FCSTD DOCUMENT  (FreeCAD 0.18.4R)
Label: SubEnclosure
License: All rights reserved
LicenseURL: http://en.wikipedia.org/wiki/All_rights_reserved
objects: Part::Feature×281, Sketcher::SketchObject×109, PartDesign::Pocket×59, PartDesign::Pad×44, PartDesign::Body×26, PartDesign::Plane×20, PartDesign::Chamfer×16, PartDesign::Mirrored×12, PartDesign::Fillet×7, PartDesign::PolarPattern×5, Part::Part2DObjectPython×4, Part::Extrusion×4, Part::Cut×4, PartDesign::Revolution×3, Part::MultiFuse×3, PartDesign::FeatureBase×2, App::DocumentObjectGroup×2, PartDesign::Line×1, Mesh::Feature×1, Part::Box×1, +1 more types
note: 708 computed .brp shape members not serialized (recipe doc carries the construction recipe); baked Part::Feature solids carry a one-line shape summary decoded from their .brp

FEATURE [Sketcher::SketchObject] Sketch
  MapMode = 5
  Support = -> [XY_Plane]
  sketch-geometry (38):
    g0: LineSegment StartX=-115 StartY=90 StartZ=0 EndX=115 EndY=90 EndZ=0
    g1: LineSegment StartX=-115 StartY=-90 StartZ=0 EndX=115 EndY=-90 EndZ=0
    g2: LineSegment StartX=120 StartY=85 StartZ=0 EndX=120 EndY=-85 EndZ=0
    g3: LineSegment StartX=-120 StartY=85 StartZ=0 EndX=-120 EndY=-85 EndZ=0
    g4: ArcOfCircle CenterX=115 CenterY=85 CenterZ=0 NormalX=0 NormalY=0 NormalZ=1 AngleXU=0 Radius=5 StartAngle=-9e-16 EndAngle=1.5708
    g5: ArcOfCircle CenterX=115 CenterY=-85 CenterZ=0 NormalX=0 NormalY=0 NormalZ=1 AngleXU=0 Radius=5 StartAngle=4.71239 EndAngle=6.28319
    g6: ArcOfCircle CenterX=-115 CenterY=-85 CenterZ=0 NormalX=0 NormalY=0 NormalZ=1 AngleXU=0 Radius=5 StartAngle=3.14159 EndAngle=4.71239
    g7: ArcOfCircle CenterX=-115 CenterY=85 CenterZ=0 NormalX=0 NormalY=0 NormalZ=1 AngleXU=0 Radius=5 StartAngle=1.5708 EndAngle=3.14159
    g8: Circle CenterX=110 CenterY=80 CenterZ=0 NormalX=0 NormalY=0 NormalZ=1 AngleXU=0 Radius=3.25
    g9: Circle CenterX=-110 CenterY=80 CenterZ=0 NormalX=0 NormalY=0 NormalZ=1 AngleXU=0 Radius=3.25
    g10: Circle CenterX=110 CenterY=-80 CenterZ=0 NormalX=0 NormalY=0 NormalZ=1 AngleXU=0 Radius=3.25
    g11: Circle CenterX=-110 CenterY=-80 CenterZ=0 NormalX=0 NormalY=0 NormalZ=1 AngleXU=0 Radius=3.25
    g12: ArcOfCircle CenterX=110 CenterY=80 CenterZ=0 NormalX=0 NormalY=0 NormalZ=1 AngleXU=0 Radius=7 StartAngle=3.43134 EndAngle=4.42264
    g13: ArcOfCircle CenterX=106 CenterY=66.5836 CenterZ=0 NormalX=0 NormalY=0 NormalZ=1 AngleXU=0 Radius=7 StartAngle=-9e-16 EndAngle=1.28104
    g14: ArcOfCircle CenterX=96.5836 CenterY=76 CenterZ=0 NormalX=0 NormalY=0 NormalZ=1 AngleXU=0 Radius=7 StartAngle=0.289752 EndAngle=1.5708
    g15: LineSegment StartX=-96.5836 StartY=83 StartZ=0 EndX=96.5836 EndY=83 EndZ=0
    g16: ArcOfCircle CenterX=110 CenterY=-80 CenterZ=0 NormalX=0 NormalY=0 NormalZ=1 AngleXU=0 Radius=7 StartAngle=1.86055 EndAngle=2.85184
    g17: ArcOfCircle CenterX=-110 CenterY=-80 CenterZ=0 NormalX=0 NormalY=0 NormalZ=1 AngleXU=0 Radius=7 StartAngle=0.289752 EndAngle=1.28104
    g18: ArcOfCircle CenterX=-110 CenterY=80 CenterZ=0 NormalX=0 NormalY=0 NormalZ=1 AngleXU=0 Radius=7 StartAngle=5.00214 EndAngle=5.99343
    g19: ArcOfCircle CenterX=-96.5836 CenterY=76 CenterZ=0 NormalX=0 NormalY=0 NormalZ=1 AngleXU=0 Radius=7 StartAngle=1.5708 EndAngle=2.85184
    g20: ArcOfCircle CenterX=106 CenterY=-66.5836 CenterZ=0 NormalX=0 NormalY=0 NormalZ=1 AngleXU=0 Radius=7 StartAngle=5.00214 EndAngle=6.28319
    g21: ArcOfCircle CenterX=96.5836 CenterY=-76 CenterZ=0 NormalX=0 NormalY=0 NormalZ=1 AngleXU=0 Radius=7 StartAngle=4.71239 EndAngle=5.99343
    g22: ArcOfCircle CenterX=-96.5836 CenterY=-76 CenterZ=0 NormalX=0 NormalY=0 NormalZ=1 AngleXU=0 Radius=7 StartAngle=3.43134 EndAngle=4.71239
    g23: ArcOfCircle CenterX=-106 CenterY=-66.5836 CenterZ=0 NormalX=0 NormalY=0 NormalZ=1 AngleXU=0 Radius=7 StartAngle=3.14159 EndAngle=4.42264
    g24: ArcOfCircle CenterX=-106 CenterY=66.5836 CenterZ=0 NormalX=0 NormalY=0 NormalZ=1 AngleXU=0 Radius=7 StartAngle=1.86055 EndAngle=3.14159
    g25: LineSegment StartX=-96.5836 StartY=-83 StartZ=0 EndX=96.5836 EndY=-83 EndZ=0
    g26: Circle CenterX=110 CenterY=0 CenterZ=0 NormalX=0 NormalY=0 NormalZ=1 AngleXU=0 Radius=3.25
    g27: Circle CenterX=-110 CenterY=0 CenterZ=0 NormalX=0 NormalY=0 NormalZ=1 AngleXU=0 Radius=3.25
    g28: ArcOfCircle CenterX=110 CenterY=0 CenterZ=0 NormalX=0 NormalY=0 NormalZ=1 AngleXU=0 Radius=7 StartAngle=1.86055 EndAngle=4.42264
    g29: ArcOfCircle CenterX=106 CenterY=-13.4164 CenterZ=0 NormalX=0 NormalY=0 NormalZ=1 AngleXU=0 Radius=7 StartAngle=0 EndAngle=1.28104
    g30: ArcOfCircle CenterX=106 CenterY=13.4164 CenterZ=0 NormalX=0 NormalY=0 NormalZ=1 AngleXU=0 Radius=7 StartAngle=5.00214 EndAngle=6.28319
    g31: ArcOfCircle CenterX=-110 CenterY=0 CenterZ=0 NormalX=0 NormalY=0 NormalZ=1 AngleXU=0 Radius=7 StartAngle=5.00214 EndAngle=7.56423
    g32: ArcOfCircle CenterX=-106 CenterY=13.4164 CenterZ=0 NormalX=0 NormalY=0 NormalZ=1 AngleXU=0 Radius=7 StartAngle=3.14159 EndAngle=4.42264
    g33: ArcOfCircle CenterX=-106 CenterY=-13.4164 CenterZ=0 NormalX=0 NormalY=0 NormalZ=1 AngleXU=0 Radius=7 StartAngle=1.86055 EndAngle=3.14159
    g34: LineSegment StartX=113 StartY=66.5836 StartZ=0 EndX=113 EndY=13.4164 EndZ=0
    g35: LineSegment StartX=113 StartY=-13.4164 StartZ=0 EndX=113 EndY=-66.5836 EndZ=0
    g36: LineSegment StartX=-113 StartY=-66.5836 StartZ=0 EndX=-113 EndY=-13.4164 EndZ=0
    g37: LineSegment StartX=-113 StartY=13.4164 StartZ=0 EndX=-113 EndY=66.5836 EndZ=0
  constraints (92):
    c: Symmetric(g0,g0,g-2)
    c: Equal(g1,g0)
    c: Symmetric(g1,g1,g-2)
    c: Symmetric(g2,g2,g-1)
    c: Symmetric(g3,g3,g-1)
    c: Equal(g3,g2)
    c: Symmetric(g0,g1,g-1)
    c: Symmetric(g2,g3,g-2)
    c: Coincident(g4,g2)
    c: Tangent(g7,g0) = 1.5708
    c: Tangent(g7,g3) = -1.5708
    c: Tangent(g0,g4) = 1.5708
    c: Coincident(g5,g1)
    c: Tangent(g5,g2) = 1.5708
    c: Coincident(g3,g6)
    c: Tangent(g6,g1) = -1.5708
    c: Distance(g3,g2) = 240
    c: Radius(g4) = 5
    c: Distance(g0,g1) = 180
    c: Diameter(g8) = 6.5
    c: DistanceY(g8,g0) = 10
    c: DistanceX(g8,g2) = 10
    c: Equal(g9,g8)
    c: Symmetric(g9,g8,g-2)
    c: Equal(g11,g10)
    c: Equal(g10,g8)
    c: Symmetric(g10,g8,g-1)
    c: Symmetric(g11,g10,g-2)
    c: Coincident(g12,g8)
    c: Tangent(g13,g12) = 1.5708
    c: Radius(g12) = 7
    c: DistanceX(g13,g2) = 7
    c: Tangent(g14,g12) = 1.5708
    c: DistanceY(g14,g0) = 7
    c: Equal(g13,g12)
    c: Equal(g12,g14)
    c: Symmetric(g15,g15,g-2)
    c: Tangent(g14,g15) = 1.5708
    c: Coincident(g16,g10)
    c: Coincident(g17,g11)
    c: Coincident(g18,g9)
    c: Equal(g16,g12)
    c: Equal(g17,g16)
    c: Equal(g18,g12)
    c: Tangent(g19,g18) = 1.5708
    c: Tangent(g19,g15) = 1.5708
    c: Tangent(g22,g17) = 1.5708
    c: Tangent(g17,g23) = 1.5708
    c: Symmetric(g13,g24,g-2)
    c: Tangent(g24,g18) = 1.5708
    c: Horizontal(g25)
    c: Tangent(g16,g20) = 1.5708
    c: Symmetric(g21,g14,g-1)
    c: Tangent(g21,g25) = -1.5708
    c: Tangent(g22,g25) = -1.5708
    c: Equal(g22,g23)
    c: Equal(g23,g21)
    c: Equal(g21,g20)
    c: Coincident(g16,g21)
    c: PointOnObject(g26,g-1)
    c: PointOnObject(g27,g-1)
    c: Equal(g27,g26)
    c: Equal(g26,g8)
    c: Vertical(g26,g8)
    c: Vertical(g27,g9)
    c: Coincident(g28,g26)
    c: Coincident(g31,g27)
    c: Vertical(g34)
    c: Vertical(g35)
    c: Equal(g34,g35)
    c: Tangent(g34,g13) = 1.5708
    c: Tangent(g35,g20) = 1.5708
    c: Tangent(g35,g29) = 1.5708
    c: Tangent(g34,g30) = 1.5708
    c: Tangent(g29,g28) = 1.5708
    c: Tangent(g28,g30) = 1.5708
    c: Equal(g28,g12)
    c: Equal(g29,g30)
    c: Equal(g30,g13)
    c: Vertical(g29,g30)
    c: Equal(g33,g29)
    c: Equal(g32,g30)
    c: Equal(g31,g28)
    c: Tangent(g32,g37) = 1.5708
    c: Vertical(g37)
    c: Tangent(g36,g33) = 1.5708
    c: Tangent(g36,g23) = 1.5708
    c: Vertical(g36)
    c: Vertical(g33,g32)
    c: Tangent(g33,g31) = 1.5708
    c: Tangent(g31,g32) = 1.5708
    c: Tangent(g37,g24) = 1.5708
FEATURE [PartDesign::Pad] Pad
  Length = 200
  Length2 = 100
  Profile = -> Sketch
  Type = 0
FEATURE [PartDesign::Line] DatumLine
  AttacherType = Attacher::AttachEngineLine
  AttachmentOffset = pos=(0,100,0) rot=(0,0,1;0rad)
  MapMode = 29
  Placement = pos=(0,2.22e-14,100) rot=(0,0.707107,0.707107;3.14159rad)
  Support = -> [Y_Axis]
FEATURE [PartDesign::Plane] DatumPlane
  Length = 284.9
  MapMode = 5
  Placement = pos=(0,-90,0) rot=(1,0,0;1.5708rad)
  ResizeMode = 0
  Support = -> [Pad]
  Width = 254.9
FEATURE [Sketcher::SketchObject] Sketch001
  ExternalGeometry = -> [Pad]
  MapMode = 5
  Placement = pos=(0,-90,0) rot=(1,0,0;1.5708rad)
  Support = -> [DatumPlane]
  sketch-geometry (7):
    g0: Circle CenterX=0 CenterY=100 CenterZ=0 NormalX=0 NormalY=0 NormalZ=1 AngleXU=0 Radius=60.5
    g1: LineSegment [constr] StartX=-48.7904 StartY=51.2096 StartZ=0 EndX=48.7904 EndY=148.79 EndZ=0
    g2: LineSegment [constr] StartX=-48.7904 StartY=148.79 StartZ=0 EndX=48.7904 EndY=51.2096 EndZ=0
    g3: Circle CenterX=-48.7904 CenterY=148.79 CenterZ=0 NormalX=0 NormalY=0 NormalZ=1 AngleXU=0 Radius=2.6
    g4: Circle CenterX=48.7904 CenterY=148.79 CenterZ=0 NormalX=0 NormalY=0 NormalZ=1 AngleXU=0 Radius=2.6
    g5: Circle CenterX=48.7904 CenterY=51.2096 CenterZ=0 NormalX=0 NormalY=0 NormalZ=1 AngleXU=0 Radius=2.6
    g6: Circle CenterX=-48.7904 CenterY=51.2096 CenterZ=0 NormalX=0 NormalY=0 NormalZ=1 AngleXU=0 Radius=2.6
  constraints (17):
    c: Diameter(g0) = 121
    c: Perpendicular(g2,g1)
    c: Symmetric(g1,g1,g0)
    c: Equal(g2,g1)
    c: Symmetric(g2,g2,g0)
    c: Angle(g-4,g1) = 0.785398
    c: Distance(g1) = 138
    c: Coincident(g3,g2)
    c: Coincident(g4,g1)
    c: Coincident(g5,g2)
    c: Coincident(g6,g1)
    c: Diameter(g6) = 5.2
    c: Equal(g3,g4)
    c: Equal(g4,g5)
    c: Equal(g5,g6)
    c: PointOnObject(g0,g-2)
    c: DistanceY(g-4,g0) = 100
FEATURE [PartDesign::Pocket] Pocket
  BaseFeature = -> Pad
  Length = 5
  Length2 = 100
  Profile = -> Sketch001
  Type = 1
FEATURE [Sketcher::SketchObject] Sketch002
  ExternalGeometry = -> [Pocket]
  MapMode = 5
  Placement = pos=(0,0,0) rot=(0.57735,0.57735,0.57735;2.0944rad)
  Support = -> [YZ_Plane]
  expr: Constraints[4] = (200 - 156) / 2
  sketch-geometry (4):
    g0: LineSegment StartX=-90 StartY=200 StartZ=0 EndX=-93.2142 EndY=188.312 EndZ=0
    g1: LineSegment StartX=-90 StartY=178 StartZ=0 EndX=-90 EndY=200 EndZ=0
    g2: LineSegment [constr] StartX=-90 StartY=178 StartZ=0 EndX=-97.6604 EndY=184.428 EndZ=0
    g3: ArcOfCircle CenterX=-83.5721 CenterY=185.66 CenterZ=0 NormalX=0 NormalY=0 NormalZ=1 AngleXU=0 Radius=10 StartAngle=2.87323 EndAngle=4.01425
  constraints (12):
    c: Coincident(g0,g1)
    c: Vertical(g1)
    c: DistanceX(g0,g-1) = 90
    c: DistanceY(g-1,g0) = 200
    c: DistanceY(g1,g1) = 22
    c: Coincident(g2,g1)
    c: Angle(g2,g-2) = 2.26893
    c: Distance(g2) = 10
    c: Coincident(g3,g1)
    c: Tangent(g3,g2)
    c: Radius(g3) = 10
    c: Tangent(g3,g0) = -1.5708
FEATURE [PartDesign::Revolution] Revolution
  Angle = 360
  Axis = (1e-16,1,-2e-16)
  Base = (0,2.22e-14,100)
  BaseFeature = -> Pocket
  Profile = -> Sketch002
  ReferenceAxis = -> DatumLine
FEATURE [PartDesign::Plane] DatumPlane001
  Length = 284.9
  MapMode = 5
  Placement = pos=(0,-83,0) rot=(0,0.707107,0.707107;3.14159rad)
  ResizeMode = 0
  Support = -> [Revolution]
  Width = 254.9
FEATURE [Sketcher::SketchObject] Sketch003
  ExternalGeometry = -> [Revolution]
  MapMode = 5
  Placement = pos=(0,-83,0) rot=(0,0.707107,0.707107;3.14159rad)
  Support = -> [DatumPlane001]
  sketch-geometry (31):
    g0: LineSegment StartX=51.2441 StartY=144.54 StartZ=0 EndX=53.6978 EndY=148.79 EndZ=0
    g1: LineSegment StartX=53.6978 StartY=148.79 StartZ=0 EndX=51.2441 EndY=153.04 EndZ=0
    g2: LineSegment StartX=51.2441 StartY=153.04 StartZ=0 EndX=46.3366 EndY=153.04 EndZ=0
    g3: LineSegment StartX=46.3366 StartY=153.04 StartZ=0 EndX=43.8829 EndY=148.79 EndZ=0
    g4: LineSegment StartX=43.8829 StartY=148.79 StartZ=0 EndX=46.3366 EndY=144.54 EndZ=0
    g5: LineSegment StartX=46.3366 StartY=144.54 StartZ=0 EndX=51.2441 EndY=144.54 EndZ=0
    g6: Circle [constr] CenterX=48.7904 CenterY=148.79 CenterZ=0 NormalX=0 NormalY=0 NormalZ=1 AngleXU=0 Radius=4.90748
    g7: LineSegment StartX=51.2441 StartY=46.9596 StartZ=0 EndX=53.6978 EndY=51.2096 EndZ=0
    g8: LineSegment StartX=53.6978 StartY=51.2096 StartZ=0 EndX=51.2441 EndY=55.4596 EndZ=0
    g9: LineSegment StartX=51.2441 StartY=55.4596 StartZ=0 EndX=46.3366 EndY=55.4596 EndZ=0
    g10: LineSegment StartX=46.3366 StartY=55.4596 StartZ=0 EndX=43.8829 EndY=51.2096 EndZ=0
    g11: LineSegment StartX=43.8829 StartY=51.2096 StartZ=0 EndX=46.3366 EndY=46.9596 EndZ=0
    g12: LineSegment StartX=46.3366 StartY=46.9596 StartZ=0 EndX=51.2441 EndY=46.9596 EndZ=0
    g13: Circle [constr] CenterX=48.7904 CenterY=51.2096 CenterZ=0 NormalX=0 NormalY=0 NormalZ=1 AngleXU=0 Radius=4.90748
    g14: LineSegment StartX=-46.3366 StartY=46.9596 StartZ=0 EndX=-43.8829 EndY=51.2096 EndZ=0
    g15: LineSegment StartX=-43.8829 StartY=51.2096 StartZ=0 EndX=-46.3366 EndY=55.4596 EndZ=0
    g16: LineSegment StartX=-46.3366 StartY=55.4596 StartZ=0 EndX=-51.2441 EndY=55.4596 EndZ=0
    g17: LineSegment StartX=-51.2441 StartY=55.4596 StartZ=0 EndX=-53.6978 EndY=51.2096 EndZ=0
    g18: LineSegment StartX=-53.6978 StartY=51.2096 StartZ=0 EndX=-51.2441 EndY=46.9596 EndZ=0
    g19: LineSegment StartX=-51.2441 StartY=46.9596 StartZ=0 EndX=-46.3366 EndY=46.9596 EndZ=0
    g20: Circle [constr] CenterX=-48.7904 CenterY=51.2096 CenterZ=0 NormalX=0 NormalY=0 NormalZ=1 AngleXU=0 Radius=4.90748
    g21: LineSegment StartX=-46.3366 StartY=144.54 StartZ=0 EndX=-43.8829 EndY=148.79 EndZ=0
    g22: LineSegment StartX=-43.8829 StartY=148.79 StartZ=0 EndX=-46.3366 EndY=153.04 EndZ=0
    g23: LineSegment StartX=-46.3366 StartY=153.04 StartZ=0 EndX=-51.2441 EndY=153.04 EndZ=0
    g24: LineSegment StartX=-51.2441 StartY=153.04 StartZ=0 EndX=-53.6978 EndY=148.79 EndZ=0
    g25: LineSegment StartX=-53.6978 StartY=148.79 StartZ=0 EndX=-51.2441 EndY=144.54 EndZ=0
    g26: LineSegment StartX=-51.2441 StartY=144.54 StartZ=0 EndX=-46.3366 EndY=144.54 EndZ=0
    g27: Circle [constr] CenterX=-48.7904 CenterY=148.79 CenterZ=0 NormalX=0 NormalY=0 NormalZ=1 AngleXU=0 Radius=4.90748
    g28: Circle CenterX=0 CenterY=100 CenterZ=0 NormalX=0 NormalY=0 NormalZ=1 AngleXU=0 Radius=60.5
    g29: Circle CenterX=0 CenterY=100 CenterZ=0 NormalX=0 NormalY=0 NormalZ=1 AngleXU=0 Radius=79
    g30: LineSegment [constr] StartX=-100 StartY=100 StartZ=0 EndX=100 EndY=100 EndZ=0
  constraints (87):
    c: Coincident(g17,g18)
    c: Coincident(g25,g24)
    c: Coincident(g18,g19)
    c: Coincident(g16,g17)
    c: Coincident(g26,g25)
    c: Coincident(g23,g24)
    c: Coincident(g19,g14)
    c: Coincident(g16,g15)
    c: Coincident(g21,g26)
    c: Coincident(g23,g22)
    c: Coincident(g14,g15)
    c: Coincident(g22,g21)
    c: Coincident(g10,g11)
    c: Coincident(g3,g4)
    c: Coincident(g11,g12)
    c: Coincident(g9,g10)
    c: Coincident(g5,g4)
    c: Coincident(g3,g2)
    c: Coincident(g7,g12)
    c: Coincident(g8,g9)
    c: Coincident(g5,g0)
    c: Coincident(g2,g1)
    c: Coincident(g7,g8)
    c: Coincident(g1,g0)
    c: Coincident(g28,g29)
    c: Coincident(g28,g-7)
    c: Equal(g28,g-7)
    c: Coincident(g6,g-8)
    c: Equal(g0,g5)
    c: Equal(g5,g4)
    c: Equal(g4,g3)
    c: Equal(g3,g2)
    c: Equal(g2,g1)
    c: Horizontal(g5)
    c: PointOnObject(g0,g6)
    c: PointOnObject(g1,g6)
    c: PointOnObject(g2,g6)
    c: PointOnObject(g3,g6)
    c: PointOnObject(g0,g6)
    c: PointOnObject(g4,g6)
    c: DistanceY(g0,g1) = 8.5
    c: Diameter(g29) = 158
    c: Equal(g27,g20)
    c: Equal(g20,g13)
    c: Equal(g13,g6)
    c: Symmetric(g27,g6,g-2)
    c: PointOnObject(g21,g27)
    c: PointOnObject(g22,g27)
    c: PointOnObject(g23,g27)
    c: PointOnObject(g24,g27)
    c: PointOnObject(g25,g27)
    c: PointOnObject(g21,g27)
    c: Horizontal(g26)
    c: Equal(g26,g25)
    c: Equal(g25,g24)
    c: Equal(g24,g23)
    c: Equal(g23,g22)
    c: Equal(g22,g21)
    c: Horizontal(g30)
    c: Symmetric(g30,g30,g28)
    c: DistanceX(g30,g30) = 200
    c: Symmetric(g13,g6,g30)
    c: PointOnObject(g7,g13)
    c: PointOnObject(g7,g13)
    c: PointOnObject(g8,g13)
    c: PointOnObject(g9,g13)
    c: PointOnObject(g10,g13)
    c: PointOnObject(g11,g13)
    c: Equal(g12,g11)
    c: Equal(g11,g10)
    c: Equal(g10,g9)
    c: Equal(g9,g8)
    c: Equal(g8,g7)
    c: Horizontal(g12)
    c: Equal(g18,g17)
    c: Equal(g17,g16)
    c: Equal(g16,g15)
    c: Equal(g15,g14)
    c: Equal(g14,g19)
    c: PointOnObject(g15,g20)
    c: PointOnObject(g14,g20)
    c: PointOnObject(g14,g20)
    c: PointOnObject(g18,g20)
    c: PointOnObject(g17,g20)
    c: PointOnObject(g16,g20)
    c: Symmetric(g20,g27,g30)
    c: Horizontal(g19)
FEATURE [PartDesign::Pad] Pad001
  BaseFeature = -> Revolution
  Length = 5
  Length2 = 100
  Profile = -> Sketch003
  Type = 0
FEATURE [PartDesign::PolarPattern] PolarPattern
  Angle = 360
  Axis = -> Z_Axis
  BaseFeature = -> Pad001
  Occurrences = 2
  Originals = -> [Pad001]
FEATURE [PartDesign::Mirrored] Mirrored
  BaseFeature = -> PolarPattern
  MirrorPlane = -> Sketch002 [V_Axis]
  Originals = -> [Revolution]
FEATURE [Sketcher::SketchObject] CopySketch005
  sketch-geometry (16):
    g0: LineSegment StartX=-115 StartY=90 StartZ=0 EndX=115 EndY=90 EndZ=0
    g1: LineSegment StartX=-115 StartY=-90 StartZ=0 EndX=115 EndY=-90 EndZ=0
    g2: LineSegment StartX=120 StartY=85 StartZ=0 EndX=120 EndY=-85 EndZ=0
    g3: LineSegment StartX=-120 StartY=85 StartZ=0 EndX=-120 EndY=-85 EndZ=0
    g4: ArcOfCircle CenterX=115 CenterY=85 CenterZ=0 NormalX=0 NormalY=0 NormalZ=1 AngleXU=0 Radius=5 StartAngle=-9e-16 EndAngle=1.5708
    g5: ArcOfCircle CenterX=115 CenterY=-85 CenterZ=0 NormalX=0 NormalY=0 NormalZ=1 AngleXU=0 Radius=5 StartAngle=4.71239 EndAngle=6.28319
    g6: ArcOfCircle CenterX=-115 CenterY=-85 CenterZ=0 NormalX=0 NormalY=0 NormalZ=1 AngleXU=0 Radius=5 StartAngle=3.14159 EndAngle=4.71239
    g7: ArcOfCircle CenterX=-115 CenterY=85 CenterZ=0 NormalX=0 NormalY=0 NormalZ=1 AngleXU=0 Radius=5 StartAngle=1.5708 EndAngle=3.14159
    g8: Circle CenterX=110 CenterY=80 CenterZ=0 NormalX=0 NormalY=0 NormalZ=1 AngleXU=0 Radius=3.25
    g9: Circle CenterX=-110 CenterY=80 CenterZ=0 NormalX=0 NormalY=0 NormalZ=1 AngleXU=0 Radius=3.25
    g10: Circle CenterX=110 CenterY=-80 CenterZ=0 NormalX=0 NormalY=0 NormalZ=1 AngleXU=0 Radius=3.25
    g11: Circle CenterX=-110 CenterY=-80 CenterZ=0 NormalX=0 NormalY=0 NormalZ=1 AngleXU=0 Radius=3.25
    g12: Circle CenterX=110 CenterY=0 CenterZ=0 NormalX=0 NormalY=0 NormalZ=1 AngleXU=0 Radius=3.25
    g13: Circle CenterX=-110 CenterY=0 CenterZ=0 NormalX=0 NormalY=0 NormalZ=1 AngleXU=0 Radius=3.25
    g14: Circle CenterX=0 CenterY=70 CenterZ=0 NormalX=0 NormalY=0 NormalZ=1 AngleXU=0 Radius=3.25
    g15: Circle CenterX=0 CenterY=-70 CenterZ=0 NormalX=0 NormalY=0 NormalZ=1 AngleXU=0 Radius=3.25
  constraints (39):
    c: Symmetric(g0,g0,g-2)
    c: Equal(g1,g0)
    c: Symmetric(g1,g1,g-2)
    c: Symmetric(g2,g2,g-1)
    c: Symmetric(g3,g3,g-1)
    c: Equal(g3,g2)
    c: Symmetric(g0,g1,g-1)
    c: Symmetric(g2,g3,g-2)
    c: Coincident(g4,g2)
    c: Tangent(g7,g0) = 1.5708
    c: Tangent(g7,g3) = -1.5708
    c: Tangent(g0,g4) = 1.5708
    c: Coincident(g5,g1)
    c: Tangent(g5,g2) = 1.5708
    c: Coincident(g3,g6)
    c: Tangent(g6,g1) = -1.5708
    c: Distance(g3,g2) = 240
    c: Radius(g4) = 5
    c: Distance(g0,g1) = 180
    c: Diameter(g8) = 6.5
    c: DistanceY(g8,g0) = 10
    c: DistanceX(g8,g2) = 10
    c: Equal(g9,g8)
    c: Symmetric(g9,g8,g-2)
    c: Equal(g11,g10)
    c: Equal(g10,g8)
    c: Symmetric(g10,g8,g-1)
    c: Symmetric(g11,g10,g-2)
    c: PointOnObject(g12,g-1)
    c: PointOnObject(g13,g-1)
    c: Equal(g13,g12)
    c: Equal(g12,g8)
    c: Vertical(g12,g8)
    c: Vertical(g13,g9)
    c: Equal(g15,g14)
    c: Equal(g14,g8)
    c: PointOnObject(g15,g-2)
    c: Symmetric(g15,g14,g-1)
    c: DistanceY(g14,g0) = 20
FEATURE [PartDesign::Pad] Pad002
  Length = 14
  Length2 = 100
  Profile = -> CopySketch005
  Reversed = true
  Type = 0
FEATURE [Sketcher::SketchObject] Sketch010
  MapMode = 5
  Support = -> [XY_Plane003]
  sketch-geometry (4):
    g0: LineSegment StartX=-50 StartY=42.5 StartZ=0 EndX=50 EndY=42.5 EndZ=0
    g1: LineSegment StartX=50 StartY=42.5 StartZ=0 EndX=50 EndY=-42.5 EndZ=0
    g2: LineSegment StartX=50 StartY=-42.5 StartZ=0 EndX=-50 EndY=-42.5 EndZ=0
    g3: LineSegment StartX=-50 StartY=-42.5 StartZ=0 EndX=-50 EndY=42.5 EndZ=0
  constraints (10):
    c: Coincident(g0,g1)
    c: Coincident(g1,g2)
    c: Coincident(g2,g3)
    c: Coincident(g3,g0)
    c: Horizontal(g2)
    c: Vertical(g3)
    c: Symmetric(g1,g0,g-1)
    c: Symmetric(g0,g0,g-2)
    c: DistanceX(g0,g0) = 100
    c: DistanceY(g1,g1) = 85
FEATURE [PartDesign::Pad] Pad006
  Length = 50
  Length2 = 100
  Profile = -> Sketch010
  Type = 0
FEATURE [Sketcher::SketchObject] Sketch011
  ExternalGeometry = -> [Pad006]
  MapMode = 5
  Placement = pos=(0,42.5,0) rot=(0,0.707107,0.707107;3.14159rad)
  Support = -> [Pad006]
  sketch-geometry (26):
    g0: Circle CenterX=-38.5 CenterY=13 CenterZ=0 NormalX=0 NormalY=0 NormalZ=1 AngleXU=0 Radius=9.25
    g1: Circle CenterX=-27.5 CenterY=32.0526 CenterZ=0 NormalX=0 NormalY=0 NormalZ=1 AngleXU=0 Radius=9.25
    g2: Circle CenterX=-16.5 CenterY=13 CenterZ=0 NormalX=0 NormalY=0 NormalZ=1 AngleXU=0 Radius=9.25
    g3: Circle CenterX=5.5 CenterY=13 CenterZ=0 NormalX=0 NormalY=0 NormalZ=1 AngleXU=0 Radius=9.25
    g4: Circle CenterX=27.5 CenterY=13 CenterZ=0 NormalX=0 NormalY=0 NormalZ=1 AngleXU=0 Radius=9.25
    g5: Circle CenterX=-5.5 CenterY=32.0526 CenterZ=0 NormalX=0 NormalY=0 NormalZ=1 AngleXU=0 Radius=9.25
    g6: Circle CenterX=16.5 CenterY=32.0526 CenterZ=0 NormalX=0 NormalY=0 NormalZ=1 AngleXU=0 Radius=9.25
    g7: Circle CenterX=38.5 CenterY=32.0526 CenterZ=0 NormalX=0 NormalY=0 NormalZ=1 AngleXU=0 Radius=9.25
    g8: LineSegment [constr] StartX=-38.5 StartY=13 StartZ=0 EndX=-16.5 EndY=13 EndZ=0
    g9: LineSegment [constr] StartX=5.5 StartY=13 StartZ=0 EndX=-16.5 EndY=13 EndZ=0
    g10: LineSegment [constr] StartX=27.5 StartY=13 StartZ=0 EndX=5.5 EndY=13 EndZ=0
    g11: LineSegment [constr] StartX=-27.5 StartY=32.0526 StartZ=0 EndX=-5.5 EndY=32.0526 EndZ=0
    g12: LineSegment [constr] StartX=-5.5 StartY=32.0526 StartZ=0 EndX=16.5 EndY=32.0526 EndZ=0
    g13: LineSegment [constr] StartX=16.5 StartY=32.0526 StartZ=0 EndX=38.5 EndY=32.0526 EndZ=0
    g14: LineSegment [constr] StartX=-16.5 StartY=13 StartZ=0 EndX=-27.5 EndY=32.0526 EndZ=0
    g15: LineSegment [constr] StartX=-27.5 StartY=32.0526 StartZ=0 EndX=-38.5 EndY=13 EndZ=0
    g16: LineSegment StartX=35 StartY=0 StartZ=0 EndX=50 EndY=25.9808 EndZ=0
    g17: LineSegment StartX=50 StartY=25.9808 StartZ=0 EndX=50 EndY=0 EndZ=0
    g18: LineSegment StartX=50 StartY=0 StartZ=0 EndX=35 EndY=0 EndZ=0
    g19: LineSegment StartX=-50 StartY=50 StartZ=0 EndX=-50 EndY=18.8231 EndZ=0
    g20: LineSegment StartX=-50 StartY=18.8231 StartZ=0 EndX=-35.4641 EndY=44 EndZ=0
    g21: LineSegment StartX=-32 StartY=50 StartZ=0 EndX=-50 EndY=50 EndZ=0
    g22: LineSegment StartX=-32 StartY=50 StartZ=0 EndX=50 EndY=50 EndZ=0
    g23: LineSegment StartX=50 StartY=50 StartZ=0 EndX=50 EndY=44 EndZ=0
    g24: LineSegment StartX=50 StartY=44 StartZ=0 EndX=-35.4641 EndY=44 EndZ=0
    g25: LineSegment [constr] StartX=-35.4641 StartY=44 StartZ=0 EndX=-32 EndY=50 EndZ=0
  constraints (67):
    c: Horizontal(g0,g2)
    c: Horizontal(g2,g3)
    c: Horizontal(g3,g4)
    c: Horizontal(g1,g5)
    c: Horizontal(g5,g6)
    c: Horizontal(g6,g7)
    c: Diameter(g0) = 18.5
    c: Equal(g2,g1)
    c: Equal(g1,g5)
    c: Equal(g5,g6)
    c: Equal(g6,g7)
    c: Equal(g7,g3)
    c: Equal(g3,g4)
    c: Equal(g4,g0)
    c: Coincident(g8,g0)
    c: Coincident(g8,g2)
    c: DistanceX(g8,g8) = 22
    c: Coincident(g9,g3)
    c: Coincident(g9,g2)
    c: Coincident(g10,g4)
    c: Coincident(g10,g3)
    c: Coincident(g11,g1)
    c: Coincident(g11,g5)
    c: Coincident(g12,g5)
    c: Coincident(g12,g6)
    c: Coincident(g13,g6)
    c: Coincident(g13,g7)
    c: Equal(g10,g13)
    c: Equal(g13,g12)
    c: Equal(g12,g11)
    c: Equal(g11,g9)
    c: Equal(g9,g8)
    c: DistanceY(g-1,g2) = 13
    c: Coincident(g14,g2)
    c: Coincident(g14,g1)
    c: Coincident(g15,g1)
    c: Coincident(g15,g0)
    c: Equal(g14,g15)
    c: Equal(g15,g8)
    c: DistanceX(g0,g-1) = 38.5
    c: PointOnObject(g16,g-1)
    c: Coincident(g17,g16)
    c: PointOnObject(g17,g-1)
    c: Vertical(g17)
    c: Coincident(g18,g17)
    c: Coincident(g18,g16)
    c: PointOnObject(g16,g-3)
    c: Parallel(g16,g15)
    c: DistanceX(g18,g18) = 15
    c: Coincident(g19,g-5)
    c: PointOnObject(g19,g-4)
    c: PointOnObject(g21,g-5)
    c: Coincident(g21,g19)
    c: Coincident(g20,g19)
    c: Parallel(g20,g15)
    c: DistanceX(g21,g21) = 18
    c: Coincident(g22,g21)
    c: Coincident(g22,g-5)
    c: Coincident(g23,g22)
    c: PointOnObject(g23,g-3)
    c: Coincident(g24,g23)
    c: Horizontal(g24)
    c: DistanceY(g23,g23) = 6
    c: Coincident(g20,g24)
    c: Coincident(g25,g20)
    c: Coincident(g25,g21)
    c: Parallel(g20,g25)
FEATURE [PartDesign::Pocket] Pocket004
  BaseFeature = -> Pad006
  Length = 5
  Length2 = 100
  Profile = -> Sketch011
  Type = 1
FEATURE [Sketcher::SketchObject] Sketch012
  ExternalGeometry = -> [Pocket004]
  MapMode = 5
  Placement = pos=(50,0,0) rot=(0.57735,0.57735,0.57735;2.0944rad)
  Support = -> [Pocket004]
  sketch-geometry (12):
    g0: LineSegment StartX=-42.5 StartY=3 StartZ=0 EndX=-27.5 EndY=3 EndZ=0
    g1: LineSegment StartX=-27.5 StartY=3 StartZ=0 EndX=-27.5 EndY=44 EndZ=0
    g2: LineSegment StartX=-27.5 StartY=44 StartZ=0 EndX=-42.5 EndY=44 EndZ=0
    g3: LineSegment StartX=-42.5 StartY=44 StartZ=0 EndX=-42.5 EndY=3 EndZ=0
    g4: LineSegment StartX=42.5 StartY=44 StartZ=0 EndX=27.5 EndY=44 EndZ=0
    g5: LineSegment StartX=27.5 StartY=44 StartZ=0 EndX=27.5 EndY=3 EndZ=0
    g6: LineSegment StartX=27.5 StartY=3 StartZ=0 EndX=42.5 EndY=3 EndZ=0
    g7: LineSegment StartX=42.5 StartY=3 StartZ=0 EndX=42.5 EndY=44 EndZ=0
    g8: LineSegment StartX=-10 StartY=44 StartZ=0 EndX=10 EndY=44 EndZ=0
    g9: LineSegment StartX=10 StartY=44 StartZ=0 EndX=10 EndY=3 EndZ=0
    g10: LineSegment StartX=10 StartY=3 StartZ=0 EndX=-10 EndY=3 EndZ=0
    g11: LineSegment StartX=-10 StartY=3 StartZ=0 EndX=-10 EndY=44 EndZ=0
  constraints (31):
    c: PointOnObject(g0,g-3)
    c: Horizontal(g0)
    c: Coincident(g1,g0)
    c: PointOnObject(g1,g-5)
    c: Vertical(g1)
    c: Coincident(g2,g1)
    c: Coincident(g2,g-5)
    c: Coincident(g3,g2)
    c: Coincident(g3,g0)
    c: DistanceX(g2,g2) = 15
    c: DistanceY(g-3,g0) = 3
    c: Coincident(g4,g5)
    c: Coincident(g5,g6)
    c: Coincident(g6,g7)
    c: Coincident(g7,g4)
    c: Horizontal(g6)
    c: Vertical(g7)
    c: Coincident(g4,g-7)
    c: Symmetric(g4,g1,g-2)
    c: Symmetric(g5,g0,g-2)
    c: Coincident(g8,g9)
    c: Coincident(g9,g10)
    c: Coincident(g10,g11)
    c: Coincident(g11,g8)
    c: Horizontal(g8)
    c: Vertical(g9)
    c: Vertical(g11)
    c: PointOnObject(g8,g-5)
    c: Symmetric(g9,g10,g-2)
    c: Horizontal(g9,g6)
    c: DistanceX(g8,g8) = 20
FEATURE [PartDesign::Pocket] Pocket005
  BaseFeature = -> Pocket004
  Length = 5
  Length2 = 100
  Profile = -> Sketch012
  Type = 1
FEATURE [Sketcher::SketchObject] Sketch013
  ExternalGeometry = -> [Pocket005]
  MapMode = 5
  Placement = pos=(0,0,3) rot=(0,0,1;0rad)
  Support = -> [Pocket005]
  sketch-geometry (14):
    g0: Circle CenterX=-31.7321 CenterY=37.5 CenterZ=0 NormalX=0 NormalY=0 NormalZ=1 AngleXU=0 Radius=2.25
    g1: Circle CenterX=31.7321 CenterY=37.5 CenterZ=0 NormalX=0 NormalY=0 NormalZ=1 AngleXU=0 Radius=2.25
    g2: Circle CenterX=31.7321 CenterY=-37.5 CenterZ=0 NormalX=0 NormalY=0 NormalZ=1 AngleXU=0 Radius=2.25
    g3: Circle CenterX=-31.7321 CenterY=-37.5 CenterZ=0 NormalX=0 NormalY=0 NormalZ=1 AngleXU=0 Radius=2.25
    g4: LineSegment StartX=50 StartY=42.5 StartZ=0 EndX=36.7321 EndY=42.5 EndZ=0
    g5: LineSegment StartX=36.7321 StartY=42.5 StartZ=0 EndX=36.7321 EndY=27.5 EndZ=0
    g6: LineSegment StartX=36.7321 StartY=27.5 StartZ=0 EndX=50 EndY=27.5 EndZ=0
    g7: LineSegment StartX=50 StartY=27.5 StartZ=0 EndX=50 EndY=42.5 EndZ=0
    g8: LineSegment StartX=50 StartY=-42.5 StartZ=0 EndX=36.7321 EndY=-42.5 EndZ=0
    g9: LineSegment StartX=36.7321 StartY=-42.5 StartZ=0 EndX=36.7321 EndY=-27.5 EndZ=0
    g10: LineSegment StartX=36.7321 StartY=-27.5 StartZ=0 EndX=50 EndY=-27.5 EndZ=0
    g11: LineSegment StartX=50 StartY=-27.5 StartZ=0 EndX=50 EndY=-42.5 EndZ=0
    g12: Circle CenterX=0 CenterY=55 CenterZ=0 NormalX=0 NormalY=0 NormalZ=1 AngleXU=0 Radius=27.5
    g13: Circle CenterX=0 CenterY=-55 CenterZ=0 NormalX=0 NormalY=0 NormalZ=1 AngleXU=0 Radius=27.5
  constraints (34):
    c: Symmetric(g3,g2,g-2)
    c: Symmetric(g0,g1,g-2)
    c: Symmetric(g2,g1,g-1)
    c: DistanceY(g0,g-3) = 5
    c: Diameter(g1) = 4.5
    c: Equal(g3,g0)
    c: Equal(g0,g2)
    c: Equal(g2,g1)
    c: DistanceX(g-5,g0) = 5
    c: Coincident(g4,g5)
    c: Coincident(g5,g6)
    c: Coincident(g6,g7)
    c: Coincident(g7,g4)
    c: Horizontal(g4)
    c: Horizontal(g6)
    c: Vertical(g5)
    c: Vertical(g7)
    c: Coincident(g4,g-3)
    c: DistanceX(g1,g4) = 5
    c: PointOnObject(g5,g-6)
    c: Coincident(g8,g9)
    c: Coincident(g9,g10)
    c: Coincident(g10,g11)
    c: Coincident(g11,g8)
    c: Horizontal(g10)
    c: Vertical(g9)
    c: Coincident(g8,g-4)
    c: Symmetric(g10,g6,g-1)
    c: Symmetric(g8,g4,g-1)
    c: PointOnObject(g12,g-2)
    c: Diameter(g12) = 55
    c: Tangent(g12,g-6)
    c: Equal(g13,g12)
    c: Symmetric(g13,g12,g-1)
FEATURE [PartDesign::Pocket] Pocket006
  BaseFeature = -> Pocket005
  Length = 5
  Length2 = 100
  Profile = -> Sketch013
  Type = 0
FEATURE [PartDesign::Fillet] Fillet
  Base = -> Pocket006 [Edge126,Edge78,Edge72,Edge68,Edge112,Edge80,Edge52,Edge48]
  BaseFeature = -> Pocket006
  Radius = 5
FEATURE [PartDesign::Fillet] Fillet001
  Base = -> Fillet [Edge28,Edge31,Edge35,Edge4]
  BaseFeature = -> Fillet
  Radius = 1
FEATURE [PartDesign::Fillet] Fillet002
  Base = -> Fillet001 [Edge188,Edge190,Edge191,Edge192,Edge195,Edge194,Edge193,Edge189,Edge215,Edge214,Edge213,Edge209,Edge208,Edge212,Edge211,Edge210,Edge20,Edge19,Edge18,Edge14,Edge13,Edge15,Edge16,Edge17,Edge67,Edge61,Edge59,Edge57,Edge53,Edge55,Edge63,Edge65]
  BaseFeature = -> Fillet001
  Radius = 1
FEATURE [PartDesign::Fillet] Fillet003
  Base = -> Fillet002 [Edge133,Edge98,Edge134,Edge149,Edge189,Edge190,Edge194,Edge157]
  BaseFeature = -> Fillet002
  Radius = 2
FEATURE [PartDesign::Body] Body003  label="LiPoHolder"
  Group = -> [Sketch010,Pad006,Sketch011,Pocket004,Sketch012,Pocket005,Sketch013,Pocket006,Fillet,Fillet001,Fillet002,Fillet003]
  Origin = -> Origin003
  Placement = pos=(55,30,207) rot=(0,0,1;1.5708rad)
  Tip = -> Fillet003
FEATURE [Sketcher::SketchObject] Sketch014
  ExternalGeometry = -> [Sketch]
  MapMode = 5
  Support = -> [XY_Plane]
  sketch-geometry (10):
    g0: LineSegment StartX=-7 StartY=83 StartZ=0 EndX=7 EndY=83 EndZ=0
    g1: LineSegment StartX=7 StartY=83 StartZ=0 EndX=7 EndY=63 EndZ=0
    g2: LineSegment StartX=7 StartY=63 StartZ=0 EndX=-7 EndY=63 EndZ=0
    g3: LineSegment StartX=-7 StartY=63 StartZ=0 EndX=-7 EndY=83 EndZ=0
    g4: Circle CenterX=0 CenterY=70 CenterZ=0 NormalX=0 NormalY=0 NormalZ=1 AngleXU=0 Radius=3.25
    g5: LineSegment StartX=-7 StartY=-83 StartZ=0 EndX=7 EndY=-83 EndZ=0
    g6: LineSegment StartX=7 StartY=-83 StartZ=0 EndX=7 EndY=-63 EndZ=0
    g7: LineSegment StartX=7 StartY=-63 StartZ=0 EndX=-7 EndY=-63 EndZ=0
    g8: LineSegment StartX=-7 StartY=-63 StartZ=0 EndX=-7 EndY=-83 EndZ=0
    g9: Circle CenterX=0 CenterY=-70 CenterZ=0 NormalX=0 NormalY=0 NormalZ=1 AngleXU=0 Radius=3.25
  constraints (25):
    c: Coincident(g0,g1)
    c: Coincident(g1,g2)
    c: Coincident(g2,g3)
    c: Coincident(g3,g0)
    c: Horizontal(g2)
    c: Vertical(g1)
    c: Vertical(g3)
    c: PointOnObject(g0,g-3)
    c: Symmetric(g0,g0,g-2)
    c: PointOnObject(g4,g-2)
    c: Diameter(g4) = 6.5
    c: DistanceX(g2,g2) = 14
    c: DistanceY(g1,g4) = 7
    c: DistanceY(g1,g1) = 20
    c: Coincident(g5,g6)
    c: Coincident(g6,g7)
    c: Coincident(g7,g8)
    c: Coincident(g8,g5)
    c: Horizontal(g5)
    c: Vertical(g8)
    c: Symmetric(g6,g7,g-2)
    c: Symmetric(g9,g4,g-1)
    c: Equal(g9,g4)
    c: Symmetric(g6,g1,g-1)
    c: Symmetric(g5,g0,g-1)
FEATURE [PartDesign::Pad] Pad007
  BaseFeature = -> Mirrored
  Length = 10
  Length2 = 100
  Profile = -> Sketch014
  Type = 0
FEATURE [Sketcher::SketchObject] Sketch015
  ExternalGeometry = -> [Pad002]
  MapMode = 5
  Support = -> [Pad002]
  sketch-geometry (24):
    g0: LineSegment StartX=7 StartY=83 StartZ=0 EndX=96 EndY=83 EndZ=0
    g1: LineSegment StartX=96 StartY=83 StartZ=0 EndX=113 EndY=66 EndZ=0
    g2: LineSegment StartX=113 StartY=66 StartZ=0 EndX=113 EndY=7 EndZ=0
    g3: LineSegment StartX=113 StartY=7 StartZ=0 EndX=104 EndY=7 EndZ=0
    g4: LineSegment StartX=104 StartY=7 StartZ=0 EndX=104 EndY=-7 EndZ=0
    g5: LineSegment StartX=104 StartY=-7 StartZ=0 EndX=113 EndY=-7 EndZ=0
    g6: LineSegment StartX=113 StartY=-7 StartZ=0 EndX=113 EndY=-66 EndZ=0
    g7: LineSegment StartX=113 StartY=-66 StartZ=0 EndX=96 EndY=-83 EndZ=0
    g8: LineSegment StartX=96 StartY=-83 StartZ=0 EndX=7 EndY=-83 EndZ=0
    g9: LineSegment StartX=7 StartY=-83 StartZ=0 EndX=7 EndY=-63 EndZ=0
    g10: LineSegment StartX=7 StartY=-63 StartZ=0 EndX=-7 EndY=-63 EndZ=0
    g11: LineSegment StartX=-7 StartY=-63 StartZ=0 EndX=-7 EndY=-83 EndZ=0
    g12: LineSegment StartX=-7 StartY=-83 StartZ=0 EndX=-96 EndY=-83 EndZ=0
    g13: LineSegment StartX=-96 StartY=-83 StartZ=0 EndX=-113 EndY=-66 EndZ=0
    g14: LineSegment StartX=-113 StartY=-66 StartZ=0 EndX=-113 EndY=-7 EndZ=0
    g15: LineSegment StartX=-113 StartY=-7 StartZ=0 EndX=-104 EndY=-7 EndZ=0
    g16: LineSegment StartX=-104 StartY=-7 StartZ=0 EndX=-104 EndY=7 EndZ=0
    g17: LineSegment StartX=-104 StartY=7 StartZ=0 EndX=-113 EndY=7 EndZ=0
    g18: LineSegment StartX=-113 StartY=7 StartZ=0 EndX=-113 EndY=66 EndZ=0
    g19: LineSegment StartX=-113 StartY=66 StartZ=0 EndX=-96 EndY=83 EndZ=0
    g20: LineSegment StartX=-96 StartY=83 StartZ=0 EndX=-7 EndY=83 EndZ=0
    g21: LineSegment StartX=-7 StartY=83 StartZ=0 EndX=-7 EndY=63 EndZ=0
    g22: LineSegment StartX=-7 StartY=63 StartZ=0 EndX=7 EndY=63 EndZ=0
    g23: LineSegment StartX=7 StartY=63 StartZ=0 EndX=7 EndY=83 EndZ=0
  constraints (62):
    c: Horizontal(g0)
    c: Coincident(g1,g0)
    c: Coincident(g2,g1)
    c: Vertical(g2)
    c: Coincident(g3,g2)
    c: Horizontal(g3)
    c: Coincident(g4,g3)
    c: Coincident(g5,g4)
    c: Coincident(g6,g5)
    c: Vertical(g6)
    c: Coincident(g7,g6)
    c: Coincident(g8,g7)
    c: Horizontal(g8)
    c: Coincident(g9,g8)
    c: Coincident(g10,g9)
    c: Coincident(g11,g10)
    c: Vertical(g11)
    c: Coincident(g12,g11)
    c: Horizontal(g12)
    c: Coincident(g13,g12)
    c: Coincident(g14,g13)
    c: Vertical(g14)
    c: Coincident(g15,g14)
    c: Horizontal(g15)
    c: Coincident(g16,g15)
    c: Vertical(g16)
    c: Coincident(g17,g16)
    c: Coincident(g18,g17)
    c: Coincident(g19,g18)
    c: Coincident(g20,g19)
    c: Coincident(g21,g20)
    c: Vertical(g21)
    c: Coincident(g22,g21)
    c: Horizontal(g22)
    c: Coincident(g23,g22)
    c: Coincident(g23,g0)
    c: Angle(g-3,g1) = 2.35619
    c: DistanceY(g0,g-3) = 7
    c: DistanceX(g1,g-4) = 7
    c: Symmetric(g20,g0,g-2)
    c: Vertical(g23)
    c: DistanceX(g-1,g0) = 7
    c: DistanceY(g23,g23) = 20
    c: Symmetric(g19,g0,g-2)
    c: Symmetric(g18,g1,g-2)
    c: DistanceX(g0,g0) = 89
    c: Equal(g4,g10)
    c: Equal(g10,g16)
    c: Equal(g16,g22)
    c: Horizontal(g5)
    c: Horizontal(g17)
    c: Symmetric(g14,g17,g-1)
    c: Symmetric(g4,g3,g-1)
    c: DistanceX(g3,g-4) = 16
    c: Symmetric(g6,g1,g-1)
    c: Vertical(g9)
    c: Symmetric(g9,g10,g-2)
    c: Equal(g9,g23)
    c: Symmetric(g13,g6,g-2)
    c: Symmetric(g12,g7,g-2)
    c: Symmetric(g7,g0,g-1)
    c: Equal(g17,g3)
FEATURE [PartDesign::Pocket] Pocket007
  BaseFeature = -> Pad002
  Length = 10
  Length2 = 100
  Profile = -> Sketch015
  Type = 0
FEATURE [Sketcher::SketchObject] Sketch016
  ExternalGeometry = -> [Pocket007]
  MapMode = 5
  Placement = pos=(0,0,-10) rot=(0,0,1;0rad)
  Support = -> [Pocket007]
  sketch-geometry (100):
    g0: LineSegment StartX=-113 StartY=56 StartZ=0 EndX=-86 EndY=83 EndZ=0
    g1: LineSegment StartX=-83 StartY=83 StartZ=0 EndX=-113 EndY=53 EndZ=0
    g2: LineSegment StartX=-73 StartY=83 StartZ=0 EndX=-113 EndY=43 EndZ=0
    g3: LineSegment StartX=-113 StartY=40 StartZ=0 EndX=-70 EndY=83 EndZ=0
    g4: LineSegment StartX=-60 StartY=83 StartZ=0 EndX=-113 EndY=30 EndZ=0
    g5: LineSegment [constr] StartX=-96 StartY=83 StartZ=0 EndX=-86 EndY=83 EndZ=0
    g6: LineSegment StartX=-86 StartY=83 StartZ=0 EndX=-83 EndY=83 EndZ=0
    g7: LineSegment [constr] StartX=-83 StartY=83 StartZ=0 EndX=-73 EndY=83 EndZ=0
    g8: LineSegment StartX=-73 StartY=83 StartZ=0 EndX=-70 EndY=83 EndZ=0
    g9: LineSegment StartX=-113 StartY=56 StartZ=0 EndX=-113 EndY=53 EndZ=0
    g10: LineSegment StartX=-113 StartY=40 StartZ=0 EndX=-113 EndY=43 EndZ=0
    g11: LineSegment [constr] StartX=-60 StartY=83 StartZ=0 EndX=-70 EndY=83 EndZ=0
    g12: LineSegment StartX=-113 StartY=27 StartZ=0 EndX=-57 EndY=83 EndZ=0
    g13: LineSegment StartX=-60 StartY=83 StartZ=0 EndX=-57 EndY=83 EndZ=0
    g14: LineSegment StartX=-113 StartY=27 StartZ=0 EndX=-113 EndY=30 EndZ=0
    g15: LineSegment StartX=-113 StartY=17 StartZ=0 EndX=-47 EndY=83 EndZ=0
    g16: LineSegment StartX=-44 StartY=83 StartZ=0 EndX=-113 EndY=14 EndZ=0
    g17: LineSegment StartX=-113 StartY=14 StartZ=0 EndX=-113 EndY=17 EndZ=0
    g18: LineSegment StartX=-44 StartY=83 StartZ=0 EndX=-47 EndY=83 EndZ=0
    g19: LineSegment [constr] StartX=-57 StartY=83 StartZ=0 EndX=-47 EndY=83 EndZ=0
    g20: LineSegment StartX=-34 StartY=83 StartZ=0 EndX=-110 EndY=7 EndZ=0
    g21: LineSegment StartX=-31 StartY=83 StartZ=0 EndX=-107 EndY=7 EndZ=0
    g22: LineSegment StartX=-31 StartY=83 StartZ=0 EndX=-34 EndY=83 EndZ=0
    g23: LineSegment [constr] StartX=-44 StartY=83 StartZ=0 EndX=-34 EndY=83 EndZ=0
    g24: LineSegment StartX=-110 StartY=7 StartZ=0 EndX=-107 EndY=7 EndZ=0
    g25: LineSegment StartX=-21 StartY=83 StartZ=0 EndX=-104 EndY=4.832e-13 EndZ=0
    g26: LineSegment StartX=-18 StartY=83 StartZ=0 EndX=-104 EndY=-3 EndZ=0
    g27: LineSegment StartX=-21 StartY=83 StartZ=0 EndX=-18 EndY=83 EndZ=0
    g28: LineSegment [constr] StartX=-21 StartY=83 StartZ=0 EndX=-31 EndY=83 EndZ=0
    g29: LineSegment StartX=-8 StartY=83 StartZ=0 EndX=-113 EndY=-22 EndZ=0
    g30: LineSegment StartX=-7 StartY=81 StartZ=0 EndX=-113 EndY=-25 EndZ=0
    g31: LineSegment [constr] StartX=-18 StartY=83 StartZ=0 EndX=-8 EndY=83 EndZ=0
    g32: LineSegment StartX=-104 StartY=-3 StartZ=0 EndX=-104 EndY=4.832e-13 EndZ=0
    g33: LineSegment StartX=-113 StartY=-25 StartZ=0 EndX=-113 EndY=-22 EndZ=0
    g34: LineSegment [constr] StartX=-113 StartY=17 StartZ=0 EndX=-113 EndY=27 EndZ=0
    g35: LineSegment StartX=-113 StartY=-35 StartZ=0 EndX=-7 EndY=71 EndZ=0
    g36: LineSegment StartX=-7 StartY=68 StartZ=0 EndX=-113 EndY=-38 EndZ=0
    g37: LineSegment StartX=-113 StartY=-38 StartZ=0 EndX=-113 EndY=-35 EndZ=0
    g38: LineSegment [constr] StartX=-113 StartY=-25 StartZ=0 EndX=-113 EndY=-35 EndZ=0
    g39: LineSegment StartX=-7 StartY=71 StartZ=0 EndX=-7 EndY=68 EndZ=0
    g40: LineSegment StartX=-113 StartY=-48 StartZ=0 EndX=-2 EndY=63 EndZ=0
    g41: LineSegment StartX=-113 StartY=-51 StartZ=0 EndX=0 EndY=62 EndZ=0
    g42: LineSegment StartX=-113 StartY=-61 StartZ=0 EndX=0 EndY=52 EndZ=0
    g43: LineSegment StartX=-113 StartY=-64 StartZ=0 EndX=0 EndY=49 EndZ=0
    g44: LineSegment StartX=-109 StartY=-70 StartZ=0 EndX=0 EndY=39 EndZ=0
    g45: LineSegment StartX=-107.5 StartY=-71.5 StartZ=0 EndX=0 EndY=36 EndZ=0
    g46: LineSegment StartX=-102.5 StartY=-76.5 StartZ=0 EndX=0 EndY=26 EndZ=0
    g47: LineSegment StartX=-101 StartY=-78 StartZ=0 EndX=0 EndY=23 EndZ=0
    g48: LineSegment StartX=-96 StartY=-83 StartZ=0 EndX=0 EndY=13 EndZ=0
    g49: LineSegment StartX=-113 StartY=-51 StartZ=0 EndX=-113 EndY=-48 EndZ=0
    g50: LineSegment [constr] StartX=-113 StartY=-48 StartZ=0 EndX=-113 EndY=-38 EndZ=0
    g51: LineSegment [constr] StartX=-113 StartY=-61 StartZ=0 EndX=-113 EndY=-51 EndZ=0
    g52: LineSegment StartX=-113 StartY=-64 StartZ=0 EndX=-113 EndY=-61 EndZ=0
    g53: LineSegment StartX=-2 StartY=63 StartZ=0 EndX=0 EndY=63 EndZ=0
    g54: LineSegment StartX=0 StartY=63 StartZ=0 EndX=0 EndY=62 EndZ=0
    g55: LineSegment [constr] StartX=0 StartY=52 StartZ=0 EndX=0 EndY=62 EndZ=0
    g56: LineSegment [constr] StartX=0 StartY=39 StartZ=0 EndX=0 EndY=49 EndZ=0
    g57: LineSegment StartX=0 StartY=49 StartZ=0 EndX=0 EndY=52 EndZ=0
    g58: LineSegment StartX=0 StartY=36 StartZ=0 EndX=0 EndY=39 EndZ=0
    g59: LineSegment StartX=0 StartY=23 StartZ=0 EndX=0 EndY=26 EndZ=0
    g60: LineSegment StartX=-107.5 StartY=-71.5 StartZ=0 EndX=-109 EndY=-70 EndZ=0
    g61: LineSegment StartX=-101 StartY=-78 StartZ=0 EndX=-102.5 EndY=-76.5 EndZ=0
    g62: LineSegment [constr] StartX=0 StartY=26 StartZ=0 EndX=0 EndY=36 EndZ=0
    g63: LineSegment [constr] StartX=0 StartY=13 StartZ=0 EndX=0 EndY=23 EndZ=0
    g64: LineSegment StartX=-93 StartY=-83 StartZ=0 EndX=0 EndY=10 EndZ=0
    g65: LineSegment StartX=-83 StartY=-83 StartZ=0 EndX=0 EndY=2.7e-13 EndZ=0
    g66: LineSegment StartX=-80 StartY=-83 StartZ=0 EndX=0 EndY=-3 EndZ=0
    g67: LineSegment StartX=-70 StartY=-83 StartZ=0 EndX=0 EndY=-13 EndZ=0
    g68: LineSegment StartX=-67 StartY=-83 StartZ=0 EndX=0 EndY=-16 EndZ=0
    g69: LineSegment StartX=-57 StartY=-83 StartZ=0 EndX=0 EndY=-26 EndZ=0
    g70: LineSegment [constr] StartX=0 StartY=2.7e-13 StartZ=0 EndX=0 EndY=10 EndZ=0
    g71: LineSegment [constr] StartX=0 StartY=-13 StartZ=0 EndX=0 EndY=-3 EndZ=0
    g72: LineSegment [constr] StartX=0 StartY=-16 StartZ=0 EndX=0 EndY=-26 EndZ=0
    g73: LineSegment StartX=0 StartY=-16 StartZ=0 EndX=0 EndY=-13 EndZ=0
    g74: LineSegment StartX=0 StartY=-3 StartZ=0 EndX=0 EndY=2.7e-13 EndZ=0
    g75: LineSegment StartX=0 StartY=10 StartZ=0 EndX=0 EndY=13 EndZ=0
    g76: LineSegment StartX=-67 StartY=-83 StartZ=0 EndX=-70 EndY=-83 EndZ=0
    g77: LineSegment StartX=-80 StartY=-83 StartZ=0 EndX=-83 EndY=-83 EndZ=0
    g78: LineSegment StartX=-93 StartY=-83 StartZ=0 EndX=-96 EndY=-83 EndZ=0
    g79: LineSegment StartX=-54 StartY=-83 StartZ=0 EndX=0 EndY=-29 EndZ=0
    g80: LineSegment StartX=0 StartY=-39 StartZ=0 EndX=-44 EndY=-83 EndZ=0
    g81: LineSegment StartX=-41 StartY=-83 StartZ=0 EndX=0 EndY=-42 EndZ=0
    g82: LineSegment StartX=-31 StartY=-83 StartZ=0 EndX=0 EndY=-52 EndZ=0
    g83: LineSegment StartX=-28 StartY=-83 StartZ=0 EndX=-3.6e-15 EndY=-55 EndZ=0
    g84: LineSegment StartX=0 StartY=-42 StartZ=0 EndX=0 EndY=-39 EndZ=0
    g85: LineSegment StartX=-3.6e-15 StartY=-55 StartZ=0 EndX=0 EndY=-52 EndZ=0
    g86: LineSegment StartX=0 StartY=-29 StartZ=0 EndX=0 EndY=-26 EndZ=0
    g87: LineSegment [constr] StartX=0 StartY=-52 StartZ=0 EndX=0 EndY=-42 EndZ=0
    g88: LineSegment [constr] StartX=0 StartY=-39 StartZ=0 EndX=0 EndY=-29 EndZ=0
    g89: LineSegment StartX=-57 StartY=-83 StartZ=0 EndX=-54 EndY=-83 EndZ=0
    g90: LineSegment StartX=-44 StartY=-83 StartZ=0 EndX=-41 EndY=-83 EndZ=0
    g91: LineSegment StartX=-31 StartY=-83 StartZ=0 EndX=-28 EndY=-83 EndZ=0
    g92: LineSegment StartX=-18 StartY=-83 StartZ=0 EndX=-7 EndY=-72 EndZ=0
    g93: LineSegment StartX=-15 StartY=-83 StartZ=0 EndX=-7 EndY=-75 EndZ=0
    g94: LineSegment StartX=-7 StartY=-75 StartZ=0 EndX=-7 EndY=-72 EndZ=0
    g95: LineSegment StartX=-15 StartY=-83 StartZ=0 EndX=-18 EndY=-83 EndZ=0
    g96: LineSegment [constr] StartX=-41 StartY=-83 StartZ=0 EndX=-31 EndY=-83 EndZ=0
    g97: LineSegment [constr] StartX=-28 StartY=-83 StartZ=0 EndX=-18 EndY=-83 EndZ=0
    g98: LineSegment StartX=-8 StartY=83 StartZ=0 EndX=-7 EndY=83 EndZ=0
    g99: LineSegment StartX=-7 StartY=81 StartZ=0 EndX=-7 EndY=83 EndZ=0
  constraints (277):
    c: PointOnObject(g0,g-4)
    c: PointOnObject(g0,g-3)
    c: PointOnObject(g1,g-3)
    c: PointOnObject(g1,g-4)
    c: PointOnObject(g2,g-3)
    c: PointOnObject(g2,g-4)
    c: PointOnObject(g3,g-4)
    c: PointOnObject(g3,g-3)
    c: PointOnObject(g4,g-3)
    c: Parallel(g0,g1)
    c: Parallel(g1,g2)
    c: Parallel(g2,g3)
    c: Parallel(g3,g4)
    c: Coincident(g5,g-9)
    c: Coincident(g5,g0)
    c: DistanceX(g5,g5) = 10
    c: Coincident(g6,g0)
    c: Coincident(g6,g1)
    c: DistanceX(g6,g6) = 3
    c: Coincident(g7,g1)
    c: Coincident(g7,g2)
    c: Coincident(g8,g2)
    c: Coincident(g8,g3)
    c: Equal(g7,g5)
    c: Equal(g6,g8)
    c: Parallel(g0,g-9)
    c: PointOnObject(g4,g-4)
    c: Coincident(g9,g0)
    c: Coincident(g9,g1)
    c: Coincident(g10,g3)
    c: Coincident(g10,g2)
    c: Coincident(g11,g4)
    c: Coincident(g11,g3)
    c: Equal(g11,g7)
    c: PointOnObject(g12,g-4)
    c: PointOnObject(g12,g-3)
    c: Coincident(g13,g4)
    c: Coincident(g13,g12)
    c: Coincident(g14,g12)
    c: Coincident(g14,g4)
    c: Equal(g13,g8)
    c: Parallel(g4,g12)
    c: PointOnObject(g15,g-4)
    c: PointOnObject(g15,g-3)
    c: PointOnObject(g16,g-3)
    c: PointOnObject(g16,g-4)
    c: Coincident(g17,g16)
    c: Coincident(g17,g15)
    c: Coincident(g18,g16)
    c: Coincident(g18,g15)
    c: Equal(g18,g13)
    c: Parallel(g15,g16)
    c: Coincident(g19,g12)
    c: Coincident(g19,g15)
    c: Equal(g19,g11)
    c: Parallel(g15,g12)
    c: PointOnObject(g20,g-3)
    c: PointOnObject(g21,g-3)
    c: Coincident(g22,g21)
    c: Coincident(g22,g20)
    c: Equal(g22,g18)
    c: Parallel(g20,g21)
    c: Parallel(g21,g16)
    c: Coincident(g23,g16)
    c: Coincident(g23,g20)
    c: Equal(g23,g19)
    c: PointOnObject(g20,g-5)
    c: PointOnObject(g21,g-5)
    c: Coincident(g24,g20)
    c: Coincident(g24,g21)
    c: PointOnObject(g25,g-3)
    c: PointOnObject(g26,g-3)
    c: Coincident(g27,g25)
    c: Coincident(g27,g26)
    c: Coincident(g28,g25)
    c: Coincident(g28,g21)
    c: PointOnObject(g29,g-3)
    c: Equal(g28,g23)
    c: Equal(g27,g22)
    c: Parallel(g25,g26)
    c: Parallel(g26,g29)
    c: Parallel(g29,g30)
    c: Parallel(g30,g21)
    c: PointOnObject(g25,g-6)
    c: PointOnObject(g26,g-6)
    c: Coincident(g31,g26)
    c: Coincident(g31,g29)
    c: Equal(g31,g28)
    c: PointOnObject(g30,g-10)
    c: PointOnObject(g29,g-8)
    c: PointOnObject(g30,g-8)
    c: Coincident(g32,g26)
    c: Coincident(g32,g25)
    c: Coincident(g33,g30)
    c: Coincident(g33,g29)
    c: Equal(g33,g32)
    c: Coincident(g34,g15)
    c: Coincident(g34,g12)
    c: PointOnObject(g35,g-10)
    c: PointOnObject(g36,g-8)
    c: Parallel(g36,g35)
    c: Parallel(g35,g30)
    c: Coincident(g37,g36)
    c: Coincident(g37,g35)
    c: Vertical(g37)
    c: Equal(g37,g33)
    c: Coincident(g38,g30)
    c: Coincident(g38,g35)
    c: Equal(g38,g34)
    c: PointOnObject(g36,g-10)
    c: Coincident(g39,g35)
    c: Coincident(g39,g36)
    c: PointOnObject(g40,g-8)
    c: PointOnObject(g40,g-11)
    c: PointOnObject(g41,g-8)
    c: PointOnObject(g42,g-8)
    c: Parallel(g41,g40)
    c: Parallel(g40,g36)
    c: Coincident(g49,g40)
    c: Equal(g49,g37)
    c: Coincident(g50,g40)
    c: Coincident(g50,g36)
    c: Equal(g50,g38)
    c: Coincident(g41,g49)
    c: Coincident(g51,g42)
    c: Coincident(g51,g41)
    c: Equal(g51,g50)
    c: Parallel(g43,g42)
    c: Parallel(g42,g41)
    c: PointOnObject(g43,g-8)
    c: Coincident(g52,g43)
    c: Coincident(g52,g42)
    c: Equal(g52,g49)
    c: Parallel(g44,g45)
    c: Parallel(g45,g46)
    c: Parallel(g46,g47)
    c: Parallel(g47,g48)
    c: Parallel(g48,g43)
    c: PointOnObject(g44,g-12)
    c: PointOnObject(g45,g-12)
    c: PointOnObject(g41,g-2)
    c: Coincident(g53,g40)
    c: Horizontal(g53)
    c: Coincident(g54,g53)
    c: Coincident(g54,g41)
    c: PointOnObject(g53,g-2)
    c: PointOnObject(g42,g-2)
    c: PointOnObject(g43,g-2)
    c: PointOnObject(g44,g-2)
    c: PointOnObject(g45,g-2)
    c: Coincident(g55,g42)
    c: Coincident(g55,g41)
    c: Coincident(g56,g44)
    c: Coincident(g56,g43)
    c: Equal(g55,g56)
    c: Coincident(g57,g43)
    c: Coincident(g57,g42)
    c: Coincident(g45,g58)
    c: Coincident(g58,g44)
    c: Equal(g58,g57)
    c: PointOnObject(g46,g-2)
    c: PointOnObject(g47,g-2)
    c: Coincident(g59,g47)
    c: Coincident(g59,g46)
    c: Equal(g59,g58)
    c: PointOnObject(g46,g-12)
    c: PointOnObject(g47,g-12)
    c: Coincident(g60,g45)
    c: Coincident(g60,g44)
    c: Coincident(g61,g47)
    c: Coincident(g61,g46)
    c: PointOnObject(g48,g-2)
    c: Coincident(g62,g46)
    c: Coincident(g62,g45)
    c: Coincident(g63,g48)
    c: Coincident(g63,g47)
    c: Equal(g63,g62)
    c: Equal(g62,g56)
    c: PointOnObject(g48,g-12)
    c: PointOnObject(g64,g-13)
    c: PointOnObject(g64,g-2)
    c: PointOnObject(g65,g-13)
    c: PointOnObject(g65,g-2)
    c: PointOnObject(g66,g-13)
    c: PointOnObject(g66,g-2)
    c: PointOnObject(g67,g-13)
    c: PointOnObject(g68,g-13)
    c: PointOnObject(g68,g-2)
    c: PointOnObject(g69,g-2)
    c: Parallel(g48,g64)
    c: Parallel(g64,g65)
    c: Parallel(g65,g66)
    c: Parallel(g66,g67)
    c: Parallel(g67,g68)
    c: Parallel(g68,g69)
    c: Coincident(g70,g65)
    c: Coincident(g70,g64)
    c: Coincident(g71,g67)
    c: Coincident(g71,g66)
    c: Vertical(g71)
    c: Coincident(g72,g68)
    c: Coincident(g72,g69)
    c: Coincident(g73,g68)
    c: Coincident(g73,g67)
    c: Coincident(g74,g66)
    c: Coincident(g74,g65)
    c: Coincident(g75,g64)
    c: Coincident(g75,g48)
    c: Equal(g73,g74)
    c: Equal(g74,g75)
    c: Equal(g75,g59)
    c: Equal(g72,g71)
    c: Equal(g71,g70)
    c: Equal(g70,g63)
    c: PointOnObject(g69,g-13)
    c: Coincident(g76,g68)
    c: Coincident(g76,g67)
    c: Coincident(g77,g66)
    c: Coincident(g77,g65)
    c: Coincident(g78,g64)
    c: Coincident(g78,g48)
    c: PointOnObject(g79,g-13)
    c: PointOnObject(g79,g-2)
    c: PointOnObject(g80,g-2)
    c: PointOnObject(g80,g-13)
    c: PointOnObject(g81,g-2)
    c: PointOnObject(g82,g-13)
    c: PointOnObject(g82,g-2)
    c: PointOnObject(g83,g-13)
    c: PointOnObject(g83,g-2)
    c: Coincident(g84,g81)
    c: Coincident(g84,g80)
    c: Coincident(g85,g83)
    c: Coincident(g85,g82)
    c: Coincident(g86,g79)
    c: Coincident(g86,g69)
    c: Equal(g85,g84)
    c: Equal(g84,g86)
    c: Equal(g86,g73)
    c: Coincident(g87,g82)
    c: Coincident(g87,g81)
    c: Coincident(g88,g80)
    c: Coincident(g88,g79)
    c: Equal(g87,g88)
    c: Equal(g88,g72)
    c: Parallel(g80,g81)
    c: Parallel(g81,g82)
    c: Parallel(g82,g83)
    c: Parallel(g83,g66)
    c: PointOnObject(g81,g-13)
    c: Parallel(g79,g69)
    c: Coincident(g89,g69)
    c: Coincident(g89,g79)
    c: Coincident(g90,g80)
    c: Coincident(g90,g81)
    c: Coincident(g91,g82)
    c: Coincident(g91,g83)
    c: PointOnObject(g92,g-13)
    c: PointOnObject(g93,g-13)
    c: PointOnObject(g93,g-14)
    c: Coincident(g94,g92)
    c: Vertical(g94)
    c: Coincident(g95,g93)
    c: Coincident(g95,g92)
    c: Parallel(g92,g93)
    c: Parallel(g93,g83)
    c: Coincident(g93,g94)
    c: Equal(g95,g91)
    c: Coincident(g96,g81)
    c: Coincident(g96,g82)
    c: Coincident(g97,g83)
    c: Coincident(g97,g92)
    c: Equal(g97,g96)
    c: Coincident(g98,g29)
    c: Coincident(g98,g-10)
    c: Coincident(g99,g30)
    c: Coincident(g99,g98)
FEATURE [PartDesign::Pad] Pad008
  BaseFeature = -> Pocket007
  Length = 7
  Length2 = 100
  Profile = -> Sketch016
  Type = 0
FEATURE [PartDesign::Mirrored] Mirrored002
  BaseFeature = -> Pad008
  MirrorPlane = -> Sketch016 [V_Axis]
  Originals = -> [Pad008]
FEATURE [PartDesign::Body] Body001  label="SubEnclosureBottom"
  Group = -> [Pad002,Sketch015,Pocket007,Sketch016,Pad008,Mirrored002]
  Origin = -> Origin001
  Placement = pos=(0,0,-14) rot=(1,0,0;3.14159rad)
  Tip = -> Mirrored002
FEATURE [PartDesign::Plane] DatumPlane003
  AttachmentOffset = pos=(0,0,100) rot=(0,0,1;0rad)
  Length = 282.384
  MapMode = 2
  Placement = pos=(0,0,100) rot=(0,0,1;0rad)
  ResizeMode = 0
  Support = -> [XY_Plane]
  Width = 229.512
FEATURE [PartDesign::Mirrored] Mirrored003
  BaseFeature = -> Pad007
  MirrorPlane = -> DatumPlane003
  Originals = -> [Pad007]
FEATURE [PartDesign::Plane] DatumPlane004
  AttachmentOffset = pos=(0,0,120) rot=(0,0,1;0rad)
  Length = 226.775
  MapMode = 5
  Placement = pos=(120,-2.66e-14,2.66e-14) rot=(0.57735,0.57735,0.57735;2.0944rad)
  ResizeMode = 0
  Support = -> [YZ_Plane]
  Width = 249.647
FEATURE [Sketcher::SketchObject] Sketch017
  MapMode = 5
  Placement = pos=(120,-2.66e-14,2.66e-14) rot=(0.57735,0.57735,0.57735;2.0944rad)
  Support = -> [DatumPlane004]
  sketch-geometry (34):
    g0: LineSegment StartX=-80 StartY=0 StartZ=0 EndX=80 EndY=40 EndZ=0
    g1: LineSegment [constr] StartX=80 StartY=40 StartZ=0 EndX=80 EndY=0 EndZ=0
    g2: LineSegment [constr] StartX=-80 StartY=0 StartZ=0 EndX=-80 EndY=200 EndZ=0
    g3: LineSegment StartX=-80 StartY=20 StartZ=0 EndX=80 EndY=60 EndZ=0
    g4: LineSegment StartX=-80 StartY=40 StartZ=0 EndX=80 EndY=80 EndZ=0
    g5: LineSegment StartX=-80 StartY=60 StartZ=0 EndX=80 EndY=100 EndZ=0
    g6: LineSegment StartX=-80 StartY=80 StartZ=0 EndX=80 EndY=120 EndZ=0
    g7: LineSegment StartX=-80 StartY=100 StartZ=0 EndX=80 EndY=140 EndZ=0
    g8: LineSegment StartX=-80 StartY=120 StartZ=0 EndX=80 EndY=160 EndZ=0
    g9: LineSegment StartX=-80 StartY=140 StartZ=0 EndX=80 EndY=180 EndZ=0
    g10: LineSegment StartX=80 StartY=20 StartZ=0 EndX=0 EndY=0 EndZ=0
    g11: LineSegment [constr] StartX=80 StartY=40 StartZ=0 EndX=80 EndY=60 EndZ=0
    g12: LineSegment [constr] StartX=80 StartY=60 StartZ=0 EndX=80 EndY=80 EndZ=0
    g13: LineSegment [constr] StartX=80 StartY=80 StartZ=0 EndX=80 EndY=100 EndZ=0
    g14: LineSegment [constr] StartX=80 StartY=100 StartZ=0 EndX=80 EndY=120 EndZ=0
    g15: LineSegment [constr] StartX=80 StartY=120 StartZ=0 EndX=80 EndY=140 EndZ=0
    g16: LineSegment [constr] StartX=80 StartY=140 StartZ=0 EndX=80 EndY=160 EndZ=0
    g17: LineSegment [constr] StartX=80 StartY=160 StartZ=0 EndX=80 EndY=180 EndZ=0
    g18: LineSegment [constr] StartX=-80 StartY=200 StartZ=0 EndX=80 EndY=200 EndZ=0
    g19: LineSegment [constr] StartX=80 StartY=200 StartZ=0 EndX=80 EndY=180 EndZ=0
    g20: LineSegment StartX=-80 StartY=160 StartZ=0 EndX=80 EndY=200 EndZ=0
    g21: LineSegment StartX=-80 StartY=180 StartZ=0 EndX=0 EndY=200 EndZ=0
    g22: LineSegment StartX=0 StartY=200 StartZ=0 EndX=-80 EndY=200 EndZ=0
    g23: LineSegment StartX=-80 StartY=200 StartZ=0 EndX=-80 EndY=180 EndZ=0
    g24: LineSegment StartX=80 StartY=200 StartZ=0 EndX=80 EndY=180 EndZ=0
    g25: LineSegment StartX=-80 StartY=160 StartZ=0 EndX=-80 EndY=140 EndZ=0
    g26: LineSegment StartX=-80 StartY=120 StartZ=0 EndX=-80 EndY=100 EndZ=0
    g27: LineSegment StartX=80 StartY=160 StartZ=0 EndX=80 EndY=140 EndZ=0
    g28: LineSegment StartX=80 StartY=120 StartZ=0 EndX=80 EndY=100 EndZ=0
    g29: LineSegment StartX=80 StartY=80 StartZ=0 EndX=80 EndY=60 EndZ=0
    g30: LineSegment StartX=80 StartY=40 StartZ=0 EndX=80 EndY=20 EndZ=0
    g31: LineSegment StartX=0 StartY=0 StartZ=0 EndX=-80 EndY=0 EndZ=0
    g32: LineSegment StartX=-80 StartY=20 StartZ=0 EndX=-80 EndY=40 EndZ=0
    g33: LineSegment StartX=-80 StartY=60 StartZ=0 EndX=-80 EndY=80 EndZ=0
  constraints (90):
    c: PointOnObject(g0,g-1)
    c: DistanceY(g-1,g0) = 40
    c: Coincident(g1,g0)
    c: Vertical(g1)
    c: Symmetric(g0,g1,g-2)
    c: DistanceX(g-1,g1) = 80
    c: Coincident(g2,g0)
    c: Vertical(g2)
    c: DistanceY(g2,g2) = 200
    c: PointOnObject(g3,g2)
    c: PointOnObject(g4,g2)
    c: PointOnObject(g5,g2)
    c: PointOnObject(g6,g2)
    c: PointOnObject(g7,g2)
    c: PointOnObject(g8,g2)
    c: PointOnObject(g9,g2)
    c: PointOnObject(g10,g1)
    c: Coincident(g10,g-1)
    c: Parallel(g10,g0)
    c: Coincident(g11,g0)
    c: Coincident(g11,g3)
    c: Vertical(g11)
    c: DistanceY(g11,g11) = 20
    c: Coincident(g12,g3)
    c: Coincident(g12,g4)
    c: Vertical(g12)
    c: Coincident(g13,g4)
    c: Coincident(g13,g5)
    c: Coincident(g14,g5)
    c: Coincident(g14,g6)
    c: Vertical(g14)
    c: Coincident(g15,g6)
    c: Coincident(g15,g7)
    c: Coincident(g16,g7)
    c: Coincident(g16,g8)
    c: Vertical(g13)
    c: Vertical(g15)
    c: Vertical(g16)
    c: Equal(g16,g15)
    c: Equal(g15,g14)
    c: Equal(g14,g13)
    c: Equal(g13,g12)
    c: Equal(g12,g11)
    c: Parallel(g8,g7)
    c: Parallel(g7,g6)
    c: Parallel(g6,g5)
    c: Parallel(g5,g4)
    c: Parallel(g4,g3)
    c: Parallel(g3,g0)
    c: Parallel(g9,g8)
    c: Coincident(g17,g8)
    c: Coincident(g17,g9)
    c: Vertical(g17)
    c: Equal(g17,g16)
    c: Coincident(g18,g2)
    c: Coincident(g19,g9)
    c: Vertical(g19)
    c: Equal(g19,g17)
    c: Coincident(g18,g19)
    c: PointOnObject(g20,g2)
    c: Coincident(g20,g18)
    c: PointOnObject(g21,g2)
    c: PointOnObject(g21,g18)
    c: PointOnObject(g21,g-2)
    c: Parallel(g21,g20)
    c: Parallel(g20,g9)
    c: Coincident(g22,g21)
    c: Coincident(g22,g2)
    c: Coincident(g23,g21)
    c: Coincident(g23,g22)
    c: Coincident(g24,g20)
    c: Coincident(g24,g9)
    c: Coincident(g25,g20)
    c: Coincident(g25,g9)
    c: Coincident(g26,g7)
    c: Coincident(g26,g8)
    c: Coincident(g27,g8)
    c: Coincident(g27,g7)
    c: Coincident(g28,g6)
    c: Coincident(g28,g5)
    c: Coincident(g29,g4)
    c: Coincident(g29,g3)
    c: Coincident(g30,g0)
    c: Coincident(g30,g10)
    c: Coincident(g31,g10)
    c: Coincident(g31,g0)
    c: Coincident(g32,g3)
    c: Coincident(g32,g4)
    c: Coincident(g33,g5)
    c: Coincident(g33,g6)
FEATURE [PartDesign::Pocket] Pocket008
  BaseFeature = -> Mirrored003
  Length = 1.2
  Length2 = 100
  Profile = -> Sketch017
  Type = 0
FEATURE [PartDesign::PolarPattern] PolarPattern001
  Angle = 360
  Axis = -> Z_Axis
  BaseFeature = -> Pocket008
  Occurrences = 2
  Originals = -> [Pocket008]
FEATURE [PartDesign::Chamfer] Chamfer
  Base = -> PolarPattern001 [Edge210,Edge188]
  BaseFeature = -> PolarPattern001
  Size = 4.99
FEATURE [PartDesign::Fillet] Fillet004
  Base = -> Chamfer [Edge224,Edge356,Edge361,Edge226,Edge11,Edge135,Edge129,Edge9,Edge222,Edge355,Edge350,Edge220,Edge5,Edge72,Edge66,Edge3]
  BaseFeature = -> Chamfer
  Radius = 3
FEATURE [PartDesign::Body] Body  label="SubEnclosure"
  Group = -> [Sketch,Pad,DatumLine,DatumPlane,Sketch001,Pocket,Sketch002,Revolution,DatumPlane001,Sketch003,Pad001,PolarPattern,Mirrored,Sketch014,Pad007,DatumPlane003,Mirrored003,DatumPlane004,Sketch017,Pocket008,PolarPattern001,Chamfer,Fillet004]
  Origin = -> Origin
  Placement = pos=(0,0,200) rot=(0,1,0;3.14159rad)
  Tip = -> Fillet004
FEATURE [Sketcher::SketchObject] CopySketch007
  sketch-geometry (16):
    g0: LineSegment StartX=-115 StartY=90 StartZ=0 EndX=115 EndY=90 EndZ=0
    g1: LineSegment StartX=-115 StartY=-90 StartZ=0 EndX=115 EndY=-90 EndZ=0
    g2: LineSegment StartX=120 StartY=85 StartZ=0 EndX=120 EndY=-85 EndZ=0
    g3: LineSegment StartX=-120 StartY=85 StartZ=0 EndX=-120 EndY=-85 EndZ=0
    g4: ArcOfCircle CenterX=115 CenterY=85 CenterZ=0 NormalX=0 NormalY=0 NormalZ=1 AngleXU=0 Radius=5 StartAngle=-9e-16 EndAngle=1.5708
    g5: ArcOfCircle CenterX=115 CenterY=-85 CenterZ=0 NormalX=0 NormalY=0 NormalZ=1 AngleXU=0 Radius=5 StartAngle=4.71239 EndAngle=6.28319
    g6: ArcOfCircle CenterX=-115 CenterY=-85 CenterZ=0 NormalX=0 NormalY=0 NormalZ=1 AngleXU=0 Radius=5 StartAngle=3.14159 EndAngle=4.71239
    g7: ArcOfCircle CenterX=-115 CenterY=85 CenterZ=0 NormalX=0 NormalY=0 NormalZ=1 AngleXU=0 Radius=5 StartAngle=1.5708 EndAngle=3.14159
    g8: Circle CenterX=110 CenterY=80 CenterZ=0 NormalX=0 NormalY=0 NormalZ=1 AngleXU=0 Radius=3.25
    g9: Circle CenterX=-110 CenterY=80 CenterZ=0 NormalX=0 NormalY=0 NormalZ=1 AngleXU=0 Radius=3.25
    g10: Circle CenterX=110 CenterY=-80 CenterZ=0 NormalX=0 NormalY=0 NormalZ=1 AngleXU=0 Radius=3.25
    g11: Circle CenterX=-110 CenterY=-80 CenterZ=0 NormalX=0 NormalY=0 NormalZ=1 AngleXU=0 Radius=3.25
    g12: Circle CenterX=110 CenterY=0 CenterZ=0 NormalX=0 NormalY=0 NormalZ=1 AngleXU=0 Radius=3.25
    g13: Circle CenterX=-110 CenterY=0 CenterZ=0 NormalX=0 NormalY=0 NormalZ=1 AngleXU=0 Radius=3.25
    g14: Circle CenterX=0 CenterY=70 CenterZ=0 NormalX=0 NormalY=0 NormalZ=1 AngleXU=0 Radius=3.25
    g15: Circle CenterX=0 CenterY=-70 CenterZ=0 NormalX=0 NormalY=0 NormalZ=1 AngleXU=0 Radius=3.25
  constraints (39):
    c: Symmetric(g0,g0,g-2)
    c: Equal(g1,g0)
    c: Symmetric(g1,g1,g-2)
    c: Symmetric(g2,g2,g-1)
    c: Symmetric(g3,g3,g-1)
    c: Equal(g3,g2)
    c: Symmetric(g0,g1,g-1)
    c: Symmetric(g2,g3,g-2)
    c: Coincident(g4,g2)
    c: Tangent(g7,g0) = 1.5708
    c: Tangent(g7,g3) = -1.5708
    c: Tangent(g0,g4) = 1.5708
    c: Coincident(g5,g1)
    c: Tangent(g5,g2) = 1.5708
    c: Coincident(g3,g6)
    c: Tangent(g6,g1) = -1.5708
    c: Distance(g3,g2) = 240
    c: Radius(g4) = 5
    c: Distance(g0,g1) = 180
    c: Diameter(g8) = 6.5
    c: DistanceY(g8,g0) = 10
    c: DistanceX(g8,g2) = 10
    c: Equal(g9,g8)
    c: Symmetric(g9,g8,g-2)
    c: Equal(g11,g10)
    c: Equal(g10,g8)
    c: Symmetric(g10,g8,g-1)
    c: Symmetric(g11,g10,g-2)
    c: PointOnObject(g12,g-1)
    c: PointOnObject(g13,g-1)
    c: Equal(g13,g12)
    c: Equal(g12,g8)
    c: Vertical(g12,g8)
    c: Vertical(g13,g9)
    c: Equal(g15,g14)
    c: Equal(g14,g8)
    c: PointOnObject(g15,g-2)
    c: Symmetric(g15,g14,g-1)
    c: DistanceY(g14,g0) = 20
FEATURE [PartDesign::Pad] Pad009
  Length = 7
  Length2 = 100
  Profile = -> CopySketch007
  Reversed = true
  Type = 0
FEATURE [Sketcher::SketchObject] Sketch018
  ExternalGeometry = -> [Pad009]
  MapMode = 5
  Support = -> [Pad009]
  sketch-geometry (24):
    g0: LineSegment StartX=7 StartY=83 StartZ=0 EndX=96 EndY=83 EndZ=0
    g1: LineSegment StartX=96 StartY=83 StartZ=0 EndX=113 EndY=66 EndZ=0
    g2: LineSegment StartX=113 StartY=66 StartZ=0 EndX=113 EndY=7 EndZ=0
    g3: LineSegment StartX=113 StartY=7 StartZ=0 EndX=104 EndY=7 EndZ=0
    g4: LineSegment StartX=104 StartY=7 StartZ=0 EndX=104 EndY=-7 EndZ=0
    g5: LineSegment StartX=104 StartY=-7 StartZ=0 EndX=113 EndY=-7 EndZ=0
    g6: LineSegment StartX=113 StartY=-7 StartZ=0 EndX=113 EndY=-66 EndZ=0
    g7: LineSegment StartX=113 StartY=-66 StartZ=0 EndX=96 EndY=-83 EndZ=0
    g8: LineSegment StartX=96 StartY=-83 StartZ=0 EndX=7 EndY=-83 EndZ=0
    g9: LineSegment StartX=7 StartY=-83 StartZ=0 EndX=7 EndY=-63 EndZ=0
    g10: LineSegment StartX=7 StartY=-63 StartZ=0 EndX=-7 EndY=-63 EndZ=0
    g11: LineSegment StartX=-7 StartY=-63 StartZ=0 EndX=-7 EndY=-83 EndZ=0
    g12: LineSegment StartX=-7 StartY=-83 StartZ=0 EndX=-96 EndY=-83 EndZ=0
    g13: LineSegment StartX=-96 StartY=-83 StartZ=0 EndX=-113 EndY=-66 EndZ=0
    g14: LineSegment StartX=-113 StartY=-66 StartZ=0 EndX=-113 EndY=-7 EndZ=0
    g15: LineSegment StartX=-113 StartY=-7 StartZ=0 EndX=-104 EndY=-7 EndZ=0
    g16: LineSegment StartX=-104 StartY=-7 StartZ=0 EndX=-104 EndY=7 EndZ=0
    g17: LineSegment StartX=-104 StartY=7 StartZ=0 EndX=-113 EndY=7 EndZ=0
    g18: LineSegment StartX=-113 StartY=7 StartZ=0 EndX=-113 EndY=66 EndZ=0
    g19: LineSegment StartX=-113 StartY=66 StartZ=0 EndX=-96 EndY=83 EndZ=0
    g20: LineSegment StartX=-96 StartY=83 StartZ=0 EndX=-7 EndY=83 EndZ=0
    g21: LineSegment StartX=-7 StartY=83 StartZ=0 EndX=-7 EndY=63 EndZ=0
    g22: LineSegment StartX=-7 StartY=63 StartZ=0 EndX=7 EndY=63 EndZ=0
    g23: LineSegment StartX=7 StartY=63 StartZ=0 EndX=7 EndY=83 EndZ=0
  constraints (62):
    c: Horizontal(g0)
    c: Coincident(g1,g0)
    c: Coincident(g2,g1)
    c: Vertical(g2)
    c: Coincident(g3,g2)
    c: Horizontal(g3)
    c: Coincident(g4,g3)
    c: Coincident(g5,g4)
    c: Coincident(g6,g5)
    c: Vertical(g6)
    c: Coincident(g7,g6)
    c: Coincident(g8,g7)
    c: Horizontal(g8)
    c: Coincident(g9,g8)
    c: Coincident(g10,g9)
    c: Coincident(g11,g10)
    c: Vertical(g11)
    c: Coincident(g12,g11)
    c: Horizontal(g12)
    c: Coincident(g13,g12)
    c: Coincident(g14,g13)
    c: Vertical(g14)
    c: Coincident(g15,g14)
    c: Horizontal(g15)
    c: Coincident(g16,g15)
    c: Vertical(g16)
    c: Coincident(g17,g16)
    c: Coincident(g18,g17)
    c: Coincident(g19,g18)
    c: Coincident(g20,g19)
    c: Coincident(g21,g20)
    c: Vertical(g21)
    c: Coincident(g22,g21)
    c: Horizontal(g22)
    c: Coincident(g23,g22)
    c: Coincident(g23,g0)
    c: Angle(g-3,g1) = 2.35619
    c: DistanceY(g0,g-3) = 7
    c: DistanceX(g1,g-4) = 7
    c: Symmetric(g20,g0,g-2)
    c: Vertical(g23)
    c: DistanceX(g-1,g0) = 7
    c: DistanceY(g23,g23) = 20
    c: Symmetric(g19,g0,g-2)
    c: Symmetric(g18,g1,g-2)
    c: DistanceX(g0,g0) = 89
    c: Equal(g4,g10)
    c: Equal(g10,g16)
    c: Equal(g16,g22)
    c: Horizontal(g5)
    c: Horizontal(g17)
    c: Symmetric(g14,g17,g-1)
    c: Symmetric(g4,g3,g-1)
    c: DistanceX(g3,g-4) = 16
    c: Symmetric(g6,g1,g-1)
    c: Vertical(g9)
    c: Symmetric(g9,g10,g-2)
    c: Equal(g9,g23)
    c: Symmetric(g13,g6,g-2)
    c: Symmetric(g12,g7,g-2)
    c: Symmetric(g7,g0,g-1)
    c: Equal(g17,g3)
FEATURE [PartDesign::Pocket] Pocket009
  BaseFeature = -> Pad009
  Length = 5
  Length2 = 100
  Profile = -> Sketch018
  Type = 0
FEATURE [Sketcher::SketchObject] Sketch019
  ExternalGeometry = -> [Pocket009]
  MapMode = 5
  Placement = pos=(0,0,-5) rot=(0,0,1;0rad)
  Support = -> [Pocket009]
  sketch-geometry (100):
    g0: LineSegment StartX=-113 StartY=56 StartZ=0 EndX=-86 EndY=83 EndZ=0
    g1: LineSegment StartX=-83 StartY=83 StartZ=0 EndX=-113 EndY=53 EndZ=0
    g2: LineSegment StartX=-73 StartY=83 StartZ=0 EndX=-113 EndY=43 EndZ=0
    g3: LineSegment StartX=-113 StartY=40 StartZ=0 EndX=-70 EndY=83 EndZ=0
    g4: LineSegment StartX=-60 StartY=83 StartZ=0 EndX=-113 EndY=30 EndZ=0
    g5: LineSegment [constr] StartX=-96 StartY=83 StartZ=0 EndX=-86 EndY=83 EndZ=0
    g6: LineSegment StartX=-86 StartY=83 StartZ=0 EndX=-83 EndY=83 EndZ=0
    g7: LineSegment [constr] StartX=-83 StartY=83 StartZ=0 EndX=-73 EndY=83 EndZ=0
    g8: LineSegment StartX=-73 StartY=83 StartZ=0 EndX=-70 EndY=83 EndZ=0
    g9: LineSegment StartX=-113 StartY=56 StartZ=0 EndX=-113 EndY=53 EndZ=0
    g10: LineSegment StartX=-113 StartY=40 StartZ=0 EndX=-113 EndY=43 EndZ=0
    g11: LineSegment [constr] StartX=-60 StartY=83 StartZ=0 EndX=-70 EndY=83 EndZ=0
    g12: LineSegment StartX=-113 StartY=27 StartZ=0 EndX=-57 EndY=83 EndZ=0
    g13: LineSegment StartX=-60 StartY=83 StartZ=0 EndX=-57 EndY=83 EndZ=0
    g14: LineSegment StartX=-113 StartY=27 StartZ=0 EndX=-113 EndY=30 EndZ=0
    g15: LineSegment StartX=-113 StartY=17 StartZ=0 EndX=-47 EndY=83 EndZ=0
    g16: LineSegment StartX=-44 StartY=83 StartZ=0 EndX=-113 EndY=14 EndZ=0
    g17: LineSegment StartX=-113 StartY=14 StartZ=0 EndX=-113 EndY=17 EndZ=0
    g18: LineSegment StartX=-44 StartY=83 StartZ=0 EndX=-47 EndY=83 EndZ=0
    g19: LineSegment [constr] StartX=-57 StartY=83 StartZ=0 EndX=-47 EndY=83 EndZ=0
    g20: LineSegment StartX=-34 StartY=83 StartZ=0 EndX=-110 EndY=7 EndZ=0
    g21: LineSegment StartX=-31 StartY=83 StartZ=0 EndX=-107 EndY=7 EndZ=0
    g22: LineSegment StartX=-31 StartY=83 StartZ=0 EndX=-34 EndY=83 EndZ=0
    g23: LineSegment [constr] StartX=-44 StartY=83 StartZ=0 EndX=-34 EndY=83 EndZ=0
    g24: LineSegment StartX=-110 StartY=7 StartZ=0 EndX=-107 EndY=7 EndZ=0
    g25: LineSegment StartX=-21 StartY=83 StartZ=0 EndX=-104 EndY=4.832e-13 EndZ=0
    g26: LineSegment StartX=-18 StartY=83 StartZ=0 EndX=-104 EndY=-3 EndZ=0
    g27: LineSegment StartX=-21 StartY=83 StartZ=0 EndX=-18 EndY=83 EndZ=0
    g28: LineSegment [constr] StartX=-21 StartY=83 StartZ=0 EndX=-31 EndY=83 EndZ=0
    g29: LineSegment StartX=-8 StartY=83 StartZ=0 EndX=-113 EndY=-22 EndZ=0
    g30: LineSegment StartX=-7 StartY=81 StartZ=0 EndX=-113 EndY=-25 EndZ=0
    g31: LineSegment [constr] StartX=-18 StartY=83 StartZ=0 EndX=-8 EndY=83 EndZ=0
    g32: LineSegment StartX=-104 StartY=-3 StartZ=0 EndX=-104 EndY=4.832e-13 EndZ=0
    g33: LineSegment StartX=-113 StartY=-25 StartZ=0 EndX=-113 EndY=-22 EndZ=0
    g34: LineSegment [constr] StartX=-113 StartY=17 StartZ=0 EndX=-113 EndY=27 EndZ=0
    g35: LineSegment StartX=-113 StartY=-35 StartZ=0 EndX=-7 EndY=71 EndZ=0
    g36: LineSegment StartX=-7 StartY=68 StartZ=0 EndX=-113 EndY=-38 EndZ=0
    g37: LineSegment StartX=-113 StartY=-38 StartZ=0 EndX=-113 EndY=-35 EndZ=0
    g38: LineSegment [constr] StartX=-113 StartY=-25 StartZ=0 EndX=-113 EndY=-35 EndZ=0
    g39: LineSegment StartX=-7 StartY=71 StartZ=0 EndX=-7 EndY=68 EndZ=0
    g40: LineSegment StartX=-113 StartY=-48 StartZ=0 EndX=-2 EndY=63 EndZ=0
    g41: LineSegment StartX=-113 StartY=-51 StartZ=0 EndX=0 EndY=62 EndZ=0
    g42: LineSegment StartX=-113 StartY=-61 StartZ=0 EndX=0 EndY=52 EndZ=0
    g43: LineSegment StartX=-113 StartY=-64 StartZ=0 EndX=0 EndY=49 EndZ=0
    g44: LineSegment StartX=-109 StartY=-70 StartZ=0 EndX=0 EndY=39 EndZ=0
    g45: LineSegment StartX=-107.5 StartY=-71.5 StartZ=0 EndX=0 EndY=36 EndZ=0
    g46: LineSegment StartX=-102.5 StartY=-76.5 StartZ=0 EndX=0 EndY=26 EndZ=0
    g47: LineSegment StartX=-101 StartY=-78 StartZ=0 EndX=0 EndY=23 EndZ=0
    g48: LineSegment StartX=-96 StartY=-83 StartZ=0 EndX=0 EndY=13 EndZ=0
    g49: LineSegment StartX=-113 StartY=-51 StartZ=0 EndX=-113 EndY=-48 EndZ=0
    g50: LineSegment [constr] StartX=-113 StartY=-48 StartZ=0 EndX=-113 EndY=-38 EndZ=0
    g51: LineSegment [constr] StartX=-113 StartY=-61 StartZ=0 EndX=-113 EndY=-51 EndZ=0
    g52: LineSegment StartX=-113 StartY=-64 StartZ=0 EndX=-113 EndY=-61 EndZ=0
    g53: LineSegment StartX=-2 StartY=63 StartZ=0 EndX=0 EndY=63 EndZ=0
    g54: LineSegment StartX=0 StartY=63 StartZ=0 EndX=0 EndY=62 EndZ=0
    g55: LineSegment [constr] StartX=0 StartY=52 StartZ=0 EndX=0 EndY=62 EndZ=0
    g56: LineSegment [constr] StartX=0 StartY=39 StartZ=0 EndX=0 EndY=49 EndZ=0
    g57: LineSegment StartX=0 StartY=49 StartZ=0 EndX=0 EndY=52 EndZ=0
    g58: LineSegment StartX=0 StartY=36 StartZ=0 EndX=0 EndY=39 EndZ=0
    g59: LineSegment StartX=0 StartY=23 StartZ=0 EndX=0 EndY=26 EndZ=0
    g60: LineSegment StartX=-107.5 StartY=-71.5 StartZ=0 EndX=-109 EndY=-70 EndZ=0
    g61: LineSegment StartX=-101 StartY=-78 StartZ=0 EndX=-102.5 EndY=-76.5 EndZ=0
    g62: LineSegment [constr] StartX=0 StartY=26 StartZ=0 EndX=0 EndY=36 EndZ=0
    g63: LineSegment [constr] StartX=0 StartY=13 StartZ=0 EndX=0 EndY=23 EndZ=0
    g64: LineSegment StartX=-93 StartY=-83 StartZ=0 EndX=0 EndY=10 EndZ=0
    g65: LineSegment StartX=-83 StartY=-83 StartZ=0 EndX=0 EndY=2.7e-13 EndZ=0
    g66: LineSegment StartX=-80 StartY=-83 StartZ=0 EndX=0 EndY=-3 EndZ=0
    g67: LineSegment StartX=-70 StartY=-83 StartZ=0 EndX=0 EndY=-13 EndZ=0
    g68: LineSegment StartX=-67 StartY=-83 StartZ=0 EndX=0 EndY=-16 EndZ=0
    g69: LineSegment StartX=-57 StartY=-83 StartZ=0 EndX=0 EndY=-26 EndZ=0
    g70: LineSegment [constr] StartX=0 StartY=2.7e-13 StartZ=0 EndX=0 EndY=10 EndZ=0
    g71: LineSegment [constr] StartX=0 StartY=-13 StartZ=0 EndX=0 EndY=-3 EndZ=0
    g72: LineSegment [constr] StartX=0 StartY=-16 StartZ=0 EndX=0 EndY=-26 EndZ=0
    g73: LineSegment StartX=0 StartY=-16 StartZ=0 EndX=0 EndY=-13 EndZ=0
    g74: LineSegment StartX=0 StartY=-3 StartZ=0 EndX=0 EndY=2.7e-13 EndZ=0
    g75: LineSegment StartX=0 StartY=10 StartZ=0 EndX=0 EndY=13 EndZ=0
    g76: LineSegment StartX=-67 StartY=-83 StartZ=0 EndX=-70 EndY=-83 EndZ=0
    g77: LineSegment StartX=-80 StartY=-83 StartZ=0 EndX=-83 EndY=-83 EndZ=0
    g78: LineSegment StartX=-93 StartY=-83 StartZ=0 EndX=-96 EndY=-83 EndZ=0
    g79: LineSegment StartX=-54 StartY=-83 StartZ=0 EndX=0 EndY=-29 EndZ=0
    g80: LineSegment StartX=0 StartY=-39 StartZ=0 EndX=-44 EndY=-83 EndZ=0
    g81: LineSegment StartX=-41 StartY=-83 StartZ=0 EndX=0 EndY=-42 EndZ=0
    g82: LineSegment StartX=-31 StartY=-83 StartZ=0 EndX=0 EndY=-52 EndZ=0
    g83: LineSegment StartX=-28 StartY=-83 StartZ=0 EndX=-3.6e-15 EndY=-55 EndZ=0
    g84: LineSegment StartX=0 StartY=-42 StartZ=0 EndX=0 EndY=-39 EndZ=0
    g85: LineSegment StartX=-3.6e-15 StartY=-55 StartZ=0 EndX=0 EndY=-52 EndZ=0
    g86: LineSegment StartX=0 StartY=-29 StartZ=0 EndX=0 EndY=-26 EndZ=0
    g87: LineSegment [constr] StartX=0 StartY=-52 StartZ=0 EndX=0 EndY=-42 EndZ=0
    g88: LineSegment [constr] StartX=0 StartY=-39 StartZ=0 EndX=0 EndY=-29 EndZ=0
    g89: LineSegment StartX=-57 StartY=-83 StartZ=0 EndX=-54 EndY=-83 EndZ=0
    g90: LineSegment StartX=-44 StartY=-83 StartZ=0 EndX=-41 EndY=-83 EndZ=0
    g91: LineSegment StartX=-31 StartY=-83 StartZ=0 EndX=-28 EndY=-83 EndZ=0
    g92: LineSegment StartX=-18 StartY=-83 StartZ=0 EndX=-7 EndY=-72 EndZ=0
    g93: LineSegment StartX=-15 StartY=-83 StartZ=0 EndX=-7 EndY=-75 EndZ=0
    g94: LineSegment StartX=-7 StartY=-75 StartZ=0 EndX=-7 EndY=-72 EndZ=0
    g95: LineSegment StartX=-15 StartY=-83 StartZ=0 EndX=-18 EndY=-83 EndZ=0
    g96: LineSegment [constr] StartX=-41 StartY=-83 StartZ=0 EndX=-31 EndY=-83 EndZ=0
    g97: LineSegment [constr] StartX=-28 StartY=-83 StartZ=0 EndX=-18 EndY=-83 EndZ=0
    g98: LineSegment StartX=-8 StartY=83 StartZ=0 EndX=-7 EndY=83 EndZ=0
    g99: LineSegment StartX=-7 StartY=81 StartZ=0 EndX=-7 EndY=83 EndZ=0
  constraints (277):
    c: PointOnObject(g0,g-4)
    c: PointOnObject(g0,g-3)
    c: PointOnObject(g1,g-3)
    c: PointOnObject(g1,g-4)
    c: PointOnObject(g2,g-3)
    c: PointOnObject(g2,g-4)
    c: PointOnObject(g3,g-4)
    c: PointOnObject(g3,g-3)
    c: PointOnObject(g4,g-3)
    c: Parallel(g0,g1)
    c: Parallel(g1,g2)
    c: Parallel(g2,g3)
    c: Parallel(g3,g4)
    c: Coincident(g5,g-9)
    c: Coincident(g5,g0)
    c: DistanceX(g5,g5) = 10
    c: Coincident(g6,g0)
    c: Coincident(g6,g1)
    c: DistanceX(g6,g6) = 3
    c: Coincident(g7,g1)
    c: Coincident(g7,g2)
    c: Coincident(g8,g2)
    c: Coincident(g8,g3)
    c: Equal(g7,g5)
    c: Equal(g6,g8)
    c: Parallel(g0,g-9)
    c: PointOnObject(g4,g-4)
    c: Coincident(g9,g0)
    c: Coincident(g9,g1)
    c: Coincident(g10,g3)
    c: Coincident(g10,g2)
    c: Coincident(g11,g4)
    c: Coincident(g11,g3)
    c: Equal(g11,g7)
    c: PointOnObject(g12,g-4)
    c: PointOnObject(g12,g-3)
    c: Coincident(g13,g4)
    c: Coincident(g13,g12)
    c: Coincident(g14,g12)
    c: Coincident(g14,g4)
    c: Equal(g13,g8)
    c: Parallel(g4,g12)
    c: PointOnObject(g15,g-4)
    c: PointOnObject(g15,g-3)
    c: PointOnObject(g16,g-3)
    c: PointOnObject(g16,g-4)
    c: Coincident(g17,g16)
    c: Coincident(g17,g15)
    c: Coincident(g18,g16)
    c: Coincident(g18,g15)
    c: Equal(g18,g13)
    c: Parallel(g15,g16)
    c: Coincident(g19,g12)
    c: Coincident(g19,g15)
    c: Equal(g19,g11)
    c: Parallel(g15,g12)
    c: PointOnObject(g20,g-3)
    c: PointOnObject(g21,g-3)
    c: Coincident(g22,g21)
    c: Coincident(g22,g20)
    c: Equal(g22,g18)
    c: Parallel(g20,g21)
    c: Parallel(g21,g16)
    c: Coincident(g23,g16)
    c: Coincident(g23,g20)
    c: Equal(g23,g19)
    c: PointOnObject(g20,g-5)
    c: PointOnObject(g21,g-5)
    c: Coincident(g24,g20)
    c: Coincident(g24,g21)
    c: PointOnObject(g25,g-3)
    c: PointOnObject(g26,g-3)
    c: Coincident(g27,g25)
    c: Coincident(g27,g26)
    c: Coincident(g28,g25)
    c: Coincident(g28,g21)
    c: PointOnObject(g29,g-3)
    c: Equal(g28,g23)
    c: Equal(g27,g22)
    c: Parallel(g25,g26)
    c: Parallel(g26,g29)
    c: Parallel(g29,g30)
    c: Parallel(g30,g21)
    c: PointOnObject(g25,g-6)
    c: PointOnObject(g26,g-6)
    c: Coincident(g31,g26)
    c: Coincident(g31,g29)
    c: Equal(g31,g28)
    c: PointOnObject(g30,g-10)
    c: PointOnObject(g29,g-8)
    c: PointOnObject(g30,g-8)
    c: Coincident(g32,g26)
    c: Coincident(g32,g25)
    c: Coincident(g33,g30)
    c: Coincident(g33,g29)
    c: Equal(g33,g32)
    c: Coincident(g34,g15)
    c: Coincident(g34,g12)
    c: PointOnObject(g35,g-10)
    c: PointOnObject(g36,g-8)
    c: Parallel(g36,g35)
    c: Parallel(g35,g30)
    c: Coincident(g37,g36)
    c: Coincident(g37,g35)
    c: Vertical(g37)
    c: Equal(g37,g33)
    c: Coincident(g38,g30)
    c: Coincident(g38,g35)
    c: Equal(g38,g34)
    c: PointOnObject(g36,g-10)
    c: Coincident(g39,g35)
    c: Coincident(g39,g36)
    c: PointOnObject(g40,g-8)
    c: PointOnObject(g40,g-11)
    c: PointOnObject(g41,g-8)
    c: PointOnObject(g42,g-8)
    c: Parallel(g41,g40)
    c: Parallel(g40,g36)
    c: Coincident(g49,g40)
    c: Equal(g49,g37)
    c: Coincident(g50,g40)
    c: Coincident(g50,g36)
    c: Equal(g50,g38)
    c: Coincident(g41,g49)
    c: Coincident(g51,g42)
    c: Coincident(g51,g41)
    c: Equal(g51,g50)
    c: Parallel(g43,g42)
    c: Parallel(g42,g41)
    c: PointOnObject(g43,g-8)
    c: Coincident(g52,g43)
    c: Coincident(g52,g42)
    c: Equal(g52,g49)
    c: Parallel(g44,g45)
    c: Parallel(g45,g46)
    c: Parallel(g46,g47)
    c: Parallel(g47,g48)
    c: Parallel(g48,g43)
    c: PointOnObject(g44,g-12)
    c: PointOnObject(g45,g-12)
    c: PointOnObject(g41,g-2)
    c: Coincident(g53,g40)
    c: Horizontal(g53)
    c: Coincident(g54,g53)
    c: Coincident(g54,g41)
    c: PointOnObject(g53,g-2)
    c: PointOnObject(g42,g-2)
    c: PointOnObject(g43,g-2)
    c: PointOnObject(g44,g-2)
    c: PointOnObject(g45,g-2)
    c: Coincident(g55,g42)
    c: Coincident(g55,g41)
    c: Coincident(g56,g44)
    c: Coincident(g56,g43)
    c: Equal(g55,g56)
    c: Coincident(g57,g43)
    c: Coincident(g57,g42)
    c: Coincident(g45,g58)
    c: Coincident(g58,g44)
    c: Equal(g58,g57)
    c: PointOnObject(g46,g-2)
    c: PointOnObject(g47,g-2)
    c: Coincident(g59,g47)
    c: Coincident(g59,g46)
    c: Equal(g59,g58)
    c: PointOnObject(g46,g-12)
    c: PointOnObject(g47,g-12)
    c: Coincident(g60,g45)
    c: Coincident(g60,g44)
    c: Coincident(g61,g47)
    c: Coincident(g61,g46)
    c: PointOnObject(g48,g-2)
    c: Coincident(g62,g46)
    c: Coincident(g62,g45)
    c: Coincident(g63,g48)
    c: Coincident(g63,g47)
    c: Equal(g63,g62)
    c: Equal(g62,g56)
    c: PointOnObject(g48,g-12)
    c: PointOnObject(g64,g-13)
    c: PointOnObject(g64,g-2)
    c: PointOnObject(g65,g-13)
    c: PointOnObject(g65,g-2)
    c: PointOnObject(g66,g-13)
    c: PointOnObject(g66,g-2)
    c: PointOnObject(g67,g-13)
    c: PointOnObject(g68,g-13)
    c: PointOnObject(g68,g-2)
    c: PointOnObject(g69,g-2)
    c: Parallel(g48,g64)
    c: Parallel(g64,g65)
    c: Parallel(g65,g66)
    c: Parallel(g66,g67)
    c: Parallel(g67,g68)
    c: Parallel(g68,g69)
    c: Coincident(g70,g65)
    c: Coincident(g70,g64)
    c: Coincident(g71,g67)
    c: Coincident(g71,g66)
    c: Vertical(g71)
    c: Coincident(g72,g68)
    c: Coincident(g72,g69)
    c: Coincident(g73,g68)
    c: Coincident(g73,g67)
    c: Coincident(g74,g66)
    c: Coincident(g74,g65)
    c: Coincident(g75,g64)
    c: Coincident(g75,g48)
    c: Equal(g73,g74)
    c: Equal(g74,g75)
    c: Equal(g75,g59)
    c: Equal(g72,g71)
    c: Equal(g71,g70)
    c: Equal(g70,g63)
    c: PointOnObject(g69,g-13)
    c: Coincident(g76,g68)
    c: Coincident(g76,g67)
    c: Coincident(g77,g66)
    c: Coincident(g77,g65)
    c: Coincident(g78,g64)
    c: Coincident(g78,g48)
    c: PointOnObject(g79,g-13)
    c: PointOnObject(g79,g-2)
    c: PointOnObject(g80,g-2)
    c: PointOnObject(g80,g-13)
    c: PointOnObject(g81,g-2)
    c: PointOnObject(g82,g-13)
    c: PointOnObject(g82,g-2)
    c: PointOnObject(g83,g-13)
    c: PointOnObject(g83,g-2)
    c: Coincident(g84,g81)
    c: Coincident(g84,g80)
    c: Coincident(g85,g83)
    c: Coincident(g85,g82)
    c: Coincident(g86,g79)
    c: Coincident(g86,g69)
    c: Equal(g85,g84)
    c: Equal(g84,g86)
    c: Equal(g86,g73)
    c: Coincident(g87,g82)
    c: Coincident(g87,g81)
    c: Coincident(g88,g80)
    c: Coincident(g88,g79)
    c: Equal(g87,g88)
    c: Equal(g88,g72)
    c: Parallel(g80,g81)
    c: Parallel(g81,g82)
    c: Parallel(g82,g83)
    c: Parallel(g83,g66)
    c: PointOnObject(g81,g-13)
    c: Parallel(g79,g69)
    c: Coincident(g89,g69)
    c: Coincident(g89,g79)
    c: Coincident(g90,g80)
    c: Coincident(g90,g81)
    c: Coincident(g91,g82)
    c: Coincident(g91,g83)
    c: PointOnObject(g92,g-13)
    c: PointOnObject(g93,g-13)
    c: PointOnObject(g93,g-14)
    c: Coincident(g94,g92)
    c: Vertical(g94)
    c: Coincident(g95,g93)
    c: Coincident(g95,g92)
    c: Parallel(g92,g93)
    c: Parallel(g93,g83)
    c: Coincident(g93,g94)
    c: Equal(g95,g91)
    c: Coincident(g96,g81)
    c: Coincident(g96,g82)
    c: Coincident(g97,g83)
    c: Coincident(g97,g92)
    c: Equal(g97,g96)
    c: Coincident(g98,g29)
    c: Coincident(g98,g-10)
    c: Coincident(g99,g30)
    c: Coincident(g99,g98)
FEATURE [PartDesign::Pad] Pad010
  BaseFeature = -> Pocket009
  Length = 2
  Length2 = 100
  Profile = -> Sketch019
  Type = 0
FEATURE [PartDesign::Mirrored] Mirrored004
  BaseFeature = -> Pad010
  MirrorPlane = -> Sketch019 [V_Axis]
  Originals = -> [Pad010]
FEATURE [PartDesign::Plane] DatumPlane005
  Length = 281.569
  MapMode = 2
  ResizeMode = 0
  Width = 221.569
FEATURE [Sketcher::SketchObject] Sketch020
  ExternalGeometry = -> [Mirrored004]
  MapMode = 5
  Support = -> [DatumPlane005]
  sketch-geometry (46):
    g0: ArcOfCircle CenterX=-115 CenterY=85 CenterZ=0 NormalX=0 NormalY=0 NormalZ=1 AngleXU=0 Radius=5 StartAngle=1.5708 EndAngle=3.14159
    g1: LineSegment StartX=-115 StartY=90 StartZ=0 EndX=115 EndY=90 EndZ=0
    g2: LineSegment StartX=-120 StartY=85 StartZ=0 EndX=-120 EndY=-85 EndZ=0
    g3: ArcOfCircle CenterX=-93.9289 CenterY=78 CenterZ=0 NormalX=0 NormalY=0 NormalZ=1 AngleXU=0 Radius=5 StartAngle=1.5708 EndAngle=2.35619
    g4: ArcOfCircle CenterX=-108 CenterY=63.9289 CenterZ=0 NormalX=0 NormalY=0 NormalZ=1 AngleXU=0 Radius=5 StartAngle=2.35619 EndAngle=3.14159
    g5: ArcOfCircle CenterX=93.9289 CenterY=78 CenterZ=0 NormalX=0 NormalY=0 NormalZ=1 AngleXU=0 Radius=5 StartAngle=0.785398 EndAngle=1.5708
    g6: ArcOfCircle CenterX=108 CenterY=63.9289 CenterZ=0 NormalX=0 NormalY=0 NormalZ=1 AngleXU=0 Radius=5 StartAngle=3.78397e-08 EndAngle=0.785398
    g7: ArcOfCircle CenterX=108 CenterY=-63.9289 CenterZ=0 NormalX=0 NormalY=0 NormalZ=1 AngleXU=0 Radius=5 StartAngle=5.49779 EndAngle=6.28319
    g8: ArcOfCircle CenterX=93.9289 CenterY=-78 CenterZ=0 NormalX=0 NormalY=0 NormalZ=1 AngleXU=0 Radius=5 StartAngle=4.71239 EndAngle=5.49779
    g9: ArcOfCircle CenterX=-93.9289 CenterY=-78 CenterZ=0 NormalX=0 NormalY=0 NormalZ=1 AngleXU=0 Radius=5 StartAngle=3.92699 EndAngle=4.71239
    g10: ArcOfCircle CenterX=-108 CenterY=-63.9289 CenterZ=0 NormalX=0 NormalY=0 NormalZ=1 AngleXU=0 Radius=5 StartAngle=3.14159 EndAngle=3.92699
    g11: LineSegment StartX=-93.9289 StartY=83 StartZ=0 EndX=93.9289 EndY=83 EndZ=0
    g12: LineSegment StartX=-93.9289 StartY=-83 StartZ=0 EndX=93.9289 EndY=-83 EndZ=0
    g13: LineSegment StartX=97.4645 StartY=-81.5355 StartZ=0 EndX=111.536 EndY=-67.4645 EndZ=0
    g14: LineSegment StartX=-97.4645 StartY=-81.5355 StartZ=0 EndX=-111.536 EndY=-67.4645 EndZ=0
    g15: ArcOfCircle CenterX=111 CenterY=9 CenterZ=0 NormalX=0 NormalY=0 NormalZ=1 AngleXU=0 Radius=2 StartAngle=4.71239 EndAngle=6.28319
    g16: ArcOfCircle CenterX=106 CenterY=5 CenterZ=0 NormalX=0 NormalY=0 NormalZ=1 AngleXU=0 Radius=2 StartAngle=1.5708 EndAngle=3.14159
    g17: ArcOfCircle CenterX=106 CenterY=-5 CenterZ=0 NormalX=0 NormalY=0 NormalZ=1 AngleXU=0 Radius=2 StartAngle=3.14159 EndAngle=4.71239
    g18: ArcOfCircle CenterX=111 CenterY=-9 CenterZ=0 NormalX=0 NormalY=0 NormalZ=1 AngleXU=0 Radius=2 StartAngle=9.33234e-07 EndAngle=1.5708
    g19: ArcOfCircle CenterX=-111 CenterY=-9 CenterZ=0 NormalX=0 NormalY=0 NormalZ=1 AngleXU=0 Radius=2 StartAngle=1.5708 EndAngle=3.14159
    g20: ArcOfCircle CenterX=-106 CenterY=-5 CenterZ=0 NormalX=0 NormalY=0 NormalZ=1 AngleXU=0 Radius=2 StartAngle=4.71239 EndAngle=6.28319
    g21: ArcOfCircle CenterX=-106 CenterY=5 CenterZ=0 NormalX=0 NormalY=0 NormalZ=1 AngleXU=0 Radius=2 StartAngle=6.28319 EndAngle=7.85398
    g22: ArcOfCircle CenterX=-111 CenterY=9 CenterZ=0 NormalX=0 NormalY=0 NormalZ=1 AngleXU=0 Radius=2 StartAngle=3.14159 EndAngle=4.71239
    g23: LineSegment StartX=111 StartY=-7 StartZ=0 EndX=106 EndY=-7 EndZ=0
    g24: LineSegment StartX=104 StartY=5 StartZ=0 EndX=104 EndY=-5 EndZ=0
    g25: LineSegment StartX=111 StartY=7 StartZ=0 EndX=106 EndY=7 EndZ=0
    g26: LineSegment StartX=-111 StartY=-7 StartZ=0 EndX=-106 EndY=-7 EndZ=0
    g27: LineSegment StartX=-104 StartY=-5 StartZ=0 EndX=-104 EndY=5 EndZ=0
    g28: LineSegment StartX=-111 StartY=7 StartZ=0 EndX=-106 EndY=7 EndZ=0
    g29: LineSegment StartX=-97.4645 StartY=81.5355 StartZ=0 EndX=-111.536 EndY=67.4645 EndZ=0
    g30: LineSegment StartX=-113 StartY=63.9289 StartZ=0 EndX=-113 EndY=9 EndZ=0
    g31: LineSegment StartX=-113 StartY=-63.9289 StartZ=0 EndX=-113 EndY=-9 EndZ=0
    g32: LineSegment StartX=113 StartY=-63.9289 StartZ=0 EndX=113 EndY=-9 EndZ=0
    g33: LineSegment StartX=113 StartY=9 StartZ=0 EndX=113 EndY=63.9289 EndZ=0
    g34: LineSegment StartX=111.536 StartY=67.4645 StartZ=0 EndX=97.4645 EndY=81.5355 EndZ=0
    g35: Circle CenterX=110 CenterY=80 CenterZ=0 NormalX=0 NormalY=0 NormalZ=1 AngleXU=0 Radius=3.25
    g36: Circle CenterX=110 CenterY=-80 CenterZ=0 NormalX=0 NormalY=0 NormalZ=1 AngleXU=0 Radius=3.25
    g37: Circle CenterX=-110 CenterY=-80 CenterZ=0 NormalX=0 NormalY=0 NormalZ=1 AngleXU=0 Radius=3.25
    g38: Circle CenterX=-110 CenterY=80 CenterZ=0 NormalX=0 NormalY=0 NormalZ=1 AngleXU=0 Radius=3.25
    g39: ArcOfCircle CenterX=-115 CenterY=-85 CenterZ=0 NormalX=0 NormalY=0 NormalZ=1 AngleXU=0 Radius=5 StartAngle=3.14159 EndAngle=4.71239
    g40: ArcOfCircle CenterX=115 CenterY=-85 CenterZ=0 NormalX=0 NormalY=0 NormalZ=1 AngleXU=0 Radius=5 StartAngle=4.71239 EndAngle=6.28319
    g41: ArcOfCircle CenterX=115 CenterY=85 CenterZ=0 NormalX=0 NormalY=0 NormalZ=1 AngleXU=0 Radius=5 StartAngle=-9e-16 EndAngle=1.5708
    g42: LineSegment StartX=-115 StartY=-90 StartZ=0 EndX=115 EndY=-90 EndZ=0
    g43: LineSegment StartX=120 StartY=-85 StartZ=0 EndX=120 EndY=85 EndZ=0
    g44: Circle CenterX=110 CenterY=0 CenterZ=0 NormalX=0 NormalY=0 NormalZ=1 AngleXU=0 Radius=3.25
    g45: Circle CenterX=-110 CenterY=0 CenterZ=0 NormalX=0 NormalY=0 NormalZ=1 AngleXU=0 Radius=3.25
  constraints (144):
    c: Coincident(g0,g-5)
    c: Coincident(g0,g-5)
    c: Equal(g0,g-5)
    c: Coincident(g1,g0)
    c: Coincident(g1,g-3)
    c: Coincident(g2,g0)
    c: Coincident(g2,g-4)
    c: PointOnObject(g3,g-8)
    c: PointOnObject(g3,g-7)
    c: Tangent(g3,g-7)
    c: Tangent(g-8,g3)
    c: Radius(g3) = 5
    c: PointOnObject(g8,g-13)
    c: PointOnObject(g8,g-17)
    c: PointOnObject(g7,g-12)
    c: PointOnObject(g7,g-13)
    c: Tangent(g7,g-12)
    c: Tangent(g7,g-13)
    c: Tangent(g8,g-13)
    c: Tangent(g8,g-17)
    c: PointOnObject(g6,g-11)
    c: PointOnObject(g6,g-10)
    c: Tangent(g6,g-11)
    c: Tangent(g6,g-10)
    c: PointOnObject(g5,g-9)
    c: PointOnObject(g5,g-11)
    c: Tangent(g5,g-9)
    c: Tangent(g-11,g5)
    c: PointOnObject(g10,g-20)
    c: PointOnObject(g10,g-19)
    c: PointOnObject(g9,g-19)
    c: PointOnObject(g9,g-18)
    c: Tangent(g9,g-18)
    c: Tangent(g9,g-19)
    c: Tangent(g10,g-19)
    c: Tangent(g10,g-20)
    c: PointOnObject(g4,g-21)
    c: PointOnObject(g4,g-8)
    c: Tangent(g4,g-8)
    c: Tangent(g4,g-21)
    c: Equal(g4,g10)
    c: Equal(g10,g9)
    c: Equal(g9,g8)
    c: Equal(g8,g7)
    c: Equal(g7,g6)
    c: Equal(g6,g5)
    c: Equal(g5,g3)
    c: Coincident(g11,g3)
    c: Coincident(g11,g5)
    c: Coincident(g12,g9)
    c: Coincident(g12,g8)
    c: Coincident(g13,g8)
    c: Coincident(g13,g7)
    c: Coincident(g14,g9)
    c: Coincident(g14,g10)
    c: PointOnObject(g22,g-21)
    c: PointOnObject(g22,g-22)
    c: Tangent(g22,g-21)
    c: Tangent(g22,g-22)
    c: PointOnObject(g21,g-22)
    c: PointOnObject(g21,g-23)
    c: Tangent(g21,g-22)
    c: Tangent(g21,g-23)
    c: PointOnObject(g20,g-23)
    c: PointOnObject(g20,g-24)
    c: Tangent(g20,g-23)
    c: Tangent(g20,g-24)
    c: PointOnObject(g19,g-24)
    c: PointOnObject(g19,g-20)
    c: Tangent(g19,g-24)
    c: Tangent(g19,g-20)
    c: Radius(g22) = 2
    c: PointOnObject(g18,g-14)
    c: PointOnObject(g18,g-12)
    c: PointOnObject(g17,g-14)
    c: PointOnObject(g17,g-15)
    c: Tangent(g17,g-15)
    c: Tangent(g17,g-14)
    c: Tangent(g18,g-14)
    c: Tangent(g18,g-12)
    c: PointOnObject(g16,g-16)
    c: PointOnObject(g16,g-15)
    c: Tangent(g16,g-16)
    c: Tangent(g16,g-15)
    c: PointOnObject(g15,g-16)
    c: PointOnObject(g15,g-10)
    c: Tangent(g15,g-16)
    c: Tangent(g15,g-10)
    c: Equal(g18,g17)
    c: Equal(g17,g16)
    c: Equal(g16,g15)
    c: Equal(g15,g19)
    c: Equal(g19,g20)
    c: Equal(g20,g21)
    c: Equal(g21,g22)
    c: Coincident(g23,g18)
    c: Coincident(g23,g17)
    c: Coincident(g24,g16)
    c: Coincident(g24,g17)
    c: Coincident(g25,g15)
    c: Coincident(g25,g16)
    c: Coincident(g26,g19)
    c: Coincident(g26,g20)
    c: Coincident(g27,g20)
    c: Coincident(g27,g21)
    c: Coincident(g28,g22)
    c: Coincident(g28,g21)
    c: Coincident(g29,g3)
    c: Coincident(g29,g4)
    c: Coincident(g30,g4)
    c: Coincident(g30,g22)
    c: Coincident(g31,g10)
    c: Coincident(g31,g19)
    c: Coincident(g32,g7)
    c: Coincident(g32,g18)
    c: Coincident(g33,g15)
    c: Coincident(g33,g6)
    c: Coincident(g34,g6)
    c: Coincident(g34,g5)
    c: Equal(g37,g36)
    c: Equal(g36,g35)
    c: Equal(g35,g-6)
    c: Symmetric(g35,g-6,g-2)
    c: Symmetric(g36,g35,g-1)
    c: Symmetric(g37,g-6,g-1)
    c: Equal(g38,g-6)
    c: Coincident(g38,g-6)
    c: Equal(g39,g40)
    c: Equal(g40,g41)
    c: Equal(g41,g0)
    c: Symmetric(g41,g0,g-2)
    c: Symmetric(g41,g0,g-2)
    c: Symmetric(g39,g0,g-1)
    c: Symmetric(g0,g39,g-1)
    c: Symmetric(g39,g40,g-2)
    c: Symmetric(g2,g40,g-2)
    c: Coincident(g42,g39)
    c: Coincident(g42,g40)
    c: Coincident(g43,g40)
    c: Coincident(g43,g41)
    c: Equal(g45,g-25)
    c: Coincident(g45,g-25)
    c: Symmetric(g44,g45,g-2)
    c: Equal(g44,g45)
FEATURE [PartDesign::Pad] Pad011
  BaseFeature = -> Mirrored004
  Length = 100
  Length2 = 100
  Profile = -> Sketch020
  Type = 0
FEATURE [PartDesign::Plane] DatumPlane006
  AttachmentOffset = pos=(0,0,90) rot=(0,0,1;0rad)
  Length = 272.496
  MapMode = 2
  Placement = pos=(0,-90,-2e-14) rot=(1,0,0;1.5708rad)
  ResizeMode = 0
  Support = -> [XZ_Plane005]
  Width = 142.496
FEATURE [Sketcher::SketchObject] Sketch021
  MapMode = 5
  Placement = pos=(0,-90,-2e-14) rot=(1,0,0;1.5708rad)
  Support = -> [DatumPlane006]
  sketch-geometry (10):
    g0: Circle [constr] CenterX=50 CenterY=46.5 CenterZ=0 NormalX=0 NormalY=0 NormalZ=1 AngleXU=0 Radius=46.5
    g1: Circle CenterX=17.1195 CenterY=79.3805 CenterZ=0 NormalX=0 NormalY=0 NormalZ=1 AngleXU=0 Radius=2.25
    g2: Circle CenterX=82.8805 CenterY=79.3805 CenterZ=0 NormalX=0 NormalY=0 NormalZ=1 AngleXU=0 Radius=2.25
    g3: Circle CenterX=82.8805 CenterY=13.6195 CenterZ=0 NormalX=0 NormalY=0 NormalZ=1 AngleXU=0 Radius=2.25
    g4: Circle CenterX=17.1195 CenterY=13.6195 CenterZ=0 NormalX=0 NormalY=0 NormalZ=1 AngleXU=0 Radius=2.25
    g5: LineSegment [constr] StartX=3.5 StartY=46.5 StartZ=0 EndX=96.5 EndY=46.5 EndZ=0
    g6: LineSegment [constr] StartX=50 StartY=93 StartZ=0 EndX=50 EndY=0 EndZ=0
    g7: LineSegment [constr] StartX=17.1195 StartY=79.3805 StartZ=0 EndX=82.8805 EndY=79.3805 EndZ=0
    g8: LineSegment [constr] StartX=82.8805 StartY=13.6195 StartZ=0 EndX=82.8805 EndY=79.3805 EndZ=0
    g9: Circle CenterX=50 CenterY=46.5 CenterZ=0 NormalX=0 NormalY=0 NormalZ=1 AngleXU=0 Radius=38.25
  constraints (27):
    c: Diameter(g0) = 93
    c: Tangent(g0,g-1)
    c: PointOnObject(g4,g0)
    c: PointOnObject(g1,g0)
    c: PointOnObject(g2,g0)
    c: Diameter(g1) = 4.5
    c: Equal(g2,g3)
    c: Equal(g3,g4)
    c: Equal(g4,g1)
    c: Horizontal(g5)
    c: PointOnObject(g5,g0)
    c: PointOnObject(g5,g0)
    c: Symmetric(g4,g1,g5)
    c: Vertical(g6)
    c: PointOnObject(g6,g0)
    c: PointOnObject(g6,g0)
    c: Symmetric(g2,g1,g6)
    c: Symmetric(g3,g4,g6)
    c: Coincident(g7,g1)
    c: Coincident(g7,g2)
    c: Coincident(g8,g3)
    c: PointOnObject(g8,g0)
    c: Vertical(g8)
    c: Equal(g8,g7)
    c: Coincident(g9,g0)
    c: Diameter(g9) = 76.5
    c: DistanceX(g-1,g9) = 50
FEATURE [PartDesign::Pocket] Pocket010
  BaseFeature = -> Pad011
  Length = 10
  Length2 = 100
  Profile = -> Sketch021
  Type = 0
FEATURE [PartDesign::PolarPattern] PolarPattern002
  Angle = 360
  Axis = -> Z_Axis005
  BaseFeature = -> Pocket010
  Occurrences = 2
  Originals = -> [Pocket010]
FEATURE [PartDesign::Plane] DatumPlane007
  AttachmentOffset = pos=(0,0,90) rot=(0,0,1;0rad)
  Length = 272.496
  MapMode = 3
  Placement = pos=(0,-90,2e-14) rot=(1,0,0;1.5708rad)
  ResizeMode = 0
  Support = -> [PolarPattern002]
  Width = 142.496
FEATURE [Sketcher::SketchObject] Sketch022
  MapMode = 5
  Placement = pos=(0,-90,2e-14) rot=(1,0,0;1.5708rad)
  Support = -> [DatumPlane007]
  sketch-geometry (10):
    g0: Circle [constr] CenterX=-50 CenterY=46.5 CenterZ=0 NormalX=0 NormalY=0 NormalZ=1 AngleXU=0 Radius=27.85
    g1: Circle CenterX=-69.6929 CenterY=66.1929 CenterZ=0 NormalX=0 NormalY=0 NormalZ=1 AngleXU=0 Radius=2
    g2: Circle CenterX=-30.3071 CenterY=66.1929 CenterZ=0 NormalX=0 NormalY=0 NormalZ=1 AngleXU=0 Radius=2
    g3: Circle CenterX=-30.3071 CenterY=26.8071 CenterZ=0 NormalX=0 NormalY=0 NormalZ=1 AngleXU=0 Radius=2
    g4: Circle CenterX=-69.6929 CenterY=26.8071 CenterZ=0 NormalX=0 NormalY=0 NormalZ=1 AngleXU=0 Radius=2
    g5: LineSegment [constr] StartX=-77.85 StartY=46.5 StartZ=0 EndX=-22.15 EndY=46.5 EndZ=0
    g6: LineSegment [constr] StartX=-50 StartY=74.35 StartZ=0 EndX=-50 EndY=18.65 EndZ=0
    g7: LineSegment [constr] StartX=-69.6929 StartY=66.1929 StartZ=0 EndX=-30.3071 EndY=66.1929 EndZ=0
    g8: LineSegment [constr] StartX=-30.3071 StartY=26.8071 StartZ=0 EndX=-30.3071 EndY=66.1929 EndZ=0
    g9: Circle CenterX=-50 CenterY=46.5 CenterZ=0 NormalX=0 NormalY=0 NormalZ=1 AngleXU=0 Radius=22
  constraints (27):
    c: Diameter(g0) = 55.7
    c: DistanceX(g0,g-1) = 50
    c: Equal(g4,g1)
    c: Equal(g1,g2)
    c: Equal(g2,g3)
    c: Diameter(g1) = 4
    c: PointOnObject(g1,g0)
    c: PointOnObject(g2,g0)
    c: PointOnObject(g3,g0)
    c: PointOnObject(g4,g0)
    c: Horizontal(g5)
    c: PointOnObject(g5,g0)
    c: PointOnObject(g5,g0)
    c: Vertical(g6)
    c: PointOnObject(g6,g0)
    c: PointOnObject(g6,g0)
    c: Symmetric(g3,g4,g6)
    c: Symmetric(g3,g2,g5)
    c: Coincident(g7,g1)
    c: Coincident(g7,g2)
    c: Coincident(g8,g3)
    c: Coincident(g8,g2)
    c: Horizontal(g7)
    c: Equal(g8,g7)
    c: DistanceY(g-1,g0) = 46.5
    c: Coincident(g9,g0)
    c: Diameter(g9) = 44
FEATURE [PartDesign::Pocket] Pocket011
  BaseFeature = -> PolarPattern002
  Length = 10
  Length2 = 100
  Profile = -> Sketch022
  Type = 0
FEATURE [Sketcher::SketchObject] Sketch023
  MapMode = 5
  Support = -> [XY_Plane006]
  sketch-geometry (8):
    g0: LineSegment StartX=0 StartY=0 StartZ=0 EndX=51.75 EndY=0 EndZ=0
    g1: LineSegment StartX=51.75 StartY=0 StartZ=0 EndX=51.75 EndY=-0.5 EndZ=0
    g2: LineSegment StartX=51.75 StartY=-0.5 StartZ=0 EndX=38.25 EndY=-0.5 EndZ=0
    g3: LineSegment StartX=38.25 StartY=-0.5 StartZ=0 EndX=22.1 EndY=-29.3 EndZ=0
    g4: LineSegment StartX=22.1 StartY=-29.3 StartZ=0 EndX=22.1 EndY=-54.3 EndZ=0
    g5: LineSegment StartX=22.1 StartY=-54.3 StartZ=0 EndX=0 EndY=-54.3 EndZ=0
    g6: LineSegment StartX=0 StartY=-54.3 StartZ=0 EndX=0 EndY=0 EndZ=0
    g7: LineSegment StartX=0 StartY=0 StartZ=0 EndX=51.75 EndY=0 EndZ=0
  constraints (22):
    c: Coincident(g0,g-1)
    c: PointOnObject(g0,g-1)
    c: Coincident(g1,g0)
    c: Coincident(g2,g1)
    c: Horizontal(g2)
    c: Coincident(g3,g2)
    c: Coincident(g4,g3)
    c: Vertical(g4)
    c: Coincident(g5,g4)
    c: PointOnObject(g5,g-2)
    c: Horizontal(g5)
    c: Coincident(g6,g5)
    c: Coincident(g6,g0)
    c: Coincident(g7,g0)
    c: Coincident(g7,g0)
    c: Vertical(g1)
    c: DistanceX(g0,g0) = 51.75
    c: DistanceX(g5,g5) = 22.1
    c: DistanceY(g1,g1) = 0.5
    c: DistanceY(g4,g1) = 53.8
    c: DistanceY(g4,g4) = 25
    c: DistanceX(g0,g2) = 38.25
FEATURE [PartDesign::Revolution] Revolution001
  Angle = 360
  Axis = (0,1,0)
  Base = (0,0,0)
  Profile = -> Sketch023
  ReferenceAxis = -> Sketch023 [V_Axis]
  Reversed = true
FEATURE [Sketcher::SketchObject] Sketch024
  MapMode = 5
  Placement = pos=(0,0,0) rot=(1,0,0;1.5708rad)
  Support = -> [XZ_Plane006]
  sketch-geometry (10):
    g0: Circle [constr] CenterX=0 CenterY=0 CenterZ=0 NormalX=0 NormalY=0 NormalZ=1 AngleXU=0 Radius=46.5
    g1: LineSegment [constr] StartX=0 StartY=46.5 StartZ=0 EndX=0 EndY=-46.5 EndZ=0
    g2: LineSegment [constr] StartX=-46.5 StartY=0 StartZ=0 EndX=46.5 EndY=0 EndZ=0
    g3: Circle CenterX=-32.8805 CenterY=32.8805 CenterZ=0 NormalX=0 NormalY=0 NormalZ=1 AngleXU=0 Radius=2.25
    g4: Circle CenterX=32.8805 CenterY=32.8805 CenterZ=0 NormalX=0 NormalY=0 NormalZ=1 AngleXU=0 Radius=2.25
    g5: Circle CenterX=32.8805 CenterY=-32.8805 CenterZ=0 NormalX=0 NormalY=0 NormalZ=1 AngleXU=0 Radius=2.25
    g6: Circle CenterX=-32.8805 CenterY=-32.8805 CenterZ=0 NormalX=0 NormalY=0 NormalZ=1 AngleXU=0 Radius=2.25
    g7: LineSegment [constr] StartX=-32.8805 StartY=-32.8805 StartZ=0 EndX=32.8805 EndY=-32.8805 EndZ=0
    g8: LineSegment [constr] StartX=32.8805 StartY=-32.8805 StartZ=0 EndX=32.8805 EndY=32.8805 EndZ=0
    g9: LineSegment [constr] StartX=-32.8805 StartY=32.8805 StartZ=0 EndX=32.8805 EndY=32.8805 EndZ=0
  constraints (28):
    c: Diameter(g0) = 93
    c: Vertical(g1)
    c: Horizontal(g2)
    c: PointOnObject(g0,g2)
    c: PointOnObject(g2,g0)
    c: PointOnObject(g2,g0)
    c: PointOnObject(g1,g0)
    c: PointOnObject(g1,g0)
    c: PointOnObject(g0,g1)
    c: Coincident(g0,g-1)
    c: Equal(g6,g5)
    c: Equal(g5,g4)
    c: Equal(g4,g3)
    c: Diameter(g3) = 4.5
    c: PointOnObject(g3,g0)
    c: PointOnObject(g4,g0)
    c: PointOnObject(g5,g0)
    c: PointOnObject(g6,g0)
    c: Coincident(g7,g6)
    c: Coincident(g7,g5)
    c: Coincident(g8,g5)
    c: Coincident(g8,g4)
    c: Vertical(g8)
    c: Horizontal(g7)
    c: Equal(g7,g8)
    c: Coincident(g9,g3)
    c: Coincident(g9,g4)
    c: Horizontal(g9)
FEATURE [PartDesign::Pocket] Pocket012
  BaseFeature = -> Revolution001
  Length = 5
  Length2 = 100
  Profile = -> Sketch024
  Reversed = true
  Type = 0
FEATURE [PartDesign::Body] Body006  label="ND91-8"
  Group = -> [Sketch023,Revolution001,Sketch024,Pocket012]
  Origin = -> Origin006
  Placement = pos=(50,-91,253) rot=(0,0,1;3.14159rad)
  Tip = -> Pocket012
FEATURE [Part::Feature] _M1_Series
  Placement = pos=(1.6e-14,-4.4,2.7e-14) rot=(0,1,0;3.14159rad)
  shape: bbox 12.7 x 8.302 x 6.602 mm, 74 faces (baked)
FEATURE [Part::Feature] _M1_Series001
  Placement = pos=(0,0,0) rot=(0,1,0;3.14159rad)
  shape: bbox 12.71 x 10.78 x 10.11 mm, 103 faces (baked)
FEATURE [Part::Feature] _M1_Series002
  Placement = pos=(1.5e-14,4.75,2.4e-14) rot=(0,1,0;3.14159rad)
  shape: bbox 6.458 x 10 x 6.458 mm, 50 faces (baked)
FEATURE [Part::Feature] _M1_Series003
  Placement = pos=(-0.738059,2.04083,-1e-15) rot=(0.108867,0.994056,0;3.14159rad)
  shape: bbox 6.354 x 17.07 x 3.475 mm, 8 faces (baked)
FEATURE [Part::Feature] _M1_Series004
  Placement = pos=(-4.7,-5.87,1.8e-14) rot=(0,1,0;1.5708rad)
  shape: bbox 0.75 x 9.34 x 4 mm, 22 faces (baked)
FEATURE [Part::Feature] _M1_Series005
  Placement = pos=(9e-15,-5.37,2e-15) rot=(0,1,0;1.5708rad)
  shape: bbox 0.75 x 10.84 x 4 mm, 28 faces (baked)
FEATURE [Part::Feature] _M1_Series006
  Placement = pos=(4.7,-5.87,9e-15) rot=(0,1,0;1.5708rad)
  shape: bbox 0.75 x 9.34 x 4 mm, 22 faces (baked)
FEATURE [Part::MultiFuse] Fusion001  label="ToggleSwitchOnOff"
  Placement = pos=(-60,-58,302) rot=(0.57735,-0.57735,-0.57735;2.0944rad)
  Shapes = -> [_M1_Series,_M1_Series001,_M1_Series003,_M1_Series006,_M1_Series005,_M1_Series004,_M1_Series002]
FEATURE [PartDesign::Plane] DatumPlane008
  AttachmentOffset = pos=(0,0,83) rot=(0,0,1;0rad)
  Length = 272.496
  MapMode = 5
  Placement = pos=(0,-83,-1.84e-14) rot=(1,0,0;1.5708rad)
  ResizeMode = 0
  Support = -> [XZ_Plane005]
  Width = 142.496
FEATURE [Sketcher::SketchObject] Sketch025
  ExternalGeometry = -> [Sketch021]
  MapMode = 5
  Placement = pos=(0,-83,-1.84e-14) rot=(1,0,0;1.5708rad)
  Support = -> [DatumPlane008]
  sketch-geometry (35):
    g0: LineSegment StartX=87.1529 StartY=79.3805 StartZ=0 EndX=85.0167 EndY=83.0805 EndZ=0
    g1: LineSegment StartX=85.0167 StartY=83.0805 StartZ=0 EndX=80.7443 EndY=83.0805 EndZ=0
    g2: LineSegment StartX=80.7443 StartY=83.0805 StartZ=0 EndX=78.6081 EndY=79.3805 EndZ=0
    g3: LineSegment StartX=78.6081 StartY=79.3805 StartZ=0 EndX=80.7443 EndY=75.6805 EndZ=0
    g4: LineSegment StartX=80.7443 StartY=75.6805 StartZ=0 EndX=85.0167 EndY=75.6805 EndZ=0
    g5: LineSegment StartX=85.0167 StartY=75.6805 StartZ=0 EndX=87.1529 EndY=79.3805 EndZ=0
    g6: Circle [constr] CenterX=82.8805 CenterY=79.3805 CenterZ=0 NormalX=0 NormalY=0 NormalZ=1 AngleXU=0 Radius=4.27239
    g7: LineSegment StartX=85.0167 StartY=9.91953 StartZ=0 EndX=87.1529 EndY=13.6195 EndZ=0
    g8: LineSegment StartX=87.1529 StartY=13.6195 StartZ=0 EndX=85.0167 EndY=17.3195 EndZ=0
    g9: LineSegment StartX=85.0167 StartY=17.3195 StartZ=0 EndX=80.7443 EndY=17.3195 EndZ=0
    g10: LineSegment StartX=80.7443 StartY=17.3195 StartZ=0 EndX=78.6081 EndY=13.6195 EndZ=0
    g11: LineSegment StartX=78.6081 StartY=13.6195 StartZ=0 EndX=80.7443 EndY=9.91953 EndZ=0
    g12: LineSegment StartX=80.7443 StartY=9.91953 StartZ=0 EndX=85.0167 EndY=9.91953 EndZ=0
    g13: Circle [constr] CenterX=82.8805 CenterY=13.6195 CenterZ=0 NormalX=0 NormalY=0 NormalZ=1 AngleXU=0 Radius=4.27239
    g14: LineSegment StartX=19.2557 StartY=9.91953 StartZ=0 EndX=21.3919 EndY=13.6195 EndZ=0
    g15: LineSegment StartX=21.3919 StartY=13.6195 StartZ=0 EndX=19.2557 EndY=17.3195 EndZ=0
    g16: LineSegment StartX=19.2557 StartY=17.3195 StartZ=0 EndX=14.9833 EndY=17.3195 EndZ=0
    g17: LineSegment StartX=14.9833 StartY=17.3195 StartZ=0 EndX=12.8471 EndY=13.6195 EndZ=0
    g18: LineSegment StartX=12.8471 StartY=13.6195 StartZ=0 EndX=14.9833 EndY=9.91953 EndZ=0
    g19: LineSegment StartX=14.9833 StartY=9.91953 StartZ=0 EndX=19.2557 EndY=9.91953 EndZ=0
    g20: Circle [constr] CenterX=17.1195 CenterY=13.6195 CenterZ=0 NormalX=0 NormalY=0 NormalZ=1 AngleXU=0 Radius=4.27239
    g21: LineSegment StartX=19.2557 StartY=75.6805 StartZ=0 EndX=21.3919 EndY=79.3805 EndZ=0
    g22: LineSegment StartX=21.3919 StartY=79.3805 StartZ=0 EndX=19.2557 EndY=83.0805 EndZ=0
    g23: LineSegment StartX=19.2557 StartY=83.0805 StartZ=0 EndX=14.9833 EndY=83.0805 EndZ=0
    g24: LineSegment StartX=14.9833 StartY=83.0805 StartZ=0 EndX=12.8471 EndY=79.3805 EndZ=0
    g25: LineSegment StartX=12.8471 StartY=79.3805 StartZ=0 EndX=14.9833 EndY=75.6805 EndZ=0
    g26: LineSegment StartX=14.9833 StartY=75.6805 StartZ=0 EndX=19.2557 EndY=75.6805 EndZ=0
    g27: Circle [constr] CenterX=17.1195 CenterY=79.3805 CenterZ=0 NormalX=0 NormalY=0 NormalZ=1 AngleXU=0 Radius=4.27239
    g28: Circle CenterX=50 CenterY=46.5 CenterZ=0 NormalX=0 NormalY=0 NormalZ=1 AngleXU=0 Radius=38.25
    g29: LineSegment StartX=10 StartY=86.5 StartZ=0 EndX=90 EndY=86.5 EndZ=0
    g30: LineSegment StartX=90 StartY=86.5 StartZ=0 EndX=90 EndY=6.5 EndZ=0
    g31: LineSegment StartX=90 StartY=6.5 StartZ=0 EndX=10 EndY=6.5 EndZ=0
    g32: LineSegment StartX=10 StartY=6.5 StartZ=0 EndX=10 EndY=86.5 EndZ=0
    g33: LineSegment [constr] StartX=10 StartY=46.5 StartZ=0 EndX=90 EndY=46.5 EndZ=0
    g34: LineSegment [constr] StartX=50 StartY=86.5 StartZ=0 EndX=50 EndY=6.5 EndZ=0
  constraints (84):
    c: Coincident(g0,g1)
    c: Coincident(g1,g2)
    c: Coincident(g2,g3)
    c: Coincident(g3,g4)
    c: Coincident(g4,g5)
    c: Coincident(g5,g0)
    c: Equal(g0, g1-g5) x5
    c: PointOnObject(g0,g6)
    c: PointOnObject(g1,g6)
    c: PointOnObject(g2,g6)
    c: PointOnObject(g3,g6)
    c: PointOnObject(g4,g6)
    c: PointOnObject(g5,g6)
    c: Coincident(g6,g-5)
    c: Horizontal(g4)
    c: DistanceY(g4,g0) = 7.4
    c: Coincident(g7,g8)
    c: Coincident(g8,g9)
    c: Coincident(g9,g10)
    c: Coincident(g10,g11)
    c: Coincident(g11,g12)
    c: Coincident(g12,g7)
    c: Equal(g7, g8-g12) x5
    c: PointOnObject(g7,g13)
    c: PointOnObject(g8,g13)
    c: PointOnObject(g9,g13)
    c: PointOnObject(g10,g13)
    c: PointOnObject(g11,g13)
    c: PointOnObject(g12,g13)
    c: Coincident(g13,g-6)
    c: Coincident(g14,g15)
    c: Coincident(g15,g16)
    c: Coincident(g16,g17)
    c: Coincident(g17,g18)
    c: Coincident(g18,g19)
    c: Coincident(g19,g14)
    c: Equal(g14, g15-g19) x5
    c: PointOnObject(g14,g20)
    c: PointOnObject(g15,g20)
    c: PointOnObject(g16,g20)
    c: PointOnObject(g17,g20)
    c: PointOnObject(g18,g20)
    c: PointOnObject(g19,g20)
    c: Coincident(g20,g-7)
    c: Coincident(g21,g22)
    c: Coincident(g22,g23)
    c: Coincident(g23,g24)
    c: Coincident(g24,g25)
    c: Coincident(g25,g26)
    c: Coincident(g26,g21)
    c: Equal(g21, g22-g26) x5
    c: PointOnObject(g21,g27)
    c: PointOnObject(g22,g27)
    c: PointOnObject(g23,g27)
    c: PointOnObject(g24,g27)
    c: PointOnObject(g25,g27)
    c: PointOnObject(g26,g27)
    c: Coincident(g27,g-3)
    c: Horizontal(g19)
    c: Horizontal(g12)
    c: Equal(g9,g16)
    c: Equal(g16,g26)
    c: Equal(g26,g4)
    c: Horizontal(g26)
    c: Coincident(g28,g-4)
    c: Equal(g28,g-4)
    c: Coincident(g29,g30)
    c: Coincident(g30,g31)
    c: Coincident(g31,g32)
    c: Coincident(g32,g29)
    c: Horizontal(g29)
    c: Horizontal(g31)
    c: Vertical(g30)
    c: Vertical(g32)
    c: Equal(g31,g30)
    c: PointOnObject(g33,g32)
    c: Horizontal(g33)
    c: PointOnObject(g34,g31)
    c: Vertical(g34)
    c: Symmetric(g29,g29,g34)
    c: Symmetric(g30,g29,g33)
    c: PointOnObject(g28,g34)
    c: PointOnObject(g28,g33)
    c: DistanceY(g30,g30) = 80
FEATURE [PartDesign::Pad] Pad012
  BaseFeature = -> Pocket011
  Length = 3.5
  Length2 = 100
  Profile = -> Sketch025
  Reversed = true
  Type = 0
FEATURE [PartDesign::PolarPattern] PolarPattern003
  Angle = 360
  Axis = -> Z_Axis005
  BaseFeature = -> Pad012
  Occurrences = 2
  Originals = -> [Pad012]
FEATURE [PartDesign::Chamfer] Chamfer001
  Base = -> PolarPattern003 [Edge153,Edge156,Edge154,Edge155,Edge199,Edge196,Edge198,Edge197]
  BaseFeature = -> PolarPattern003
  Size = 3.499
FEATURE [Sketcher::SketchObject] Sketch026
  MapMode = 5
  Placement = pos=(0,0,0) rot=(1,0,0;1.5708rad)
  Support = -> [XZ_Plane010]
  sketch-geometry (1):
    g0: Circle CenterX=0 CenterY=0 CenterZ=0 NormalX=0 NormalY=0 NormalZ=1 AngleXU=0 Radius=32.5
  constraints (2):
    c: Coincident(g0,g-1)
    c: Radius(g0) = 32.5
FEATURE [PartDesign::Pad] Pad013
  Length = 3
  Length2 = 100
  Placement = pos=(0,0,0) rot=(1,0,0;1.5708rad)
  Profile = -> Sketch026
  Type = 0
FEATURE [Sketcher::SketchObject] Sketch027
  MapMode = 5
  Placement = pos=(0,0,0) rot=(-1,0,0;1.5708rad)
  Support = -> [Pad013]
  sketch-geometry (1):
    g0: Circle CenterX=0 CenterY=0 CenterZ=0 NormalX=0 NormalY=0 NormalZ=1 AngleXU=0 Radius=22.5
  constraints (2):
    c: Coincident(g0,g-1)
    c: Radius(g0) = 22.5
FEATURE [PartDesign::Pad] Pad014
  BaseFeature = -> Pad013
  Length = 16.5
  Length2 = 100
  Placement = pos=(0,0,0) rot=(1,0,0;1.5708rad)
  Profile = -> Sketch027
  Type = 0
FEATURE [Sketcher::SketchObject] Sketch028
  MapMode = 5
  Placement = pos=(0,-3,7e-16) rot=(1,0,0;1.5708rad)
  Support = -> [Pad014]
  sketch-geometry (9):
    g0: Circle [constr] CenterX=0 CenterY=0 CenterZ=0 NormalX=0 NormalY=0 NormalZ=1 AngleXU=0 Radius=27.85
    g1: Circle CenterX=-19.6929 CenterY=19.6929 CenterZ=0 NormalX=0 NormalY=0 NormalZ=1 AngleXU=0 Radius=1.75
    g2: Circle CenterX=19.6929 CenterY=19.6929 CenterZ=0 NormalX=0 NormalY=0 NormalZ=1 AngleXU=0 Radius=1.75
    g3: Circle CenterX=19.6929 CenterY=-19.6929 CenterZ=0 NormalX=0 NormalY=0 NormalZ=1 AngleXU=0 Radius=1.75
    g4: Circle CenterX=-19.6929 CenterY=-19.6929 CenterZ=0 NormalX=0 NormalY=0 NormalZ=1 AngleXU=0 Radius=1.75
    g5: LineSegment [constr] StartX=-19.6929 StartY=19.6929 StartZ=0 EndX=19.6929 EndY=19.6929 EndZ=0
    g6: LineSegment [constr] StartX=-19.6929 StartY=19.6929 StartZ=0 EndX=-19.6929 EndY=-19.6929 EndZ=0
    g7: LineSegment [constr] StartX=-19.6929 StartY=-19.6929 StartZ=0 EndX=19.6929 EndY=-19.6929 EndZ=0
    g8: LineSegment [constr] StartX=19.6929 StartY=-19.6929 StartZ=0 EndX=19.6929 EndY=19.6929 EndZ=0
  constraints (22):
    c: Coincident(g0,g-1)
    c: PointOnObject(g1,g0)
    c: PointOnObject(g2,g0)
    c: PointOnObject(g3,g0)
    c: PointOnObject(g4,g0)
    c: Radius(g2) = 1.75
    c: Equal(g1,g4)
    c: Equal(g4,g3)
    c: Equal(g3,g2)
    c: Coincident(g5,g1)
    c: Coincident(g5,g2)
    c: Coincident(g6,g1)
    c: Coincident(g6,g4)
    c: Coincident(g7,g4)
    c: Coincident(g7,g3)
    c: Coincident(g8,g3)
    c: Coincident(g8,g2)
    c: Vertical(g8)
    c: Horizontal(g5)
    c: Horizontal(g7)
    c: Equal(g6,g5)
    c: Radius(g0) = 27.85
FEATURE [PartDesign::Pocket] Pocket013
  BaseFeature = -> Pad014
  Length = 5
  Length2 = 100
  Placement = pos=(0,0,0) rot=(1,0,0;1.5708rad)
  Profile = -> Sketch028
  Type = 0
FEATURE [PartDesign::Body] Body010  label="ND28F-6"
  Group = -> [Sketch026,Pad013,Sketch027,Pad014,Sketch028,Pocket013]
  Origin = -> Origin010
  Placement = pos=(-50,-87,254) rot=(0,0,1;0rad)
  Tip = -> Pocket013
FEATURE [Sketcher::SketchObject] Sketch029
  ExternalGeometry = -> [Chamfer001]
  MapMode = 5
  Placement = pos=(0,-90,2e-14) rot=(1,0,0;1.5708rad)
  Support = -> [DatumPlane007]
  sketch-geometry (1):
    g0: Circle CenterX=-50 CenterY=46.5 CenterZ=0 NormalX=0 NormalY=0 NormalZ=1 AngleXU=0 Radius=33
  constraints (2):
    c: Coincident(g0,g-3)
    c: Diameter(g0) = 66
FEATURE [PartDesign::Pocket] Pocket014
  BaseFeature = -> Chamfer001
  Length = 3
  Length2 = 100
  Profile = -> Sketch029
  Type = 0
FEATURE [Sketcher::SketchObject] Sketch030
  ExternalGeometry = -> [Pocket014]
  MapMode = 5
  Placement = pos=(0,-83,-1.84e-14) rot=(1,0,0;1.5708rad)
  Support = -> [DatumPlane008]
  sketch-geometry (35):
    g0: Circle CenterX=-50 CenterY=46.5 CenterZ=0 NormalX=0 NormalY=0 NormalZ=1 AngleXU=0 Radius=22
    g1: LineSegment StartX=-71.5404 StartY=62.9929 StartZ=0 EndX=-67.8454 EndY=62.9929 EndZ=0
    g2: LineSegment StartX=-67.8454 StartY=62.9929 StartZ=0 EndX=-65.9979 EndY=66.1929 EndZ=0
    g3: LineSegment StartX=-65.9979 StartY=66.1929 StartZ=0 EndX=-67.8454 EndY=69.3929 EndZ=0
    g4: LineSegment StartX=-67.8454 StartY=69.3929 StartZ=0 EndX=-71.5404 EndY=69.3929 EndZ=0
    g5: LineSegment StartX=-71.5404 StartY=69.3929 StartZ=0 EndX=-73.388 EndY=66.1929 EndZ=0
    g6: LineSegment StartX=-73.388 StartY=66.1929 StartZ=0 EndX=-71.5404 EndY=62.9929 EndZ=0
    g7: Circle [constr] CenterX=-69.6929 CenterY=66.1929 CenterZ=0 NormalX=0 NormalY=0 NormalZ=1 AngleXU=0 Radius=3.69504
    g8: LineSegment StartX=-32.1546 StartY=62.9929 StartZ=0 EndX=-28.4596 EndY=62.9929 EndZ=0
    g9: LineSegment StartX=-28.4596 StartY=62.9929 StartZ=0 EndX=-26.612 EndY=66.1929 EndZ=0
    g10: LineSegment StartX=-26.612 StartY=66.1929 StartZ=0 EndX=-28.4596 EndY=69.3929 EndZ=0
    g11: LineSegment StartX=-28.4596 StartY=69.3929 StartZ=0 EndX=-32.1546 EndY=69.3929 EndZ=0
    g12: LineSegment StartX=-32.1546 StartY=69.3929 StartZ=0 EndX=-34.0021 EndY=66.1929 EndZ=0
    g13: LineSegment StartX=-34.0021 StartY=66.1929 StartZ=0 EndX=-32.1546 EndY=62.9929 EndZ=0
    g14: Circle [constr] CenterX=-30.3071 CenterY=66.1929 CenterZ=0 NormalX=0 NormalY=0 NormalZ=1 AngleXU=0 Radius=3.69504
    g15: LineSegment StartX=-32.1546 StartY=23.6071 StartZ=0 EndX=-28.4596 EndY=23.6071 EndZ=0
    g16: LineSegment StartX=-28.4596 StartY=23.6071 StartZ=0 EndX=-26.612 EndY=26.8071 EndZ=0
    g17: LineSegment StartX=-26.612 StartY=26.8071 StartZ=0 EndX=-28.4596 EndY=30.0071 EndZ=0
    g18: LineSegment StartX=-28.4596 StartY=30.0071 StartZ=0 EndX=-32.1546 EndY=30.0071 EndZ=0
    g19: LineSegment StartX=-32.1546 StartY=30.0071 StartZ=0 EndX=-34.0021 EndY=26.8071 EndZ=0
    g20: LineSegment StartX=-34.0021 StartY=26.8071 StartZ=0 EndX=-32.1546 EndY=23.6071 EndZ=0
    g21: Circle [constr] CenterX=-30.3071 CenterY=26.8071 CenterZ=0 NormalX=0 NormalY=0 NormalZ=1 AngleXU=0 Radius=3.69504
    g22: LineSegment StartX=-71.5404 StartY=23.6071 StartZ=0 EndX=-67.8454 EndY=23.6071 EndZ=0
    g23: LineSegment StartX=-67.8454 StartY=23.6071 StartZ=0 EndX=-65.9979 EndY=26.8071 EndZ=0
    g24: LineSegment StartX=-65.9979 StartY=26.8071 StartZ=0 EndX=-67.8454 EndY=30.0071 EndZ=0
    g25: LineSegment StartX=-67.8454 StartY=30.0071 StartZ=0 EndX=-71.5404 EndY=30.0071 EndZ=0
    g26: LineSegment StartX=-71.5404 StartY=30.0071 StartZ=0 EndX=-73.388 EndY=26.8071 EndZ=0
    g27: LineSegment StartX=-73.388 StartY=26.8071 StartZ=0 EndX=-71.5404 EndY=23.6071 EndZ=0
    g28: Circle [constr] CenterX=-69.6929 CenterY=26.8071 CenterZ=0 NormalX=0 NormalY=0 NormalZ=1 AngleXU=0 Radius=3.69504
    g29: LineSegment StartX=-80 StartY=76.5 StartZ=0 EndX=-20 EndY=76.5 EndZ=0
    g30: LineSegment StartX=-20 StartY=76.5 StartZ=0 EndX=-20 EndY=16.5 EndZ=0
    g31: LineSegment StartX=-20 StartY=16.5 StartZ=0 EndX=-80 EndY=16.5 EndZ=0
    g32: LineSegment StartX=-80 StartY=16.5 StartZ=0 EndX=-80 EndY=76.5 EndZ=0
    g33: LineSegment [constr] StartX=-80 StartY=46.5 StartZ=0 EndX=-20 EndY=46.5 EndZ=0
    g34: LineSegment [constr] StartX=-50 StartY=76.5 StartZ=0 EndX=-50 EndY=16.5 EndZ=0
  constraints (84):
    c: Coincident(g0,g-7)
    c: Equal(g0,g-7)
    c: Coincident(g1,g2)
    c: Coincident(g2,g3)
    c: Coincident(g3,g4)
    c: Coincident(g4,g5)
    c: Coincident(g5,g6)
    c: Coincident(g6,g1)
    c: Equal(g1, g2-g6) x5
    c: PointOnObject(g1,g7)
    c: PointOnObject(g2,g7)
    c: PointOnObject(g3,g7)
    c: PointOnObject(g4,g7)
    c: PointOnObject(g5,g7)
    c: PointOnObject(g6,g7)
    c: Coincident(g7,g-3)
    c: Coincident(g8,g9)
    c: Coincident(g9,g10)
    c: Coincident(g10,g11)
    c: Coincident(g11,g12)
    c: Coincident(g12,g13)
    c: Coincident(g13,g8)
    c: Equal(g8, g9-g13) x5
    c: PointOnObject(g8,g14)
    c: PointOnObject(g9,g14)
    c: PointOnObject(g10,g14)
    c: PointOnObject(g11,g14)
    c: PointOnObject(g12,g14)
    c: PointOnObject(g13,g14)
    c: Coincident(g14,g-4)
    c: Coincident(g15,g16)
    c: Coincident(g16,g17)
    c: Coincident(g17,g18)
    c: Coincident(g18,g19)
    c: Coincident(g19,g20)
    c: Coincident(g20,g15)
    c: Equal(g15, g16-g20) x5
    c: PointOnObject(g15,g21)
    c: PointOnObject(g16,g21)
    c: PointOnObject(g17,g21)
    c: PointOnObject(g18,g21)
    c: PointOnObject(g19,g21)
    c: PointOnObject(g20,g21)
    c: Coincident(g21,g-5)
    c: Coincident(g22,g23)
    c: Coincident(g23,g24)
    c: Coincident(g24,g25)
    c: Coincident(g25,g26)
    c: Coincident(g26,g27)
    c: Coincident(g27,g22)
    c: Equal(g22, g23-g27) x5
    c: PointOnObject(g22,g28)
    c: PointOnObject(g23,g28)
    c: PointOnObject(g24,g28)
    c: PointOnObject(g25,g28)
    c: PointOnObject(g26,g28)
    c: PointOnObject(g27,g28)
    c: Coincident(g28,g-6)
    c: Horizontal(g15)
    c: Horizontal(g8)
    c: Horizontal(g1)
    c: Horizontal(g22)
    c: DistanceY(g8,g10) = 6.4
    c: Equal(g1,g10)
    c: Equal(g17,g24)
    c: Equal(g24,g10)
    c: Coincident(g29,g30)
    c: Coincident(g30,g31)
    c: Coincident(g31,g32)
    c: Coincident(g32,g29)
    c: Horizontal(g29)
    c: Horizontal(g31)
    c: Vertical(g30)
    c: Vertical(g32)
    c: PointOnObject(g33,g32)
    c: Horizontal(g33)
    c: PointOnObject(g34,g31)
    c: Vertical(g34)
    c: Equal(g32,g29)
    c: Symmetric(g29,g29,g34)
    c: Symmetric(g30,g29,g33)
    c: PointOnObject(g0,g34)
    c: PointOnObject(g0,g33)
    c: DistanceY(g30,g30) = 60
FEATURE [PartDesign::Pad] Pad015
  BaseFeature = -> Pocket014
  Length = 3.5
  Length2 = 100
  Profile = -> Sketch030
  Reversed = true
  Type = 0
FEATURE [PartDesign::Chamfer] Chamfer002
  Base = -> Pad015 [Edge7,Edge8,Edge10,Edge9]
  BaseFeature = -> Pad015
  Size = 3.499
FEATURE [Sketcher::SketchObject] Sketch031
  MapMode = 5
  Support = -> [DatumPlane005]
  sketch-geometry (12):
    g0: LineSegment [constr] StartX=17.5 StartY=61.46 StartZ=0 EndX=92.5 EndY=61.46 EndZ=0
    g1: LineSegment [constr] StartX=92.5 StartY=61.46 StartZ=0 EndX=92.5 EndY=-2 EndZ=0
    g2: LineSegment [constr] StartX=92.5 StartY=-2 StartZ=0 EndX=17.5 EndY=-2 EndZ=0
    g3: LineSegment [constr] StartX=17.5 StartY=-2 StartZ=0 EndX=17.5 EndY=61.46 EndZ=0
    g4: Circle [constr] CenterX=17.5 CenterY=61.46 CenterZ=0 NormalX=0 NormalY=0 NormalZ=1 AngleXU=0 Radius=2.25
    g5: Circle [constr] CenterX=92.5 CenterY=61.46 CenterZ=0 NormalX=0 NormalY=0 NormalZ=1 AngleXU=0 Radius=2.25
    g6: Circle [constr] CenterX=92.5 CenterY=-2 CenterZ=0 NormalX=0 NormalY=0 NormalZ=1 AngleXU=0 Radius=2.25
    g7: Circle [constr] CenterX=17.5 CenterY=-2 CenterZ=0 NormalX=0 NormalY=0 NormalZ=1 AngleXU=0 Radius=2.25
    g8: Circle CenterX=17.5 CenterY=61.46 CenterZ=0 NormalX=0 NormalY=0 NormalZ=1 AngleXU=0 Radius=7.5
    g9: Circle CenterX=92.5 CenterY=61.46 CenterZ=0 NormalX=0 NormalY=0 NormalZ=1 AngleXU=0 Radius=7.5
    g10: Circle CenterX=92.5 CenterY=-2 CenterZ=0 NormalX=0 NormalY=0 NormalZ=1 AngleXU=0 Radius=7.5
    g11: Circle CenterX=17.5 CenterY=-2 CenterZ=0 NormalX=0 NormalY=0 NormalZ=1 AngleXU=0 Radius=7.5
  constraints (28):
    c: Coincident(g0,g1)
    c: Coincident(g1,g2)
    c: Coincident(g2,g3)
    c: Coincident(g3,g0)
    c: Horizontal(g0)
    c: Horizontal(g2)
    c: Vertical(g1)
    c: Vertical(g3)
    c: DistanceY(g3,g3) = 63.46
    c: DistanceX(g0,g0) = 75
    c: Coincident(g4,g0)
    c: Coincident(g5,g0)
    c: Coincident(g6,g1)
    c: Coincident(g7,g2)
    c: Equal(g7,g4)
    c: Equal(g4,g6)
    c: Equal(g6,g5)
    c: Diameter(g5) = 4.5
    c: DistanceY(g7) = -2
    c: DistanceX(g-1,g7) = 17.5
    c: Coincident(g8,g0)
    c: Coincident(g9,g0)
    c: Coincident(g10,g1)
    c: Coincident(g11,g2)
    c: Equal(g11,g8)
    c: Equal(g8,g9)
    c: Equal(g9,g10)
    c: Diameter(g9) = 15
FEATURE [PartDesign::Pad] Pad016
  BaseFeature = -> Chamfer002
  Length = 7
  Length2 = 100
  Profile = -> Sketch031
  Reversed = true
  Type = 0
FEATURE [Sketcher::SketchObject] Sketch032
  ExternalGeometry = -> [Pad016]
  MapMode = 5
  Placement = pos=(0,0,-7) rot=(1,0,0;3.14159rad)
  Support = -> [Pad016]
  sketch-geometry (28):
    g0: LineSegment StartX=19.9537 StartY=-2.25 StartZ=0 EndX=22.4075 EndY=2 EndZ=0
    g1: LineSegment StartX=22.4075 StartY=2 StartZ=0 EndX=19.9537 EndY=6.25 EndZ=0
    g2: LineSegment StartX=19.9537 StartY=6.25 StartZ=0 EndX=15.0463 EndY=6.25 EndZ=0
    g3: LineSegment StartX=15.0463 StartY=6.25 StartZ=0 EndX=12.5925 EndY=2 EndZ=0
    g4: LineSegment StartX=12.5925 StartY=2 StartZ=0 EndX=15.0463 EndY=-2.25 EndZ=0
    g5: LineSegment StartX=15.0463 StartY=-2.25 StartZ=0 EndX=19.9537 EndY=-2.25 EndZ=0
    g6: Circle [constr] CenterX=17.5 CenterY=2 CenterZ=0 NormalX=0 NormalY=0 NormalZ=1 AngleXU=0 Radius=4.90748
    g7: LineSegment StartX=94.9537 StartY=-2.25 StartZ=0 EndX=97.4075 EndY=2 EndZ=0
    g8: LineSegment StartX=97.4075 StartY=2 StartZ=0 EndX=94.9537 EndY=6.25 EndZ=0
    g9: LineSegment StartX=94.9537 StartY=6.25 StartZ=0 EndX=90.0463 EndY=6.25 EndZ=0
    g10: LineSegment StartX=90.0463 StartY=6.25 StartZ=0 EndX=87.5925 EndY=2 EndZ=0
    g11: LineSegment StartX=87.5925 StartY=2 StartZ=0 EndX=90.0463 EndY=-2.25 EndZ=0
    g12: LineSegment StartX=90.0463 StartY=-2.25 StartZ=0 EndX=94.9537 EndY=-2.25 EndZ=0
    g13: Circle [constr] CenterX=92.5 CenterY=2 CenterZ=0 NormalX=0 NormalY=0 NormalZ=1 AngleXU=0 Radius=4.90748
    g14: LineSegment StartX=94.9537 StartY=-65.71 StartZ=0 EndX=97.4075 EndY=-61.46 EndZ=0
    g15: LineSegment StartX=97.4075 StartY=-61.46 StartZ=0 EndX=94.9537 EndY=-57.21 EndZ=0
    g16: LineSegment StartX=94.9537 StartY=-57.21 StartZ=0 EndX=90.0463 EndY=-57.21 EndZ=0
    g17: LineSegment StartX=90.0463 StartY=-57.21 StartZ=0 EndX=87.5925 EndY=-61.46 EndZ=0
    g18: LineSegment StartX=87.5925 StartY=-61.46 StartZ=0 EndX=90.0463 EndY=-65.71 EndZ=0
    g19: LineSegment StartX=90.0463 StartY=-65.71 StartZ=0 EndX=94.9537 EndY=-65.71 EndZ=0
    g20: Circle [constr] CenterX=92.5 CenterY=-61.46 CenterZ=0 NormalX=0 NormalY=0 NormalZ=1 AngleXU=0 Radius=4.90748
    g21: LineSegment StartX=19.9537 StartY=-65.71 StartZ=0 EndX=22.4075 EndY=-61.46 EndZ=0
    g22: LineSegment StartX=22.4075 StartY=-61.46 StartZ=0 EndX=19.9537 EndY=-57.21 EndZ=0
    g23: LineSegment StartX=19.9537 StartY=-57.21 StartZ=0 EndX=15.0463 EndY=-57.21 EndZ=0
    g24: LineSegment StartX=15.0463 StartY=-57.21 StartZ=0 EndX=12.5925 EndY=-61.46 EndZ=0
    g25: LineSegment StartX=12.5925 StartY=-61.46 StartZ=0 EndX=15.0463 EndY=-65.71 EndZ=0
    g26: LineSegment StartX=15.0463 StartY=-65.71 StartZ=0 EndX=19.9537 EndY=-65.71 EndZ=0
    g27: Circle [constr] CenterX=17.5 CenterY=-61.46 CenterZ=0 NormalX=0 NormalY=0 NormalZ=1 AngleXU=0 Radius=4.90748
  constraints (64):
    c: Coincident(g0,g1)
    c: Coincident(g1,g2)
    c: Coincident(g2,g3)
    c: Coincident(g3,g4)
    c: Coincident(g4,g5)
    c: Coincident(g5,g0)
    c: Equal(g0, g1-g5) x5
    c: PointOnObject(g0,g6)
    c: PointOnObject(g1,g6)
    c: PointOnObject(g2,g6)
    c: PointOnObject(g3,g6)
    c: PointOnObject(g4,g6)
    c: PointOnObject(g5,g6)
    c: Coincident(g6,g-3)
    c: Coincident(g7,g8)
    c: Coincident(g8,g9)
    c: Coincident(g9,g10)
    c: Coincident(g10,g11)
    c: Coincident(g11,g12)
    c: Coincident(g12,g7)
    c: Equal(g7, g8-g12) x5
    c: PointOnObject(g7,g13)
    c: PointOnObject(g8,g13)
    c: PointOnObject(g9,g13)
    c: PointOnObject(g10,g13)
    c: PointOnObject(g11,g13)
    c: PointOnObject(g12,g13)
    c: Coincident(g13,g-4)
    c: Coincident(g14,g15)
    c: Coincident(g15,g16)
    c: Coincident(g16,g17)
    c: Coincident(g17,g18)
    c: Coincident(g18,g19)
    c: Coincident(g19,g14)
    c: Equal(g14, g15-g19) x5
    c: PointOnObject(g14,g20)
    c: PointOnObject(g15,g20)
    c: PointOnObject(g16,g20)
    c: PointOnObject(g17,g20)
    c: PointOnObject(g18,g20)
    c: PointOnObject(g19,g20)
    c: Coincident(g20,g-5)
    c: Coincident(g21,g22)
    c: Coincident(g22,g23)
    c: Coincident(g23,g24)
    c: Coincident(g24,g25)
    c: Coincident(g25,g26)
    c: Coincident(g26,g21)
    c: Equal(g21, g22-g26) x5
    c: PointOnObject(g21,g27)
    c: PointOnObject(g22,g27)
    c: PointOnObject(g23,g27)
    c: PointOnObject(g24,g27)
    c: PointOnObject(g25,g27)
    c: PointOnObject(g26,g27)
    c: Coincident(g27,g-6)
    c: Horizontal(g26)
    c: Horizontal(g19)
    c: Horizontal(g12)
    c: Horizontal(g5)
    c: Equal(g6,g13)
    c: Equal(g13,g27)
    c: Equal(g27,g20)
    c: DistanceY(g0,g1) = 8.5
FEATURE [PartDesign::Pocket] Pocket015
  BaseFeature = -> Pad016
  Length = 4
  Length2 = 100
  Profile = -> Sketch032
  Type = 0
FEATURE [Sketcher::SketchObject] Sketch033
  ExternalGeometry = -> [Pocket015]
  MapMode = 5
  Placement = pos=(0,0,-7) rot=(1,0,0;3.14159rad)
  Support = -> [Pocket015]
  sketch-geometry (4):
    g0: Circle CenterX=17.5 CenterY=2 CenterZ=0 NormalX=0 NormalY=0 NormalZ=1 AngleXU=0 Radius=2.25
    g1: Circle CenterX=92.5 CenterY=2 CenterZ=0 NormalX=0 NormalY=0 NormalZ=1 AngleXU=0 Radius=2.25
    g2: Circle CenterX=92.5 CenterY=-61.46 CenterZ=0 NormalX=0 NormalY=0 NormalZ=1 AngleXU=0 Radius=2.25
    g3: Circle CenterX=17.5 CenterY=-61.46 CenterZ=0 NormalX=0 NormalY=0 NormalZ=1 AngleXU=0 Radius=2.25
  constraints (8):
    c: Coincident(g0,g-3)
    c: Coincident(g1,g-4)
    c: Coincident(g2,g-5)
    c: Coincident(g3,g-6)
    c: Equal(g3,g2)
    c: Equal(g2,g1)
    c: Equal(g1,g0)
    c: Diameter(g1) = 4.5
FEATURE [PartDesign::Pocket] Pocket016
  BaseFeature = -> Pocket015
  Length = 8
  Length2 = 100
  Profile = -> Sketch033
  Type = 0
FEATURE [Sketcher::SketchObject] Sketch034
  ExternalGeometry = -> [Pocket016]
  MapMode = 5
  Placement = pos=(0,0,100) rot=(0,0,1;0rad)
  Support = -> [Pocket016]
  sketch-geometry (10):
    g0: LineSegment StartX=-7 StartY=83 StartZ=0 EndX=7 EndY=83 EndZ=0
    g1: LineSegment StartX=7 StartY=83 StartZ=0 EndX=7 EndY=63 EndZ=0
    g2: LineSegment StartX=7 StartY=63 StartZ=0 EndX=-7 EndY=63 EndZ=0
    g3: LineSegment StartX=-7 StartY=63 StartZ=0 EndX=-7 EndY=83 EndZ=0
    g4: LineSegment StartX=-7 StartY=-63 StartZ=0 EndX=7 EndY=-63 EndZ=0
    g5: LineSegment StartX=7 StartY=-63 StartZ=0 EndX=7 EndY=-83 EndZ=0
    g6: LineSegment StartX=7 StartY=-83 StartZ=0 EndX=-7 EndY=-83 EndZ=0
    g7: LineSegment StartX=-7 StartY=-83 StartZ=0 EndX=-7 EndY=-63 EndZ=0
    g8: Circle CenterX=0 CenterY=-70 CenterZ=0 NormalX=0 NormalY=0 NormalZ=1 AngleXU=0 Radius=3.25
    g9: Circle CenterX=0 CenterY=70 CenterZ=0 NormalX=0 NormalY=0 NormalZ=1 AngleXU=0 Radius=3.25
  constraints (24):
    c: Coincident(g0,g1)
    c: Coincident(g1,g2)
    c: Coincident(g2,g3)
    c: Coincident(g3,g0)
    c: Horizontal(g0)
    c: Horizontal(g2)
    c: Vertical(g1)
    c: Vertical(g3)
    c: Coincident(g0,g-6)
    c: Coincident(g1,g-5)
    c: Coincident(g4,g5)
    c: Coincident(g5,g6)
    c: Coincident(g6,g7)
    c: Coincident(g7,g4)
    c: Horizontal(g4)
    c: Horizontal(g6)
    c: Vertical(g5)
    c: Vertical(g7)
    c: Coincident(g4,g-8)
    c: Coincident(g5,g-10)
    c: Equal(g8,g-11)
    c: Coincident(g8,g-11)
    c: Coincident(g9,g-12)
    c: Equal(g9,g-12)
FEATURE [PartDesign::Pad] Pad017
  BaseFeature = -> Pocket016
  Length = 35
  Length2 = 100
  Profile = -> Sketch034
  Reversed = true
  Type = 0
FEATURE [Sketcher::SketchObject] Sketch035
  ExternalGeometry = -> [Pad017]
  MapMode = 5
  Placement = pos=(7,0,0) rot=(0.57735,0.57735,0.57735;2.0944rad)
  Support = -> [Pad017]
  sketch-geometry (6):
    g0: LineSegment StartX=-82.501 StartY=65 StartZ=0 EndX=-63 EndY=92 EndZ=0
    g1: LineSegment StartX=-63 StartY=92 StartZ=0 EndX=-63 EndY=65 EndZ=0
    g2: LineSegment StartX=-63 StartY=65 StartZ=0 EndX=-82.501 EndY=65 EndZ=0
    g3: LineSegment StartX=63 StartY=65 StartZ=0 EndX=63 EndY=92 EndZ=0
    g4: LineSegment StartX=63 StartY=92 StartZ=0 EndX=83 EndY=65 EndZ=0
    g5: LineSegment StartX=83 StartY=65 StartZ=0 EndX=63 EndY=65 EndZ=0
  constraints (14):
    c: Coincident(g0,g-8)
    c: Coincident(g1,g0)
    c: Coincident(g1,g-8)
    c: Vertical(g1)
    c: Coincident(g2,g1)
    c: Coincident(g2,g0)
    c: Distance(g0,g-7) = 8
    c: Coincident(g3,g-4)
    c: Vertical(g3)
    c: Coincident(g4,g3)
    c: Coincident(g4,g-4)
    c: Coincident(g5,g4)
    c: Coincident(g5,g3)
    c: Distance(g3,g-5) = 8
FEATURE [PartDesign::Pocket] Pocket017
  BaseFeature = -> Pad017
  Length = 14
  Length2 = 100
  Profile = -> Sketch035
  Type = 0
FEATURE [PartDesign::Plane] DatumPlane009
  AttachmentOffset = pos=(0,0,120) rot=(0,0,1;0rad)
  Length = 208.142
  MapMode = 5
  Placement = pos=(120,-2.66e-14,2.66e-14) rot=(0.57735,0.57735,0.57735;2.0944rad)
  ResizeMode = 0
  Support = -> [YZ_Plane005]
  Width = 138.142
FEATURE [Sketcher::SketchObject] Sketch036
  MapMode = 5
  Placement = pos=(120,-2.66e-14,2.66e-14) rot=(0.57735,0.57735,0.57735;2.0944rad)
  Support = -> [DatumPlane009]
  sketch-geometry (25):
    g0: LineSegment StartX=-80 StartY=-7 StartZ=0 EndX=80 EndY=33 EndZ=0
    g1: LineSegment StartX=0 StartY=-7 StartZ=0 EndX=80 EndY=13 EndZ=0
    g2: LineSegment [constr] StartX=80 StartY=33 StartZ=0 EndX=80 EndY=13 EndZ=0
    g3: LineSegment StartX=-80 StartY=-7 StartZ=0 EndX=-80 EndY=13 EndZ=0
    g4: LineSegment [constr] StartX=0 StartY=100 StartZ=0 EndX=80 EndY=100 EndZ=0
    g5: LineSegment [constr] StartX=80 StartY=100 StartZ=0 EndX=80 EndY=33 EndZ=0
    g6: LineSegment StartX=-80 StartY=13 StartZ=0 EndX=80 EndY=53 EndZ=0
    g7: LineSegment [constr] StartX=-80 StartY=13 StartZ=0 EndX=-80 EndY=33 EndZ=0
    g8: LineSegment StartX=-80 StartY=33 StartZ=0 EndX=80 EndY=73 EndZ=0
    g9: LineSegment StartX=-80 StartY=53 StartZ=0 EndX=80 EndY=93 EndZ=0
    g10: LineSegment StartX=-80 StartY=33 StartZ=0 EndX=-80 EndY=53 EndZ=0
    g11: LineSegment StartX=-80 StartY=73 StartZ=0 EndX=28 EndY=100 EndZ=0
    g12: LineSegment [constr] StartX=-80 StartY=53 StartZ=0 EndX=-80 EndY=73 EndZ=0
    g13: LineSegment [constr] StartX=28 StartY=100 StartZ=0 EndX=80 EndY=100 EndZ=0
    g14: LineSegment [constr] StartX=80 StartY=100 StartZ=0 EndX=80 EndY=93 EndZ=0
    g15: LineSegment StartX=-80 StartY=73 StartZ=0 EndX=-80 EndY=93 EndZ=0
    g16: LineSegment [constr] StartX=-80 StartY=93 StartZ=0 EndX=-80 EndY=100 EndZ=0
    g17: LineSegment StartX=-80 StartY=93 StartZ=0 EndX=-52 EndY=100 EndZ=0
    g18: LineSegment [constr] StartX=-80 StartY=100 StartZ=0 EndX=-52 EndY=100 EndZ=0
    g19: LineSegment [constr] StartX=80 StartY=13 StartZ=0 EndX=80 EndY=-7 EndZ=0
    g20: LineSegment StartX=0 StartY=-7 StartZ=0 EndX=80 EndY=-7 EndZ=0
    g21: LineSegment StartX=80 StartY=-7 StartZ=0 EndX=80 EndY=13 EndZ=0
    g22: LineSegment StartX=80 StartY=33 StartZ=0 EndX=80 EndY=53 EndZ=0
    g23: LineSegment StartX=80 StartY=73 StartZ=0 EndX=80 EndY=93 EndZ=0
    g24: LineSegment StartX=-52 StartY=100 StartZ=0 EndX=28 EndY=100 EndZ=0
  constraints (68):
    c: PointOnObject(g1,g-2)
    c: Coincident(g2,g0)
    c: Coincident(g2,g1)
    c: Vertical(g2)
    c: DistanceY(g-1,g1) = 13
    c: DistanceY(g2,g2) = 20
    c: DistanceX(g0,g1) = 80
    c: DistanceX(g-1,g1) = 80
    c: Coincident(g3,g0)
    c: Vertical(g3)
    c: DistanceY(g3,g3) = 20
    c: PointOnObject(g4,g-2)
    c: Horizontal(g4)
    c: DistanceX(g4,g4) = 80
    c: DistanceY(g-1,g4) = 100
    c: Coincident(g5,g4)
    c: Coincident(g5,g0)
    c: Coincident(g6,g3)
    c: PointOnObject(g6,g5)
    c: Parallel(g0,g6)
    c: Coincident(g7,g6)
    c: Vertical(g7)
    c: Coincident(g8,g7)
    c: PointOnObject(g8,g5)
    c: Equal(g7,g3)
    c: PointOnObject(g9,g5)
    c: Coincident(g10,g7)
    c: Coincident(g10,g9)
    c: Vertical(g10)
    c: Equal(g10,g3)
    c: Parallel(g8,g9)
    c: PointOnObject(g11,g4)
    c: Coincident(g12,g9)
    c: Coincident(g12,g11)
    c: Vertical(g12)
    c: Equal(g12,g10)
    c: Parallel(g11,g9)
    c: Coincident(g13,g11)
    c: Coincident(g13,g4)
    c: Coincident(g14,g13)
    c: Coincident(g14,g9)
    c: Coincident(g15,g11)
    c: Vertical(g15)
    c: Equal(g15,g10)
    c: DistanceX(g16,g4) = 80
    c: Coincident(g16,g15)
    c: Coincident(g18,g16)
    c: Coincident(g18,g17)
    c: Parallel(g17,g11)
    c: Coincident(g17,g16)
    c: Coincident(g19,g1)
    c: Vertical(g19)
    c: Equal(g19,g3)
    c: Coincident(g20,g1)
    c: Coincident(g20,g19)
    c: Horizontal(g20)
    c: Coincident(g21,g20)
    c: Coincident(g21,g1)
    c: Parallel(g0,g1)
    c: Coincident(g22,g0)
    c: Coincident(g22,g6)
    c: Parallel(g8,g6)
    c: Horizontal(g17,g4)
    c: Coincident(g24,g17)
    c: Coincident(g24,g11)
    c: Coincident(g23,g9)
    c: Coincident(g23,g8)
    c: Horizontal(g18)
FEATURE [PartDesign::Pocket] Pocket018
  BaseFeature = -> Pocket017
  Length = 1.2
  Length2 = 100
  Profile = -> Sketch036
  Type = 0
FEATURE [PartDesign::PolarPattern] PolarPattern004
  Angle = 360
  Axis = -> Z_Axis005
  BaseFeature = -> Pocket018
  Occurrences = 2
  Originals = -> [Pocket018]
FEATURE [Sketcher::SketchObject] Sketch037
  MapMode = 5
  Placement = pos=(13,13,0) rot=(0.281085,0.678598,0.678598;2.59356rad)
  Support = -> [PolarPattern004]
  sketch-geometry (1):
    g0: Circle CenterX=0 CenterY=-2 CenterZ=0 NormalX=0 NormalY=0 NormalZ=1 AngleXU=0 Radius=2
  constraints (3):
    c: Diameter(g0) = 4
    c: PointOnObject(g0,g-2)
    c: DistanceY(g-1,g0) = -2
FEATURE [PartDesign::Pocket] Pocket019
  BaseFeature = -> PolarPattern004
  Length = 5
  Length2 = 100
  Profile = -> Sketch037
  Type = 0
FEATURE [Sketcher::SketchObject] Sketch038
  MapMode = 5
  Placement = pos=(0,0,-3) rot=(0,0,1;0rad)
  Support = -> [Pocket019]
FEATURE [Sketcher::SketchObject] Sketch039
  MapMode = 5
  Support = -> [XY_Plane011]
  sketch-geometry (4):
    g0: LineSegment StartX=-35 StartY=35 StartZ=0 EndX=35 EndY=35 EndZ=0
    g1: LineSegment StartX=35 StartY=35 StartZ=0 EndX=35 EndY=-35 EndZ=0
    g2: LineSegment StartX=35 StartY=-35 StartZ=0 EndX=-35 EndY=-35 EndZ=0
    g3: LineSegment StartX=-35 StartY=-35 StartZ=0 EndX=-35 EndY=35 EndZ=0
  constraints (10):
    c: Coincident(g0,g1)
    c: Coincident(g1,g2)
    c: Coincident(g2,g3)
    c: Coincident(g3,g0)
    c: Horizontal(g2)
    c: Vertical(g3)
    c: Symmetric(g0,g0,g-2)
    c: Symmetric(g1,g0,g-1)
    c: Equal(g1,g0)
    c: DistanceY(g1,g1) = 70
FEATURE [PartDesign::Pad] Pad018
  Length = 6
  Length2 = 100
  Profile = -> Sketch039
  Type = 0
FEATURE [Sketcher::SketchObject] Sketch040
  MapMode = 5
  Placement = pos=(0,0,6) rot=(0,0,1;0rad)
  Support = -> [Pad018]
  sketch-geometry (4):
    g0: Circle CenterX=-30 CenterY=30 CenterZ=0 NormalX=0 NormalY=0 NormalZ=1 AngleXU=0 Radius=2.25
    g1: Circle CenterX=30 CenterY=30 CenterZ=0 NormalX=0 NormalY=0 NormalZ=1 AngleXU=0 Radius=2.25
    g2: Circle CenterX=30 CenterY=-30 CenterZ=0 NormalX=0 NormalY=0 NormalZ=1 AngleXU=0 Radius=2.25
    g3: Circle CenterX=-30 CenterY=-30 CenterZ=0 NormalX=0 NormalY=0 NormalZ=1 AngleXU=0 Radius=2.25
  constraints (9):
    c: Equal(g3,g0)
    c: Equal(g0,g1)
    c: Equal(g1,g2)
    c: Radius(g0) = 2.25
    c: Symmetric(g0,g3,g-1)
    c: Symmetric(g0,g1,g-2)
    c: Symmetric(g2,g1,g-1)
    c: DistanceX(g0,g1) = 60
    c: DistanceY(g2,g1) = 60
FEATURE [PartDesign::Pocket] Pocket020
  BaseFeature = -> Pad018
  Length = 7
  Length2 = 100
  Profile = -> Sketch040
  Type = 0
FEATURE [Sketcher::SketchObject] Sketch041
  ExternalGeometry = -> [Pocket020]
  MapMode = 5
  Placement = pos=(0,0,0) rot=(1,0,0;3.14159rad)
  Support = -> [Pocket020]
  sketch-geometry (8):
    g0: LineSegment StartX=-31 StartY=23 StartZ=0 EndX=-23 EndY=31 EndZ=0
    g1: LineSegment StartX=-23 StartY=31 StartZ=0 EndX=23 EndY=31 EndZ=0
    g2: LineSegment StartX=23 StartY=31 StartZ=0 EndX=31 EndY=23 EndZ=0
    g3: LineSegment StartX=31 StartY=23 StartZ=0 EndX=31 EndY=-23 EndZ=0
    g4: LineSegment StartX=31 StartY=-23 StartZ=0 EndX=23 EndY=-31 EndZ=0
    g5: LineSegment StartX=23 StartY=-31 StartZ=0 EndX=-23 EndY=-31 EndZ=0
    g6: LineSegment StartX=-23 StartY=-31 StartZ=0 EndX=-31 EndY=-23 EndZ=0
    g7: LineSegment StartX=-31 StartY=-23 StartZ=0 EndX=-31 EndY=23 EndZ=0
  constraints (21):
    c: Coincident(g1,g0)
    c: Coincident(g3,g2)
    c: Vertical(g3)
    c: Coincident(g4,g3)
    c: Coincident(g5,g4)
    c: Coincident(g6,g5)
    c: Coincident(g7,g6)
    c: Coincident(g7,g0)
    c: DistanceY(g1,g-5) = 4
    c: DistanceX(g2,g-5) = 4
    c: DistanceX(g-4,g0) = 4
    c: DistanceY(g-3,g5) = 4
    c: Angle(g-4,g4) = 0.785398
    c: Parallel(g4,g0)
    c: Angle(g6,g-4) = 0.785398
    c: Parallel(g6,g2)
    c: Coincident(g2,g1)
    c: DistanceY(g2,g-5) = 12
    c: Symmetric(g0,g1,g-2)
    c: Symmetric(g6,g0,g-1)
    c: Symmetric(g5,g4,g-2)
FEATURE [PartDesign::Pocket] Pocket021
  BaseFeature = -> Pocket020
  Length = 3
  Length2 = 100
  Profile = -> Sketch041
  Type = 0
FEATURE [Sketcher::SketchObject] Sketch042
  ExternalGeometry = -> [Pocket021]
  MapMode = 5
  Placement = pos=(0,0,6) rot=(0,0,1;0rad)
  Support = -> [Pocket021]
  sketch-geometry (21):
    g0: LineSegment [constr] StartX=-22.5 StartY=29 StartZ=0 EndX=22.5 EndY=29 EndZ=0
    g1: LineSegment [constr] StartX=22.5 StartY=29 StartZ=0 EndX=22.5 EndY=3 EndZ=0
    g2: LineSegment [constr] StartX=22.5 StartY=3 StartZ=0 EndX=-22.5 EndY=3 EndZ=0
    g3: LineSegment [constr] StartX=-22.5 StartY=3 StartZ=0 EndX=-22.5 EndY=29 EndZ=0
    g4: Circle [constr] CenterX=0 CenterY=-16.75 CenterZ=0 NormalX=0 NormalY=0 NormalZ=1 AngleXU=0 Radius=16.75
    g5: Circle CenterX=15.9735 CenterY=-5.56526 CenterZ=0 NormalX=0 NormalY=0 NormalZ=1 AngleXU=0 Radius=2
    g6: Circle CenterX=-15.9735 CenterY=-27.9347 CenterZ=0 NormalX=0 NormalY=0 NormalZ=1 AngleXU=0 Radius=2
    g7: Circle CenterX=19 CenterY=-16.75 CenterZ=0 NormalX=0 NormalY=0 NormalZ=1 AngleXU=0 Radius=1
    g8: Circle CenterX=-19 CenterY=-16.75 CenterZ=0 NormalX=0 NormalY=0 NormalZ=1 AngleXU=0 Radius=1
    g9: Circle CenterX=-25 CenterY=16 CenterZ=0 NormalX=0 NormalY=0 NormalZ=1 AngleXU=0 Radius=1
    g10: Circle CenterX=25 CenterY=16 CenterZ=0 NormalX=0 NormalY=0 NormalZ=1 AngleXU=0 Radius=1
    g11: Circle CenterX=0 CenterY=27 CenterZ=0 NormalX=0 NormalY=0 NormalZ=1 AngleXU=0 Radius=2
    g12: Circle CenterX=0 CenterY=5 CenterZ=0 NormalX=0 NormalY=0 NormalZ=1 AngleXU=0 Radius=2
    g13: LineSegment [constr] StartX=-18.4309 StartY=-29.6555 StartZ=0 EndX=18.4309 EndY=-3.84453 EndZ=0
    g14: Circle CenterX=-30 CenterY=2.5 CenterZ=0 NormalX=0 NormalY=0 NormalZ=1 AngleXU=0 Radius=0.75
    g15: Circle CenterX=-30 CenterY=-2.5 CenterZ=0 NormalX=0 NormalY=0 NormalZ=1 AngleXU=0 Radius=0.75
    g16: Circle CenterX=30 CenterY=7.5 CenterZ=0 NormalX=0 NormalY=0 NormalZ=1 AngleXU=0 Radius=0.75
    g17: Circle CenterX=30 CenterY=2.5 CenterZ=0 NormalX=0 NormalY=0 NormalZ=1 AngleXU=0 Radius=0.75
    g18: Circle CenterX=30 CenterY=-2.5 CenterZ=0 NormalX=0 NormalY=0 NormalZ=1 AngleXU=0 Radius=0.75
    g19: Circle CenterX=30 CenterY=-7.5 CenterZ=0 NormalX=0 NormalY=0 NormalZ=1 AngleXU=0 Radius=0.75
    g20: Circle CenterX=0 CenterY=-16.75 CenterZ=0 NormalX=0 NormalY=0 NormalZ=1 AngleXU=0 Radius=2
  constraints (58):
    c: Coincident(g0,g1)
    c: Coincident(g1,g2)
    c: Coincident(g2,g3)
    c: Coincident(g3,g0)
    c: Horizontal(g0)
    c: Vertical(g1)
    c: Vertical(g3)
    c: Diameter(g4) = 33.5
    c: DistanceY(g1,g1) = 26
    c: DistanceX(g0,g0) = 45
    c: PointOnObject(g4,g-2)
    c: Symmetric(g2,g1,g-2)
    c: Tangent(g-1,g4)
    c: DistanceY(g-1,g1) = 3
    c: Equal(g8,g9)
    c: Equal(g9,g10)
    c: Equal(g10,g7)
    c: Diameter(g10) = 2
    c: DistanceX(g9,g2) = 2.5
    c: DistanceX(g1,g10) = 2.5
    c: DistanceY(g1,g10) = 13
    c: DistanceY(g2,g9) = 13
    c: Equal(g5,g6)
    c: Equal(g6,g12)
    c: Equal(g12,g11)
    c: Diameter(g5) = 4
    c: Symmetric(g8,g7,g-2)
    c: Horizontal(g8,g4)
    c: Angle(g2,g13) = 0.610865
    c: Symmetric(g13,g13,g4)
    c: Distance(g13) = 45
    c: PointOnObject(g5,g13)
    c: PointOnObject(g6,g13)
    c: Distance(g13,g6) = 3
    c: Distance(g5,g13) = 3
    c: PointOnObject(g12,g-2)
    c: PointOnObject(g11,g-2)
    c: Tangent(g11,g0)
    c: Tangent(g12,g2)
    c: Distance(g8,g7) = 38
    c: Equal(g19,g18)
    c: Equal(g18,g17)
    c: Equal(g17,g16)
    c: Equal(g16,g15)
    c: Equal(g15,g14)
    c: Diameter(g14) = 1.5
    c: Symmetric(g15,g14,g-1)
    c: DistanceY(g15,g14) = 5
    c: DistanceX(g-3,g15) = 5
    c: Vertical(g19,g18)
    c: Vertical(g17,g16)
    c: DistanceY(g17,g16) = 5
    c: Symmetric(g18,g17,g-1)
    c: DistanceY(g18,g17) = 5
    c: DistanceY(g19,g18) = 5
    c: DistanceX(g19,g-4) = 5
    c: Coincident(g20,g4)
    c: Equal(g20,g5)
FEATURE [PartDesign::Pocket] Pocket022
  BaseFeature = -> Pocket021
  Length = 5
  Length2 = 100
  Profile = -> Sketch042
  Type = 0
FEATURE [PartDesign::Fillet] Fillet005
  Base = -> Pocket022 [Edge5,Edge1,Edge8,Edge2]
  BaseFeature = -> Pocket022
  Radius = 4
FEATURE [PartDesign::Body] Body011  label="FreqWeiche"
  Group = -> [Sketch039,Pad018,Sketch040,Pocket020,Sketch041,Pocket021,Sketch042,Pocket022,Fillet005]
  Origin = -> Origin011
  Placement = pos=(-50,0,207) rot=(0,0,1;0rad)
  Tip = -> Fillet005
FEATURE [Sketcher::SketchObject] Sketch043
  MapMode = 5
  Support = -> [DatumPlane005]
  sketch-geometry (9):
    g0: Circle CenterX=-20 CenterY=30 CenterZ=0 NormalX=0 NormalY=0 NormalZ=1 AngleXU=0 Radius=7.5
    g1: Circle CenterX=-20 CenterY=-30 CenterZ=0 NormalX=0 NormalY=0 NormalZ=1 AngleXU=0 Radius=6.36324
    g2: Circle CenterX=-80 CenterY=-30 CenterZ=0 NormalX=0 NormalY=0 NormalZ=1 AngleXU=0 Radius=6.81191
    g3: Circle CenterX=-80 CenterY=30 CenterZ=0 NormalX=0 NormalY=0 NormalZ=1 AngleXU=0 Radius=6.69594
    g4: LineSegment [constr] StartX=-80 StartY=30 StartZ=0 EndX=-20 EndY=30 EndZ=0
    g5: LineSegment [constr] StartX=-20 StartY=30 StartZ=0 EndX=-20 EndY=-30 EndZ=0
    g6: LineSegment [constr] StartX=-20 StartY=-30 StartZ=0 EndX=-80 EndY=-30 EndZ=0
    g7: LineSegment [constr] StartX=-80 StartY=-30 StartZ=0 EndX=-80 EndY=30 EndZ=0
    g8: LineSegment [constr] StartX=-50 StartY=30 StartZ=0 EndX=-50 EndY=-30 EndZ=0
  constraints (19):
    c: Coincident(g4,g3)
    c: Coincident(g4,g0)
    c: Horizontal(g4)
    c: Coincident(g5,g0)
    c: Coincident(g5,g1)
    c: Coincident(g6,g1)
    c: Coincident(g6,g2)
    c: Horizontal(g6)
    c: Coincident(g7,g2)
    c: Coincident(g7,g3)
    c: Vertical(g7)
    c: Equal(g7,g4)
    c: Symmetric(g1,g0,g-1)
    c: DistanceX(g4,g4) = 60
    c: Diameter(g0) = 15
    c: PointOnObject(g8,g6)
    c: Vertical(g8)
    c: Symmetric(g3,g0,g8)
    c: DistanceX(g8,g-1) = 50
FEATURE [PartDesign::Pad] Pad019
  BaseFeature = -> Pocket019
  Length = 7
  Length2 = 100
  Profile = -> Sketch043
  Reversed = true
  Type = 0
FEATURE [Sketcher::SketchObject] Sketch044
  ExternalGeometry = -> [Pad019]
  MapMode = 5
  Placement = pos=(0,0,-7) rot=(1,0,0;3.14159rad)
  Support = -> [Pad019]
  sketch-geometry (28):
    g0: LineSegment StartX=-77.8349 StartY=26.25 StartZ=0 EndX=-75.6699 EndY=30 EndZ=0
    g1: LineSegment StartX=-75.6699 StartY=30 StartZ=0 EndX=-77.8349 EndY=33.75 EndZ=0
    g2: LineSegment StartX=-77.8349 StartY=33.75 StartZ=0 EndX=-82.1651 EndY=33.75 EndZ=0
    g3: LineSegment StartX=-82.1651 StartY=33.75 StartZ=0 EndX=-84.3301 EndY=30 EndZ=0
    g4: LineSegment StartX=-84.3301 StartY=30 StartZ=0 EndX=-82.1651 EndY=26.25 EndZ=0
    g5: LineSegment StartX=-82.1651 StartY=26.25 StartZ=0 EndX=-77.8349 EndY=26.25 EndZ=0
    g6: Circle [constr] CenterX=-80 CenterY=30 CenterZ=0 NormalX=0 NormalY=0 NormalZ=1 AngleXU=0 Radius=4.33013
    g7: LineSegment StartX=-17.8349 StartY=26.25 StartZ=0 EndX=-15.6699 EndY=30 EndZ=0
    g8: LineSegment StartX=-15.6699 StartY=30 StartZ=0 EndX=-17.8349 EndY=33.75 EndZ=0
    g9: LineSegment StartX=-17.8349 StartY=33.75 StartZ=0 EndX=-22.1651 EndY=33.75 EndZ=0
    g10: LineSegment StartX=-22.1651 StartY=33.75 StartZ=0 EndX=-24.3301 EndY=30 EndZ=0
    g11: LineSegment StartX=-24.3301 StartY=30 StartZ=0 EndX=-22.1651 EndY=26.25 EndZ=0
    g12: LineSegment StartX=-22.1651 StartY=26.25 StartZ=0 EndX=-17.8349 EndY=26.25 EndZ=0
    g13: Circle [constr] CenterX=-20 CenterY=30 CenterZ=0 NormalX=0 NormalY=0 NormalZ=1 AngleXU=0 Radius=4.33013
    g14: LineSegment StartX=-17.8349 StartY=-33.75 StartZ=0 EndX=-15.6699 EndY=-30 EndZ=0
    g15: LineSegment StartX=-15.6699 StartY=-30 StartZ=0 EndX=-17.8349 EndY=-26.25 EndZ=0
    g16: LineSegment StartX=-17.8349 StartY=-26.25 StartZ=0 EndX=-22.1651 EndY=-26.25 EndZ=0
    g17: LineSegment StartX=-22.1651 StartY=-26.25 StartZ=0 EndX=-24.3301 EndY=-30 EndZ=0
    g18: LineSegment StartX=-24.3301 StartY=-30 StartZ=0 EndX=-22.1651 EndY=-33.75 EndZ=0
    g19: LineSegment StartX=-22.1651 StartY=-33.75 StartZ=0 EndX=-17.8349 EndY=-33.75 EndZ=0
    g20: Circle [constr] CenterX=-20 CenterY=-30 CenterZ=0 NormalX=0 NormalY=0 NormalZ=1 AngleXU=0 Radius=4.33013
    g21: LineSegment StartX=-77.8349 StartY=-33.75 StartZ=0 EndX=-75.6699 EndY=-30 EndZ=0
    g22: LineSegment StartX=-75.6699 StartY=-30 StartZ=0 EndX=-77.8349 EndY=-26.25 EndZ=0
    g23: LineSegment StartX=-77.8349 StartY=-26.25 StartZ=0 EndX=-82.1651 EndY=-26.25 EndZ=0
    g24: LineSegment StartX=-82.1651 StartY=-26.25 StartZ=0 EndX=-84.3301 EndY=-30 EndZ=0
    g25: LineSegment StartX=-84.3301 StartY=-30 StartZ=0 EndX=-82.1651 EndY=-33.75 EndZ=0
    g26: LineSegment StartX=-82.1651 StartY=-33.75 StartZ=0 EndX=-77.8349 EndY=-33.75 EndZ=0
    g27: Circle [constr] CenterX=-80 CenterY=-30 CenterZ=0 NormalX=0 NormalY=0 NormalZ=1 AngleXU=0 Radius=4.33013
  constraints (64):
    c: Coincident(g0,g1)
    c: Coincident(g1,g2)
    c: Coincident(g2,g3)
    c: Coincident(g3,g4)
    c: Coincident(g4,g5)
    c: Coincident(g5,g0)
    c: Equal(g0, g1-g5) x5
    c: PointOnObject(g0,g6)
    c: PointOnObject(g1,g6)
    c: PointOnObject(g2,g6)
    c: PointOnObject(g3,g6)
    c: PointOnObject(g4,g6)
    c: PointOnObject(g5,g6)
    c: Coincident(g6,g-3)
    c: Coincident(g7,g8)
    c: Coincident(g8,g9)
    c: Coincident(g9,g10)
    c: Coincident(g10,g11)
    c: Coincident(g11,g12)
    c: Coincident(g12,g7)
    c: Equal(g7, g8-g12) x5
    c: PointOnObject(g7,g13)
    c: PointOnObject(g8,g13)
    c: PointOnObject(g9,g13)
    c: PointOnObject(g10,g13)
    c: PointOnObject(g11,g13)
    c: PointOnObject(g12,g13)
    c: Coincident(g13,g-4)
    c: Coincident(g14,g15)
    c: Coincident(g15,g16)
    c: Coincident(g16,g17)
    c: Coincident(g17,g18)
    c: Coincident(g18,g19)
    c: Coincident(g19,g14)
    c: Equal(g14, g15-g19) x5
    c: PointOnObject(g14,g20)
    c: PointOnObject(g15,g20)
    c: PointOnObject(g16,g20)
    c: PointOnObject(g17,g20)
    c: PointOnObject(g18,g20)
    c: PointOnObject(g19,g20)
    c: Coincident(g20,g-5)
    c: Coincident(g21,g22)
    c: Coincident(g22,g23)
    c: Coincident(g23,g24)
    c: Coincident(g24,g25)
    c: Coincident(g25,g26)
    c: Coincident(g26,g21)
    c: Equal(g21, g22-g26) x5
    c: PointOnObject(g21,g27)
    c: PointOnObject(g22,g27)
    c: PointOnObject(g23,g27)
    c: PointOnObject(g24,g27)
    c: PointOnObject(g25,g27)
    c: PointOnObject(g26,g27)
    c: Coincident(g27,g-6)
    c: Horizontal(g19)
    c: Horizontal(g26)
    c: Horizontal(g5)
    c: Horizontal(g12)
    c: Equal(g27,g20)
    c: Equal(g20,g13)
    c: Equal(g13,g6)
    c: DistanceY(g0,g1) = 7.5
FEATURE [PartDesign::Pocket] Pocket023
  BaseFeature = -> Pad019
  Length = 4
  Length2 = 100
  Profile = -> Sketch044
  Type = 0
FEATURE [Sketcher::SketchObject] Sketch045
  ExternalGeometry = -> [Pocket023]
  MapMode = 5
  Placement = pos=(0,0,-7) rot=(1,0,0;3.14159rad)
  Support = -> [Pocket023]
  sketch-geometry (4):
    g0: Circle CenterX=-80 CenterY=30 CenterZ=0 NormalX=0 NormalY=0 NormalZ=1 AngleXU=0 Radius=2.25
    g1: Circle CenterX=-20 CenterY=30 CenterZ=0 NormalX=0 NormalY=0 NormalZ=1 AngleXU=0 Radius=2.25
    g2: Circle CenterX=-20 CenterY=-30 CenterZ=0 NormalX=0 NormalY=0 NormalZ=1 AngleXU=0 Radius=2.25
    g3: Circle CenterX=-80 CenterY=-30 CenterZ=0 NormalX=0 NormalY=0 NormalZ=1 AngleXU=0 Radius=2.25
  constraints (8):
    c: Coincident(g0,g-3)
    c: Coincident(g1,g-4)
    c: Coincident(g2,g-5)
    c: Coincident(g3,g-6)
    c: Equal(g3,g0)
    c: Equal(g0,g1)
    c: Equal(g1,g2)
    c: Diameter(g1) = 4.5
FEATURE [PartDesign::Pocket] Pocket024
  BaseFeature = -> Pocket023
  Length = 11
  Length2 = 100
  Profile = -> Sketch045
  Type = 0
FEATURE [PartDesign::Body] Body005  label="FullRangeEnclosure"
  Group = -> [Pad009,Sketch018,Pocket009,Sketch019,Pad010,Mirrored004,DatumPlane005,Sketch020,Pad011,DatumPlane006,Sketch021,Pocket010,PolarPattern002,DatumPlane007,Sketch022,Pocket011,DatumPlane008,Sketch025,Pad012,PolarPattern003,Chamfer001,Sketch029,Pocket014,Sketch030,Pad015,Chamfer002,Sketch031,Pad016,Sketch032,Pocket015,Sketch033,Pocket016,Sketch034,Pad017,Sketch035,Pocket017,DatumPlane009,Sketch036,+11 more]
  Origin = -> Origin005
  Placement = pos=(0,0,207) rot=(0,0,1;0rad)
  Tip = -> Pocket024
FEATURE [Mesh::Feature] Mesh  label="FullRangeEnclosure (Meshed)"
FEATURE [Part::Box] Box002  label="Würfel002"
  AttacherType = Attacher::AttachEngine3D
  Height = 57
  Length = 250
  Placement = pos=(-125,-125,200) rot=(0,0,1;0rad)
  Width = 250
FEATURE [Part::Feature] ND140_8
  Placement = pos=(0,-92,100) rot=(-1,0,0;1.5708rad)
  shape: bbox 138 x 62.5 x 138 mm, 52 faces (baked)
FEATURE [Part::Feature] ND140_009  label="ND140_8_2"
  Placement = pos=(0,92,100) rot=(1,0,0;1.5708rad)
  shape: bbox 138 x 62.5 x 138 mm, 52 faces (baked)
FEATURE [Sketcher::SketchObject] Sketch046
  MapMode = 5
  Placement = pos=(0,0,0) rot=(1,0,0;1.5708rad)
  Support = -> [XZ_Plane013]
  sketch-geometry (2):
    g0: Circle CenterX=0 CenterY=0 CenterZ=0 NormalX=0 NormalY=0 NormalZ=1 AngleXU=0 Radius=60
    g1: Circle CenterX=0 CenterY=0 CenterZ=0 NormalX=0 NormalY=0 NormalZ=1 AngleXU=0 Radius=80
  constraints (4):
    c: Diameter(g0) = 120
    c: Coincident(g1,g0)
    c: Diameter(g1) = 160
    c: Coincident(g0,g-1)
FEATURE [PartDesign::Pad] Pad020
  Length = 8
  Length2 = 100
  Placement = pos=(0,0,0) rot=(1,0,0;1.5708rad)
  Profile = -> Sketch046
  Type = 0
FEATURE [Sketcher::SketchObject] Sketch047
  MapMode = 5
  Placement = pos=(0,0,0) rot=(1,0,0;1.5708rad)
  Support = -> [XZ_Plane013]
  sketch-geometry (9):
    g0: Circle [constr] CenterX=0 CenterY=0 CenterZ=0 NormalX=0 NormalY=0 NormalZ=1 AngleXU=0 Radius=69
    g1: Circle CenterX=-48.7904 CenterY=48.7904 CenterZ=0 NormalX=0 NormalY=0 NormalZ=1 AngleXU=0 Radius=2.75
    g2: Circle CenterX=48.7904 CenterY=-48.7904 CenterZ=0 NormalX=0 NormalY=0 NormalZ=1 AngleXU=0 Radius=2.75
    g3: Circle CenterX=-48.7904 CenterY=-48.7904 CenterZ=0 NormalX=0 NormalY=0 NormalZ=1 AngleXU=0 Radius=2.75
    g4: Circle CenterX=48.7904 CenterY=48.7904 CenterZ=0 NormalX=0 NormalY=0 NormalZ=1 AngleXU=0 Radius=2.75
    g5: LineSegment [constr] StartX=-48.7904 StartY=48.7904 StartZ=0 EndX=48.7904 EndY=48.7904 EndZ=0
    g6: LineSegment [constr] StartX=48.7904 StartY=48.7904 StartZ=0 EndX=48.7904 EndY=-48.7904 EndZ=0
    g7: LineSegment [constr] StartX=-48.7904 StartY=-48.7904 StartZ=0 EndX=48.7904 EndY=-48.7904 EndZ=0
    g8: LineSegment [constr] StartX=-48.7904 StartY=48.7904 StartZ=0 EndX=-48.7904 EndY=-48.7904 EndZ=0
  constraints (22):
    c: Coincident(g0,g-1)
    c: PointOnObject(g1,g0)
    c: PointOnObject(g2,g0)
    c: PointOnObject(g3,g0)
    c: PointOnObject(g4,g0)
    c: Equal(g3,g1)
    c: Equal(g1,g4)
    c: Equal(g4,g2)
    c: Diameter(g4) = 5.5
    c: Coincident(g5,g1)
    c: Coincident(g5,g4)
    c: Coincident(g6,g4)
    c: Coincident(g6,g2)
    c: Vertical(g6)
    c: Coincident(g7,g3)
    c: Coincident(g7,g2)
    c: Horizontal(g7)
    c: Coincident(g8,g1)
    c: Coincident(g8,g3)
    c: Vertical(g8)
    c: Equal(g8,g5)
    c: Diameter(g0) = 138
FEATURE [PartDesign::Pocket] Pocket025
  BaseFeature = -> Pad020
  Length = 10
  Length2 = 100
  Placement = pos=(0,0,0) rot=(1,0,0;1.5708rad)
  Profile = -> Sketch047
  Reversed = true
  Type = 0
FEATURE [Sketcher::SketchObject] Sketch048
  ExternalGeometry = -> [Pocket025]
  MapMode = 5
  Placement = pos=(0,0,0) rot=(1,0,0;1.5708rad)
  Support = -> [XZ_Plane013]
  sketch-geometry (4):
    g0: Circle CenterX=-48.7904 CenterY=48.7904 CenterZ=0 NormalX=0 NormalY=0 NormalZ=1 AngleXU=0 Radius=4.5
    g1: Circle CenterX=48.7904 CenterY=48.7904 CenterZ=0 NormalX=0 NormalY=0 NormalZ=1 AngleXU=0 Radius=4.5
    g2: Circle CenterX=48.7904 CenterY=-48.7904 CenterZ=0 NormalX=0 NormalY=0 NormalZ=1 AngleXU=0 Radius=4.5
    g3: Circle CenterX=-48.7904 CenterY=-48.7904 CenterZ=0 NormalX=0 NormalY=0 NormalZ=1 AngleXU=0 Radius=4.5
  constraints (9):
    c: Coincident(g0,g-3)
    c: Coincident(g1,g-4)
    c: Coincident(g2,g-5)
    c: Coincident(g3,g-6)
    c: Diameter(g0) = 9
    c: Equal(g3,g2)
    c: Equal(g2,g1)
    c: Equal(g1,g0)
    c: Diameter(g-3) = 5.5
FEATURE [PartDesign::Pocket] Pocket026
  BaseFeature = -> Pocket025
  Length = 5
  Length2 = 100
  Placement = pos=(0,0,0) rot=(1,0,0;1.5708rad)
  Profile = -> Sketch048
  Reversed = true
  Type = 0
FEATURE [PartDesign::Chamfer] Chamfer003
  Base = -> Pocket026 [Edge2]
  BaseFeature = -> Pocket026
  Placement = pos=(0,0,0) rot=(1,0,0;1.5708rad)
  Size = 5
FEATURE [PartDesign::Chamfer] Chamfer004
  Base = -> Chamfer003 [Edge3]
  BaseFeature = -> Chamfer003
  Placement = pos=(0,0,0) rot=(1,0,0;1.5708rad)
  Size = 1
FEATURE [PartDesign::Body] Body013  label="SubBlende"
  Group = -> [Sketch046,Pad020,Sketch047,Pocket025,Sketch048,Pocket026,Chamfer003,Chamfer004]
  Origin = -> Origin013
  Placement = pos=(0,103,100) rot=(0,0,1;0rad)
  Tip = -> Chamfer004
FEATURE [PartDesign::FeatureBase] Clone005
  BaseFeature = -> Body013
  Placement = pos=(0,103,100) rot=(0,0,1;0rad)
FEATURE [PartDesign::Body] Body014  label="SubBlende2"
  BaseFeature = -> Body013
  Group = -> [Clone005]
  Origin = -> Origin014
  Placement = pos=(0,0,0) rot=(0,0,1;3.14159rad)
FEATURE [Sketcher::SketchObject] Sketch049
  MapMode = 5
  Placement = pos=(0,0,0) rot=(1,0,0;1.5708rad)
  Support = -> [XZ_Plane015]
  sketch-geometry (2):
    g0: Circle CenterX=0 CenterY=0 CenterZ=0 NormalX=0 NormalY=0 NormalZ=1 AngleXU=0 Radius=38
    g1: Circle CenterX=0 CenterY=0 CenterZ=0 NormalX=0 NormalY=0 NormalZ=1 AngleXU=0 Radius=55
  constraints (4):
    c: Coincident(g0,g-1)
    c: Diameter(g0) = 76
    c: Coincident(g1,g0)
    c: Diameter(g1) = 110
FEATURE [PartDesign::Pad] Pad021
  Length = 8
  Length2 = 100
  Placement = pos=(0,0,0) rot=(1,0,0;1.5708rad)
  Profile = -> Sketch049
  Type = 0
FEATURE [Sketcher::SketchObject] Sketch050
  MapMode = 5
  Placement = pos=(0,0,0) rot=(1,0,0;1.5708rad)
  Support = -> [XZ_Plane015]
  sketch-geometry (9):
    g0: Circle [constr] CenterX=0 CenterY=0 CenterZ=0 NormalX=0 NormalY=0 NormalZ=1 AngleXU=0 Radius=46.5
    g1: Circle CenterX=-32.8805 CenterY=32.8805 CenterZ=0 NormalX=0 NormalY=0 NormalZ=1 AngleXU=0 Radius=2.25
    g2: Circle CenterX=32.8805 CenterY=32.8805 CenterZ=0 NormalX=0 NormalY=0 NormalZ=1 AngleXU=0 Radius=2.25
    g3: Circle CenterX=32.8805 CenterY=-32.8805 CenterZ=0 NormalX=0 NormalY=0 NormalZ=1 AngleXU=0 Radius=2.25
    g4: Circle CenterX=-32.8805 CenterY=-32.8805 CenterZ=0 NormalX=0 NormalY=0 NormalZ=1 AngleXU=0 Radius=2.25
    g5: LineSegment [constr] StartX=-32.8805 StartY=-32.8805 StartZ=0 EndX=-32.8805 EndY=32.8805 EndZ=0
    g6: LineSegment [constr] StartX=32.8805 StartY=32.8805 StartZ=0 EndX=-32.8805 EndY=32.8805 EndZ=0
    g7: LineSegment [constr] StartX=32.8805 StartY=32.8805 StartZ=0 EndX=32.8805 EndY=-32.8805 EndZ=0
    g8: LineSegment [constr] StartX=32.8805 StartY=-32.8805 StartZ=0 EndX=-32.8805 EndY=-32.8805 EndZ=0
  constraints (22):
    c: Coincident(g0,g-1)
    c: Diameter(g0) = 93
    c: PointOnObject(g1,g0)
    c: PointOnObject(g2,g0)
    c: PointOnObject(g3,g0)
    c: PointOnObject(g4,g0)
    c: Coincident(g5,g4)
    c: Coincident(g5,g1)
    c: Vertical(g5)
    c: Coincident(g6,g2)
    c: Coincident(g6,g1)
    c: Coincident(g7,g2)
    c: Coincident(g7,g3)
    c: Coincident(g8,g3)
    c: Coincident(g8,g4)
    c: Horizontal(g6)
    c: Horizontal(g8)
    c: Equal(g7,g6)
    c: Equal(g4,g3)
    c: Equal(g3,g1)
    c: Equal(g1,g2)
    c: Diameter(g2) = 4.5
FEATURE [PartDesign::Pocket] Pocket027
  BaseFeature = -> Pad021
  Length = 10
  Length2 = 100
  Placement = pos=(0,0,0) rot=(1,0,0;1.5708rad)
  Profile = -> Sketch050
  Reversed = true
  Type = 0
FEATURE [Sketcher::SketchObject] Sketch051
  ExternalGeometry = -> [Pocket027]
  MapMode = 5
  Placement = pos=(0,0,0) rot=(1,0,0;1.5708rad)
  Support = -> [XZ_Plane015]
  sketch-geometry (4):
    g0: Circle CenterX=-32.8805 CenterY=32.8805 CenterZ=0 NormalX=0 NormalY=0 NormalZ=1 AngleXU=0 Radius=3.75
    g1: Circle CenterX=32.8805 CenterY=32.8805 CenterZ=0 NormalX=0 NormalY=0 NormalZ=1 AngleXU=0 Radius=3.75
    g2: Circle CenterX=-32.8805 CenterY=-32.8805 CenterZ=0 NormalX=0 NormalY=0 NormalZ=1 AngleXU=0 Radius=3.75
    g3: Circle CenterX=32.8805 CenterY=-32.8805 CenterZ=0 NormalX=0 NormalY=0 NormalZ=1 AngleXU=0 Radius=3.75
  constraints (8):
    c: Coincident(g0,g-4)
    c: Coincident(g1,g-3)
    c: Coincident(g2,g-5)
    c: Coincident(g3,g-6)
    c: Equal(g3,g1)
    c: Equal(g1,g0)
    c: Equal(g0,g2)
    c: Diameter(g1) = 7.5
FEATURE [PartDesign::Pocket] Pocket028
  BaseFeature = -> Pocket027
  Length = 4
  Length2 = 100
  Placement = pos=(0,0,0) rot=(1,0,0;1.5708rad)
  Profile = -> Sketch051
  Reversed = true
  Type = 0
FEATURE [PartDesign::Chamfer] Chamfer005
  Base = -> Pocket028 [Edge2]
  BaseFeature = -> Pocket028
  Placement = pos=(0,0,0) rot=(1,0,0;1.5708rad)
  Size = 3.5
FEATURE [Sketcher::SketchObject] Sketch052
  ExternalGeometry = -> [Chamfer005]
  MapMode = 5
  Placement = pos=(0,-8,1.8e-15) rot=(1,0,0;1.5708rad)
  Support = -> [Chamfer005]
  sketch-geometry (2):
    g0: Circle CenterX=0 CenterY=0 CenterZ=0 NormalX=0 NormalY=0 NormalZ=1 AngleXU=0 Radius=52.25
    g1: Circle CenterX=0 CenterY=0 CenterZ=0 NormalX=0 NormalY=0 NormalZ=1 AngleXU=0 Radius=55
  constraints (4):
    c: Coincident(g0,g-1)
    c: Coincident(g1,g0)
    c: Equal(g-3,g1)
    c: Diameter(g0) = 104.5
FEATURE [PartDesign::Pad] Pad022
  BaseFeature = -> Chamfer005
  Length = 1.2
  Length2 = 100
  Placement = pos=(0,0,0) rot=(1,0,0;1.5708rad)
  Profile = -> Sketch052
  Type = 0
FEATURE [PartDesign::Body] Body015  label="FullRangeBlende"
  Group = -> [Sketch049,Pad021,Sketch050,Pocket027,Sketch051,Pocket028,Chamfer005,Sketch052,Pad022]
  Origin = -> Origin015
  Placement = pos=(-50,99,253) rot=(0,0,1;0rad)
  Tip = -> Pad022
FEATURE [PartDesign::FeatureBase] Clone006
  BaseFeature = -> Body015
  Placement = pos=(-50,99,253) rot=(0,0,1;0rad)
FEATURE [PartDesign::Body] Body016  label="FullRangeBlende2"
  BaseFeature = -> Body015
  Group = -> [Clone006]
  Origin = -> Origin016
  Placement = pos=(0,0,0) rot=(0,0,1;3.14159rad)
  Tip = -> Clone006
FEATURE [Sketcher::SketchObject] Sketch053
  MapMode = 5
  Support = -> [XY_Plane017]
  sketch-geometry (7):
    g0: LineSegment StartX=0 StartY=0 StartZ=0 EndX=51.75 EndY=0 EndZ=0
    g1: LineSegment StartX=51.75 StartY=0 StartZ=0 EndX=51.75 EndY=-0.5 EndZ=0
    g2: LineSegment StartX=51.75 StartY=-0.5 StartZ=0 EndX=38.25 EndY=-0.5 EndZ=0
    g3: LineSegment StartX=38.25 StartY=-0.5 StartZ=0 EndX=22.1 EndY=-28.5 EndZ=0
    g4: LineSegment StartX=22.1 StartY=-28.5 StartZ=0 EndX=0 EndY=-28.5 EndZ=0
    g5: LineSegment StartX=0 StartY=-28.5 StartZ=0 EndX=0 EndY=0 EndZ=0
    g6: LineSegment StartX=0 StartY=0 StartZ=0 EndX=51.75 EndY=0 EndZ=0
  constraints (19):
    c: Coincident(g0,g-1)
    c: PointOnObject(g0,g-1)
    c: Coincident(g1,g0)
    c: Coincident(g2,g1)
    c: Horizontal(g2)
    c: Coincident(g3,g2)
    c: PointOnObject(g4,g-2)
    c: Horizontal(g4)
    c: Coincident(g5,g4)
    c: Coincident(g5,g0)
    c: Coincident(g6,g0)
    c: Coincident(g6,g0)
    c: Vertical(g1)
    c: DistanceX(g0,g0) = 51.75
    c: DistanceX(g4,g4) = 22.1
    c: DistanceY(g1,g1) = 0.5
    c: DistanceX(g0,g2) = 38.25
    c: DistanceY(g3,g2) = 28
    c: Coincident(g4,g3)
FEATURE [PartDesign::Revolution] Revolution002
  Angle = 360
  Axis = (0,1,0)
  Base = (0,0,0)
  Profile = -> Sketch053
  ReferenceAxis = -> Sketch053 [V_Axis]
  Reversed = true
FEATURE [Sketcher::SketchObject] Sketch054
  MapMode = 5
  Placement = pos=(0,0,0) rot=(1,0,0;1.5708rad)
  Support = -> [XZ_Plane017]
  sketch-geometry (10):
    g0: Circle [constr] CenterX=0 CenterY=0 CenterZ=0 NormalX=0 NormalY=0 NormalZ=1 AngleXU=0 Radius=46.5
    g1: LineSegment [constr] StartX=0 StartY=46.5 StartZ=0 EndX=0 EndY=-46.5 EndZ=0
    g2: LineSegment [constr] StartX=-46.5 StartY=0 StartZ=0 EndX=46.5 EndY=0 EndZ=0
    g3: Circle CenterX=-32.8805 CenterY=32.8805 CenterZ=0 NormalX=0 NormalY=0 NormalZ=1 AngleXU=0 Radius=2.25
    g4: Circle CenterX=32.8805 CenterY=32.8805 CenterZ=0 NormalX=0 NormalY=0 NormalZ=1 AngleXU=0 Radius=2.25
    g5: Circle CenterX=32.8805 CenterY=-32.8805 CenterZ=0 NormalX=0 NormalY=0 NormalZ=1 AngleXU=0 Radius=2.25
    g6: Circle CenterX=-32.8805 CenterY=-32.8805 CenterZ=0 NormalX=0 NormalY=0 NormalZ=1 AngleXU=0 Radius=2.25
    g7: LineSegment [constr] StartX=-32.8805 StartY=-32.8805 StartZ=0 EndX=32.8805 EndY=-32.8805 EndZ=0
    g8: LineSegment [constr] StartX=32.8805 StartY=-32.8805 StartZ=0 EndX=32.8805 EndY=32.8805 EndZ=0
    g9: LineSegment [constr] StartX=-32.8805 StartY=32.8805 StartZ=0 EndX=32.8805 EndY=32.8805 EndZ=0
  constraints (28):
    c: Diameter(g0) = 93
    c: Vertical(g1)
    c: Horizontal(g2)
    c: PointOnObject(g0,g2)
    c: PointOnObject(g2,g0)
    c: PointOnObject(g2,g0)
    c: PointOnObject(g1,g0)
    c: PointOnObject(g1,g0)
    c: PointOnObject(g0,g1)
    c: Coincident(g0,g-1)
    c: Equal(g6,g5)
    c: Equal(g5,g4)
    c: Equal(g4,g3)
    c: Diameter(g3) = 4.5
    c: PointOnObject(g3,g0)
    c: PointOnObject(g4,g0)
    c: PointOnObject(g5,g0)
    c: PointOnObject(g6,g0)
    c: Coincident(g7,g6)
    c: Coincident(g7,g5)
    c: Coincident(g8,g5)
    c: Coincident(g8,g4)
    c: Vertical(g8)
    c: Horizontal(g7)
    c: Equal(g7,g8)
    c: Coincident(g9,g3)
    c: Coincident(g9,g4)
    c: Horizontal(g9)
FEATURE [PartDesign::Pocket] Pocket029
  BaseFeature = -> Revolution002
  Length = 5
  Length2 = 100
  Profile = -> Sketch054
  Reversed = true
  Type = 0
FEATURE [PartDesign::Body] Body017  label="ND90-PR"
  Group = -> [Sketch053,Revolution002,Sketch054,Pocket029]
  Origin = -> Origin017
  Placement = pos=(-50,91,253) rot=(0,0,1;0rad)
  Tip = -> Pocket029
FEATURE [Sketcher::SketchObject] CopySketch008
  sketch-geometry (16):
    g0: LineSegment StartX=-115 StartY=90 StartZ=0 EndX=115 EndY=90 EndZ=0
    g1: LineSegment StartX=-115 StartY=-90 StartZ=0 EndX=115 EndY=-90 EndZ=0
    g2: LineSegment StartX=120 StartY=85 StartZ=0 EndX=120 EndY=-85 EndZ=0
    g3: LineSegment StartX=-120 StartY=85 StartZ=0 EndX=-120 EndY=-85 EndZ=0
    g4: ArcOfCircle CenterX=115 CenterY=85 CenterZ=0 NormalX=0 NormalY=0 NormalZ=1 AngleXU=0 Radius=5 StartAngle=-9e-16 EndAngle=1.5708
    g5: ArcOfCircle CenterX=115 CenterY=-85 CenterZ=0 NormalX=0 NormalY=0 NormalZ=1 AngleXU=0 Radius=5 StartAngle=4.71239 EndAngle=6.28319
    g6: ArcOfCircle CenterX=-115 CenterY=-85 CenterZ=0 NormalX=0 NormalY=0 NormalZ=1 AngleXU=0 Radius=5 StartAngle=3.14159 EndAngle=4.71239
    g7: ArcOfCircle CenterX=-115 CenterY=85 CenterZ=0 NormalX=0 NormalY=0 NormalZ=1 AngleXU=0 Radius=5 StartAngle=1.5708 EndAngle=3.14159
    g8: Circle CenterX=110 CenterY=80 CenterZ=0 NormalX=0 NormalY=0 NormalZ=1 AngleXU=0 Radius=3.25
    g9: Circle CenterX=-110 CenterY=80 CenterZ=0 NormalX=0 NormalY=0 NormalZ=1 AngleXU=0 Radius=3.25
    g10: Circle CenterX=110 CenterY=-80 CenterZ=0 NormalX=0 NormalY=0 NormalZ=1 AngleXU=0 Radius=3.25
    g11: Circle CenterX=-110 CenterY=-80 CenterZ=0 NormalX=0 NormalY=0 NormalZ=1 AngleXU=0 Radius=3.25
    g12: Circle CenterX=110 CenterY=0 CenterZ=0 NormalX=0 NormalY=0 NormalZ=1 AngleXU=0 Radius=3.25
    g13: Circle CenterX=-110 CenterY=0 CenterZ=0 NormalX=0 NormalY=0 NormalZ=1 AngleXU=0 Radius=3.25
    g14: Circle CenterX=0 CenterY=70 CenterZ=0 NormalX=0 NormalY=0 NormalZ=1 AngleXU=0 Radius=3.25
    g15: Circle CenterX=0 CenterY=-70 CenterZ=0 NormalX=0 NormalY=0 NormalZ=1 AngleXU=0 Radius=3.25
  constraints (39):
    c: Symmetric(g0,g0,g-2)
    c: Equal(g1,g0)
    c: Symmetric(g1,g1,g-2)
    c: Symmetric(g2,g2,g-1)
    c: Symmetric(g3,g3,g-1)
    c: Equal(g3,g2)
    c: Symmetric(g0,g1,g-1)
    c: Symmetric(g2,g3,g-2)
    c: Coincident(g4,g2)
    c: Tangent(g7,g0) = 1.5708
    c: Tangent(g7,g3) = -1.5708
    c: Tangent(g0,g4) = 1.5708
    c: Coincident(g5,g1)
    c: Tangent(g5,g2) = 1.5708
    c: Coincident(g3,g6)
    c: Tangent(g6,g1) = -1.5708
    c: Distance(g3,g2) = 240
    c: Radius(g4) = 5
    c: Distance(g0,g1) = 180
    c: Diameter(g8) = 6.5
    c: DistanceY(g8,g0) = 10
    c: DistanceX(g8,g2) = 10
    c: Equal(g9,g8)
    c: Symmetric(g9,g8,g-2)
    c: Equal(g11,g10)
    c: Equal(g10,g8)
    c: Symmetric(g10,g8,g-1)
    c: Symmetric(g11,g10,g-2)
    c: PointOnObject(g12,g-1)
    c: PointOnObject(g13,g-1)
    c: Equal(g13,g12)
    c: Equal(g12,g8)
    c: Vertical(g12,g8)
    c: Vertical(g13,g9)
    c: Equal(g15,g14)
    c: Equal(g14,g8)
    c: PointOnObject(g15,g-2)
    c: Symmetric(g15,g14,g-1)
    c: DistanceY(g14,g0) = 20
FEATURE [PartDesign::Pad] Pad023
  Length = 14
  Length2 = 100
  Profile = -> CopySketch008
  Reversed = true
  Type = 0
FEATURE [Sketcher::SketchObject] Sketch055
  ExternalGeometry = -> [Pad023]
  MapMode = 5
  Support = -> [Pad023]
  sketch-geometry (24):
    g0: LineSegment StartX=7 StartY=83 StartZ=0 EndX=96 EndY=83 EndZ=0
    g1: LineSegment StartX=96 StartY=83 StartZ=0 EndX=113 EndY=66 EndZ=0
    g2: LineSegment StartX=113 StartY=66 StartZ=0 EndX=113 EndY=7 EndZ=0
    g3: LineSegment StartX=113 StartY=7 StartZ=0 EndX=104 EndY=7 EndZ=0
    g4: LineSegment StartX=104 StartY=7 StartZ=0 EndX=104 EndY=-7 EndZ=0
    g5: LineSegment StartX=104 StartY=-7 StartZ=0 EndX=113 EndY=-7 EndZ=0
    g6: LineSegment StartX=113 StartY=-7 StartZ=0 EndX=113 EndY=-66 EndZ=0
    g7: LineSegment StartX=113 StartY=-66 StartZ=0 EndX=96 EndY=-83 EndZ=0
    g8: LineSegment StartX=96 StartY=-83 StartZ=0 EndX=7 EndY=-83 EndZ=0
    g9: LineSegment StartX=7 StartY=-83 StartZ=0 EndX=7 EndY=-63 EndZ=0
    g10: LineSegment StartX=7 StartY=-63 StartZ=0 EndX=-7 EndY=-63 EndZ=0
    g11: LineSegment StartX=-7 StartY=-63 StartZ=0 EndX=-7 EndY=-83 EndZ=0
    g12: LineSegment StartX=-7 StartY=-83 StartZ=0 EndX=-96 EndY=-83 EndZ=0
    g13: LineSegment StartX=-96 StartY=-83 StartZ=0 EndX=-113 EndY=-66 EndZ=0
    g14: LineSegment StartX=-113 StartY=-66 StartZ=0 EndX=-113 EndY=-7 EndZ=0
    g15: LineSegment StartX=-113 StartY=-7 StartZ=0 EndX=-104 EndY=-7 EndZ=0
    g16: LineSegment StartX=-104 StartY=-7 StartZ=0 EndX=-104 EndY=7 EndZ=0
    g17: LineSegment StartX=-104 StartY=7 StartZ=0 EndX=-113 EndY=7 EndZ=0
    g18: LineSegment StartX=-113 StartY=7 StartZ=0 EndX=-113 EndY=66 EndZ=0
    g19: LineSegment StartX=-113 StartY=66 StartZ=0 EndX=-96 EndY=83 EndZ=0
    g20: LineSegment StartX=-96 StartY=83 StartZ=0 EndX=-7 EndY=83 EndZ=0
    g21: LineSegment StartX=-7 StartY=83 StartZ=0 EndX=-7 EndY=63 EndZ=0
    g22: LineSegment StartX=-7 StartY=63 StartZ=0 EndX=7 EndY=63 EndZ=0
    g23: LineSegment StartX=7 StartY=63 StartZ=0 EndX=7 EndY=83 EndZ=0
  constraints (62):
    c: Horizontal(g0)
    c: Coincident(g1,g0)
    c: Coincident(g2,g1)
    c: Vertical(g2)
    c: Coincident(g3,g2)
    c: Horizontal(g3)
    c: Coincident(g4,g3)
    c: Coincident(g5,g4)
    c: Coincident(g6,g5)
    c: Vertical(g6)
    c: Coincident(g7,g6)
    c: Coincident(g8,g7)
    c: Horizontal(g8)
    c: Coincident(g9,g8)
    c: Coincident(g10,g9)
    c: Coincident(g11,g10)
    c: Vertical(g11)
    c: Coincident(g12,g11)
    c: Horizontal(g12)
    c: Coincident(g13,g12)
    c: Coincident(g14,g13)
    c: Vertical(g14)
    c: Coincident(g15,g14)
    c: Horizontal(g15)
    c: Coincident(g16,g15)
    c: Vertical(g16)
    c: Coincident(g17,g16)
    c: Coincident(g18,g17)
    c: Coincident(g19,g18)
    c: Coincident(g20,g19)
    c: Coincident(g21,g20)
    c: Vertical(g21)
    c: Coincident(g22,g21)
    c: Horizontal(g22)
    c: Coincident(g23,g22)
    c: Coincident(g23,g0)
    c: Angle(g-3,g1) = 2.35619
    c: DistanceY(g0,g-3) = 7
    c: DistanceX(g1,g-4) = 7
    c: Symmetric(g20,g0,g-2)
    c: Vertical(g23)
    c: DistanceX(g-1,g0) = 7
    c: DistanceY(g23,g23) = 20
    c: Symmetric(g19,g0,g-2)
    c: Symmetric(g18,g1,g-2)
    c: DistanceX(g0,g0) = 89
    c: Equal(g4,g10)
    c: Equal(g10,g16)
    c: Equal(g16,g22)
    c: Horizontal(g5)
    c: Horizontal(g17)
    c: Symmetric(g14,g17,g-1)
    c: Symmetric(g4,g3,g-1)
    c: DistanceX(g3,g-4) = 16
    c: Symmetric(g6,g1,g-1)
    c: Vertical(g9)
    c: Symmetric(g9,g10,g-2)
    c: Equal(g9,g23)
    c: Symmetric(g13,g6,g-2)
    c: Symmetric(g12,g7,g-2)
    c: Symmetric(g7,g0,g-1)
    c: Equal(g17,g3)
FEATURE [PartDesign::Pocket] Pocket030
  BaseFeature = -> Pad023
  Length = 10
  Length2 = 100
  Profile = -> Sketch055
  Type = 0
FEATURE [Sketcher::SketchObject] Sketch056
  ExternalGeometry = -> [Pocket030]
  MapMode = 5
  Placement = pos=(0,0,-10) rot=(0,0,1;0rad)
  Support = -> [Pocket030]
  sketch-geometry (100):
    g0: LineSegment StartX=-113 StartY=56 StartZ=0 EndX=-86 EndY=83 EndZ=0
    g1: LineSegment StartX=-83 StartY=83 StartZ=0 EndX=-113 EndY=53 EndZ=0
    g2: LineSegment StartX=-73 StartY=83 StartZ=0 EndX=-113 EndY=43 EndZ=0
    g3: LineSegment StartX=-113 StartY=40 StartZ=0 EndX=-70 EndY=83 EndZ=0
    g4: LineSegment StartX=-60 StartY=83 StartZ=0 EndX=-113 EndY=30 EndZ=0
    g5: LineSegment [constr] StartX=-96 StartY=83 StartZ=0 EndX=-86 EndY=83 EndZ=0
    g6: LineSegment StartX=-86 StartY=83 StartZ=0 EndX=-83 EndY=83 EndZ=0
    g7: LineSegment [constr] StartX=-83 StartY=83 StartZ=0 EndX=-73 EndY=83 EndZ=0
    g8: LineSegment StartX=-73 StartY=83 StartZ=0 EndX=-70 EndY=83 EndZ=0
    g9: LineSegment StartX=-113 StartY=56 StartZ=0 EndX=-113 EndY=53 EndZ=0
    g10: LineSegment StartX=-113 StartY=40 StartZ=0 EndX=-113 EndY=43 EndZ=0
    g11: LineSegment [constr] StartX=-60 StartY=83 StartZ=0 EndX=-70 EndY=83 EndZ=0
    g12: LineSegment StartX=-113 StartY=27 StartZ=0 EndX=-57 EndY=83 EndZ=0
    g13: LineSegment StartX=-60 StartY=83 StartZ=0 EndX=-57 EndY=83 EndZ=0
    g14: LineSegment StartX=-113 StartY=27 StartZ=0 EndX=-113 EndY=30 EndZ=0
    g15: LineSegment StartX=-113 StartY=17 StartZ=0 EndX=-47 EndY=83 EndZ=0
    g16: LineSegment StartX=-44 StartY=83 StartZ=0 EndX=-113 EndY=14 EndZ=0
    g17: LineSegment StartX=-113 StartY=14 StartZ=0 EndX=-113 EndY=17 EndZ=0
    g18: LineSegment StartX=-44 StartY=83 StartZ=0 EndX=-47 EndY=83 EndZ=0
    g19: LineSegment [constr] StartX=-57 StartY=83 StartZ=0 EndX=-47 EndY=83 EndZ=0
    g20: LineSegment StartX=-34 StartY=83 StartZ=0 EndX=-110 EndY=7 EndZ=0
    g21: LineSegment StartX=-31 StartY=83 StartZ=0 EndX=-107 EndY=7 EndZ=0
    g22: LineSegment StartX=-31 StartY=83 StartZ=0 EndX=-34 EndY=83 EndZ=0
    g23: LineSegment [constr] StartX=-44 StartY=83 StartZ=0 EndX=-34 EndY=83 EndZ=0
    g24: LineSegment StartX=-110 StartY=7 StartZ=0 EndX=-107 EndY=7 EndZ=0
    g25: LineSegment StartX=-21 StartY=83 StartZ=0 EndX=-104 EndY=4.832e-13 EndZ=0
    g26: LineSegment StartX=-18 StartY=83 StartZ=0 EndX=-104 EndY=-3 EndZ=0
    g27: LineSegment StartX=-21 StartY=83 StartZ=0 EndX=-18 EndY=83 EndZ=0
    g28: LineSegment [constr] StartX=-21 StartY=83 StartZ=0 EndX=-31 EndY=83 EndZ=0
    g29: LineSegment StartX=-8 StartY=83 StartZ=0 EndX=-113 EndY=-22 EndZ=0
    g30: LineSegment StartX=-7 StartY=81 StartZ=0 EndX=-113 EndY=-25 EndZ=0
    g31: LineSegment [constr] StartX=-18 StartY=83 StartZ=0 EndX=-8 EndY=83 EndZ=0
    g32: LineSegment StartX=-104 StartY=-3 StartZ=0 EndX=-104 EndY=4.832e-13 EndZ=0
    g33: LineSegment StartX=-113 StartY=-25 StartZ=0 EndX=-113 EndY=-22 EndZ=0
    g34: LineSegment [constr] StartX=-113 StartY=17 StartZ=0 EndX=-113 EndY=27 EndZ=0
    g35: LineSegment StartX=-113 StartY=-35 StartZ=0 EndX=-7 EndY=71 EndZ=0
    g36: LineSegment StartX=-7 StartY=68 StartZ=0 EndX=-113 EndY=-38 EndZ=0
    g37: LineSegment StartX=-113 StartY=-38 StartZ=0 EndX=-113 EndY=-35 EndZ=0
    g38: LineSegment [constr] StartX=-113 StartY=-25 StartZ=0 EndX=-113 EndY=-35 EndZ=0
    g39: LineSegment StartX=-7 StartY=71 StartZ=0 EndX=-7 EndY=68 EndZ=0
    g40: LineSegment StartX=-113 StartY=-48 StartZ=0 EndX=-2 EndY=63 EndZ=0
    g41: LineSegment StartX=-113 StartY=-51 StartZ=0 EndX=0 EndY=62 EndZ=0
    g42: LineSegment StartX=-113 StartY=-61 StartZ=0 EndX=0 EndY=52 EndZ=0
    g43: LineSegment StartX=-113 StartY=-64 StartZ=0 EndX=0 EndY=49 EndZ=0
    g44: LineSegment StartX=-109 StartY=-70 StartZ=0 EndX=0 EndY=39 EndZ=0
    g45: LineSegment StartX=-107.5 StartY=-71.5 StartZ=0 EndX=0 EndY=36 EndZ=0
    g46: LineSegment StartX=-102.5 StartY=-76.5 StartZ=0 EndX=0 EndY=26 EndZ=0
    g47: LineSegment StartX=-101 StartY=-78 StartZ=0 EndX=0 EndY=23 EndZ=0
    g48: LineSegment StartX=-96 StartY=-83 StartZ=0 EndX=0 EndY=13 EndZ=0
    g49: LineSegment StartX=-113 StartY=-51 StartZ=0 EndX=-113 EndY=-48 EndZ=0
    g50: LineSegment [constr] StartX=-113 StartY=-48 StartZ=0 EndX=-113 EndY=-38 EndZ=0
    g51: LineSegment [constr] StartX=-113 StartY=-61 StartZ=0 EndX=-113 EndY=-51 EndZ=0
    g52: LineSegment StartX=-113 StartY=-64 StartZ=0 EndX=-113 EndY=-61 EndZ=0
    g53: LineSegment StartX=-2 StartY=63 StartZ=0 EndX=0 EndY=63 EndZ=0
    g54: LineSegment StartX=0 StartY=63 StartZ=0 EndX=0 EndY=62 EndZ=0
    g55: LineSegment [constr] StartX=0 StartY=52 StartZ=0 EndX=0 EndY=62 EndZ=0
    g56: LineSegment [constr] StartX=0 StartY=39 StartZ=0 EndX=0 EndY=49 EndZ=0
    g57: LineSegment StartX=0 StartY=49 StartZ=0 EndX=0 EndY=52 EndZ=0
    g58: LineSegment StartX=0 StartY=36 StartZ=0 EndX=0 EndY=39 EndZ=0
    g59: LineSegment StartX=0 StartY=23 StartZ=0 EndX=0 EndY=26 EndZ=0
    g60: LineSegment StartX=-107.5 StartY=-71.5 StartZ=0 EndX=-109 EndY=-70 EndZ=0
    g61: LineSegment StartX=-101 StartY=-78 StartZ=0 EndX=-102.5 EndY=-76.5 EndZ=0
    g62: LineSegment [constr] StartX=0 StartY=26 StartZ=0 EndX=0 EndY=36 EndZ=0
    g63: LineSegment [constr] StartX=0 StartY=13 StartZ=0 EndX=0 EndY=23 EndZ=0
    g64: LineSegment StartX=-93 StartY=-83 StartZ=0 EndX=0 EndY=10 EndZ=0
    g65: LineSegment StartX=-83 StartY=-83 StartZ=0 EndX=0 EndY=2.7e-13 EndZ=0
    g66: LineSegment StartX=-80 StartY=-83 StartZ=0 EndX=0 EndY=-3 EndZ=0
    g67: LineSegment StartX=-70 StartY=-83 StartZ=0 EndX=0 EndY=-13 EndZ=0
    g68: LineSegment StartX=-67 StartY=-83 StartZ=0 EndX=0 EndY=-16 EndZ=0
    g69: LineSegment StartX=-57 StartY=-83 StartZ=0 EndX=0 EndY=-26 EndZ=0
    g70: LineSegment [constr] StartX=0 StartY=2.7e-13 StartZ=0 EndX=0 EndY=10 EndZ=0
    g71: LineSegment [constr] StartX=0 StartY=-13 StartZ=0 EndX=0 EndY=-3 EndZ=0
    g72: LineSegment [constr] StartX=0 StartY=-16 StartZ=0 EndX=0 EndY=-26 EndZ=0
    g73: LineSegment StartX=0 StartY=-16 StartZ=0 EndX=0 EndY=-13 EndZ=0
    g74: LineSegment StartX=0 StartY=-3 StartZ=0 EndX=0 EndY=2.7e-13 EndZ=0
    g75: LineSegment StartX=0 StartY=10 StartZ=0 EndX=0 EndY=13 EndZ=0
    g76: LineSegment StartX=-67 StartY=-83 StartZ=0 EndX=-70 EndY=-83 EndZ=0
    g77: LineSegment StartX=-80 StartY=-83 StartZ=0 EndX=-83 EndY=-83 EndZ=0
    g78: LineSegment StartX=-93 StartY=-83 StartZ=0 EndX=-96 EndY=-83 EndZ=0
    g79: LineSegment StartX=-54 StartY=-83 StartZ=0 EndX=0 EndY=-29 EndZ=0
    g80: LineSegment StartX=0 StartY=-39 StartZ=0 EndX=-44 EndY=-83 EndZ=0
    g81: LineSegment StartX=-41 StartY=-83 StartZ=0 EndX=0 EndY=-42 EndZ=0
    g82: LineSegment StartX=-31 StartY=-83 StartZ=0 EndX=0 EndY=-52 EndZ=0
    g83: LineSegment StartX=-28 StartY=-83 StartZ=0 EndX=-3.6e-15 EndY=-55 EndZ=0
    g84: LineSegment StartX=0 StartY=-42 StartZ=0 EndX=0 EndY=-39 EndZ=0
    g85: LineSegment StartX=-3.6e-15 StartY=-55 StartZ=0 EndX=0 EndY=-52 EndZ=0
    g86: LineSegment StartX=0 StartY=-29 StartZ=0 EndX=0 EndY=-26 EndZ=0
    g87: LineSegment [constr] StartX=0 StartY=-52 StartZ=0 EndX=0 EndY=-42 EndZ=0
    g88: LineSegment [constr] StartX=0 StartY=-39 StartZ=0 EndX=0 EndY=-29 EndZ=0
    g89: LineSegment StartX=-57 StartY=-83 StartZ=0 EndX=-54 EndY=-83 EndZ=0
    g90: LineSegment StartX=-44 StartY=-83 StartZ=0 EndX=-41 EndY=-83 EndZ=0
    g91: LineSegment StartX=-31 StartY=-83 StartZ=0 EndX=-28 EndY=-83 EndZ=0
    g92: LineSegment StartX=-18 StartY=-83 StartZ=0 EndX=-7 EndY=-72 EndZ=0
    g93: LineSegment StartX=-15 StartY=-83 StartZ=0 EndX=-7 EndY=-75 EndZ=0
    g94: LineSegment StartX=-7 StartY=-75 StartZ=0 EndX=-7 EndY=-72 EndZ=0
    g95: LineSegment StartX=-15 StartY=-83 StartZ=0 EndX=-18 EndY=-83 EndZ=0
    g96: LineSegment [constr] StartX=-41 StartY=-83 StartZ=0 EndX=-31 EndY=-83 EndZ=0
    g97: LineSegment [constr] StartX=-28 StartY=-83 StartZ=0 EndX=-18 EndY=-83 EndZ=0
    g98: LineSegment StartX=-8 StartY=83 StartZ=0 EndX=-7 EndY=83 EndZ=0
    g99: LineSegment StartX=-7 StartY=81 StartZ=0 EndX=-7 EndY=83 EndZ=0
  constraints (277):
    c: PointOnObject(g0,g-4)
    c: PointOnObject(g0,g-3)
    c: PointOnObject(g1,g-3)
    c: PointOnObject(g1,g-4)
    c: PointOnObject(g2,g-3)
    c: PointOnObject(g2,g-4)
    c: PointOnObject(g3,g-4)
    c: PointOnObject(g3,g-3)
    c: PointOnObject(g4,g-3)
    c: Parallel(g0,g1)
    c: Parallel(g1,g2)
    c: Parallel(g2,g3)
    c: Parallel(g3,g4)
    c: Coincident(g5,g-9)
    c: Coincident(g5,g0)
    c: DistanceX(g5,g5) = 10
    c: Coincident(g6,g0)
    c: Coincident(g6,g1)
    c: DistanceX(g6,g6) = 3
    c: Coincident(g7,g1)
    c: Coincident(g7,g2)
    c: Coincident(g8,g2)
    c: Coincident(g8,g3)
    c: Equal(g7,g5)
    c: Equal(g6,g8)
    c: Parallel(g0,g-9)
    c: PointOnObject(g4,g-4)
    c: Coincident(g9,g0)
    c: Coincident(g9,g1)
    c: Coincident(g10,g3)
    c: Coincident(g10,g2)
    c: Coincident(g11,g4)
    c: Coincident(g11,g3)
    c: Equal(g11,g7)
    c: PointOnObject(g12,g-4)
    c: PointOnObject(g12,g-3)
    c: Coincident(g13,g4)
    c: Coincident(g13,g12)
    c: Coincident(g14,g12)
    c: Coincident(g14,g4)
    c: Equal(g13,g8)
    c: Parallel(g4,g12)
    c: PointOnObject(g15,g-4)
    c: PointOnObject(g15,g-3)
    c: PointOnObject(g16,g-3)
    c: PointOnObject(g16,g-4)
    c: Coincident(g17,g16)
    c: Coincident(g17,g15)
    c: Coincident(g18,g16)
    c: Coincident(g18,g15)
    c: Equal(g18,g13)
    c: Parallel(g15,g16)
    c: Coincident(g19,g12)
    c: Coincident(g19,g15)
    c: Equal(g19,g11)
    c: Parallel(g15,g12)
    c: PointOnObject(g20,g-3)
    c: PointOnObject(g21,g-3)
    c: Coincident(g22,g21)
    c: Coincident(g22,g20)
    c: Equal(g22,g18)
    c: Parallel(g20,g21)
    c: Parallel(g21,g16)
    c: Coincident(g23,g16)
    c: Coincident(g23,g20)
    c: Equal(g23,g19)
    c: PointOnObject(g20,g-5)
    c: PointOnObject(g21,g-5)
    c: Coincident(g24,g20)
    c: Coincident(g24,g21)
    c: PointOnObject(g25,g-3)
    c: PointOnObject(g26,g-3)
    c: Coincident(g27,g25)
    c: Coincident(g27,g26)
    c: Coincident(g28,g25)
    c: Coincident(g28,g21)
    c: PointOnObject(g29,g-3)
    c: Equal(g28,g23)
    c: Equal(g27,g22)
    c: Parallel(g25,g26)
    c: Parallel(g26,g29)
    c: Parallel(g29,g30)
    c: Parallel(g30,g21)
    c: PointOnObject(g25,g-6)
    c: PointOnObject(g26,g-6)
    c: Coincident(g31,g26)
    c: Coincident(g31,g29)
    c: Equal(g31,g28)
    c: PointOnObject(g30,g-10)
    c: PointOnObject(g29,g-8)
    c: PointOnObject(g30,g-8)
    c: Coincident(g32,g26)
    c: Coincident(g32,g25)
    c: Coincident(g33,g30)
    c: Coincident(g33,g29)
    c: Equal(g33,g32)
    c: Coincident(g34,g15)
    c: Coincident(g34,g12)
    c: PointOnObject(g35,g-10)
    c: PointOnObject(g36,g-8)
    c: Parallel(g36,g35)
    c: Parallel(g35,g30)
    c: Coincident(g37,g36)
    c: Coincident(g37,g35)
    c: Vertical(g37)
    c: Equal(g37,g33)
    c: Coincident(g38,g30)
    c: Coincident(g38,g35)
    c: Equal(g38,g34)
    c: PointOnObject(g36,g-10)
    c: Coincident(g39,g35)
    c: Coincident(g39,g36)
    c: PointOnObject(g40,g-8)
    c: PointOnObject(g40,g-11)
    c: PointOnObject(g41,g-8)
    c: PointOnObject(g42,g-8)
    c: Parallel(g41,g40)
    c: Parallel(g40,g36)
    c: Coincident(g49,g40)
    c: Equal(g49,g37)
    c: Coincident(g50,g40)
    c: Coincident(g50,g36)
    c: Equal(g50,g38)
    c: Coincident(g41,g49)
    c: Coincident(g51,g42)
    c: Coincident(g51,g41)
    c: Equal(g51,g50)
    c: Parallel(g43,g42)
    c: Parallel(g42,g41)
    c: PointOnObject(g43,g-8)
    c: Coincident(g52,g43)
    c: Coincident(g52,g42)
    c: Equal(g52,g49)
    c: Parallel(g44,g45)
    c: Parallel(g45,g46)
    c: Parallel(g46,g47)
    c: Parallel(g47,g48)
    c: Parallel(g48,g43)
    c: PointOnObject(g44,g-12)
    c: PointOnObject(g45,g-12)
    c: PointOnObject(g41,g-2)
    c: Coincident(g53,g40)
    c: Horizontal(g53)
    c: Coincident(g54,g53)
    c: Coincident(g54,g41)
    c: PointOnObject(g53,g-2)
    c: PointOnObject(g42,g-2)
    c: PointOnObject(g43,g-2)
    c: PointOnObject(g44,g-2)
    c: PointOnObject(g45,g-2)
    c: Coincident(g55,g42)
    c: Coincident(g55,g41)
    c: Coincident(g56,g44)
    c: Coincident(g56,g43)
    c: Equal(g55,g56)
    c: Coincident(g57,g43)
    c: Coincident(g57,g42)
    c: Coincident(g45,g58)
    c: Coincident(g58,g44)
    c: Equal(g58,g57)
    c: PointOnObject(g46,g-2)
    c: PointOnObject(g47,g-2)
    c: Coincident(g59,g47)
    c: Coincident(g59,g46)
    c: Equal(g59,g58)
    c: PointOnObject(g46,g-12)
    c: PointOnObject(g47,g-12)
    c: Coincident(g60,g45)
    c: Coincident(g60,g44)
    c: Coincident(g61,g47)
    c: Coincident(g61,g46)
    c: PointOnObject(g48,g-2)
    c: Coincident(g62,g46)
    c: Coincident(g62,g45)
    c: Coincident(g63,g48)
    c: Coincident(g63,g47)
    c: Equal(g63,g62)
    c: Equal(g62,g56)
    c: PointOnObject(g48,g-12)
    c: PointOnObject(g64,g-13)
    c: PointOnObject(g64,g-2)
    c: PointOnObject(g65,g-13)
    c: PointOnObject(g65,g-2)
    c: PointOnObject(g66,g-13)
    c: PointOnObject(g66,g-2)
    c: PointOnObject(g67,g-13)
    c: PointOnObject(g68,g-13)
    c: PointOnObject(g68,g-2)
    c: PointOnObject(g69,g-2)
    c: Parallel(g48,g64)
    c: Parallel(g64,g65)
    c: Parallel(g65,g66)
    c: Parallel(g66,g67)
    c: Parallel(g67,g68)
    c: Parallel(g68,g69)
    c: Coincident(g70,g65)
    c: Coincident(g70,g64)
    c: Coincident(g71,g67)
    c: Coincident(g71,g66)
    c: Vertical(g71)
    c: Coincident(g72,g68)
    c: Coincident(g72,g69)
    c: Coincident(g73,g68)
    c: Coincident(g73,g67)
    c: Coincident(g74,g66)
    c: Coincident(g74,g65)
    c: Coincident(g75,g64)
    c: Coincident(g75,g48)
    c: Equal(g73,g74)
    c: Equal(g74,g75)
    c: Equal(g75,g59)
    c: Equal(g72,g71)
    c: Equal(g71,g70)
    c: Equal(g70,g63)
    c: PointOnObject(g69,g-13)
    c: Coincident(g76,g68)
    c: Coincident(g76,g67)
    c: Coincident(g77,g66)
    c: Coincident(g77,g65)
    c: Coincident(g78,g64)
    c: Coincident(g78,g48)
    c: PointOnObject(g79,g-13)
    c: PointOnObject(g79,g-2)
    c: PointOnObject(g80,g-2)
    c: PointOnObject(g80,g-13)
    c: PointOnObject(g81,g-2)
    c: PointOnObject(g82,g-13)
    c: PointOnObject(g82,g-2)
    c: PointOnObject(g83,g-13)
    c: PointOnObject(g83,g-2)
    c: Coincident(g84,g81)
    c: Coincident(g84,g80)
    c: Coincident(g85,g83)
    c: Coincident(g85,g82)
    c: Coincident(g86,g79)
    c: Coincident(g86,g69)
    c: Equal(g85,g84)
    c: Equal(g84,g86)
    c: Equal(g86,g73)
    c: Coincident(g87,g82)
    c: Coincident(g87,g81)
    c: Coincident(g88,g80)
    c: Coincident(g88,g79)
    c: Equal(g87,g88)
    c: Equal(g88,g72)
    c: Parallel(g80,g81)
    c: Parallel(g81,g82)
    c: Parallel(g82,g83)
    c: Parallel(g83,g66)
    c: PointOnObject(g81,g-13)
    c: Parallel(g79,g69)
    c: Coincident(g89,g69)
    c: Coincident(g89,g79)
    c: Coincident(g90,g80)
    c: Coincident(g90,g81)
    c: Coincident(g91,g82)
    c: Coincident(g91,g83)
    c: PointOnObject(g92,g-13)
    c: PointOnObject(g93,g-13)
    c: PointOnObject(g93,g-14)
    c: Coincident(g94,g92)
    c: Vertical(g94)
    c: Coincident(g95,g93)
    c: Coincident(g95,g92)
    c: Parallel(g92,g93)
    c: Parallel(g93,g83)
    c: Coincident(g93,g94)
    c: Equal(g95,g91)
    c: Coincident(g96,g81)
    c: Coincident(g96,g82)
    c: Coincident(g97,g83)
    c: Coincident(g97,g92)
    c: Equal(g97,g96)
    c: Coincident(g98,g29)
    c: Coincident(g98,g-10)
    c: Coincident(g99,g30)
    c: Coincident(g99,g98)
FEATURE [PartDesign::Pad] Pad024
  BaseFeature = -> Pocket030
  Length = 7
  Length2 = 100
  Profile = -> Sketch056
  Type = 0
FEATURE [PartDesign::Mirrored] Mirrored005
  BaseFeature = -> Pad024
  MirrorPlane = -> Sketch056 [V_Axis]
  Originals = -> [Pad024]
FEATURE [PartDesign::Plane] DatumPlane010
  AttachmentOffset = pos=(0,0,-14) rot=(0,0,1;0rad)
  Length = 281.569
  MapMode = 5
  Placement = pos=(0,0,-14) rot=(0,0,1;0rad)
  ResizeMode = 0
  Support = -> [XY_Plane018]
  Width = 221.569
FEATURE [Sketcher::SketchObject] Sketch057
  MapMode = 5
  Placement = pos=(0,0,-14) rot=(0,0,1;0rad)
  Support = -> [DatumPlane010]
  sketch-geometry (12):
    g0: Circle CenterX=-95 CenterY=55 CenterZ=0 NormalX=0 NormalY=0 NormalZ=1 AngleXU=0 Radius=6
    g1: Circle CenterX=0 CenterY=55 CenterZ=0 NormalX=0 NormalY=0 NormalZ=1 AngleXU=0 Radius=6
    g2: Circle CenterX=95 CenterY=55 CenterZ=0 NormalX=0 NormalY=0 NormalZ=1 AngleXU=0 Radius=6
    g3: Circle CenterX=95 CenterY=-40 CenterZ=0 NormalX=0 NormalY=0 NormalZ=1 AngleXU=0 Radius=6
    g4: Circle CenterX=0 CenterY=-40 CenterZ=0 NormalX=0 NormalY=0 NormalZ=1 AngleXU=0 Radius=6
    g5: Circle CenterX=-95 CenterY=-40 CenterZ=0 NormalX=0 NormalY=0 NormalZ=1 AngleXU=0 Radius=6
    g6: LineSegment [constr] StartX=0 StartY=55 StartZ=0 EndX=95 EndY=55 EndZ=0
    g7: LineSegment [constr] StartX=0 StartY=55 StartZ=0 EndX=-95 EndY=55 EndZ=0
    g8: LineSegment [constr] StartX=-95 StartY=55 StartZ=0 EndX=-95 EndY=-40 EndZ=0
    g9: LineSegment [constr] StartX=-95 StartY=-40 StartZ=0 EndX=0 EndY=-40 EndZ=0
    g10: LineSegment [constr] StartX=0 StartY=-40 StartZ=0 EndX=95 EndY=-40 EndZ=0
    g11: LineSegment [constr] StartX=95 StartY=-40 StartZ=0 EndX=95 EndY=55 EndZ=0
  constraints (30):
    c: PointOnObject(g1,g-2)
    c: Equal(g5,g0)
    c: Equal(g0,g1)
    c: Equal(g1,g2)
    c: Equal(g2,g3)
    c: Equal(g3,g4)
    c: Horizontal(g0,g1)
    c: Horizontal(g5,g4)
    c: Diameter(g0) = 12
    c: DistanceX(g0,g1) = 95
    c: Coincident(g6,g1)
    c: Coincident(g6,g2)
    c: Horizontal(g6)
    c: Coincident(g7,g1)
    c: Coincident(g7,g0)
    c: Coincident(g8,g0)
    c: Coincident(g8,g5)
    c: Vertical(g8)
    c: Coincident(g9,g5)
    c: Coincident(g9,g4)
    c: Coincident(g10,g4)
    c: Coincident(g10,g3)
    c: Coincident(g11,g3)
    c: Coincident(g11,g2)
    c: Equal(g9,g7)
    c: Equal(g7,g6)
    c: Equal(g6,g10)
    c: Equal(g10,g11)
    c: Equal(g11,g8)
    c: DistanceY(g-1,g0) = 55
FEATURE [PartDesign::Pad] Pad025
  BaseFeature = -> Mirrored005
  Length = 11
  Length2 = 100
  Profile = -> Sketch057
  Type = 0
FEATURE [Sketcher::SketchObject] Sketch058
  MapMode = 5
  Placement = pos=(0,0,-14) rot=(1,0,0;3.14159rad)
  Support = -> [Pad025]
  sketch-geometry (12):
    g0: Circle CenterX=-95 CenterY=40 CenterZ=0 NormalX=0 NormalY=0 NormalZ=1 AngleXU=0 Radius=2
    g1: Circle CenterX=0 CenterY=40 CenterZ=0 NormalX=0 NormalY=0 NormalZ=1 AngleXU=0 Radius=2
    g2: Circle CenterX=95 CenterY=40 CenterZ=0 NormalX=0 NormalY=0 NormalZ=1 AngleXU=0 Radius=2
    g3: Circle CenterX=95 CenterY=-55 CenterZ=0 NormalX=0 NormalY=0 NormalZ=1 AngleXU=0 Radius=2
    g4: Circle CenterX=0 CenterY=-55 CenterZ=0 NormalX=0 NormalY=0 NormalZ=1 AngleXU=0 Radius=2
    g5: Circle CenterX=-95 CenterY=-55 CenterZ=0 NormalX=0 NormalY=0 NormalZ=1 AngleXU=0 Radius=2
    g6: LineSegment [constr] StartX=-95 StartY=-55 StartZ=0 EndX=0 EndY=-55 EndZ=0
    g7: LineSegment [constr] StartX=0 StartY=-55 StartZ=0 EndX=95 EndY=-55 EndZ=0
    g8: LineSegment [constr] StartX=95 StartY=-55 StartZ=0 EndX=95 EndY=40 EndZ=0
    g9: LineSegment [constr] StartX=95 StartY=40 StartZ=0 EndX=0 EndY=40 EndZ=0
    g10: LineSegment [constr] StartX=0 StartY=40 StartZ=0 EndX=-95 EndY=40 EndZ=0
    g11: LineSegment [constr] StartX=-95 StartY=40 StartZ=0 EndX=-95 EndY=-55 EndZ=0
  constraints (31):
    c: PointOnObject(g1,g-2)
    c: PointOnObject(g4,g-2)
    c: Horizontal(g5,g4)
    c: Horizontal(g4,g3)
    c: Equal(g5,g0)
    c: Equal(g0,g1)
    c: Equal(g1,g2)
    c: Equal(g2,g3)
    c: Equal(g3,g4)
    c: Diameter(g0) = 4
    c: Horizontal(g0,g1)
    c: Horizontal(g1,g2)
    c: Coincident(g6,g5)
    c: Coincident(g6,g4)
    c: Coincident(g7,g4)
    c: Coincident(g7,g3)
    c: Coincident(g8,g3)
    c: Coincident(g8,g2)
    c: Coincident(g9,g2)
    c: Coincident(g9,g1)
    c: Coincident(g10,g1)
    c: Coincident(g10,g0)
    c: Coincident(g11,g5)
    c: Vertical(g11)
    c: Equal(g7,g6)
    c: Equal(g6,g11)
    c: Equal(g11,g10)
    c: Equal(g10,g9)
    c: Equal(g9,g8)
    c: DistanceX(g10,g10) = 95
    c: DistanceY(g3,g-1) = 55
FEATURE [PartDesign::Pocket] Pocket031
  BaseFeature = -> Pad025
  Length = 11
  Length2 = 100
  Profile = -> Sketch058
  Type = 0
FEATURE [Sketcher::SketchObject] Sketch059
  MapMode = 5
  Placement = pos=(0,0,-14) rot=(0,0,1;0rad)
  Support = -> [DatumPlane010]
  sketch-geometry (12):
    g0: ArcOfCircle CenterX=-80 CenterY=-65 CenterZ=0 NormalX=0 NormalY=0 NormalZ=1 AngleXU=0 Radius=12.5 StartAngle=1.5708 EndAngle=4.71239
    g1: ArcOfCircle CenterX=-30 CenterY=-65 CenterZ=0 NormalX=0 NormalY=0 NormalZ=1 AngleXU=0 Radius=12.5 StartAngle=4.71239 EndAngle=7.85398
    g2: ArcOfCircle CenterX=30 CenterY=-65 CenterZ=0 NormalX=0 NormalY=0 NormalZ=1 AngleXU=0 Radius=12.5 StartAngle=1.5708 EndAngle=4.71239
    g3: ArcOfCircle CenterX=80 CenterY=-65 CenterZ=0 NormalX=0 NormalY=0 NormalZ=1 AngleXU=0 Radius=12.5 StartAngle=4.71239 EndAngle=7.85398
    g4: LineSegment StartX=-80 StartY=-52.5 StartZ=0 EndX=-30 EndY=-52.5 EndZ=0
    g5: LineSegment StartX=-80 StartY=-77.5 StartZ=0 EndX=-30 EndY=-77.5 EndZ=0
    g6: LineSegment StartX=30 StartY=-77.5 StartZ=0 EndX=80 EndY=-77.5 EndZ=0
    g7: LineSegment StartX=80 StartY=-52.5 StartZ=0 EndX=30 EndY=-52.5 EndZ=0
    g8: Circle CenterX=-97.5 CenterY=-65 CenterZ=0 NormalX=0 NormalY=0 NormalZ=1 AngleXU=0 Radius=5
    g9: Circle CenterX=-12.5 CenterY=-65 CenterZ=0 NormalX=0 NormalY=0 NormalZ=1 AngleXU=0 Radius=5
    g10: Circle CenterX=12.5 CenterY=-65 CenterZ=0 NormalX=0 NormalY=0 NormalZ=1 AngleXU=0 Radius=5
    g11: Circle CenterX=97.5 CenterY=-65 CenterZ=0 NormalX=0 NormalY=0 NormalZ=1 AngleXU=0 Radius=5
  constraints (34):
    c: Horizontal(g1,g0)
    c: Horizontal(g0,g2)
    c: Horizontal(g2,g3)
    c: Equal(g0,g1)
    c: Equal(g1,g2)
    c: Equal(g2,g3)
    c: Horizontal(g4)
    c: Equal(g4,g7)
    c: Equal(g7,g6)
    c: Diameter(g0) = 25
    c: DistanceX(g0,g1) = 50
    c: Tangent(g7,g2) = -1.5708
    c: Tangent(g5,g1) = -1.5708
    c: Tangent(g4,g0) = 1.5708
    c: Coincident(g1,g4)
    c: Tangent(g7,g3) = -1.5708
    c: Tangent(g5,g0) = -1.5708
    c: Tangent(g3,g6) = -1.5708
    c: Coincident(g6,g2)
    c: DistanceX(g-1,g2) = 30
    c: DistanceX(g1,g-1) = 30
    c: DistanceY(g2,g-1) = 65
    c: Equal(g11,g10)
    c: Equal(g10,g9)
    c: Equal(g9,g8)
    c: Diameter(g8) = 10
    c: Horizontal(g8,g9)
    c: Horizontal(g9,g10)
    c: Horizontal(g10,g11)
    c: Tangent(g11,g3)
    c: Horizontal(g11,g3)
    c: Tangent(g10,g2)
    c: Tangent(g9,g1)
    c: Tangent(g8,g0)
FEATURE [PartDesign::Pad] Pad026
  BaseFeature = -> Pocket031
  Length = 11
  Length2 = 100
  Profile = -> Sketch059
  Type = 0
FEATURE [Sketcher::SketchObject] Sketch060
  ExternalGeometry = -> [Pad026]
  MapMode = 5
  Placement = pos=(0,0,-14) rot=(1,0,0;3.14159rad)
  Support = -> [Pad026]
  sketch-geometry (6):
    g0: ArcOfCircle CenterX=-80 CenterY=65 CenterZ=0 NormalX=0 NormalY=0 NormalZ=1 AngleXU=0 Radius=11.3 StartAngle=1.57079 EndAngle=4.71239
    g1: ArcOfCircle CenterX=-30 CenterY=65 CenterZ=0 NormalX=0 NormalY=0 NormalZ=1 AngleXU=0 Radius=11.3 StartAngle=4.71239 EndAngle=7.85398
    g2: LineSegment StartX=-80 StartY=76.3 StartZ=0 EndX=-30 EndY=76.3 EndZ=0
    g3: LineSegment StartX=-30 StartY=53.7 StartZ=0 EndX=-80 EndY=53.7 EndZ=0
    g4: Circle CenterX=-97.5 CenterY=65 CenterZ=0 NormalX=0 NormalY=0 NormalZ=1 AngleXU=0 Radius=1.75
    g5: Circle CenterX=-12.5 CenterY=65 CenterZ=0 NormalX=0 NormalY=0 NormalZ=1 AngleXU=0 Radius=1.75
  constraints (14):
    c: Coincident(g0,g-4)
    c: Coincident(g1,g-7)
    c: Coincident(g2,g0)
    c: Horizontal(g3)
    c: Coincident(g4,g-5)
    c: Coincident(g5,g-8)
    c: Equal(g5,g4)
    c: Diameter(g4) = 3.5
    c: Diameter(g1) = 22.6
    c: Tangent(g2,g1) = 1.5708
    c: Tangent(g3,g1) = 1.5708
    c: Coincident(g0,g3)
    c: Horizontal(g2)
    c: Equal(g0,g1)
FEATURE [PartDesign::Pocket] Pocket032
  BaseFeature = -> Pad026
  Length = 11
  Length2 = 100
  Profile = -> Sketch060
  Type = 0
FEATURE [PartDesign::Mirrored] Mirrored006
  BaseFeature = -> Pocket032
  MirrorPlane = -> YZ_Plane018
  Originals = -> [Pocket032]
FEATURE [Part::Feature] _M1_Series007
  Placement = pos=(1.6e-14,-4.4,2.7e-14) rot=(0,1,0;3.14159rad)
  shape: bbox 12.7 x 8.302 x 6.602 mm, 74 faces (baked)
FEATURE [Part::Feature] _M1_Series008
  Placement = pos=(0,0,0) rot=(0,1,0;3.14159rad)
  shape: bbox 12.71 x 10.78 x 10.11 mm, 103 faces (baked)
FEATURE [Part::Feature] _M1_Series009
  Placement = pos=(1.5e-14,4.75,2.4e-14) rot=(0,1,0;3.14159rad)
  shape: bbox 6.458 x 10 x 6.458 mm, 50 faces (baked)
FEATURE [Part::Feature] _M1_Series010
  Placement = pos=(-0.738059,2.04083,-1e-15) rot=(0.108867,0.994056,0;3.14159rad)
  shape: bbox 6.354 x 17.07 x 3.475 mm, 8 faces (baked)
FEATURE [Part::Feature] _M1_Series011
  Placement = pos=(-4.7,-5.87,1.8e-14) rot=(0,1,0;1.5708rad)
  shape: bbox 0.75 x 9.34 x 4 mm, 22 faces (baked)
FEATURE [Part::Feature] _M1_Series012
  Placement = pos=(9e-15,-5.37,2e-15) rot=(0,1,0;1.5708rad)
  shape: bbox 0.75 x 10.84 x 4 mm, 28 faces (baked)
FEATURE [Part::Feature] _M1_Series013
  Placement = pos=(4.7,-5.87,9e-15) rot=(0,1,0;1.5708rad)
  shape: bbox 0.75 x 9.34 x 4 mm, 22 faces (baked)
FEATURE [Part::MultiFuse] Fusion002  label="ToggleSwitchBtAux"
  Placement = pos=(-60,-72,302) rot=(0.57735,-0.57735,-0.57735;2.0944rad)
  Shapes = -> [_M1_Series007,_M1_Series008,_M1_Series010,_M1_Series013,_M1_Series012,_M1_Series011,_M1_Series009]
FEATURE [Part::Feature] pdb181_e420
  Placement = pos=(-80,-65,303) rot=(0.707107,0,0.707107;3.14159rad)
  shape: bbox 17.97 x 22.48 x 29.2 mm, 304 faces (baked)
FEATURE [Part::Feature] pdb181_e421
  Placement = pos=(80,-65,303) rot=(0.707107,0,0.707107;3.14159rad)
  shape: bbox 17.97 x 22.48 x 29.2 mm, 304 faces (baked)
FEATURE [Part::Feature] pdb181_e422
  Placement = pos=(55,-65,303) rot=(0.707107,0,0.707107;3.14159rad)
  shape: bbox 17.97 x 22.48 x 29.2 mm, 304 faces (baked)
FEATURE [Part::Feature] pdb181_e423
  Placement = pos=(30,-65,303) rot=(0.707107,0,0.707107;3.14159rad)
  shape: bbox 17.97 x 22.48 x 29.2 mm, 304 faces (baked)
FEATURE [Part::Feature] OLED
  Placement = pos=(-37,-65,300) rot=(0,0,1;0rad)
  shape: bbox 27.5 x 27.5 x 11.7 mm, 37 faces (baked)
FEATURE [App::DocumentObjectGroup] Gruppe001  label="UI"
  Group = -> [Fusion001,Fusion002,pdb181_e420,pdb181_e421,pdb181_e422,pdb181_e423,OLED]
FEATURE [PartDesign::Plane] DatumPlane011
  AttachmentOffset = pos=(0,0,300) rot=(0,0,1;0rad)
  Length = 237.648
  MapMode = 5
  Placement = pos=(0,0,300) rot=(0,0,1;0rad)
  ResizeMode = 0
  Support = -> [XY_Plane019]
  Width = 118.648
FEATURE [Sketcher::SketchObject] Sketch061
  MapMode = 5
  Placement = pos=(0,0,300) rot=(0,0,1;0rad)
  Support = -> [DatumPlane011]
  sketch-geometry (10):
    g0: LineSegment StartX=-105 StartY=-49 StartZ=0 EndX=105 EndY=-49 EndZ=0
    g1: LineSegment StartX=105 StartY=-49 StartZ=0 EndX=105 EndY=-64 EndZ=0
    g2: LineSegment StartX=105 StartY=-64 StartZ=0 EndX=88 EndY=-81 EndZ=0
    g3: LineSegment StartX=88 StartY=-81 StartZ=0 EndX=8.5 EndY=-81 EndZ=0
    g4: LineSegment StartX=8.5 StartY=-81 StartZ=0 EndX=8.5 EndY=-61 EndZ=0
    g5: LineSegment StartX=8.5 StartY=-61 StartZ=0 EndX=-8.5 EndY=-61 EndZ=0
    g6: LineSegment StartX=-8.5 StartY=-61 StartZ=0 EndX=-8.5 EndY=-81 EndZ=0
    g7: LineSegment StartX=-8.5 StartY=-81 StartZ=0 EndX=-88 EndY=-81 EndZ=0
    g8: LineSegment StartX=-88 StartY=-81 StartZ=0 EndX=-105 EndY=-64 EndZ=0
    g9: LineSegment StartX=-105 StartY=-64 StartZ=0 EndX=-105 EndY=-49 EndZ=0
  constraints (26):
    c: Coincident(g1,g0)
    c: Vertical(g1)
    c: Coincident(g2,g1)
    c: Coincident(g3,g2)
    c: Horizontal(g3)
    c: Coincident(g4,g3)
    c: Coincident(g5,g4)
    c: Coincident(g6,g5)
    c: Horizontal(g7)
    c: Coincident(g9,g8)
    c: Coincident(g9,g0)
    c: Vertical(g4)
    c: Vertical(g6)
    c: Symmetric(g4,g5,g-2)
    c: Coincident(g6,g7)
    c: DistanceY(g4,g-1) = 61
    c: DistanceY(g3,g-1) = 81
    c: DistanceX(g5,g5) = 17
    c: Angle(g2,g3) = 2.35619
    c: Coincident(g8,g7)
    c: Symmetric(g7,g2,g-2)
    c: Symmetric(g8,g1,g-2)
    c: Symmetric(g0,g0,g-2)
    c: DistanceY(g4,g0) = 12
    c: DistanceY(g1,g1) = 15
    c: DistanceX(g-1,g0) = 105
FEATURE [PartDesign::Pad] Pad027
  Length = 4
  Length2 = 100
  Placement = pos=(0,0,300) rot=(0,0,1;0rad)
  Profile = -> Sketch061
  Type = 0
FEATURE [Sketcher::SketchObject] Sketch062
  MapMode = 5
  Placement = pos=(0,0,300) rot=(1,0,0;3.14159rad)
  Support = -> [Pad027]
  sketch-geometry (19):
    g0: Circle CenterX=-60 CenterY=72 CenterZ=0 NormalX=0 NormalY=0 NormalZ=1 AngleXU=0 Radius=3.5
    g1: Circle CenterX=-60 CenterY=58 CenterZ=0 NormalX=0 NormalY=0 NormalZ=1 AngleXU=0 Radius=3.5
    g2: Circle CenterX=-80 CenterY=65 CenterZ=0 NormalX=0 NormalY=0 NormalZ=1 AngleXU=0 Radius=3.5
    g3: Circle CenterX=-25 CenterY=53.25 CenterZ=0 NormalX=0 NormalY=0 NormalZ=1 AngleXU=0 Radius=1.25
    g4: Circle CenterX=-48.5 CenterY=53.25 CenterZ=0 NormalX=0 NormalY=0 NormalZ=1 AngleXU=0 Radius=1.25
    g5: Circle CenterX=-48.5 CenterY=76.75 CenterZ=0 NormalX=0 NormalY=0 NormalZ=1 AngleXU=0 Radius=1.25
    g6: Circle CenterX=-25 CenterY=76.75 CenterZ=0 NormalX=0 NormalY=0 NormalZ=1 AngleXU=0 Radius=1.25
    g7: Circle CenterX=30 CenterY=65 CenterZ=0 NormalX=0 NormalY=0 NormalZ=1 AngleXU=0 Radius=3.5
    g8: Circle CenterX=55 CenterY=65 CenterZ=0 NormalX=0 NormalY=0 NormalZ=1 AngleXU=0 Radius=3.5
    g9: Circle CenterX=80 CenterY=65 CenterZ=0 NormalX=0 NormalY=0 NormalZ=1 AngleXU=0 Radius=3.5
    g10: Circle CenterX=97.5 CenterY=65 CenterZ=0 NormalX=0 NormalY=0 NormalZ=1 AngleXU=0 Radius=2
    g11: Circle CenterX=12.5 CenterY=65 CenterZ=0 NormalX=0 NormalY=0 NormalZ=1 AngleXU=0 Radius=2
    g12: Circle CenterX=-12.5 CenterY=65 CenterZ=0 NormalX=0 NormalY=0 NormalZ=1 AngleXU=0 Radius=2
    g13: Circle CenterX=-97.5 CenterY=65 CenterZ=0 NormalX=0 NormalY=0 NormalZ=1 AngleXU=0 Radius=2
    g14: LineSegment [constr] StartX=-97.5 StartY=65 StartZ=0 EndX=97.5 EndY=65 EndZ=0
    g15: LineSegment [constr] StartX=-25 StartY=53.25 StartZ=0 EndX=-48.5 EndY=53.25 EndZ=0
    g16: LineSegment [constr] StartX=-48.5 StartY=53.25 StartZ=0 EndX=-48.5 EndY=76.75 EndZ=0
    g17: LineSegment [constr] StartX=-48.5 StartY=76.75 StartZ=0 EndX=-25 EndY=76.75 EndZ=0
    g18: LineSegment [constr] StartX=-25 StartY=76.75 StartZ=0 EndX=-25 EndY=53.25 EndZ=0
  constraints (47):
    c: Equal(g13,g12)
    c: Equal(g12,g11)
    c: Equal(g11,g10)
    c: Diameter(g10) = 4
    c: Coincident(g14,g10)
    c: PointOnObject(g11,g14)
    c: Symmetric(g11,g12,g-2)
    c: Symmetric(g10,g13,g-2)
    c: DistanceY(g-1,g11) = 65
    c: DistanceX(g-1,g11) = 12.5
    c: DistanceX(g-1,g10) = 97.5
    c: PointOnObject(g9,g14)
    c: PointOnObject(g8,g14)
    c: PointOnObject(g7,g14)
    c: DistanceX(g-1,g7) = 30
    c: DistanceX(g-1,g8) = 55
    c: DistanceX(g-1,g9) = 80
    c: Equal(g9,g8)
    c: Equal(g8,g7)
    c: Diameter(g7) = 7
    c: Equal(g2,g7)
    c: Symmetric(g2,g9,g-2)
    c: Equal(g1,g0)
    c: Diameter(g1) = 7
    c: Equal(g3,g4)
    c: Equal(g4,g5)
    c: Equal(g5,g6)
    c: Diameter(g4) = 2.5
    c: Coincident(g15,g16)
    c: Coincident(g16,g17)
    c: Coincident(g17,g18)
    c: Coincident(g18,g15)
    c: Horizontal(g15)
    c: Horizontal(g17)
    c: Vertical(g18)
    c: Coincident(g15,g3)
    c: Coincident(g16,g5)
    c: Coincident(g6,g17)
    c: Coincident(g4,g15)
    c: Equal(g16,g15)
    c: DistanceY(g16,g16) = 23.5
    c: Symmetric(g5,g4,g14)
    c: DistanceX(g3,g-1) = 25
    c: Coincident(g14,g13)
    c: Symmetric(g1,g0,g14)
    c: DistanceY(g1,g0) = 14
    c: DistanceX(g1,g-1) = 60
FEATURE [PartDesign::Pocket] Pocket033
  BaseFeature = -> Pad027
  Length = 5
  Length2 = 100
  Placement = pos=(0,0,300) rot=(0,0,1;0rad)
  Profile = -> Sketch062
  Type = 1
FEATURE [Sketcher::SketchObject] Sketch063
  ExternalGeometry = -> [Pocket033]
  MapMode = 5
  Placement = pos=(0,0,300) rot=(1,0,0;3.14159rad)
  Support = -> [Pocket033]
  sketch-geometry (12):
    g0: Circle CenterX=38.5 CenterY=65 CenterZ=0 NormalX=0 NormalY=0 NormalZ=1 AngleXU=0 Radius=1.75
    g1: Circle CenterX=63.5 CenterY=65 CenterZ=0 NormalX=0 NormalY=0 NormalZ=1 AngleXU=0 Radius=1.75
    g2: Circle CenterX=88.5 CenterY=65 CenterZ=0 NormalX=0 NormalY=0 NormalZ=1 AngleXU=0 Radius=1.75
    g3: Circle CenterX=-71.5 CenterY=65 CenterZ=0 NormalX=0 NormalY=0 NormalZ=1 AngleXU=0 Radius=1.75
    g4: Circle CenterX=-66 CenterY=72 CenterZ=0 NormalX=0 NormalY=0 NormalZ=1 AngleXU=0 Radius=1.75
    g5: Circle CenterX=-66 CenterY=58 CenterZ=0 NormalX=0 NormalY=0 NormalZ=1 AngleXU=0 Radius=1.75
    g6: Circle [constr] CenterX=-80 CenterY=65 CenterZ=0 NormalX=0 NormalY=0 NormalZ=1 AngleXU=0 Radius=8.5
    g7: Circle [constr] CenterX=-60 CenterY=58 CenterZ=0 NormalX=0 NormalY=0 NormalZ=1 AngleXU=0 Radius=6
    g8: Circle [constr] CenterX=-60 CenterY=72 CenterZ=0 NormalX=0 NormalY=0 NormalZ=1 AngleXU=0 Radius=6
    g9: Circle [constr] CenterX=30 CenterY=65 CenterZ=0 NormalX=0 NormalY=0 NormalZ=1 AngleXU=0 Radius=8.5
    g10: Circle [constr] CenterX=55 CenterY=65 CenterZ=0 NormalX=0 NormalY=0 NormalZ=1 AngleXU=0 Radius=8.5
    g11: Circle [constr] CenterX=80 CenterY=65 CenterZ=0 NormalX=0 NormalY=0 NormalZ=1 AngleXU=0 Radius=8.5
  constraints (30):
    c: Coincident(g6,g-3)
    c: Coincident(g7,g-4)
    c: Coincident(g9,g-5)
    c: Coincident(g10,g-6)
    c: Coincident(g11,g-7)
    c: Equal(g6,g9)
    c: Equal(g9,g10)
    c: Equal(g10,g11)
    c: Diameter(g6) = 17
    c: Equal(g3,g5)
    c: Equal(g5,g4)
    c: Equal(g4,g0)
    c: Equal(g0,g1)
    c: Equal(g1,g2)
    c: Horizontal(g0,g9)
    c: PointOnObject(g0,g9)
    c: Horizontal(g10,g1)
    c: PointOnObject(g1,g10)
    c: Horizontal(g2,g11)
    c: PointOnObject(g2,g11)
    c: Diameter(g0) = 3.5
    c: Horizontal(g3,g6)
    c: PointOnObject(g3,g6)
    c: PointOnObject(g5,g7)
    c: Diameter(g7) = 12
    c: Diameter(g8) = 12
    c: PointOnObject(g4,g8)
    c: Coincident(g-8,g8)
    c: Horizontal(g5,g7)
    c: Horizontal(g4,g8)
FEATURE [PartDesign::Pocket] Pocket034
  BaseFeature = -> Pocket033
  Length = 2.5
  Length2 = 100
  Placement = pos=(0,0,300) rot=(0,0,1;0rad)
  Profile = -> Sketch063
  Type = 0
FEATURE [Sketcher::SketchObject] Sketch064
  ExternalGeometry = -> [Mirrored006]
  MapMode = 5
  Placement = pos=(0,0,-14) rot=(0,0,1;0rad)
  Support = -> [DatumPlane010]
  sketch-geometry (4):
    g0: LineSegment StartX=55 StartY=83 StartZ=0 EndX=77.5 EndY=83 EndZ=0
    g1: LineSegment StartX=77.5 StartY=83 StartZ=0 EndX=77.5 EndY=73 EndZ=0
    g2: LineSegment StartX=77.5 StartY=73 StartZ=0 EndX=55 EndY=73 EndZ=0
    g3: LineSegment StartX=55 StartY=73 StartZ=0 EndX=55 EndY=83 EndZ=0
  constraints (12):
    c: Coincident(g0,g1)
    c: Coincident(g1,g2)
    c: Coincident(g2,g3)
    c: Coincident(g3,g0)
    c: Horizontal(g0)
    c: Horizontal(g2)
    c: Vertical(g1)
    c: Vertical(g3)
    c: DistanceY(g0,g-3) = 7
    c: DistanceY(g1,g1) = 10
    c: DistanceX(g2,g2) = 22.5
    c: DistanceX(g-3,g0) = 170
FEATURE [PartDesign::Pad] Pad028
  BaseFeature = -> Mirrored006
  Length = 14
  Length2 = 100
  Profile = -> Sketch064
  Type = 0
FEATURE [Sketcher::SketchObject] Sketch065
  ExternalGeometry = -> [Pad028]
  MapMode = 5
  Placement = pos=(0,0,-14) rot=(1,0,0;3.14159rad)
  Support = -> [Pad028]
  sketch-geometry (4):
    g0: LineSegment StartX=58 StartY=-76 StartZ=0 EndX=74.5 EndY=-76 EndZ=0
    g1: LineSegment StartX=74.5 StartY=-76 StartZ=0 EndX=74.5 EndY=-83 EndZ=0
    g2: LineSegment StartX=74.5 StartY=-83 StartZ=0 EndX=58 EndY=-83 EndZ=0
    g3: LineSegment StartX=58 StartY=-83 StartZ=0 EndX=58 EndY=-76 EndZ=0
  constraints (12):
    c: Coincident(g0,g1)
    c: Coincident(g1,g2)
    c: Coincident(g2,g3)
    c: Coincident(g3,g0)
    c: Horizontal(g0)
    c: Horizontal(g2)
    c: Vertical(g1)
    c: Vertical(g3)
    c: PointOnObject(g1,g-3)
    c: DistanceX(g0,g0) = 16.5
    c: DistanceY(g3,g3) = 7
    c: DistanceX(g-4,g0) = 3
FEATURE [PartDesign::Pocket] Pocket035
  BaseFeature = -> Pad028
  Length = 5
  Length2 = 100
  Profile = -> Sketch065
  Type = 1
FEATURE [PartDesign::Body] Body018  label="Top"
  Group = -> [Pad023,Sketch055,Pocket030,Sketch056,Pad024,Mirrored005,DatumPlane010,Sketch057,Pad025,Sketch058,Pocket031,Sketch059,Pad026,Sketch060,Pocket032,Mirrored006,Sketch064,Pad028,Sketch065,Pocket035]
  Origin = -> Origin018
  Placement = pos=(0,2e-15,321) rot=(0,0,1;0rad)
  Tip = -> Pocket035
FEATURE [Sketcher::SketchObject] CopySketch009  label="SketchGround"
  MapMode = 2
  Support = -> [XY_Plane020]
  sketch-geometry (25):
    g0: LineSegment [constr] StartX=-115 StartY=90 StartZ=0 EndX=115 EndY=90 EndZ=0
    g1: LineSegment [constr] StartX=-115 StartY=-90 StartZ=0 EndX=115 EndY=-90 EndZ=0
    g2: LineSegment [constr] StartX=120 StartY=85 StartZ=0 EndX=120 EndY=-85 EndZ=0
    g3: LineSegment [constr] StartX=-120 StartY=85 StartZ=0 EndX=-120 EndY=-85 EndZ=0
    g4: ArcOfCircle [constr] CenterX=115 CenterY=85 CenterZ=0 NormalX=0 NormalY=0 NormalZ=1 AngleXU=0 Radius=5 StartAngle=1e-15 EndAngle=1.5708
    g5: ArcOfCircle [constr] CenterX=115 CenterY=-85 CenterZ=0 NormalX=0 NormalY=0 NormalZ=1 AngleXU=0 Radius=5 StartAngle=4.71239 EndAngle=6.28319
    g6: ArcOfCircle [constr] CenterX=-115 CenterY=-85 CenterZ=0 NormalX=0 NormalY=0 NormalZ=1 AngleXU=0 Radius=5 StartAngle=3.14159 EndAngle=4.71239
    g7: ArcOfCircle [constr] CenterX=-115 CenterY=85 CenterZ=0 NormalX=0 NormalY=0 NormalZ=1 AngleXU=0 Radius=5 StartAngle=1.5708 EndAngle=3.14159
    g8: Circle [constr] CenterX=110 CenterY=80 CenterZ=0 NormalX=0 NormalY=0 NormalZ=1 AngleXU=0 Radius=3.25
    g9: Circle [constr] CenterX=-110 CenterY=80 CenterZ=0 NormalX=0 NormalY=0 NormalZ=1 AngleXU=0 Radius=3.25
    g10: Circle [constr] CenterX=110 CenterY=-80 CenterZ=0 NormalX=0 NormalY=0 NormalZ=1 AngleXU=0 Radius=3.25
    g11: Circle [constr] CenterX=-110 CenterY=-80 CenterZ=0 NormalX=0 NormalY=0 NormalZ=1 AngleXU=0 Radius=3.25
    g12: Circle [constr] CenterX=110 CenterY=0 CenterZ=0 NormalX=0 NormalY=0 NormalZ=1 AngleXU=0 Radius=3.25
    g13: Circle [constr] CenterX=-110 CenterY=0 CenterZ=0 NormalX=0 NormalY=0 NormalZ=1 AngleXU=0 Radius=3.25
    g14: Circle [constr] CenterX=0 CenterY=70 CenterZ=0 NormalX=0 NormalY=0 NormalZ=1 AngleXU=0 Radius=3.25
    g15: Circle [constr] CenterX=0 CenterY=-70 CenterZ=0 NormalX=0 NormalY=0 NormalZ=1 AngleXU=0 Radius=3.25
    g16: ArcOfCircle CenterX=115 CenterY=85 CenterZ=0 NormalX=0 NormalY=0 NormalZ=1 AngleXU=0 Radius=5.5 StartAngle=0 EndAngle=1.5708
    g17: LineSegment StartX=115 StartY=90.5 StartZ=0 EndX=105 EndY=90.5 EndZ=0
    g18: LineSegment StartX=105 StartY=95.5 StartZ=0 EndX=115 EndY=95.5 EndZ=0
    g19: ArcOfCircle CenterX=115 CenterY=85 CenterZ=0 NormalX=0 NormalY=0 NormalZ=1 AngleXU=0 Radius=10.5 StartAngle=0 EndAngle=1.5708
    g20: LineSegment StartX=120.5 StartY=85 StartZ=0 EndX=120.5 EndY=0 EndZ=0
    g21: LineSegment StartX=120.5 StartY=0 StartZ=0 EndX=125.5 EndY=0 EndZ=0
    g22: LineSegment StartX=125.5 StartY=0 StartZ=0 EndX=125.5 EndY=85 EndZ=0
    g23: ArcOfCircle CenterX=105 CenterY=85 CenterZ=0 NormalX=0 NormalY=0 NormalZ=1 AngleXU=0 Radius=10.5 StartAngle=1.5708 EndAngle=2.59028
    g24: LineSegment StartX=96.0557 StartY=90.5 StartZ=0 EndX=105 EndY=90.5 EndZ=0
  constraints (66):
    c: Symmetric(g0,g0,g-2)
    c: Equal(g1,g0)
    c: Symmetric(g1,g1,g-2)
    c: Symmetric(g2,g2,g-1)
    c: Symmetric(g3,g3,g-1)
    c: Equal(g3,g2)
    c: Symmetric(g0,g1,g-1)
    c: Symmetric(g2,g3,g-2)
    c: Coincident(g4,g2)
    c: Tangent(g7,g0) = 1.5708
    c: Tangent(g7,g3) = -1.5708
    c: Tangent(g0,g4) = 1.5708
    c: Coincident(g5,g1)
    c: Tangent(g5,g2) = 1.5708
    c: Coincident(g3,g6)
    c: Tangent(g6,g1) = -1.5708
    c: Distance(g3,g2) = 240
    c: Radius(g4) = 5
    c: Distance(g0,g1) = 180
    c: Diameter(g8) = 6.5
    c: DistanceY(g8,g0) = 10
    c: DistanceX(g8,g2) = 10
    c: Equal(g9,g8)
    c: Symmetric(g9,g8,g-2)
    c: Equal(g11,g10)
    c: Equal(g10,g8)
    c: Symmetric(g10,g8,g-1)
    c: Symmetric(g11,g10,g-2)
    c: PointOnObject(g12,g-1)
    c: PointOnObject(g13,g-1)
    c: Equal(g13,g12)
    c: Equal(g12,g8)
    c: Vertical(g12,g8)
    c: Vertical(g13,g9)
    c: Equal(g15,g14)
    c: Equal(g14,g8)
    c: PointOnObject(g15,g-2)
    c: Symmetric(g15,g14,g-1)
    c: DistanceY(g14,g0) = 20
    c: Radius(g16) = 5.5
    c: Coincident(g16,g4)
    c: Horizontal(g16,g16)
    c: Vertical(g16,g16)
    c: Horizontal(g17)
    c: DistanceX(g17,g17) = 10
    c: Coincident(g17,g16)
    c: DistanceY(g16,g18) = 5
    c: Vertical(g16,g18)
    c: Horizontal(g18)
    c: Horizontal(g19,g16)
    c: Coincident(g18,g19)
    c: Coincident(g4,g19)
    c: Vertical(g20)
    c: PointOnObject(g22,g-1)
    c: Coincident(g21,g22)
    c: PointOnObject(g20,g-1)
    c: Coincident(g21,g20)
    c: Coincident(g20,g16)
    c: Vertical(g22)
    c: Coincident(g22,g19)
    c: Vertical(g17,g18)
    c: Tangent(g23,g18) = 1.5708
    c: Equal(g19,g23)
    c: Horizontal(g23,g17)
    c: Coincident(g24,g23)
    c: Coincident(g17,g24)
FEATURE [PartDesign::Pad] Pad029
  Length = 14
  Length2 = 100
  Profile = -> CopySketch009
  Reversed = true
  Type = 0
FEATURE [PartDesign::Mirrored] Mirrored007
  BaseFeature = -> Pad029
  MirrorPlane = -> CopySketch009 [H_Axis]
  Originals = -> [Pad029]
FEATURE [Sketcher::SketchObject] Sketch066
  MapMode = 5
  Placement = pos=(0,0,-14) rot=(1,0,0;3.14159rad)
  Support = -> [Mirrored007]
  expr: Constraints[17] = CopySketch009.Constraints[17]
  expr: Constraints[38] = CopySketch009.Constraints[38]
  expr: Constraints[21] = CopySketch009.Constraints[21]
  expr: Constraints[20] = CopySketch009.Constraints[20]
  expr: Constraints[19] = CopySketch009.Constraints[19]
  expr: Constraints[18] = CopySketch009.Constraints[18]
  expr: Constraints[16] = CopySketch009.Constraints[16]
  sketch-geometry (23):
    g0: LineSegment [constr] StartX=-115 StartY=90 StartZ=0 EndX=115 EndY=90 EndZ=0
    g1: LineSegment [constr] StartX=-115 StartY=-90 StartZ=0 EndX=115 EndY=-90 EndZ=0
    g2: LineSegment [constr] StartX=120 StartY=85 StartZ=0 EndX=120 EndY=-85 EndZ=0
    g3: LineSegment [constr] StartX=-120 StartY=85 StartZ=0 EndX=-120 EndY=-85 EndZ=0
    g4: ArcOfCircle [constr] CenterX=115 CenterY=85 CenterZ=0 NormalX=0 NormalY=0 NormalZ=1 AngleXU=0 Radius=5 StartAngle=-8.8418e-12 EndAngle=1.5708
    g5: ArcOfCircle [constr] CenterX=115 CenterY=-85 CenterZ=0 NormalX=0 NormalY=0 NormalZ=1 AngleXU=0 Radius=5 StartAngle=4.71239 EndAngle=6.28319
    g6: ArcOfCircle [constr] CenterX=-115 CenterY=-85 CenterZ=0 NormalX=0 NormalY=0 NormalZ=1 AngleXU=0 Radius=5 StartAngle=3.14159 EndAngle=4.71239
    g7: ArcOfCircle [constr] CenterX=-115 CenterY=85 CenterZ=0 NormalX=0 NormalY=0 NormalZ=1 AngleXU=0 Radius=5 StartAngle=1.5708 EndAngle=3.14159
    g8: Circle [constr] CenterX=110 CenterY=80 CenterZ=0 NormalX=0 NormalY=0 NormalZ=1 AngleXU=0 Radius=3.25
    g9: Circle [constr] CenterX=-110 CenterY=80 CenterZ=0 NormalX=0 NormalY=0 NormalZ=1 AngleXU=0 Radius=3.25
    g10: Circle [constr] CenterX=110 CenterY=-80 CenterZ=0 NormalX=0 NormalY=0 NormalZ=1 AngleXU=0 Radius=3.25
    g11: Circle [constr] CenterX=-110 CenterY=-80 CenterZ=0 NormalX=0 NormalY=0 NormalZ=1 AngleXU=0 Radius=3.25
    g12: Circle [constr] CenterX=110 CenterY=0 CenterZ=0 NormalX=0 NormalY=0 NormalZ=1 AngleXU=0 Radius=3.25
    g13: Circle [constr] CenterX=-110 CenterY=0 CenterZ=0 NormalX=0 NormalY=0 NormalZ=1 AngleXU=0 Radius=3.25
    g14: Circle [constr] CenterX=0 CenterY=70 CenterZ=0 NormalX=0 NormalY=0 NormalZ=1 AngleXU=0 Radius=3.25
    g15: Circle [constr] CenterX=0 CenterY=-70 CenterZ=0 NormalX=0 NormalY=0 NormalZ=1 AngleXU=0 Radius=3.25
    g16: LineSegment StartX=105 StartY=95.5 StartZ=0 EndX=115 EndY=95.5 EndZ=0
    g17: ArcOfCircle CenterX=115 CenterY=85 CenterZ=0 NormalX=0 NormalY=0 NormalZ=1 AngleXU=0 Radius=10.5 StartAngle=-2.31e-14 EndAngle=1.5708
    g18: LineSegment StartX=94.5 StartY=0 StartZ=0 EndX=125.5 EndY=0 EndZ=0
    g19: LineSegment StartX=125.5 StartY=0 StartZ=0 EndX=125.5 EndY=85 EndZ=0
    g20: LineSegment StartX=94.5 StartY=85 StartZ=0 EndX=94.5 EndY=0 EndZ=0
    g21: LineSegment [constr] StartX=110 StartY=80 StartZ=0 EndX=110 EndY=95.5 EndZ=0
    g22: ArcOfCircle CenterX=105 CenterY=85 CenterZ=0 NormalX=0 NormalY=0 NormalZ=1 AngleXU=0 Radius=10.5 StartAngle=1.5708 EndAngle=3.14159
  constraints (59):
    c: Symmetric(g0,g0,g-2)
    c: Equal(g1,g0)
    c: Symmetric(g1,g1,g-2)
    c: Symmetric(g2,g2,g-1)
    c: Symmetric(g3,g3,g-1)
    c: Equal(g3,g2)
    c: Symmetric(g0,g1,g-1)
    c: Symmetric(g2,g3,g-2)
    c: Coincident(g4,g2)
    c: Tangent(g7,g0) = 1.5708
    c: Tangent(g7,g3) = -1.5708
    c: Tangent(g0,g4) = 1.5708
    c: Coincident(g5,g1)
    c: Tangent(g5,g2) = 1.5708
    c: Coincident(g3,g6)
    c: Tangent(g6,g1) = -1.5708
    c: Distance(g3,g2) = 240
    c: Radius(g4) = 5
    c: Distance(g0,g1) = 180
    c: Diameter(g8) = 6.5
    c: DistanceY(g8,g0) = 10
    c: DistanceX(g8,g2) = 10
    c: Equal(g9,g8)
    c: Symmetric(g9,g8,g-2)
    c: Equal(g11,g10)
    c: Equal(g10,g8)
    c: Symmetric(g10,g8,g-1)
    c: Symmetric(g11,g10,g-2)
    c: PointOnObject(g12,g-1)
    c: PointOnObject(g13,g-1)
    c: Equal(g13,g12)
    c: Equal(g12,g8)
    c: Vertical(g12,g8)
    c: Vertical(g13,g9)
    c: Equal(g15,g14)
    c: Equal(g14,g8)
    c: PointOnObject(g15,g-2)
    c: Symmetric(g15,g14,g-1)
    c: DistanceY(g14,g0) = 20
    c: Horizontal(g16)
    c: PointOnObject(g19,g-1)
    c: Coincident(g18,g19)
    c: Vertical(g19)
    c: Horizontal(g17,g20)
    c: Tangent(g19,g17) = -1.5708
    c: DistanceX(g2,g17) = 5.5
    c: Tangent(g16,g17) = 1.5708
    c: Vertical(g16,g0)
    c: Horizontal(g2,g17)
    c: Vertical(g20,g18)
    c: PointOnObject(g18,g-1)
    c: Coincident(g20,g18)
    c: Coincident(g21,g8)
    c: PointOnObject(g21,g16)
    c: Symmetric(g16,g16,g21)
    c: Vertical(g22,g22)
    c: Horizontal(g22,g22)
    c: Coincident(g16,g22)
    c: Coincident(g22,g20)
FEATURE [PartDesign::Pad] Pad030
  BaseFeature = -> Mirrored007
  Length = 14
  Length2 = 100
  Profile = -> Sketch066
  Type = 0
FEATURE [PartDesign::Mirrored] Mirrored008
  BaseFeature = -> Pad030
  MirrorPlane = -> Sketch066 [H_Axis]
  Originals = -> [Pad030]
FEATURE [Sketcher::SketchObject] Sketch069
  ExternalGeometry = -> [Pocket033]
  MapMode = 5
  Placement = pos=(0,0,304) rot=(0,0,1;0rad)
  Support = -> [Pocket034]
  expr: Constraints[34] = Sketch062.Constraints[9]
  expr: Constraints[97] = Sketch063.Constraints[25]
  expr: Constraints[96] = Sketch063.Constraints[24]
  expr: Constraints[18] = Sketch061.Constraints[18]
  expr: Constraints[92] = Sketch063.Constraints[20]
  expr: Constraints[80] = Sketch063.Constraints[8]
  expr: Constraints[23] = Sketch061.Constraints[23]
  expr: Constraints[71] = Sketch062.Constraints[46]
  expr: Constraints[15] = Sketch061.Constraints[15]
  expr: Constraints[48] = Sketch062.Constraints[23]
  expr: Constraints[16] = Sketch061.Constraints[16]
  expr: Constraints[44] = Sketch062.Constraints[19]
  expr: Constraints[52] = Sketch062.Constraints[27]
  expr: Constraints[40] = Sketch062.Constraints[15]
  expr: Constraints[65] = Sketch062.Constraints[40]
  expr: Constraints[39] = Sketch062.Constraints[14]
  expr: Constraints[29] = Sketch062.Constraints[3]
  expr: Constraints[25] = Sketch061.Constraints[25]
  expr: Constraints[24] = Sketch061.Constraints[24]
  expr: Constraints[35] = Sketch062.Constraints[10]
  expr: Constraints[41] = Sketch062.Constraints[16]
  expr: Constraints[17] = Sketch061.Constraints[17]
  expr: Constraints[70] = Sketch062.Constraints[45]
  expr: Constraints[67] = Sketch062.Constraints[42]
  sketch-geometry (41):
    g0: LineSegment StartX=-105 StartY=-49 StartZ=0 EndX=105 EndY=-49 EndZ=0
    g1: LineSegment StartX=105 StartY=-49 StartZ=0 EndX=105 EndY=-64 EndZ=0
    g2: LineSegment StartX=105 StartY=-64 StartZ=0 EndX=88 EndY=-81 EndZ=0
    g3: LineSegment StartX=88 StartY=-81 StartZ=0 EndX=8.5 EndY=-81 EndZ=0
    g4: LineSegment StartX=8.5 StartY=-81 StartZ=0 EndX=8.5 EndY=-61 EndZ=0
    g5: LineSegment StartX=8.5 StartY=-61 StartZ=0 EndX=-8.5 EndY=-61 EndZ=0
    g6: LineSegment StartX=-8.5 StartY=-61 StartZ=0 EndX=-8.5 EndY=-81 EndZ=0
    g7: LineSegment StartX=-8.5 StartY=-81 StartZ=0 EndX=-88 EndY=-81 EndZ=0
    g8: LineSegment StartX=-88 StartY=-81 StartZ=0 EndX=-105 EndY=-64 EndZ=0
    g9: LineSegment StartX=-105 StartY=-64 StartZ=0 EndX=-105 EndY=-49 EndZ=0
    g10: Circle CenterX=-60 CenterY=-58 CenterZ=0 NormalX=0 NormalY=0 NormalZ=1 AngleXU=0 Radius=3.5
    g11: Circle CenterX=-60 CenterY=-72 CenterZ=0 NormalX=0 NormalY=0 NormalZ=1 AngleXU=0 Radius=3.5
    g12: Circle CenterX=-80 CenterY=-65 CenterZ=0 NormalX=0 NormalY=0 NormalZ=1 AngleXU=0 Radius=3.5
    g13: Circle CenterX=-25 CenterY=-76.75 CenterZ=0 NormalX=0 NormalY=0 NormalZ=1 AngleXU=0 Radius=1.25
    g14: Circle CenterX=-48.5 CenterY=-76.75 CenterZ=0 NormalX=0 NormalY=0 NormalZ=1 AngleXU=0 Radius=1.25
    g15: Circle CenterX=-48.5 CenterY=-53.25 CenterZ=0 NormalX=0 NormalY=0 NormalZ=1 AngleXU=0 Radius=1.25
    g16: Circle CenterX=-25 CenterY=-53.25 CenterZ=0 NormalX=0 NormalY=0 NormalZ=1 AngleXU=0 Radius=1.25
    g17: Circle CenterX=30 CenterY=-65 CenterZ=0 NormalX=0 NormalY=0 NormalZ=1 AngleXU=0 Radius=3.5
    g18: Circle CenterX=55 CenterY=-65 CenterZ=0 NormalX=0 NormalY=0 NormalZ=1 AngleXU=0 Radius=3.5
    g19: Circle CenterX=80 CenterY=-65 CenterZ=0 NormalX=0 NormalY=0 NormalZ=1 AngleXU=0 Radius=3.5
    g20: Circle CenterX=97.5 CenterY=-65 CenterZ=0 NormalX=0 NormalY=0 NormalZ=1 AngleXU=0 Radius=2
    g21: Circle CenterX=12.5 CenterY=-65 CenterZ=0 NormalX=0 NormalY=0 NormalZ=1 AngleXU=0 Radius=2
    g22: Circle CenterX=-12.5 CenterY=-65 CenterZ=0 NormalX=0 NormalY=0 NormalZ=1 AngleXU=0 Radius=2
    g23: Circle CenterX=-97.5 CenterY=-65 CenterZ=0 NormalX=0 NormalY=0 NormalZ=1 AngleXU=0 Radius=2
    g24: LineSegment [constr] StartX=-97.5 StartY=-65 StartZ=0 EndX=97.5 EndY=-65 EndZ=0
    g25: LineSegment [constr] StartX=-25 StartY=-76.75 StartZ=0 EndX=-48.5 EndY=-76.75 EndZ=0
    g26: LineSegment [constr] StartX=-48.5 StartY=-76.75 StartZ=0 EndX=-48.5 EndY=-53.25 EndZ=0
    g27: LineSegment [constr] StartX=-48.5 StartY=-53.25 StartZ=0 EndX=-25 EndY=-53.25 EndZ=0
    g28: LineSegment [constr] StartX=-25 StartY=-53.25 StartZ=0 EndX=-25 EndY=-76.75 EndZ=0
    g29: Circle CenterX=38.5 CenterY=-65 CenterZ=0 NormalX=0 NormalY=0 NormalZ=1 AngleXU=0 Radius=1.75
    g30: Circle CenterX=63.5 CenterY=-65 CenterZ=0 NormalX=0 NormalY=0 NormalZ=1 AngleXU=0 Radius=1.75
    g31: Circle CenterX=88.5 CenterY=-65 CenterZ=0 NormalX=0 NormalY=0 NormalZ=1 AngleXU=0 Radius=1.75
    g32: Circle CenterX=-71.5 CenterY=-65 CenterZ=0 NormalX=0 NormalY=0 NormalZ=1 AngleXU=0 Radius=1.75
    g33: Circle CenterX=-66 CenterY=-72 CenterZ=0 NormalX=0 NormalY=0 NormalZ=1 AngleXU=0 Radius=1.75
    g34: Circle CenterX=-66 CenterY=-58 CenterZ=0 NormalX=0 NormalY=0 NormalZ=1 AngleXU=0 Radius=1.75
    g35: Circle [constr] CenterX=-80 CenterY=-65 CenterZ=0 NormalX=0 NormalY=0 NormalZ=1 AngleXU=0 Radius=8.5
    g36: Circle [constr] CenterX=-60 CenterY=-58 CenterZ=0 NormalX=0 NormalY=0 NormalZ=1 AngleXU=0 Radius=6
    g37: Circle [constr] CenterX=-60 CenterY=-72 CenterZ=0 NormalX=0 NormalY=0 NormalZ=1 AngleXU=0 Radius=6
    g38: Circle [constr] CenterX=30 CenterY=-65 CenterZ=0 NormalX=0 NormalY=0 NormalZ=1 AngleXU=0 Radius=8.5
    g39: Circle [constr] CenterX=55 CenterY=-65 CenterZ=0 NormalX=0 NormalY=0 NormalZ=1 AngleXU=0 Radius=8.5
    g40: Circle [constr] CenterX=80 CenterY=-65 CenterZ=0 NormalX=0 NormalY=0 NormalZ=1 AngleXU=0 Radius=8.5
  constraints (103):
    c: Coincident(g1,g0)
    c: Vertical(g1)
    c: Coincident(g2,g1)
    c: Coincident(g3,g2)
    c: Horizontal(g3)
    c: Coincident(g4,g3)
    c: Coincident(g5,g4)
    c: Coincident(g6,g5)
    c: Horizontal(g7)
    c: Coincident(g9,g8)
    c: Coincident(g9,g0)
    c: Vertical(g4)
    c: Vertical(g6)
    c: Symmetric(g4,g5,g-2)
    c: Coincident(g6,g7)
    c: DistanceY(g4,g-1) = 61
    c: DistanceY(g3,g-1) = 81
    c: DistanceX(g5,g5) = 17
    c: Angle(g2,g3) = 2.35619
    c: Coincident(g8,g7)
    c: Symmetric(g7,g2,g-2)
    c: Symmetric(g8,g1,g-2)
    c: Symmetric(g0,g0,g-2)
    c: DistanceY(g4,g0) = 12
    c: DistanceY(g1,g1) = 15
    c: DistanceX(g-1,g0) = 105
    c: Equal(g23,g22)
    c: Equal(g22,g21)
    c: Equal(g21,g20)
    c: Diameter(g20) = 4
    c: Coincident(g24,g20)
    c: PointOnObject(g21,g24)
    c: Symmetric(g21,g22,g-2)
    c: Symmetric(g20,g23,g-2)
    c: DistanceX(g-1,g21) = 12.5
    c: DistanceX(g-1,g20) = 97.5
    c: PointOnObject(g19,g24)
    c: PointOnObject(g18,g24)
    c: PointOnObject(g17,g24)
    c: DistanceX(g-1,g17) = 30
    c: DistanceX(g-1,g18) = 55
    c: DistanceX(g-1,g19) = 80
    c: Equal(g19,g18)
    c: Equal(g18,g17)
    c: Diameter(g17) = 7
    c: Equal(g12,g17)
    c: Symmetric(g12,g19,g-2)
    c: Equal(g11,g10)
    c: Diameter(g11) = 7
    c: Equal(g13,g14)
    c: Equal(g14,g15)
    c: Equal(g15,g16)
    c: Diameter(g14) = 2.5
    c: Coincident(g25,g26)
    c: Coincident(g26,g27)
    c: Coincident(g27,g28)
    c: Coincident(g28,g25)
    c: Horizontal(g25)
    c: Horizontal(g27)
    c: Vertical(g28)
    c: Coincident(g25,g13)
    c: Coincident(g26,g15)
    c: Coincident(g16,g27)
    c: Coincident(g14,g25)
    c: Equal(g26,g25)
    c: DistanceY(g26,g26) = 23.5
    c: Symmetric(g15,g14,g24)
    c: DistanceX(g13,g-1) = 25
    c: Coincident(g24,g23)
    c: Symmetric(g11,g10,g24)
    c: DistanceY(g11,g10) = 14
    c: DistanceX(g11,g-1) = 60
    c: Coincident(g35,g-3)
    c: Coincident(g36,g-4)
    c: Coincident(g38,g-5)
    c: Coincident(g39,g-6)
    c: Coincident(g40,g-7)
    c: Equal(g35,g38)
    c: Equal(g38,g39)
    c: Equal(g39,g40)
    c: Diameter(g35) = 17
    c: Equal(g32,g34)
    c: Equal(g34,g33)
    c: Equal(g33,g29)
    c: Equal(g29,g30)
    c: Equal(g30,g31)
    c: Horizontal(g29,g38)
    c: PointOnObject(g29,g38)
    c: Horizontal(g39,g30)
    c: PointOnObject(g30,g39)
    c: Horizontal(g31,g40)
    c: PointOnObject(g31,g40)
    c: Diameter(g29) = 3.5
    c: Horizontal(g32,g35)
    c: PointOnObject(g32,g35)
    c: PointOnObject(g34,g36)
    c: Diameter(g36) = 12
    c: Diameter(g37) = 12
    c: PointOnObject(g33,g37)
    c: Coincident(g-8,g37)
    c: Horizontal(g34,g36)
    c: Horizontal(g33,g37)
    c: DistanceY(g22,g-1) = 65
FEATURE [Sketcher::SketchObject] Sketch070
  MapMode = 5
  Placement = pos=(0,0,304) rot=(0,0,1;0rad)
  Support = -> [Pocket034]
  expr: Constraints[17] = Sketch062.Constraints[42]
  expr: Constraints[15] = Sketch062.Constraints[40]
  sketch-geometry (10):
    g0: Circle CenterX=-25 CenterY=-76.75 CenterZ=0 NormalX=0 NormalY=0 NormalZ=1 AngleXU=0 Radius=2.25
    g1: Circle CenterX=-48.5 CenterY=-76.75 CenterZ=0 NormalX=0 NormalY=0 NormalZ=1 AngleXU=0 Radius=2.25
    g2: Circle CenterX=-48.5 CenterY=-53.25 CenterZ=0 NormalX=0 NormalY=0 NormalZ=1 AngleXU=0 Radius=2.25
    g3: Circle CenterX=-25 CenterY=-53.25 CenterZ=0 NormalX=0 NormalY=0 NormalZ=1 AngleXU=0 Radius=2.25
    g4: Circle [constr] CenterX=0 CenterY=-65 CenterZ=0 NormalX=0 NormalY=0 NormalZ=1 AngleXU=0 Radius=2.5
    g5: LineSegment [constr] StartX=-48.5 StartY=-65 StartZ=0 EndX=48.5 EndY=-65 EndZ=0
    g6: LineSegment [constr] StartX=-25 StartY=-76.75 StartZ=0 EndX=-48.5 EndY=-76.75 EndZ=0
    g7: LineSegment [constr] StartX=-48.5 StartY=-76.75 StartZ=0 EndX=-48.5 EndY=-53.25 EndZ=0
    g8: LineSegment [constr] StartX=-48.5 StartY=-53.25 StartZ=0 EndX=-25 EndY=-53.25 EndZ=0
    g9: LineSegment [constr] StartX=-25 StartY=-53.25 StartZ=0 EndX=-25 EndY=-76.75 EndZ=0
  constraints (25):
    c: Equal(g0,g1)
    c: Equal(g1,g2)
    c: Equal(g2,g3)
    c: Coincident(g6,g7)
    c: Coincident(g7,g8)
    c: Coincident(g8,g9)
    c: Coincident(g9,g6)
    c: Horizontal(g6)
    c: Horizontal(g8)
    c: Vertical(g9)
    c: Coincident(g6,g0)
    c: Coincident(g7,g2)
    c: Coincident(g3,g8)
    c: Coincident(g1,g6)
    c: Equal(g7,g6)
    c: DistanceY(g7,g7) = 23.5
    c: Symmetric(g2,g1,g5)
    c: DistanceX(g0,g-1) = 25
    c: DistanceY(g4,g-1) = 65
    c: Diameter(g1) = 4.5
    c: PointOnObject(g4,g5)
    c: PointOnObject(g4,g-2)
    c: Symmetric(g5,g5,g-2)
    c: PointOnObject(g5,g7)
    c: Diameter(g4) = 5
FEATURE [PartDesign::Pocket] Pocket038
  BaseFeature = -> Pocket034
  Length = 2
  Length2 = 100
  Placement = pos=(0,0,300) rot=(0,0,1;0rad)
  Profile = -> Sketch070
  Type = 0
FEATURE [Sketcher::SketchObject] Sketch071
  MapMode = 5
  Placement = pos=(0,0,304) rot=(0,0,1;0rad)
  Support = -> [Pocket038]
  expr: Constraints[27] = Sketch070.Constraints[19]
  expr: Constraints[32] = Sketch070.Constraints[24]
  expr: Constraints[26] = Sketch070.Constraints[18]
  expr: Constraints[25] = Sketch070.Constraints[17]
  expr: Constraints[23] = Sketch070.Constraints[15]
  sketch-geometry (14):
    g0: LineSegment StartX=-48.5 StartY=-55.75 StartZ=0 EndX=-25 EndY=-55.75 EndZ=0
    g1: LineSegment StartX=-25 StartY=-55.75 StartZ=0 EndX=-25 EndY=-71.25 EndZ=0
    g2: LineSegment StartX=-25 StartY=-71.25 StartZ=0 EndX=-48.5 EndY=-71.25 EndZ=0
    g3: LineSegment StartX=-48.5 StartY=-71.25 StartZ=0 EndX=-48.5 EndY=-55.75 EndZ=0
    g4: Circle [constr] CenterX=-25 CenterY=-76.75 CenterZ=0 NormalX=0 NormalY=0 NormalZ=1 AngleXU=0 Radius=2.25
    g5: Circle [constr] CenterX=-48.5 CenterY=-76.75 CenterZ=0 NormalX=0 NormalY=0 NormalZ=1 AngleXU=0 Radius=2.25
    g6: Circle [constr] CenterX=-48.5 CenterY=-53.25 CenterZ=0 NormalX=0 NormalY=0 NormalZ=1 AngleXU=0 Radius=2.25
    g7: Circle [constr] CenterX=-25 CenterY=-53.25 CenterZ=0 NormalX=0 NormalY=0 NormalZ=1 AngleXU=0 Radius=2.25
    g8: Circle [constr] CenterX=0 CenterY=-65 CenterZ=0 NormalX=0 NormalY=0 NormalZ=1 AngleXU=0 Radius=2.5
    g9: LineSegment [constr] StartX=-48.5 StartY=-65 StartZ=0 EndX=48.5 EndY=-65 EndZ=0
    g10: LineSegment [constr] StartX=-25 StartY=-76.75 StartZ=0 EndX=-48.5 EndY=-76.75 EndZ=0
    g11: LineSegment [constr] StartX=-48.5 StartY=-76.75 StartZ=0 EndX=-48.5 EndY=-53.25 EndZ=0
    g12: LineSegment [constr] StartX=-48.5 StartY=-53.25 StartZ=0 EndX=-25 EndY=-53.25 EndZ=0
    g13: LineSegment [constr] StartX=-25 StartY=-53.25 StartZ=0 EndX=-25 EndY=-76.75 EndZ=0
  constraints (37):
    c: Coincident(g0,g1)
    c: Coincident(g1,g2)
    c: Coincident(g2,g3)
    c: Coincident(g3,g0)
    c: Horizontal(g0)
    c: Horizontal(g2)
    c: Vertical(g1)
    c: Vertical(g3)
    c: Equal(g4,g5)
    c: Equal(g5,g6)
    c: Equal(g6,g7)
    c: Coincident(g10,g11)
    c: Coincident(g11,g12)
    c: Coincident(g12,g13)
    c: Coincident(g13,g10)
    c: Horizontal(g10)
    c: Horizontal(g12)
    c: Vertical(g13)
    c: Coincident(g10,g4)
    c: Coincident(g11,g6)
    c: Coincident(g7,g12)
    c: Coincident(g5,g10)
    c: Equal(g11,g10)
    c: DistanceY(g11,g11) = 23.5
    c: Symmetric(g6,g5,g9)
    c: DistanceX(g4,g-1) = 25
    c: DistanceY(g8,g-1) = 65
    c: Diameter(g5) = 4.5
    c: PointOnObject(g8,g9)
    c: PointOnObject(g8,g-2)
    c: Symmetric(g9,g9,g-2)
    c: PointOnObject(g9,g11)
    c: Diameter(g8) = 5
    c: PointOnObject(g0,g13)
    c: PointOnObject(g0,g11)
    c: DistanceY(g0,g7) = 2.5
    c: DistanceY(g1,g1) = 15.5
FEATURE [PartDesign::Pocket] Pocket039
  BaseFeature = -> Pocket038
  Length = 5
  Length2 = 100
  Placement = pos=(0,0,300) rot=(0,0,1;0rad)
  Profile = -> Sketch071
  Type = 0
FEATURE [PartDesign::Body] Body019  label="UI_Blende"
  Group = -> [DatumPlane011,Sketch061,Pad027,Sketch062,Pocket033,Sketch063,Pocket034,Sketch069,Sketch070,Pocket038,Sketch071,Pocket039]
  Origin = -> Origin019
  Placement = pos=(0,0,4) rot=(0,0,1;0rad)
  Tip = -> Pocket039
FEATURE [PartDesign::Plane] DatumPlane012
  AttachmentOffset = pos=(0,0,-28) rot=(0,0,1;0rad)
  Length = 167.675
  MapMode = 5
  Placement = pos=(0,0,-28) rot=(0,0,1;0rad)
  ResizeMode = 0
  Support = -> [XY_Plane020]
  Width = 223.175
FEATURE [Sketcher::SketchObject] CopySketch010  label="GroundSketch"
  Placement = pos=(0,0,-28) rot=(0,0,1;0rad)
  sketch-geometry (16):
    g0: LineSegment [constr] StartX=-115 StartY=90 StartZ=0 EndX=115 EndY=90 EndZ=0
    g1: LineSegment [constr] StartX=-115 StartY=-90 StartZ=0 EndX=115 EndY=-90 EndZ=0
    g2: LineSegment [constr] StartX=120 StartY=85 StartZ=0 EndX=120 EndY=-85 EndZ=0
    g3: LineSegment [constr] StartX=-120 StartY=85 StartZ=0 EndX=-120 EndY=-85 EndZ=0
    g4: ArcOfCircle [constr] CenterX=115 CenterY=85 CenterZ=0 NormalX=0 NormalY=0 NormalZ=1 AngleXU=0 Radius=5 StartAngle=-9e-16 EndAngle=1.5708
    g5: ArcOfCircle [constr] CenterX=115 CenterY=-85 CenterZ=0 NormalX=0 NormalY=0 NormalZ=1 AngleXU=0 Radius=5 StartAngle=4.71239 EndAngle=6.28319
    g6: ArcOfCircle [constr] CenterX=-115 CenterY=-85 CenterZ=0 NormalX=0 NormalY=0 NormalZ=1 AngleXU=0 Radius=5 StartAngle=3.14159 EndAngle=4.71239
    g7: ArcOfCircle [constr] CenterX=-115 CenterY=85 CenterZ=0 NormalX=0 NormalY=0 NormalZ=1 AngleXU=0 Radius=5 StartAngle=1.5708 EndAngle=3.14159
    g8: Circle CenterX=110 CenterY=80 CenterZ=0 NormalX=0 NormalY=0 NormalZ=1 AngleXU=0 Radius=3.25
    g9: Circle [constr] CenterX=-110 CenterY=80 CenterZ=0 NormalX=0 NormalY=0 NormalZ=1 AngleXU=0 Radius=3.25
    g10: Circle CenterX=110 CenterY=-80 CenterZ=0 NormalX=0 NormalY=0 NormalZ=1 AngleXU=0 Radius=3.25
    g11: Circle [constr] CenterX=-110 CenterY=-80 CenterZ=0 NormalX=0 NormalY=0 NormalZ=1 AngleXU=0 Radius=3.25
    g12: Circle CenterX=110 CenterY=0 CenterZ=0 NormalX=0 NormalY=0 NormalZ=1 AngleXU=0 Radius=3.25
    g13: Circle [constr] CenterX=-110 CenterY=0 CenterZ=0 NormalX=0 NormalY=0 NormalZ=1 AngleXU=0 Radius=3.25
    g14: Circle [constr] CenterX=0 CenterY=70 CenterZ=0 NormalX=0 NormalY=0 NormalZ=1 AngleXU=0 Radius=3.25
    g15: Circle [constr] CenterX=0 CenterY=-70 CenterZ=0 NormalX=0 NormalY=0 NormalZ=1 AngleXU=0 Radius=3.25
  constraints (39):
    c: Symmetric(g0,g0,g-2)
    c: Equal(g1,g0)
    c: Symmetric(g1,g1,g-2)
    c: Symmetric(g2,g2,g-1)
    c: Symmetric(g3,g3,g-1)
    c: Equal(g3,g2)
    c: Symmetric(g0,g1,g-1)
    c: Symmetric(g2,g3,g-2)
    c: Coincident(g4,g2)
    c: Tangent(g7,g0) = 1.5708
    c: Tangent(g7,g3) = -1.5708
    c: Tangent(g0,g4) = 1.5708
    c: Coincident(g5,g1)
    c: Tangent(g5,g2) = 1.5708
    c: Coincident(g3,g6)
    c: Tangent(g6,g1) = -1.5708
    c: Distance(g3,g2) = 240
    c: Radius(g4) = 5
    c: Distance(g0,g1) = 180
    c: Diameter(g8) = 6.5
    c: DistanceY(g8,g0) = 10
    c: DistanceX(g8,g2) = 10
    c: Equal(g9,g8)
    c: Symmetric(g9,g8,g-2)
    c: Equal(g11,g10)
    c: Equal(g10,g8)
    c: Symmetric(g10,g8,g-1)
    c: Symmetric(g11,g10,g-2)
    c: PointOnObject(g12,g-1)
    c: PointOnObject(g13,g-1)
    c: Equal(g13,g12)
    c: Equal(g12,g8)
    c: Vertical(g12,g8)
    c: Vertical(g13,g9)
    c: Equal(g15,g14)
    c: Equal(g14,g8)
    c: PointOnObject(g15,g-2)
    c: Symmetric(g15,g14,g-1)
    c: DistanceY(g14,g0) = 20
FEATURE [PartDesign::Pocket] Pocket040
  BaseFeature = -> Mirrored008
  Length = 9
  Length2 = 100
  Profile = -> CopySketch010
  Reversed = true
  Type = 1
FEATURE [Sketcher::SketchObject] CopySketch011  label="GroundSketch001"
  Placement = pos=(0,0,-28) rot=(0,0,1;0rad)
  sketch-geometry (16):
    g0: LineSegment [constr] StartX=-115 StartY=90 StartZ=0 EndX=115 EndY=90 EndZ=0
    g1: LineSegment [constr] StartX=-115 StartY=-90 StartZ=0 EndX=115 EndY=-90 EndZ=0
    g2: LineSegment [constr] StartX=120 StartY=85 StartZ=0 EndX=120 EndY=-85 EndZ=0
    g3: LineSegment [constr] StartX=-120 StartY=85 StartZ=0 EndX=-120 EndY=-85 EndZ=0
    g4: ArcOfCircle [constr] CenterX=115 CenterY=85 CenterZ=0 NormalX=0 NormalY=0 NormalZ=1 AngleXU=0 Radius=5 StartAngle=-9e-16 EndAngle=1.5708
    g5: ArcOfCircle [constr] CenterX=115 CenterY=-85 CenterZ=0 NormalX=0 NormalY=0 NormalZ=1 AngleXU=0 Radius=5 StartAngle=4.71239 EndAngle=6.28319
    g6: ArcOfCircle [constr] CenterX=-115 CenterY=-85 CenterZ=0 NormalX=0 NormalY=0 NormalZ=1 AngleXU=0 Radius=5 StartAngle=3.14159 EndAngle=4.71239
    g7: ArcOfCircle [constr] CenterX=-115 CenterY=85 CenterZ=0 NormalX=0 NormalY=0 NormalZ=1 AngleXU=0 Radius=5 StartAngle=1.5708 EndAngle=3.14159
    g8: Circle CenterX=110 CenterY=80 CenterZ=0 NormalX=0 NormalY=0 NormalZ=1 AngleXU=0 Radius=8
    g9: Circle [constr] CenterX=-110 CenterY=80 CenterZ=0 NormalX=0 NormalY=0 NormalZ=1 AngleXU=0 Radius=8
    g10: Circle CenterX=110 CenterY=-80 CenterZ=0 NormalX=0 NormalY=0 NormalZ=1 AngleXU=0 Radius=8
    g11: Circle [constr] CenterX=-110 CenterY=-80 CenterZ=0 NormalX=0 NormalY=0 NormalZ=1 AngleXU=0 Radius=8
    g12: Circle CenterX=110 CenterY=0 CenterZ=0 NormalX=0 NormalY=0 NormalZ=1 AngleXU=0 Radius=8
    g13: Circle [constr] CenterX=-110 CenterY=0 CenterZ=0 NormalX=0 NormalY=0 NormalZ=1 AngleXU=0 Radius=8
    g14: Circle [constr] CenterX=0 CenterY=70 CenterZ=0 NormalX=0 NormalY=0 NormalZ=1 AngleXU=0 Radius=8
    g15: Circle [constr] CenterX=0 CenterY=-70 CenterZ=0 NormalX=0 NormalY=0 NormalZ=1 AngleXU=0 Radius=8
  constraints (39):
    c: Symmetric(g0,g0,g-2)
    c: Equal(g1,g0)
    c: Symmetric(g1,g1,g-2)
    c: Symmetric(g2,g2,g-1)
    c: Symmetric(g3,g3,g-1)
    c: Equal(g3,g2)
    c: Symmetric(g0,g1,g-1)
    c: Symmetric(g2,g3,g-2)
    c: Coincident(g4,g2)
    c: Tangent(g7,g0) = 1.5708
    c: Tangent(g7,g3) = -1.5708
    c: Tangent(g0,g4) = 1.5708
    c: Coincident(g5,g1)
    c: Tangent(g5,g2) = 1.5708
    c: Coincident(g3,g6)
    c: Tangent(g6,g1) = -1.5708
    c: Distance(g3,g2) = 240
    c: Radius(g4) = 5
    c: Distance(g0,g1) = 180
    c: Diameter(g8) = 16
    c: DistanceY(g8,g0) = 10
    c: DistanceX(g8,g2) = 10
    c: Equal(g9,g8)
    c: Symmetric(g9,g8,g-2)
    c: Equal(g11,g10)
    c: Equal(g10,g8)
    c: Symmetric(g10,g8,g-1)
    c: Symmetric(g11,g10,g-2)
    c: PointOnObject(g12,g-1)
    c: PointOnObject(g13,g-1)
    c: Equal(g13,g12)
    c: Equal(g12,g8)
    c: Vertical(g12,g8)
    c: Vertical(g13,g9)
    c: Equal(g15,g14)
    c: Equal(g14,g8)
    c: PointOnObject(g15,g-2)
    c: Symmetric(g15,g14,g-1)
    c: DistanceY(g14,g0) = 20
FEATURE [PartDesign::Pocket] Pocket041
  BaseFeature = -> Pocket040
  Length = 8
  Length2 = 100
  Profile = -> CopySketch011
  Reversed = true
  Type = 0
FEATURE [PartDesign::Chamfer] Chamfer006
  Base = -> Pocket041 [Edge16,Edge76]
  BaseFeature = -> Pocket041
  Size = 3
FEATURE [PartDesign::Body] Body020  label="Long_Foot"
  Group = -> [CopySketch009,Pad029,Mirrored007,Sketch066,Pad030,Mirrored008,DatumPlane012,CopySketch010,Pocket040,CopySketch011,Pocket041,Chamfer006]
  Origin = -> Origin020
  Tip = -> Chamfer006
FEATURE [Sketcher::SketchObject] CopySketch012  label="SketchGround001"
  MapMode = 2
  Support = -> [XY_Plane021]
  sketch-geometry (26):
    g0: LineSegment [constr] StartX=-115 StartY=90 StartZ=0 EndX=115 EndY=90 EndZ=0
    g1: LineSegment [constr] StartX=-115 StartY=-90 StartZ=0 EndX=115 EndY=-90 EndZ=0
    g2: LineSegment [constr] StartX=120 StartY=85 StartZ=0 EndX=120 EndY=-85 EndZ=0
    g3: LineSegment [constr] StartX=-120 StartY=85 StartZ=0 EndX=-120 EndY=-85 EndZ=0
    g4: ArcOfCircle [constr] CenterX=115 CenterY=85 CenterZ=0 NormalX=0 NormalY=0 NormalZ=1 AngleXU=0 Radius=5 StartAngle=1.2e-15 EndAngle=1.5708
    g5: ArcOfCircle [constr] CenterX=115 CenterY=-85 CenterZ=0 NormalX=0 NormalY=0 NormalZ=1 AngleXU=0 Radius=5 StartAngle=4.71239 EndAngle=6.28319
    g6: ArcOfCircle [constr] CenterX=-115 CenterY=-85 CenterZ=0 NormalX=0 NormalY=0 NormalZ=1 AngleXU=0 Radius=5 StartAngle=3.14159 EndAngle=4.71239
    g7: ArcOfCircle [constr] CenterX=-115 CenterY=85 CenterZ=0 NormalX=0 NormalY=0 NormalZ=1 AngleXU=0 Radius=5 StartAngle=1.5708 EndAngle=3.14159
    g8: Circle [constr] CenterX=110 CenterY=80 CenterZ=0 NormalX=0 NormalY=0 NormalZ=1 AngleXU=0 Radius=3.25
    g9: Circle [constr] CenterX=-110 CenterY=80 CenterZ=0 NormalX=0 NormalY=0 NormalZ=1 AngleXU=0 Radius=3.25
    g10: Circle [constr] CenterX=110 CenterY=-80 CenterZ=0 NormalX=0 NormalY=0 NormalZ=1 AngleXU=0 Radius=3.25
    g11: Circle [constr] CenterX=-110 CenterY=-80 CenterZ=0 NormalX=0 NormalY=0 NormalZ=1 AngleXU=0 Radius=3.25
    g12: Circle [constr] CenterX=110 CenterY=0 CenterZ=0 NormalX=0 NormalY=0 NormalZ=1 AngleXU=0 Radius=3.25
    g13: Circle [constr] CenterX=-110 CenterY=0 CenterZ=0 NormalX=0 NormalY=0 NormalZ=1 AngleXU=0 Radius=3.25
    g14: Circle [constr] CenterX=0 CenterY=70 CenterZ=0 NormalX=0 NormalY=0 NormalZ=1 AngleXU=0 Radius=3.25
    g15: Circle [constr] CenterX=0 CenterY=-70 CenterZ=0 NormalX=0 NormalY=0 NormalZ=1 AngleXU=0 Radius=3.25
    g16: ArcOfCircle CenterX=115 CenterY=85 CenterZ=0 NormalX=0 NormalY=0 NormalZ=1 AngleXU=0 Radius=5.5 StartAngle=0 EndAngle=1.5708
    g17: LineSegment StartX=115 StartY=90.5 StartZ=0 EndX=105 EndY=90.5 EndZ=0
    g18: LineSegment StartX=105 StartY=95.5 StartZ=0 EndX=115 EndY=95.5 EndZ=0
    g19: ArcOfCircle CenterX=115 CenterY=85 CenterZ=0 NormalX=0 NormalY=0 NormalZ=1 AngleXU=0 Radius=10.5 StartAngle=0 EndAngle=1.5708
    g20: LineSegment StartX=120.5 StartY=85 StartZ=0 EndX=120.5 EndY=75 EndZ=0
    g21: LineSegment StartX=125.5 StartY=75 StartZ=0 EndX=125.5 EndY=85 EndZ=0
    g22: LineSegment StartX=120.5 StartY=75 StartZ=0 EndX=120.5 EndY=66.0557 EndZ=0
    g23: ArcOfCircle CenterX=115 CenterY=75 CenterZ=0 NormalX=0 NormalY=0 NormalZ=1 AngleXU=0 Radius=10.5 StartAngle=5.26371 EndAngle=6.28319
    g24: ArcOfCircle CenterX=105 CenterY=85 CenterZ=0 NormalX=0 NormalY=0 NormalZ=1 AngleXU=0 Radius=10.5 StartAngle=1.5708 EndAngle=2.59028
    g25: LineSegment StartX=96.0557 StartY=90.5 StartZ=0 EndX=105 EndY=90.5 EndZ=0
  constraints (69):
    c: Symmetric(g0,g0,g-2)
    c: Equal(g1,g0)
    c: Symmetric(g1,g1,g-2)
    c: Symmetric(g2,g2,g-1)
    c: Symmetric(g3,g3,g-1)
    c: Equal(g3,g2)
    c: Symmetric(g0,g1,g-1)
    c: Symmetric(g2,g3,g-2)
    c: Coincident(g4,g2)
    c: Tangent(g7,g0) = 1.5708
    c: Tangent(g7,g3) = -1.5708
    c: Tangent(g0,g4) = 1.5708
    c: Coincident(g5,g1)
    c: Tangent(g5,g2) = 1.5708
    c: Coincident(g3,g6)
    c: Tangent(g6,g1) = -1.5708
    c: Distance(g3,g2) = 240
    c: Radius(g4) = 5
    c: Distance(g0,g1) = 180
    c: Diameter(g8) = 6.5
    c: DistanceY(g8,g0) = 10
    c: DistanceX(g8,g2) = 10
    c: Equal(g9,g8)
    c: Symmetric(g9,g8,g-2)
    c: Equal(g11,g10)
    c: Equal(g10,g8)
    c: Symmetric(g10,g8,g-1)
    c: Symmetric(g11,g10,g-2)
    c: PointOnObject(g12,g-1)
    c: PointOnObject(g13,g-1)
    c: Equal(g13,g12)
    c: Equal(g12,g8)
    c: Vertical(g12,g8)
    c: Vertical(g13,g9)
    c: Equal(g15,g14)
    c: Equal(g14,g8)
    c: PointOnObject(g15,g-2)
    c: Symmetric(g15,g14,g-1)
    c: DistanceY(g14,g0) = 20
    c: Radius(g16) = 5.5
    c: Coincident(g16,g4)
    c: Horizontal(g16,g16)
    c: Vertical(g16,g16)
    c: Horizontal(g17)
    c: DistanceX(g17,g17) = 10
    c: Coincident(g17,g16)
    c: DistanceY(g16,g18) = 5
    c: Vertical(g16,g18)
    c: Horizontal(g18)
    c: Horizontal(g19,g16)
    c: Coincident(g18,g19)
    c: Coincident(g4,g19)
    c: Vertical(g20)
    c: Coincident(g20,g16)
    c: Vertical(g21)
    c: Coincident(g21,g19)
    c: Vertical(g17,g18)
    c: Horizontal(g24,g17)
    c: Equal(g18,g21)
    c: Vertical(g22)
    c: Coincident(g23,g22)
    c: Coincident(g22,g20)
    c: Tangent(g24,g18) = 1.5708
    c: Tangent(g23,g21) = -1.5708
    c: Horizontal(g20,g21)
    c: Equal(g23,g19)
    c: Coincident(g24,g25)
    c: Equal(g24,g19)
    c: Coincident(g25,g17)
FEATURE [PartDesign::Pad] Pad031
  Length = 14
  Length2 = 100
  Profile = -> CopySketch012
  Reversed = true
  Type = 0
FEATURE [PartDesign::Plane] DatumPlane013
  AttachmentOffset = pos=(0,0,-28) rot=(0,0,1;0rad)
  Length = 159.413
  MapMode = 5
  Placement = pos=(0,0,-28) rot=(0,0,1;0rad)
  ResizeMode = 0
  Support = -> [XY_Plane021]
  Width = 129.413
FEATURE [Sketcher::SketchObject] CopySketch014  label="GroundSketch003"
  Placement = pos=(0,0,-28) rot=(0,0,1;0rad)
  sketch-geometry (9):
    g0: LineSegment [constr] StartX=-115 StartY=90 StartZ=0 EndX=115 EndY=90 EndZ=0
    g1: LineSegment [constr] StartX=-115 StartY=-90 StartZ=0 EndX=115 EndY=-90 EndZ=0
    g2: LineSegment [constr] StartX=120 StartY=85 StartZ=0 EndX=120 EndY=-85 EndZ=0
    g3: LineSegment [constr] StartX=-120 StartY=85 StartZ=0 EndX=-120 EndY=-85 EndZ=0
    g4: ArcOfCircle [constr] CenterX=115 CenterY=85 CenterZ=0 NormalX=0 NormalY=0 NormalZ=1 AngleXU=0 Radius=5 StartAngle=-9e-16 EndAngle=1.5708
    g5: ArcOfCircle [constr] CenterX=115 CenterY=-85 CenterZ=0 NormalX=0 NormalY=0 NormalZ=1 AngleXU=0 Radius=5 StartAngle=4.71239 EndAngle=6.28319
    g6: ArcOfCircle [constr] CenterX=-115 CenterY=-85 CenterZ=0 NormalX=0 NormalY=0 NormalZ=1 AngleXU=0 Radius=5 StartAngle=3.14159 EndAngle=4.71239
    g7: ArcOfCircle [constr] CenterX=-115 CenterY=85 CenterZ=0 NormalX=0 NormalY=0 NormalZ=1 AngleXU=0 Radius=5 StartAngle=1.5708 EndAngle=3.14159
    g8: Circle CenterX=110 CenterY=80 CenterZ=0 NormalX=0 NormalY=0 NormalZ=1 AngleXU=0 Radius=8
  constraints (22):
    c: Symmetric(g0,g0,g-2)
    c: Equal(g1,g0)
    c: Symmetric(g1,g1,g-2)
    c: Symmetric(g2,g2,g-1)
    c: Symmetric(g3,g3,g-1)
    c: Equal(g3,g2)
    c: Symmetric(g0,g1,g-1)
    c: Symmetric(g2,g3,g-2)
    c: Coincident(g4,g2)
    c: Tangent(g7,g0) = 1.5708
    c: Tangent(g7,g3) = -1.5708
    c: Tangent(g0,g4) = 1.5708
    c: Coincident(g5,g1)
    c: Tangent(g5,g2) = 1.5708
    c: Coincident(g3,g6)
    c: Tangent(g6,g1) = -1.5708
    c: Distance(g3,g2) = 240
    c: Radius(g4) = 5
    c: Distance(g0,g1) = 180
    c: Diameter(g8) = 16
    c: DistanceY(g8,g0) = 10
    c: DistanceX(g8,g2) = 10
FEATURE [Sketcher::SketchObject] Sketch072
  ExternalGeometry = -> [Pad031]
  MapMode = 5
  Placement = pos=(0,0,-14) rot=(1,0,0;3.14159rad)
  Support = -> [Pad031]
  sketch-geometry (8):
    g0: ArcOfCircle CenterX=105 CenterY=-75 CenterZ=0 NormalX=0 NormalY=0 NormalZ=1 AngleXU=0 Radius=10.5 StartAngle=1.5708 EndAngle=3.14159
    g1: ArcOfCircle CenterX=115 CenterY=-75 CenterZ=0 NormalX=0 NormalY=0 NormalZ=1 AngleXU=0 Radius=10.5 StartAngle=-9e-16 EndAngle=1.5708
    g2: ArcOfCircle CenterX=105 CenterY=-85 CenterZ=0 NormalX=0 NormalY=0 NormalZ=1 AngleXU=0 Radius=10.5 StartAngle=3.14159 EndAngle=4.71239
    g3: ArcOfCircle CenterX=115 CenterY=-85 CenterZ=0 NormalX=0 NormalY=0 NormalZ=1 AngleXU=0 Radius=10.5 StartAngle=4.71239 EndAngle=6.28319
    g4: LineSegment StartX=105 StartY=-64.5 StartZ=0 EndX=115 EndY=-64.5 EndZ=0
    g5: LineSegment StartX=125.5 StartY=-75 StartZ=0 EndX=125.5 EndY=-85 EndZ=0
    g6: LineSegment StartX=115 StartY=-95.5 StartZ=0 EndX=105 EndY=-95.5 EndZ=0
    g7: LineSegment StartX=94.5 StartY=-85 StartZ=0 EndX=94.5 EndY=-75 EndZ=0
  constraints (21):
    c: Horizontal(g4)
    c: Equal(g0,g2)
    c: Equal(g2,g3)
    c: Radius(g1) = 10.5
    c: Horizontal(g1,g0)
    c: Vertical(g2,g0)
    c: Horizontal(g2,g3)
    c: Tangent(g4,g0) = 1.5708
    c: Tangent(g5,g3) = 1.5708
    c: Vertical(g5)
    c: Tangent(g5,g1) = 1.5708
    c: Tangent(g7,g2) = 1.5708
    c: Tangent(g1,g4) = 1.5708
    c: Coincident(g6,g2)
    c: Tangent(g6,g3) = 1.5708
    c: Coincident(g7,g0)
    c: Equal(g6,g7)
    c: Equal(g7,g4)
    c: Equal(g4,g5)
    c: DistanceX(g4,g4) = 10
    c: Coincident(g-3,g1)
FEATURE [PartDesign::Pad] Pad032
  BaseFeature = -> Pad031
  Length = 14
  Length2 = 100
  Profile = -> Sketch072
  Type = 0
FEATURE [PartDesign::Pocket] Pocket042
  BaseFeature = -> Pad032
  Length = 8
  Length2 = 100
  Profile = -> CopySketch014
  Reversed = true
  Type = 0
FEATURE [Sketcher::SketchObject] Sketch073
  ExternalGeometry = -> [Pocket042]
  MapMode = 5
  Placement = pos=(0,0,-28) rot=(1,0,0;3.14159rad)
  Support = -> [Pocket042]
  sketch-geometry (1):
    g0: Circle CenterX=110 CenterY=-80 CenterZ=0 NormalX=0 NormalY=0 NormalZ=1 AngleXU=0 Radius=3.25
  constraints (2):
    c: Diameter(g0) = 6.5
    c: Coincident(g0,g-3)
FEATURE [PartDesign::Pocket] Pocket043
  BaseFeature = -> Pocket042
  Length = 5
  Length2 = 100
  Profile = -> Sketch073
  Type = 1
FEATURE [PartDesign::Chamfer] Chamfer007
  Base = -> Pocket043 [Edge14,Edge51]
  BaseFeature = -> Pocket043
  Size = 3
FEATURE [PartDesign::Body] Body021  label="Short_Foot"
  Group = -> [CopySketch012,Pad031,DatumPlane013,CopySketch014,Sketch072,Pad032,Pocket042,Sketch073,Pocket043,Chamfer007]
  Origin = -> Origin021
  Placement = pos=(0,0,0) rot=(0,0,1;3.14159rad)
  Tip = -> Chamfer007
FEATURE [Part::Mirroring] Part__Mirroring  label="Short_Foot (Mirror #1)"
  Base = (0,0,0)
  Normal = (0,1,0)
  Source = -> Body021
FEATURE [Sketcher::SketchObject] CopySketch015  label="GroundSketch004"
  Placement = pos=(0,0,-28) rot=(0,0,1;0rad)
  sketch-geometry (9):
    g0: LineSegment [constr] StartX=-115 StartY=90 StartZ=0 EndX=115 EndY=90 EndZ=0
    g1: LineSegment [constr] StartX=-115 StartY=-90 StartZ=0 EndX=115 EndY=-90 EndZ=0
    g2: LineSegment [constr] StartX=120 StartY=85 StartZ=0 EndX=120 EndY=-85 EndZ=0
    g3: LineSegment [constr] StartX=-120 StartY=85 StartZ=0 EndX=-120 EndY=-85 EndZ=0
    g4: ArcOfCircle [constr] CenterX=115 CenterY=85 CenterZ=0 NormalX=0 NormalY=0 NormalZ=1 AngleXU=0 Radius=5 StartAngle=-9e-16 EndAngle=1.5708
    g5: ArcOfCircle [constr] CenterX=115 CenterY=-85 CenterZ=0 NormalX=0 NormalY=0 NormalZ=1 AngleXU=0 Radius=5 StartAngle=4.71239 EndAngle=6.28319
    g6: ArcOfCircle [constr] CenterX=-115 CenterY=-85 CenterZ=0 NormalX=0 NormalY=0 NormalZ=1 AngleXU=0 Radius=5 StartAngle=3.14159 EndAngle=4.71239
    g7: ArcOfCircle [constr] CenterX=-115 CenterY=85 CenterZ=0 NormalX=0 NormalY=0 NormalZ=1 AngleXU=0 Radius=5 StartAngle=1.5708 EndAngle=3.14159
    g8: Circle CenterX=110 CenterY=80 CenterZ=0 NormalX=0 NormalY=0 NormalZ=1 AngleXU=0 Radius=8
  constraints (22):
    c: Symmetric(g0,g0,g-2)
    c: Equal(g1,g0)
    c: Symmetric(g1,g1,g-2)
    c: Symmetric(g2,g2,g-1)
    c: Symmetric(g3,g3,g-1)
    c: Equal(g3,g2)
    c: Symmetric(g0,g1,g-1)
    c: Symmetric(g2,g3,g-2)
    c: Coincident(g4,g2)
    c: Tangent(g7,g0) = 1.5708
    c: Tangent(g7,g3) = -1.5708
    c: Tangent(g0,g4) = 1.5708
    c: Coincident(g5,g1)
    c: Tangent(g5,g2) = 1.5708
    c: Coincident(g3,g6)
    c: Tangent(g6,g1) = -1.5708
    c: Distance(g3,g2) = 240
    c: Radius(g4) = 5
    c: Distance(g0,g1) = 180
    c: Diameter(g8) = 16
    c: DistanceY(g8,g0) = 10
    c: DistanceX(g8,g2) = 10
FEATURE [PartDesign::Plane] DatumPlane014
  AttachmentOffset = pos=(0,0,-28) rot=(0,0,1;0rad)
  Length = 159.413
  MapMode = 5
  Placement = pos=(0,0,-28) rot=(0,0,1;0rad)
  ResizeMode = 0
  Support = -> [XY_Plane022]
  Width = 129.413
FEATURE [Sketcher::SketchObject] CopySketch016  label="SketchGround002"
  MapMode = 2
  Support = -> [XY_Plane022]
  sketch-geometry (26):
    g0: LineSegment [constr] StartX=-115 StartY=90 StartZ=0 EndX=115 EndY=90 EndZ=0
    g1: LineSegment [constr] StartX=-115 StartY=-90 StartZ=0 EndX=115 EndY=-90 EndZ=0
    g2: LineSegment [constr] StartX=120 StartY=85 StartZ=0 EndX=120 EndY=-85 EndZ=0
    g3: LineSegment [constr] StartX=-120 StartY=85 StartZ=0 EndX=-120 EndY=-85 EndZ=0
    g4: ArcOfCircle [constr] CenterX=115 CenterY=85 CenterZ=0 NormalX=0 NormalY=0 NormalZ=1 AngleXU=0 Radius=5 StartAngle=1.2e-15 EndAngle=1.5708
    g5: ArcOfCircle [constr] CenterX=115 CenterY=-85 CenterZ=0 NormalX=0 NormalY=0 NormalZ=1 AngleXU=0 Radius=5 StartAngle=4.71239 EndAngle=6.28319
    g6: ArcOfCircle [constr] CenterX=-115 CenterY=-85 CenterZ=0 NormalX=0 NormalY=0 NormalZ=1 AngleXU=0 Radius=5 StartAngle=3.14159 EndAngle=4.71239
    g7: ArcOfCircle [constr] CenterX=-115 CenterY=85 CenterZ=0 NormalX=0 NormalY=0 NormalZ=1 AngleXU=0 Radius=5 StartAngle=1.5708 EndAngle=3.14159
    g8: Circle [constr] CenterX=110 CenterY=80 CenterZ=0 NormalX=0 NormalY=0 NormalZ=1 AngleXU=0 Radius=3.25
    g9: Circle [constr] CenterX=-110 CenterY=80 CenterZ=0 NormalX=0 NormalY=0 NormalZ=1 AngleXU=0 Radius=3.25
    g10: Circle [constr] CenterX=110 CenterY=-80 CenterZ=0 NormalX=0 NormalY=0 NormalZ=1 AngleXU=0 Radius=3.25
    g11: Circle [constr] CenterX=-110 CenterY=-80 CenterZ=0 NormalX=0 NormalY=0 NormalZ=1 AngleXU=0 Radius=3.25
    g12: Circle [constr] CenterX=110 CenterY=0 CenterZ=0 NormalX=0 NormalY=0 NormalZ=1 AngleXU=0 Radius=3.25
    g13: Circle [constr] CenterX=-110 CenterY=0 CenterZ=0 NormalX=0 NormalY=0 NormalZ=1 AngleXU=0 Radius=3.25
    g14: Circle [constr] CenterX=0 CenterY=70 CenterZ=0 NormalX=0 NormalY=0 NormalZ=1 AngleXU=0 Radius=3.25
    g15: Circle [constr] CenterX=0 CenterY=-70 CenterZ=0 NormalX=0 NormalY=0 NormalZ=1 AngleXU=0 Radius=3.25
    g16: ArcOfCircle CenterX=115 CenterY=85 CenterZ=0 NormalX=0 NormalY=0 NormalZ=1 AngleXU=0 Radius=5.5 StartAngle=0 EndAngle=1.5708
    g17: LineSegment StartX=115 StartY=90.5 StartZ=0 EndX=105 EndY=90.5 EndZ=0
    g18: LineSegment StartX=105 StartY=95.5 StartZ=0 EndX=115 EndY=95.5 EndZ=0
    g19: ArcOfCircle CenterX=115 CenterY=85 CenterZ=0 NormalX=0 NormalY=0 NormalZ=1 AngleXU=0 Radius=10.5 StartAngle=0 EndAngle=1.5708
    g20: LineSegment StartX=120.5 StartY=85 StartZ=0 EndX=120.5 EndY=75 EndZ=0
    g21: LineSegment StartX=125.5 StartY=75 StartZ=0 EndX=125.5 EndY=85 EndZ=0
    g22: LineSegment StartX=120.5 StartY=75 StartZ=0 EndX=120.5 EndY=66.0557 EndZ=0
    g23: ArcOfCircle CenterX=115 CenterY=75 CenterZ=0 NormalX=0 NormalY=0 NormalZ=1 AngleXU=0 Radius=10.5 StartAngle=5.26371 EndAngle=6.28319
    g24: ArcOfCircle CenterX=105 CenterY=85 CenterZ=0 NormalX=0 NormalY=0 NormalZ=1 AngleXU=0 Radius=10.5 StartAngle=1.5708 EndAngle=2.59028
    g25: LineSegment StartX=96.0557 StartY=90.5 StartZ=0 EndX=105 EndY=90.5 EndZ=0
  constraints (69):
    c: Symmetric(g0,g0,g-2)
    c: Equal(g1,g0)
    c: Symmetric(g1,g1,g-2)
    c: Symmetric(g2,g2,g-1)
    c: Symmetric(g3,g3,g-1)
    c: Equal(g3,g2)
    c: Symmetric(g0,g1,g-1)
    c: Symmetric(g2,g3,g-2)
    c: Coincident(g4,g2)
    c: Tangent(g7,g0) = 1.5708
    c: Tangent(g7,g3) = -1.5708
    c: Tangent(g0,g4) = 1.5708
    c: Coincident(g5,g1)
    c: Tangent(g5,g2) = 1.5708
    c: Coincident(g3,g6)
    c: Tangent(g6,g1) = -1.5708
    c: Distance(g3,g2) = 240
    c: Radius(g4) = 5
    c: Distance(g0,g1) = 180
    c: Diameter(g8) = 6.5
    c: DistanceY(g8,g0) = 10
    c: DistanceX(g8,g2) = 10
    c: Equal(g9,g8)
    c: Symmetric(g9,g8,g-2)
    c: Equal(g11,g10)
    c: Equal(g10,g8)
    c: Symmetric(g10,g8,g-1)
    c: Symmetric(g11,g10,g-2)
    c: PointOnObject(g12,g-1)
    c: PointOnObject(g13,g-1)
    c: Equal(g13,g12)
    c: Equal(g12,g8)
    c: Vertical(g12,g8)
    c: Vertical(g13,g9)
    c: Equal(g15,g14)
    c: Equal(g14,g8)
    c: PointOnObject(g15,g-2)
    c: Symmetric(g15,g14,g-1)
    c: DistanceY(g14,g0) = 20
    c: Radius(g16) = 5.5
    c: Coincident(g16,g4)
    c: Horizontal(g16,g16)
    c: Vertical(g16,g16)
    c: Horizontal(g17)
    c: DistanceX(g17,g17) = 10
    c: Coincident(g17,g16)
    c: DistanceY(g16,g18) = 5
    c: Vertical(g16,g18)
    c: Horizontal(g18)
    c: Horizontal(g19,g16)
    c: Coincident(g18,g19)
    c: Coincident(g4,g19)
    c: Vertical(g20)
    c: Coincident(g20,g16)
    c: Vertical(g21)
    c: Coincident(g21,g19)
    c: Vertical(g17,g18)
    c: Horizontal(g24,g17)
    c: Equal(g18,g21)
    c: Vertical(g22)
    c: Coincident(g23,g22)
    c: Coincident(g22,g20)
    c: Tangent(g24,g18) = 1.5708
    c: Tangent(g23,g21) = -1.5708
    c: Horizontal(g20,g21)
    c: Equal(g23,g19)
    c: Coincident(g24,g25)
    c: Equal(g24,g19)
    c: Coincident(g25,g17)
FEATURE [PartDesign::Pad] Pad033
  Length = 14
  Length2 = 100
  Profile = -> CopySketch016
  Reversed = true
  Type = 0
FEATURE [Sketcher::SketchObject] Sketch074
  ExternalGeometry = -> [Pad033]
  MapMode = 5
  Placement = pos=(0,0,-14) rot=(1,0,0;3.14159rad)
  Support = -> [Pad033]
  sketch-geometry (8):
    g0: ArcOfCircle CenterX=105 CenterY=-75 CenterZ=0 NormalX=0 NormalY=0 NormalZ=1 AngleXU=0 Radius=10.5 StartAngle=1.5708 EndAngle=3.14159
    g1: ArcOfCircle CenterX=115 CenterY=-75 CenterZ=0 NormalX=0 NormalY=0 NormalZ=1 AngleXU=0 Radius=10.5 StartAngle=-9e-16 EndAngle=1.5708
    g2: ArcOfCircle CenterX=105 CenterY=-85 CenterZ=0 NormalX=0 NormalY=0 NormalZ=1 AngleXU=0 Radius=10.5 StartAngle=3.14159 EndAngle=4.71239
    g3: ArcOfCircle CenterX=115 CenterY=-85 CenterZ=0 NormalX=0 NormalY=0 NormalZ=1 AngleXU=0 Radius=10.5 StartAngle=4.71239 EndAngle=6.28319
    g4: LineSegment StartX=105 StartY=-64.5 StartZ=0 EndX=115 EndY=-64.5 EndZ=0
    g5: LineSegment StartX=125.5 StartY=-75 StartZ=0 EndX=125.5 EndY=-85 EndZ=0
    g6: LineSegment StartX=115 StartY=-95.5 StartZ=0 EndX=105 EndY=-95.5 EndZ=0
    g7: LineSegment StartX=94.5 StartY=-85 StartZ=0 EndX=94.5 EndY=-75 EndZ=0
  constraints (21):
    c: Horizontal(g4)
    c: Equal(g0,g2)
    c: Equal(g2,g3)
    c: Radius(g1) = 10.5
    c: Horizontal(g1,g0)
    c: Vertical(g2,g0)
    c: Horizontal(g2,g3)
    c: Tangent(g4,g0) = 1.5708
    c: Tangent(g5,g3) = 1.5708
    c: Vertical(g5)
    c: Tangent(g5,g1) = 1.5708
    c: Tangent(g7,g2) = 1.5708
    c: Tangent(g1,g4) = 1.5708
    c: Coincident(g6,g2)
    c: Tangent(g6,g3) = 1.5708
    c: Coincident(g7,g0)
    c: Equal(g6,g7)
    c: Equal(g7,g4)
    c: Equal(g4,g5)
    c: DistanceX(g4,g4) = 10
    c: Coincident(g-3,g1)
FEATURE [PartDesign::Pad] Pad034
  BaseFeature = -> Pad033
  Length = 14
  Length2 = 100
  Profile = -> Sketch074
  Type = 0
FEATURE [PartDesign::Pocket] Pocket045
  BaseFeature = -> Pad034
  Length = 8
  Length2 = 100
  Profile = -> CopySketch015
  Reversed = true
  Type = 0
FEATURE [Sketcher::SketchObject] Sketch075
  ExternalGeometry = -> [Pocket045]
  MapMode = 5
  Placement = pos=(0,0,-28) rot=(1,0,0;3.14159rad)
  Support = -> [Pocket045]
  sketch-geometry (1):
    g0: Circle CenterX=110 CenterY=-80 CenterZ=0 NormalX=0 NormalY=0 NormalZ=1 AngleXU=0 Radius=3.25
  constraints (2):
    c: Diameter(g0) = 6.5
    c: Coincident(g0,g-3)
FEATURE [PartDesign::Pocket] Pocket044
  BaseFeature = -> Pocket045
  Length = 5
  Length2 = 100
  Profile = -> Sketch075
  Type = 1
FEATURE [PartDesign::Chamfer] Chamfer008
  Base = -> Pocket044 [Edge14,Edge51]
  BaseFeature = -> Pocket044
  Size = 3
FEATURE [Sketcher::SketchObject] Sketch076
  ExternalGeometry = -> [Chamfer008]
  MapMode = 5
  Support = -> [Chamfer008]
  sketch-geometry (4):
    g0: LineSegment StartX=115 StartY=90.5 StartZ=0 EndX=135 EndY=90.5 EndZ=0
    g1: LineSegment StartX=135 StartY=90.5 StartZ=0 EndX=135 EndY=60.5 EndZ=0
    g2: LineSegment StartX=135 StartY=60.5 StartZ=0 EndX=115 EndY=60.5 EndZ=0
    g3: LineSegment StartX=115 StartY=60.5 StartZ=0 EndX=115 EndY=90.5 EndZ=0
  constraints (11):
    c: Coincident(g0,g1)
    c: Coincident(g1,g2)
    c: Coincident(g2,g3)
    c: Coincident(g3,g0)
    c: Horizontal(g0)
    c: Horizontal(g2)
    c: Vertical(g1)
    c: Vertical(g3)
    c: Coincident(g0,g-3)
    c: DistanceX(g2,g2) = 20
    c: DistanceY(g1,g1) = 30
FEATURE [PartDesign::Pocket] Pocket046
  BaseFeature = -> Chamfer008
  Length = 14
  Length2 = 100
  Profile = -> Sketch076
  Type = 0
FEATURE [PartDesign::Body] Body022  label="Short_FooMiddle"
  Group = -> [CopySketch016,Pad033,DatumPlane014,CopySketch015,Sketch074,Pad034,Pocket045,Sketch075,Pocket044,Chamfer008,Sketch076,Pocket046]
  Origin = -> Origin022
  Placement = pos=(-30,-110,0) rot=(0,0,1;1.5708rad)
  Tip = -> Pocket046
FEATURE [Part::Feature] MukkeBox272
  Placement = pos=(120.066,-133.584,1.65) rot=(0,0,-1;1.5708rad)
  shape: bbox 0.8 x 1.6 x 0.8 mm, 28 faces (baked)
FEATURE [Part::Feature] MukkeBox273
  Placement = pos=(102.066,-138.884,1.65) rot=(0,0,-1;1.5708rad)
  shape: bbox 0.8 x 1.6 x 0.8 mm, 28 faces (baked)
FEATURE [Part::Feature] MukkeBox274
  Placement = pos=(82.466,-122.984,1.65) rot=(0,0,1;1.5708rad)
  shape: bbox 0.8 x 1.6 x 0.8 mm, 28 faces (baked)
FEATURE [Part::Feature] MukkeBox275
  Placement = pos=(66.566,-109.034,1.65) rot=(0,0,-1;1.5708rad)
  shape: bbox 0.8 x 1.6 x 0.8 mm, 28 faces (baked)
FEATURE [Part::Feature] MukkeBox276
  Placement = pos=(66.591,-115.784,1.65) rot=(0,0,1;1.5708rad)
  shape: bbox 0.8 x 1.6 x 0.8 mm, 28 faces (baked)
FEATURE [Part::Feature] MukkeBox277
  Placement = pos=(80.966,-106.384,1.65) rot=(0,0,1;1.5708rad)
  shape: bbox 0.8 x 1.6 x 0.8 mm, 28 faces (baked)
FEATURE [Part::Feature] MukkeBox278
  Placement = pos=(75.766,-109.584,1.65) rot=(0,0,1;3.14159rad)
  shape: bbox 1.6 x 0.8 x 0.8 mm, 28 faces (baked)
FEATURE [Part::Feature] MukkeBox279
  Placement = pos=(75.666,-116.484,1.65) rot=(0,0,1;3.14159rad)
  shape: bbox 1.6 x 0.8 x 0.8 mm, 28 faces (baked)
FEATURE [Part::Feature] MukkeBox280
  Placement = pos=(86.166,-122.984,1.65) rot=(0,0,-1;1.5708rad)
  shape: bbox 0.8 x 1.6 x 0.8 mm, 28 faces (baked)
FEATURE [Part::Feature] MukkeBox281
  Placement = pos=(66.566,-124.684,1.65) rot=(0,0,-1;1.5708rad)
  shape: bbox 0.8 x 1.6 x 0.8 mm, 28 faces (baked)
FEATURE [Part::Feature] MukkeBox282
  Placement = pos=(74.066,-124.584,1.65) rot=(0,0,1;1.5708rad)
  shape: bbox 0.8 x 1.6 x 0.8 mm, 28 faces (baked)
FEATURE [Part::Feature] MukkeBox283
  Placement = pos=(73.566,-138.584,1.65) rot=(0,0,-1;1.5708rad)
  shape: bbox 0.8 x 1.6 x 0.8 mm, 28 faces (baked)
FEATURE [Part::Feature] MukkeBox284
  Placement = pos=(65.666,-138.484,1.65) rot=(0,0,-1;1.5708rad)
  shape: bbox 0.8 x 1.6 x 0.8 mm, 28 faces (baked)
FEATURE [Part::Feature] MukkeBox285
  Placement = pos=(140.716,-65.384,1.65) rot=(0,0,1;1.5708rad)
  shape: bbox 0.8 x 1.6 x 0.8 mm, 28 faces (baked)
FEATURE [Part::Feature] MukkeBox286
  Placement = pos=(74.416,-88.284,1.65) rot=(0,0,-1;1.5708rad)
  shape: bbox 0.8 x 1.6 x 0.8 mm, 28 faces (baked)
FEATURE [Part::Feature] MukkeBox287
  Placement = pos=(83.216,-59.634,1.65) rot=(0,0,1;3.14159rad)
  shape: bbox 1.6 x 0.8 x 0.8 mm, 28 faces (baked)
FEATURE [Part::Feature] MukkeBox288
  Placement = pos=(82.716,-48.884,1.65) rot=(0,0,1;0.785398rad)
  shape: bbox 1.697 x 1.697 x 0.8 mm, 28 faces (baked)
FEATURE [Part::Feature] MukkeBox289
  Placement = pos=(83.616,-52.284,1.65) rot=(0,0,1;0rad)
  shape: bbox 1.6 x 0.8 x 0.8 mm, 28 faces (baked)
FEATURE [Part::Feature] MukkeBox290
  Placement = pos=(80.416,-47.884,1.65) rot=(0,0,-1;1.5708rad)
  shape: bbox 0.8 x 1.6 x 0.8 mm, 28 faces (baked)
FEATURE [Part::Feature] MukkeBox291
  Placement = pos=(70.666,-49.184,1.65) rot=(0,0,1;0rad)
  shape: bbox 1.6 x 0.8 x 0.8 mm, 28 faces (baked)
FEATURE [Part::Feature] MukkeBox292
  Placement = pos=(75.666,-48.884,1.65) rot=(0,0,1;3.14159rad)
  shape: bbox 1.6 x 0.8 x 0.8 mm, 28 faces (baked)
FEATURE [Part::Feature] MukkeBox293
  Placement = pos=(70.691,-56.484,1.65) rot=(0,0,1;3.14159rad)
  shape: bbox 1.6 x 0.8 x 0.8 mm, 28 faces (baked)
FEATURE [Part::Feature] MukkeBox294
  Placement = pos=(70.616,-51.584,1.65) rot=(0,0,1;3.14159rad)
  shape: bbox 1.6 x 0.8 x 0.8 mm, 28 faces (baked)
FEATURE [Part::Feature] MukkeBox295
  Placement = pos=(70.666,-54.909,1.65) rot=(0,0,1;3.14159rad)
  shape: bbox 1.6 x 0.8 x 0.8 mm, 28 faces (baked)
FEATURE [Part::Feature] MukkeBox296
  Placement = pos=(68.116,-52.509,1.65) rot=(0,0,1;1.5708rad)
  shape: bbox 0.8 x 1.6 x 0.8 mm, 28 faces (baked)
FEATURE [Part::Feature] MukkeBox297
  Placement = pos=(86.666,-64.584,1.65) rot=(0,0,1;3.14159rad)
  shape: bbox 7.785 x 8.053 x 8.3 mm, 46 faces (baked)
FEATURE [Part::Feature] MukkeBox298
  Placement = pos=(80.391,-40.859,1.65) rot=(0,0,-1;1.5708rad)
  shape: bbox 6.515 x 6.128 x 7 mm, 49 faces (baked)
FEATURE [Part::Feature] MukkeBox299
  Placement = pos=(207.691,-99.909,1.65) rot=(0,0,1;1.5708rad)
  shape: bbox 0.8 x 1.6 x 0.8 mm, 28 faces (baked)
FEATURE [Part::Feature] MukkeBox300
  Placement = pos=(201.666,-99.909,1.65) rot=(0,0,-1;1.5708rad)
  shape: bbox 0.8 x 1.6 x 0.8 mm, 28 faces (baked)
FEATURE [Part::Feature] MukkeBox301
  Placement = pos=(241,-108,1.65) rot=(0,0,1;3.14159rad)
  shape: bbox 4.924 x 5.212 x 6 mm, 54 faces (baked)
FEATURE [Part::Feature] MukkeBox302
  Placement = pos=(209.216,-88.034,1.65) rot=(0,0,-1;1.5708rad)
  shape: bbox 0.8 x 1.6 x 0.8 mm, 28 faces (baked)
FEATURE [Part::Feature] MukkeBox303
  Placement = pos=(234,-108,1.65) rot=(0,0,1;0rad)
  shape: bbox 4.924 x 5.212 x 6 mm, 54 faces (baked)
FEATURE [Part::Feature] MukkeBox304
  Placement = pos=(240.366,-126.684,1.65) rot=(0,0,1;1.5708rad)
  shape: bbox 6.515 x 6.128 x 7 mm, 49 faces (baked)
FEATURE [Part::Feature] MukkeBox305
  Placement = pos=(226.291,-112.984,1.65) rot=(0,0,1;1.5708rad)
  shape: bbox 2.5 x 7 x 11.9 mm, 22 faces (baked)
FEATURE [Part::Feature] MukkeBox306
  Placement = pos=(225.766,-134.284,1.65) rot=(0,0,-1;1.5708rad)
  shape: bbox 6.515 x 6.128 x 7 mm, 49 faces (baked)
FEATURE [Part::Feature] MukkeBox307
  Placement = pos=(193.966,-96.034,1.65) rot=(0,0,1;0rad)
  shape: bbox 1.6 x 0.8 x 0.8 mm, 28 faces (baked)
FEATURE [Part::Feature] MukkeBox308
  Placement = pos=(194.491,-77.109,1.65) rot=(0,0,1;0rad)
  shape: bbox 1.6 x 0.8 x 0.8 mm, 28 faces (baked)
FEATURE [Part::Feature] MukkeBox309
  Placement = pos=(205.791,-77.209,1.65) rot=(0,0,1;0rad)
  shape: bbox 1.6 x 0.8 x 0.8 mm, 28 faces (baked)
FEATURE [Part::Feature] MukkeBox310
  Placement = pos=(194.491,-75.609,1.65) rot=(0,0,1;0rad)
  shape: bbox 1.6 x 0.8 x 0.8 mm, 28 faces (baked)
FEATURE [Part::Feature] MukkeBox311
  Placement = pos=(205.816,-75.709,1.65) rot=(0,0,1;0rad)
  shape: bbox 1.6 x 0.8 x 0.8 mm, 28 faces (baked)
FEATURE [Part::Feature] MukkeBox312
  Placement = pos=(219.9,-66,1.65) rot=(0,0,1;3.14159rad)
  shape: bbox 7 x 2.5 x 11.9 mm, 22 faces (baked)
FEATURE [Part::Feature] MukkeBox313
  Placement = pos=(179.9,-66,1.65) rot=(0,0,1;0rad)
  shape: bbox 7 x 2.5 x 11.9 mm, 22 faces (baked)
FEATURE [Part::Feature] MukkeBox314
  Placement = pos=(223.9,-61,1.65) rot=(0,0,1;3.14159rad)
  shape: bbox 7 x 2.5 x 11.9 mm, 22 faces (baked)
FEATURE [Part::Feature] MukkeBox315
  Placement = pos=(176.4,-61,1.65) rot=(0,0,1;0rad)
  shape: bbox 7 x 2.5 x 11.9 mm, 22 faces (baked)
FEATURE [Part::Feature] MukkeBox316
  Placement = pos=(228.9,-55,1.65) rot=(0,0,1;3.14159rad)
  shape: bbox 7 x 2.5 x 11.9 mm, 22 faces (baked)
FEATURE [Part::Feature] MukkeBox317
  Placement = pos=(219.9,-55,1.65) rot=(0,0,1;3.14159rad)
  shape: bbox 7 x 2.5 x 11.9 mm, 22 faces (baked)
FEATURE [Part::Feature] MukkeBox318
  Placement = pos=(171.9,-55,1.65) rot=(0,0,1;0rad)
  shape: bbox 7 x 2.5 x 11.9 mm, 22 faces (baked)
FEATURE [Part::Feature] MukkeBox319
  Placement = pos=(180.9,-55,1.65) rot=(0,0,1;0rad)
  shape: bbox 7 x 2.5 x 11.9 mm, 22 faces (baked)
FEATURE [Part::Feature] MukkeBox320
  Placement = pos=(235,-77.95,1.65) rot=(0,0,1;0rad)
  shape: bbox 16.06 x 16.62 x 15 mm, 51 faces (baked)
FEATURE [Part::Feature] MukkeBox321
  Placement = pos=(228.9,-51,1.65) rot=(0,0,1;3.14159rad)
  shape: bbox 7 x 2.5 x 11.9 mm, 22 faces (baked)
FEATURE [Part::Feature] MukkeBox322
  Placement = pos=(219.9,-51,1.65) rot=(0,0,1;3.14159rad)
  shape: bbox 7 x 2.5 x 11.9 mm, 22 faces (baked)
FEATURE [Part::Feature] MukkeBox323
  Placement = pos=(171.9,-51,1.65) rot=(0,0,1;0rad)
  shape: bbox 7 x 2.5 x 11.9 mm, 22 faces (baked)
FEATURE [Part::Feature] MukkeBox324
  Placement = pos=(180.9,-51,1.65) rot=(0,0,1;0rad)
  shape: bbox 7 x 2.5 x 11.9 mm, 22 faces (baked)
FEATURE [Part::Feature] MukkeBox325
  Placement = pos=(165,-77.95,1.65) rot=(0,0,1;3.14159rad)
  shape: bbox 15.45 x 15.98 x 14.5 mm, 53 faces (baked)
FEATURE [Part::Feature] MukkeBox326
  Placement = pos=(235,-97.95,1.65) rot=(0,0,1;0rad)
  shape: bbox 15.45 x 15.98 x 14.5 mm, 53 faces (baked)
FEATURE [Part::Feature] MukkeBox327
  Placement = pos=(165,-97.95,1.65) rot=(0,0,1;3.14159rad)
  shape: bbox 15.45 x 15.98 x 14.5 mm, 53 faces (baked)
FEATURE [Part::Feature] MukkeBox328
  Placement = pos=(191.116,-107.934,1.65) rot=(0,0,-1;1.5708rad)
  shape: bbox 2.5 x 7 x 11.9 mm, 22 faces (baked)
FEATURE [Part::Feature] MukkeBox329
  Placement = pos=(151.766,-132.884,1.65) rot=(0,0,-1;1.5708rad)
  shape: bbox 0.8 x 1.6 x 0.8 mm, 28 faces (baked)
FEATURE [Part::Feature] MukkeBox330
  Placement = pos=(146.166,-131.484,1.65) rot=(0,0,1;1.5708rad)
  shape: bbox 6.515 x 6.128 x 7 mm, 49 faces (baked)
FEATURE [Part::Feature] MukkeBox331
  Placement = pos=(212.422,-128.684,1.65) rot=(0,0,1;1.5708rad)
  shape: bbox 0.8 x 1.6 x 0.8 mm, 28 faces (baked)
FEATURE [Part::Feature] MukkeBox332
  Placement = pos=(214.066,-128.684,1.65) rot=(0,0,1;1.5708rad)
  shape: bbox 0.8 x 1.6 x 0.8 mm, 28 faces (baked)
FEATURE [Part::Feature] MukkeBox333
  Placement = pos=(57.4776,-86.7357,1.65) rot=(0,0,1;0rad)
  shape: bbox 7.785 x 8.053 x 8.3 mm, 46 faces (baked)
FEATURE [Part::Feature] MukkeBox334
  Placement = pos=(210.766,-128.684,1.65) rot=(0,0,1;1.5708rad)
  shape: bbox 0.8 x 1.6 x 0.8 mm, 28 faces (baked)
FEATURE [Part::Feature] MukkeBox335
  Placement = pos=(146.741,-62.259,1.65) rot=(0,0,-1;1.5708rad)
  shape: bbox 8.053 x 7.785 x 8.3 mm, 46 faces (baked)
FEATURE [Part::Feature] MukkeBox336
  Placement = pos=(130.266,-62.184,1.65) rot=(0,0,1;3.14159rad)
  shape: bbox 1.6 x 0.8 x 0.8 mm, 28 faces (baked)
FEATURE [Part::Feature] MukkeBox337
  Placement = pos=(142.291,-65.384,1.65) rot=(0,0,1;1.5708rad)
  shape: bbox 0.8 x 1.6 x 0.8 mm, 28 faces (baked)
FEATURE [Part::Feature] MukkeBox338
  Placement = pos=(137.541,-67.984,1.65) rot=(0,0,1;0rad)
  shape: bbox 1.6 x 0.8 x 0.8 mm, 28 faces (baked)
FEATURE [Part::Feature] MukkeBox339
  Placement = pos=(119,-67.709,1.65) rot=(0,0,1;3.14159rad)
  shape: bbox 15.45 x 15.98 x 14.5 mm, 53 faces (baked)
FEATURE [Part::Feature] MukkeBox340
  Placement = pos=(119,-54.284,1.65) rot=(0,0,1;3.14159rad)
  shape: bbox 15.45 x 15.98 x 14.5 mm, 53 faces (baked)
FEATURE [Part::Feature] MukkeBox341
  Placement = pos=(142.566,-110.034,1.65) rot=(0,0,-1;1.5708rad)
  shape: bbox 15.98 x 15.45 x 14.5 mm, 53 faces (baked)
FEATURE [Part::Feature] MukkeBox342
  Placement = pos=(128.916,-110.034,1.65) rot=(0,0,-1;1.5708rad)
  shape: bbox 15.98 x 15.45 x 14.5 mm, 53 faces (baked)
FEATURE [Part::Feature] MukkeBox343
  Placement = pos=(98.066,-121.384,1.65) rot=(0,0,1;3.14159rad)
  shape: bbox 3.4 x 3.8 x 10.8 mm, 16 faces (baked)
FEATURE [Part::Feature] MukkeBox344
  Placement = pos=(62.466,-42.384,1.65) rot=(0,0,1;0rad)
  shape: bbox 9.9 x 6.5 x 2.32 mm, 80 faces (baked)
FEATURE [Part::Feature] MukkeBox345
  Placement = pos=(97.366,-47.084,1.65) rot=(0,0,-1;1.5708rad)
  shape: bbox 6.5 x 9.9 x 2.32 mm, 80 faces (baked)
FEATURE [Part::Feature] MukkeBox346
  Placement = pos=(135.416,-94.934,1.65) rot=(0,0,-1;1.5708rad)
  shape: bbox 6.5 x 9.9 x 2.32 mm, 80 faces (baked)
FEATURE [Part::Feature] MukkeBox347
  Placement = pos=(135.425,-97.3,1.65) rot=(0,0,1;3.14159rad)
  shape: bbox 26.16 x 12.71 x 10.38 mm, 120 faces (baked)
FEATURE [Part::Feature] MukkeBox348
  Placement = pos=(135.416,-82.759,1.65) rot=(0,0,1;3.14159rad)
  shape: bbox 26.16 x 12.71 x 10.38 mm, 120 faces (baked)
FEATURE [Part::Feature] MukkeBox349
  Placement = pos=(171,-106.45,6.15) rot=(0,0,1;0rad)
  shape: bbox 57.91 x 36.82 x 21.1 mm, 60 faces (baked)
FEATURE [Part::Feature] MukkeBox350
  Placement = pos=(63.916,-134.584,1.65) rot=(0,0,1;1.5708rad)
  shape: bbox 50.8 x 5.08 x 11.54 mm, 844 faces (baked)
FEATURE [Part::Feature] MukkeBox351
  Placement = pos=(116.911,-126.959,1.65) rot=(0,0,1;0rad)
  shape: bbox 2.54 x 10.16 x 11.54 mm, 100 faces (baked)
FEATURE [Part::Feature] MukkeBox352
  Placement = pos=(49.166,-120.384,1.65) rot=(0,0,1;0rad)
  shape: bbox 5.08 x 12.7 x 11.54 mm, 214 faces (baked)
FEATURE [Part::Feature] MukkeBox353
  Placement = pos=(112.166,-125.084,1.65) rot=(0,0,-1;1.5708rad)
  shape: bbox 12.7 x 5.08 x 11.54 mm, 214 faces (baked)
FEATURE [Part::Feature] MukkeBox354
  Placement = pos=(144.566,-52.184,1.65) rot=(0,0,1;0rad)
  shape: bbox 2.54 x 5.08 x 11.54 mm, 52 faces (baked)
FEATURE [Part::Feature] MukkeBox355
  Placement = pos=(131.691,-42.859,1.65) rot=(0,0,-1;1.5708rad)
  shape: bbox 10.16 x 5.08 x 11.54 mm, 172 faces (baked)
FEATURE [Part::Feature] MukkeBox356
  Placement = pos=(160.051,-110.859,1.65) rot=(0,0,1;1.5708rad)
  shape: bbox 10.16 x 5.08 x 11.54 mm, 172 faces (baked)
FEATURE [Part::Feature] MukkeBox357
  Placement = pos=(225.766,-130.384,1.65) rot=(0,0,-1;1.5708rad)
  shape: bbox 5.08 x 2.54 x 11.54 mm, 52 faces (baked)
FEATURE [Part::Feature] MukkeBox358
  Placement = pos=(197.116,-119.584,1.65) rot=(0,0,1;1.5708rad)
  shape: bbox 15.24 x 5.08 x 11.54 mm, 256 faces (baked)
FEATURE [Part::Feature] MukkeBox359
  Placement = pos=(48.866,-109.984,1.65) rot=(0,0,1;0rad)
  shape: bbox 2.54 x 5.08 x 11.54 mm, 52 faces (baked)
FEATURE [Part::Feature] MukkeBox360
  Placement = pos=(66.366,-83.484,1.65) rot=(0,0,-1;1.5708rad)
  shape: bbox 5.08 x 2.54 x 11.54 mm, 52 faces (baked)
FEATURE [Part::Feature] MukkeBox361
  Placement = pos=(103.566,-89.709,1.65) rot=(0.707107,0,0.707107;3.14159rad)
  shape: bbox 19.5 x 26.8 x 1.2 mm, 70 faces (baked)
FEATURE [Part::Feature] MukkeBox362
  Placement = pos=(103.566,-89.709,1.65) rot=(0.707107,0,0.707107;3.14159rad)
  shape: bbox 4.1 x 5 x 1.1 mm, 30 faces (baked)
FEATURE [Part::Feature] MukkeBox363
  Placement = pos=(103.566,-89.709,1.65) rot=(0.707107,0,0.707107;3.14159rad)
  shape: bbox 19 x 26.5 x 8.5 mm, 68 faces (baked)
FEATURE [Part::Feature] MukkeBox364
  Placement = pos=(103.566,-89.709,1.65) rot=(0.707107,0,0.707107;3.14159rad)
  shape: bbox 27.72 x 22.13 x 13.2 mm, 52 faces (baked)
FEATURE [Part::Feature] MukkeBox365
  Placement = pos=(103.566,-89.709,1.65) rot=(0.707107,0,0.707107;3.14159rad)
  shape: bbox 19 x 26.5 x 8.5 mm, 68 faces (baked)
FEATURE [Part::Feature] MukkeBox366
  Placement = pos=(98.266,-59.234,1.65) rot=(0,0,1;3.14159rad)
  shape: bbox 12.99 x 12.99 x 24.1 mm, 9 faces (baked)
FEATURE [Part::Feature] MukkeBox367
  Placement = pos=(234.9,-65,1.65) rot=(0,0,1;1.5708rad)
  shape: bbox 12.99 x 12.99 x 24.1 mm, 9 faces (baked)
FEATURE [Part::Feature] MukkeBox368
  Placement = pos=(206.9,-65,1.65) rot=(0,0,1;1.5708rad)
  shape: bbox 12.99 x 12.99 x 24.1 mm, 9 faces (baked)
FEATURE [Part::Feature] MukkeBox369
  Placement = pos=(165.406,-65,1.65) rot=(0,0,1;1.5708rad)
  shape: bbox 12.99 x 12.99 x 24.1 mm, 9 faces (baked)
FEATURE [Part::Feature] MukkeBox370
  Placement = pos=(192.9,-65,1.65) rot=(0,0,1;1.5708rad)
  shape: bbox 12.99 x 12.99 x 24.1 mm, 9 faces (baked)
FEATURE [Part::Feature] MukkeBox371
  Placement = pos=(55.616,-66.484,1.65) rot=(0,0,1;0rad)
  shape: bbox 2.5 x 3 x 1.2 mm, 76 faces (baked)
FEATURE [Part::Feature] MukkeBox372
  Placement = pos=(79.716,-61.134,1.65) rot=(0,0,1;1.5708rad)
  shape: bbox 3 x 2.5 x 1.2 mm, 76 faces (baked)
FEATURE [Part::Feature] MukkeBox373
  Placement = pos=(110.716,-42.634,1.65) rot=(0,0,1;0rad)
  shape: bbox 9.9 x 6.5 x 2.32 mm, 80 faces (baked)
FEATURE [Part::Feature] MukkeBox374
  Placement = pos=(104.316,-51.584,1.65) rot=(0,0,1;1.5708rad)
  shape: bbox 3 x 2.5 x 1.2 mm, 76 faces (baked)
FEATURE [Part::Feature] MukkeBox375
  Placement = pos=(81.166,-83.534,1.65) rot=(0,0,1;3.14159rad)
  shape: bbox 2.5 x 3 x 1.2 mm, 76 faces (baked)
FEATURE [Part::Feature] MukkeBox376
  Placement = pos=(83.781,-91.889,1.65) rot=(0,0,1;0rad)
  shape: bbox 2.5 x 3 x 1.2 mm, 76 faces (baked)
FEATURE [Part::Feature] MukkeBox377
  Placement = pos=(89.416,-47.084,1.65) rot=(0,0,-1;1.5708rad)
  shape: bbox 6.5 x 9.9 x 2.32 mm, 80 faces (baked)
FEATURE [Part::Feature] MukkeBox378
  Placement = pos=(233.616,-117.134,1.65) rot=(0,0,1;0rad)
  shape: bbox 2.5 x 3 x 1.2 mm, 76 faces (baked)
FEATURE [Part::Feature] MukkeBox379
  Placement = pos=(240.916,-116.184,1.65) rot=(0,0,1;3.14159rad)
  shape: bbox 2.5 x 3 x 1.2 mm, 76 faces (baked)
FEATURE [Part::Feature] MukkeBox380
  Placement = pos=(146.541,-122.584,1.65) rot=(0,0,1;3.14159rad)
  shape: bbox 2.5 x 3 x 1.2 mm, 76 faces (baked)
FEATURE [Part::Feature] MukkeBox381
  Placement = pos=(109.566,-121.384,1.65) rot=(0,0,1;1.5708rad)
  shape: bbox 0.8 x 1.6 x 0.45 mm, 26 faces (baked)
FEATURE [Part::Feature] MukkeBox382
  Placement = pos=(111.866,-121.359,1.65) rot=(0,0,1;1.5708rad)
  shape: bbox 0.8 x 1.6 x 0.45 mm, 26 faces (baked)
FEATURE [Part::Feature] MukkeBox383
  Placement = pos=(81.766,-138.684,1.65) rot=(0,0,1;1.5708rad)
  shape: bbox 0.8 x 1.6 x 0.45 mm, 26 faces (baked)
FEATURE [Part::Feature] MukkeBox384
  Placement = pos=(86.766,-138.484,1.65) rot=(0,0,1;1.5708rad)
  shape: bbox 0.8 x 1.6 x 0.45 mm, 26 faces (baked)
FEATURE [Part::Feature] MukkeBox385
  Placement = pos=(91.766,-138.484,1.65) rot=(0,0,1;1.5708rad)
  shape: bbox 0.8 x 1.6 x 0.45 mm, 26 faces (baked)
FEATURE [Part::Feature] MukkeBox386
  Placement = pos=(81.666,-127.984,1.65) rot=(0,0,1;1.5708rad)
  shape: bbox 0.8 x 1.6 x 0.45 mm, 26 faces (baked)
FEATURE [Part::Feature] MukkeBox387
  Placement = pos=(86.766,-127.984,1.65) rot=(0,0,1;1.5708rad)
  shape: bbox 0.8 x 1.6 x 0.45 mm, 26 faces (baked)
FEATURE [Part::Feature] MukkeBox388
  Placement = pos=(91.866,-127.884,1.65) rot=(0,0,1;1.5708rad)
  shape: bbox 0.8 x 1.6 x 0.45 mm, 26 faces (baked)
FEATURE [Part::Feature] MukkeBox389
  Placement = pos=(96.966,-127.984,1.65) rot=(0,0,1;1.5708rad)
  shape: bbox 0.8 x 1.6 x 0.45 mm, 26 faces (baked)
FEATURE [Part::Feature] MukkeBox390
  Placement = pos=(83.066,-106.384,1.65) rot=(0,0,1;1.5708rad)
  shape: bbox 0.8 x 1.6 x 0.45 mm, 26 faces (baked)
FEATURE [Part::Feature] MukkeBox391
  Placement = pos=(75.666,-114.884,1.65) rot=(0,0,1;3.14159rad)
  shape: bbox 1.6 x 0.8 x 0.45 mm, 26 faces (baked)
FEATURE [Part::Feature] MukkeBox392
  Placement = pos=(74.066,-128.084,1.65) rot=(0,0,1;1.5708rad)
  shape: bbox 0.8 x 1.6 x 0.45 mm, 26 faces (baked)
FEATURE [Part::Feature] MukkeBox393
  Placement = pos=(66.566,-128.084,1.65) rot=(0,0,1;1.5708rad)
  shape: bbox 0.8 x 1.6 x 0.45 mm, 26 faces (baked)
FEATURE [Part::Feature] MukkeBox394
  Placement = pos=(67.166,-138.484,1.65) rot=(0,0,-1;1.5708rad)
  shape: bbox 0.8 x 1.6 x 0.45 mm, 26 faces (baked)
FEATURE [Part::Feature] MukkeBox395
  Placement = pos=(75.166,-138.584,1.65) rot=(0,0,-1;1.5708rad)
  shape: bbox 0.8 x 1.6 x 0.45 mm, 26 faces (baked)
FEATURE [Part::Feature] MukkeBox396
  Placement = pos=(95.166,-116.884,1.65) rot=(0,0,-1;1.5708rad)
  shape: bbox 0.8 x 1.6 x 0.45 mm, 26 faces (baked)
FEATURE [Part::Feature] MukkeBox397
  Placement = pos=(103.316,-40.309,1.65) rot=(0,0,1;3.14159rad)
  shape: bbox 1.6 x 0.8 x 0.45 mm, 26 faces (baked)
FEATURE [Part::Feature] MukkeBox398
  Placement = pos=(104.566,-48.434,1.65) rot=(0,0,1;0rad)
  shape: bbox 1.6 x 0.8 x 0.45 mm, 26 faces (baked)
FEATURE [Part::Feature] MukkeBox399
  Placement = pos=(104.316,-55.434,1.65) rot=(0,0,1;0rad)
  shape: bbox 1.6 x 0.8 x 0.45 mm, 26 faces (baked)
FEATURE [Part::Feature] MukkeBox400
  Placement = pos=(108.216,-53.959,1.65) rot=(0,0,-1;1.5708rad)
  shape: bbox 0.8 x 1.6 x 0.45 mm, 26 faces (baked)
FEATURE [Part::Feature] MukkeBox401
  Placement = pos=(77.416,-84.284,1.65) rot=(0,0,1;1.5708rad)
  shape: bbox 0.8 x 1.6 x 0.45 mm, 26 faces (baked)
FEATURE [Part::Feature] MukkeBox402
  Placement = pos=(77.416,-88.034,1.65) rot=(0,0,1;1.5708rad)
  shape: bbox 0.8 x 1.6 x 0.45 mm, 26 faces (baked)
FEATURE [Part::Feature] MukkeBox403
  Placement = pos=(84.916,-83.534,1.65) rot=(0,0,1;1.5708rad)
  shape: bbox 0.8 x 1.6 x 0.45 mm, 26 faces (baked)
FEATURE [Part::Feature] MukkeBox404
  Placement = pos=(84.916,-87.034,1.65) rot=(0,0,1;1.5708rad)
  shape: bbox 0.8 x 1.6 x 0.45 mm, 26 faces (baked)
FEATURE [Part::Feature] MukkeBox405
  Placement = pos=(80.166,-90.784,1.65) rot=(0,0,1;0rad)
  shape: bbox 1.6 x 0.8 x 0.45 mm, 26 faces (baked)
FEATURE [Part::Feature] MukkeBox406
  Placement = pos=(80.166,-92.784,1.65) rot=(0,0,1;3.14159rad)
  shape: bbox 1.6 x 0.8 x 0.45 mm, 26 faces (baked)
FEATURE [Part::Feature] MukkeBox407
  Placement = pos=(80.341,-56.384,1.65) rot=(0,0,1;3.14159rad)
  shape: bbox 1.6 x 0.8 x 0.45 mm, 26 faces (baked)
FEATURE [Part::Feature] MukkeBox408
  Placement = pos=(79.466,-58.134,1.65) rot=(0,0,1;0rad)
  shape: bbox 1.6 x 0.8 x 0.45 mm, 26 faces (baked)
FEATURE [Part::Feature] MukkeBox409
  Placement = pos=(75.216,-57.384,1.65) rot=(0,0,1;1.5708rad)
  shape: bbox 0.8 x 1.6 x 0.45 mm, 26 faces (baked)
FEATURE [Part::Feature] MukkeBox410
  Placement = pos=(70.666,-53.209,1.65) rot=(0,0,1;0rad)
  shape: bbox 1.6 x 0.8 x 0.45 mm, 26 faces (baked)
FEATURE [Part::Feature] MukkeBox411
  Placement = pos=(71.566,-46.684,1.65) rot=(0,0,-1;1.5708rad)
  shape: bbox 0.8 x 1.6 x 0.45 mm, 26 faces (baked)
FEATURE [Part::Feature] MukkeBox412
  Placement = pos=(73.166,-46.684,1.65) rot=(0,0,-1;1.5708rad)
  shape: bbox 0.8 x 1.6 x 0.45 mm, 26 faces (baked)
FEATURE [Part::Feature] MukkeBox413
  Placement = pos=(71.466,-58.384,1.65) rot=(0,0,1;0rad)
  shape: bbox 1.6 x 0.8 x 0.45 mm, 26 faces (baked)
FEATURE [Part::Feature] MukkeBox414
  Placement = pos=(68.316,-60.784,1.65) rot=(0,0,1;0rad)
  shape: bbox 1.6 x 0.8 x 0.45 mm, 26 faces (baked)
FEATURE [Part::Feature] MukkeBox415
  Placement = pos=(68.316,-62.284,1.65) rot=(0,0,1;0rad)
  shape: bbox 1.6 x 0.8 x 0.45 mm, 26 faces (baked)
FEATURE [Part::Feature] MukkeBox416
  Placement = pos=(68.316,-63.784,1.65) rot=(0,0,1;0rad)
  shape: bbox 1.6 x 0.8 x 0.45 mm, 26 faces (baked)
FEATURE [Part::Feature] MukkeBox417
  Placement = pos=(231.616,-120.134,1.65) rot=(0,0,1;3.14159rad)
  shape: bbox 1.6 x 0.8 x 0.45 mm, 26 faces (baked)
FEATURE [Part::Feature] MukkeBox418
  Placement = pos=(51.616,-62.234,1.65) rot=(0,0,-1;1.5708rad)
  shape: bbox 0.8 x 1.6 x 0.45 mm, 26 faces (baked)
FEATURE [Part::Feature] MukkeBox419
  Placement = pos=(51.616,-66.234,1.65) rot=(0,0,-1;1.5708rad)
  shape: bbox 0.8 x 1.6 x 0.45 mm, 26 faces (baked)
FEATURE [Part::Feature] MukkeBox420
  Placement = pos=(230.616,-117.134,1.65) rot=(0,0,-1;1.5708rad)
  shape: bbox 0.8 x 1.6 x 0.45 mm, 26 faces (baked)
FEATURE [Part::Feature] MukkeBox421
  Placement = pos=(77.716,-64.884,1.65) rot=(0,0,1;1.5708rad)
  shape: bbox 0.8 x 1.6 x 0.45 mm, 26 faces (baked)
FEATURE [Part::Feature] MukkeBox422
  Placement = pos=(56.616,-61.734,1.65) rot=(0,0,-1;1.5708rad)
  shape: bbox 0.8 x 1.6 x 0.45 mm, 26 faces (baked)
FEATURE [Part::Feature] MukkeBox423
  Placement = pos=(80.716,-64.884,1.65) rot=(0,0,1;1.5708rad)
  shape: bbox 0.8 x 1.6 x 0.45 mm, 26 faces (baked)
FEATURE [Part::Feature] MukkeBox424
  Placement = pos=(242.916,-113.684,1.65) rot=(0,0,1;0rad)
  shape: bbox 1.6 x 0.8 x 0.45 mm, 26 faces (baked)
FEATURE [Part::Feature] MukkeBox425
  Placement = pos=(243.666,-116.184,1.65) rot=(0,0,1;1.5708rad)
  shape: bbox 0.8 x 1.6 x 0.45 mm, 26 faces (baked)
FEATURE [Part::Feature] MukkeBox426
  Placement = pos=(236.266,-117.184,1.65) rot=(0,0,-1;1.5708rad)
  shape: bbox 0.8 x 1.6 x 0.45 mm, 26 faces (baked)
FEATURE [Part::Feature] MukkeBox427
  Placement = pos=(238.166,-117.184,1.65) rot=(0,0,-1;1.5708rad)
  shape: bbox 0.8 x 1.6 x 0.45 mm, 26 faces (baked)
FEATURE [Part::Feature] MukkeBox428
  Placement = pos=(204.666,-99.909,1.65) rot=(0,0,1;1.5708rad)
  shape: bbox 0.8 x 1.6 x 0.45 mm, 26 faces (baked)
FEATURE [Part::Feature] MukkeBox429
  Placement = pos=(206.166,-99.909,1.65) rot=(0,0,1;1.5708rad)
  shape: bbox 0.8 x 1.6 x 0.45 mm, 26 faces (baked)
FEATURE [Part::Feature] MukkeBox430
  Placement = pos=(203.166,-99.909,1.65) rot=(0,0,1;1.5708rad)
  shape: bbox 0.8 x 1.6 x 0.45 mm, 26 faces (baked)
FEATURE [Part::Feature] MukkeBox431
  Placement = pos=(224.9,-66,1.65) rot=(0,0,1;3.14159rad)
  shape: bbox 3.2 x 1.6 x 0.55 mm, 26 faces (baked)
FEATURE [Part::Feature] MukkeBox432
  Placement = pos=(174.9,-66,1.65) rot=(0,0,1;0rad)
  shape: bbox 3.2 x 1.6 x 0.55 mm, 26 faces (baked)
FEATURE [Part::Feature] MukkeBox433
  Placement = pos=(233.9,-51,1.65) rot=(0,0,1;3.14159rad)
  shape: bbox 3.2 x 1.6 x 0.55 mm, 26 faces (baked)
FEATURE [Part::Feature] MukkeBox434
  Placement = pos=(209.9,-51,1.65) rot=(0,0,1;3.14159rad)
  shape: bbox 3.2 x 1.6 x 0.55 mm, 26 faces (baked)
FEATURE [Part::Feature] MukkeBox435
  Placement = pos=(166.9,-51,1.65) rot=(0,0,1;0rad)
  shape: bbox 3.2 x 1.6 x 0.55 mm, 26 faces (baked)
FEATURE [Part::Feature] MukkeBox436
  Placement = pos=(190.9,-51,1.65) rot=(0,0,1;0rad)
  shape: bbox 3.2 x 1.6 x 0.55 mm, 26 faces (baked)
FEATURE [Part::Feature] MukkeBox437
  Placement = pos=(156.566,-90.984,1.65) rot=(0,0,1;3.14159rad)
  shape: bbox 3.2 x 1.6 x 0.55 mm, 26 faces (baked)
FEATURE [Part::Feature] MukkeBox438
  Placement = pos=(148.541,-120.084,1.65) rot=(0,0,1;0rad)
  shape: bbox 1.6 x 0.8 x 0.45 mm, 26 faces (baked)
FEATURE [Part::Feature] MukkeBox439
  Placement = pos=(149.541,-122.584,1.65) rot=(0,0,1;1.5708rad)
  shape: bbox 0.8 x 1.6 x 0.45 mm, 26 faces (baked)
FEATURE [Part::Feature] MukkeBox440
  Placement = pos=(143.791,-121.834,1.65) rot=(0,0,1;1.5708rad)
  shape: bbox 0.8 x 1.6 x 0.45 mm, 26 faces (baked)
FEATURE [Part::Feature] MukkeBox441
  Placement = pos=(227.216,-124.555,1.65) rot=(0,0,1;3.14159rad)
  shape: bbox 1.6 x 0.8 x 0.45 mm, 26 faces (baked)
FEATURE [Part::Feature] MukkeBox442
  Placement = pos=(227.216,-126.055,1.65) rot=(0,0,1;3.14159rad)
  shape: bbox 1.6 x 0.8 x 0.45 mm, 26 faces (baked)
FEATURE [Part::Feature] MukkeBox443
  Placement = pos=(227.216,-127.555,1.65) rot=(0,0,1;3.14159rad)
  shape: bbox 1.6 x 0.8 x 0.45 mm, 26 faces (baked)
FEATURE [Part::Feature] MukkeBox444
  Placement = pos=(135.866,-138.184,1.65) rot=(0,0,1;0rad)
  shape: bbox 3.2 x 1.6 x 0.55 mm, 26 faces (baked)
FEATURE [Part::Feature] MukkeBox445
  Placement = pos=(195.809,-130.488,1.65) rot=(0,0,1;0rad)
  shape: bbox 1.6 x 0.8 x 0.45 mm, 26 faces (baked)
FEATURE [Part::Feature] MukkeBox446
  Placement = pos=(195.809,-131.988,1.65) rot=(0,0,1;0rad)
  shape: bbox 1.6 x 0.8 x 0.45 mm, 26 faces (baked)
FEATURE [Part::Feature] MukkeBox447
  Placement = pos=(192.642,-119.128,1.65) rot=(0,0,-1;1.5708rad)
  shape: bbox 0.8 x 1.6 x 0.45 mm, 26 faces (baked)
FEATURE [Part::Feature] MukkeBox448
  Placement = pos=(191.766,-116.484,1.65) rot=(0,0,1;0rad)
  shape: bbox 1.6 x 0.8 x 0.45 mm, 26 faces (baked)
FEATURE [Part::Feature] MukkeBox449
  Placement = pos=(231.466,-123.805,1.65) rot=(0,0,1;0rad)
  shape: bbox 1.6 x 0.8 x 0.45 mm, 26 faces (baked)
FEATURE [Part::Feature] MukkeBox450
  Placement = pos=(65.266,-93.234,1.65) rot=(0,0,-1;1.5708rad)
  shape: bbox 0.8 x 1.6 x 0.45 mm, 26 faces (baked)
FEATURE [Part::Feature] MukkeBox451
  Placement = pos=(234.966,-123.805,1.65) rot=(0,0,1;3.14159rad)
  shape: bbox 1.6 x 0.8 x 0.45 mm, 26 faces (baked)
FEATURE [Part::Feature] MukkeBox452
  Placement = pos=(59.616,-94.084,1.65) rot=(0,0,1;1.5708rad)
  shape: bbox 0.8 x 1.6 x 0.45 mm, 26 faces (baked)
FEATURE [Part::Feature] MukkeBox453
  Placement = pos=(201.066,-138.5,1.65) rot=(0,0,1;1.5708rad)
  shape: bbox 0.8 x 1.6 x 0.45 mm, 26 faces (baked)
FEATURE [Part::Feature] MukkeBox454
  Placement = pos=(189.366,-138.5,1.65) rot=(0,0,1;1.5708rad)
  shape: bbox 0.8 x 1.6 x 0.45 mm, 26 faces (baked)
FEATURE [Part::Feature] MukkeBox455
  Placement = pos=(177.666,-138.5,1.65) rot=(0,0,1;1.5708rad)
  shape: bbox 0.8 x 1.6 x 0.45 mm, 26 faces (baked)
FEATURE [Part::Feature] MukkeBox456
  Placement = pos=(217.392,-119.653,1.65) rot=(0,0,-1;1.5708rad)
  shape: bbox 0.8 x 1.6 x 0.45 mm, 26 faces (baked)
FEATURE [Part::Feature] MukkeBox457
  Placement = pos=(219.892,-119.653,1.65) rot=(0,0,-1;1.5708rad)
  shape: bbox 0.8 x 1.6 x 0.45 mm, 26 faces (baked)
FEATURE [Part::Feature] MukkeBox458
  Placement = pos=(220.791,-116.984,1.65) rot=(0,0,1;3.14159rad)
  shape: bbox 1.6 x 0.8 x 0.45 mm, 26 faces (baked)
FEATURE [Part::Feature] MukkeBox459
  Placement = pos=(214.642,-119.528,1.65) rot=(0,0,-1;1.5708rad)
  shape: bbox 0.8 x 1.6 x 0.45 mm, 26 faces (baked)
FEATURE [Part::Feature] MukkeBox460
  Placement = pos=(187.392,-119.284,1.65) rot=(0,0,-1;1.5708rad)
  shape: bbox 0.8 x 1.6 x 0.45 mm, 26 faces (baked)
FEATURE [Part::Feature] MukkeBox461
  Placement = pos=(189.892,-119.184,1.65) rot=(0,0,-1;1.5708rad)
  shape: bbox 0.8 x 1.6 x 0.45 mm, 26 faces (baked)
FEATURE [Part::Feature] MukkeBox462
  Placement = pos=(131.116,-59.459,1.65) rot=(0,0,1;1.5708rad)
  shape: bbox 0.8 x 1.6 x 0.45 mm, 26 faces (baked)
FEATURE [Part::Feature] MukkeBox463
  Placement = pos=(130.266,-63.759,1.65) rot=(0,0,1;3.14159rad)
  shape: bbox 1.6 x 0.8 x 0.45 mm, 26 faces (baked)
FEATURE [Part::Feature] MukkeBox464
  Placement = pos=(134.016,-67.984,1.65) rot=(0,0,1;3.14159rad)
  shape: bbox 1.6 x 0.8 x 0.45 mm, 26 faces (baked)
FEATURE [Part::Feature] MukkeBox465
  Placement = pos=(137.641,-60.384,1.65) rot=(0,0,1;3.14159rad)
  shape: bbox 1.6 x 0.8 x 0.45 mm, 26 faces (baked)
FEATURE [Part::Feature] MukkeBox466
  Placement = pos=(130.266,-65.409,1.65) rot=(0,0,1;0rad)
  shape: bbox 1.6 x 0.8 x 0.45 mm, 26 faces (baked)
FEATURE [Part::Feature] MukkeBox467
  Placement = pos=(136.991,-70.159,1.65) rot=(0,0,1;3.14159rad)
  shape: bbox 3.2 x 1.6 x 0.55 mm, 26 faces (baked)
FEATURE [Part::Feature] MukkeBox468
  Placement = pos=(132.916,-59.459,1.65) rot=(0,0,1;1.5708rad)
  shape: bbox 0.8 x 1.6 x 0.45 mm, 26 faces (baked)
FEATURE [Part::Feature] MukkeBox469
  Placement = pos=(135.766,-56.784,1.65) rot=(0,0,1;3.14159rad)
  shape: bbox 1.6 x 0.8 x 0.45 mm, 26 faces (baked)
FEATURE [Part::Feature] MukkeBox470
  Placement = pos=(141.916,-52.959,1.65) rot=(0,0,-1;1.5708rad)
  shape: bbox 0.8 x 1.6 x 0.45 mm, 26 faces (baked)
FEATURE [Part::Feature] MukkeBox471
  Placement = pos=(135.791,-55.234,1.65) rot=(0,0,1;3.14159rad)
  shape: bbox 1.6 x 0.8 x 0.45 mm, 26 faces (baked)
FEATURE [Part::Feature] MukkeBox472
  Placement = pos=(140.266,-74.484,1.65) rot=(0,0,1;3.14159rad)
  shape: bbox 1.6 x 0.8 x 0.45 mm, 26 faces (baked)
FEATURE [Part::Feature] MukkeBox473
  Placement = pos=(140.291,-72.934,1.65) rot=(0,0,1;3.14159rad)
  shape: bbox 1.6 x 0.8 x 0.45 mm, 26 faces (baked)
FEATURE [Part::Feature] MukkeBox474
  Placement = pos=(142.791,-71.959,1.65) rot=(0,0,1;1.5708rad)
  shape: bbox 0.8 x 1.6 x 0.45 mm, 26 faces (baked)
FEATURE [Part::Feature] MukkeBox475
  Placement = pos=(86.916,-56.384,1.65) rot=(0,0,-1;1.5708rad)
  shape: bbox 1.6 x 3.2 x 0.55 mm, 26 faces (baked)
FEATURE [Part::Feature] MukkeBox476
  Placement = pos=(130.241,-67.984,1.65) rot=(0,0,-1;1.5708rad)
  shape: bbox 3 x 2.5 x 1.2 mm, 76 faces (baked)
FEATURE [Part::Feature] MukkeBox477
  Placement = pos=(135.425,-83.034,1.65) rot=(0,0,-1;1.5708rad)
  shape: bbox 6.5 x 9.9 x 2.32 mm, 80 faces (baked)
FEATURE [Part::Feature] MukkeBox478
  Placement = pos=(202.866,-110.734,1.65) rot=(0,0,1;0rad)
  shape: bbox 10.22 x 5.2 x 3.68 mm, 84 faces (baked)
FEATURE [Part::Feature] MukkeBox479
  Placement = pos=(129.366,-135.984,1.65) rot=(0,0,1;0rad)
  shape: bbox 4.83 x 3.745 x 9.8 mm, 19 faces (baked)
FEATURE [Part::Feature] MukkeBox480
  Placement = pos=(83.366,-113.534,1.65) rot=(0,0,1;0rad)
  shape: bbox 9 x 9 x 1.5 mm, 764 faces (baked)
FEATURE [Part::Feature] MukkeBox481
  Placement = pos=(138.366,-52.859,1.65) rot=(0,0,1;0rad)
  shape: bbox 2.8 x 2.9 x 1.55 mm, 109 faces (baked)
FEATURE [Part::Feature] MukkeBox482
  Placement = pos=(77.716,-52.634,1.65) rot=(0,0,1;0rad)
  shape: bbox 6 x 4.9 x 1.42 mm, 260 faces (baked)
FEATURE [Part::Feature] MukkeBox483
  Placement = pos=(200,-87.95,1.65) rot=(0,0,1;1.5708rad)
  shape: bbox 10.3 x 9.87 x 1.6 mm, 576 faces (baked)
FEATURE [Part::Feature] MukkeBox484
  Placement = pos=(161.291,-129.259,1.65) rot=(0,0,1;3.14159rad)
  shape: bbox 13.2 x 23 x 4 mm, 314 faces (baked)
FEATURE [Part::Feature] MukkeBox485
  Placement = pos=(204.716,-130.834,1.65) rot=(0,0,1;1.5708rad)
  shape: bbox 9.7 x 6.4 x 1.1 mm, 456 faces (baked)
FEATURE [Part::Feature] MukkeBox486
  Placement = pos=(231.716,-126.555,1.65) rot=(0,0,1;3.14159rad)
  shape: bbox 2.8 x 2.9 x 1.55 mm, 109 faces (baked)
FEATURE [Part::Feature] MukkeBox487
  Placement = pos=(135.966,-64.159,1.65) rot=(0,0,1;0rad)
  shape: bbox 6 x 4.9 x 1.75 mm, 156 faces (baked)
FEATURE [Part::Feature] MukkeBox488
  Placement = pos=(211.966,-110.784,1.65) rot=(0,0,1;0rad)
  shape: bbox 4.924 x 5.212 x 6 mm, 54 faces (baked)
FEATURE [Part::Feature] MukkeBox489
  Placement = pos=(177.066,-110.584,1.65) rot=(0,0,1;0rad)
  shape: bbox 4.924 x 5.212 x 6 mm, 54 faces (baked)
FEATURE [Part::Feature] MukkeBox490
  Placement = pos=(58.716,-91.1857,1.65) rot=(0,0,1;3.14159rad)
  shape: bbox 1.6 x 0.8 x 0.8 mm, 28 faces (baked)
FEATURE [Part::Feature] MukkeBox491
  Placement = pos=(64.466,-98.984,1.65) rot=(0,0,1;0rad)
  shape: bbox 1.6 x 0.8 x 0.8 mm, 28 faces (baked)
FEATURE [Part::Feature] MukkeBox492
  Placement = pos=(54.366,-99.834,1.65) rot=(0,0,1;0rad)
  shape: bbox 1.6 x 0.8 x 0.8 mm, 28 faces (baked)
FEATURE [Part::Feature] MukkeBox493
  Placement = pos=(49.8776,-104.386,1.65) rot=(0,0,1;0rad)
  shape: bbox 7.785 x 8.053 x 8.3 mm, 46 faces (baked)
FEATURE [Part::Feature] MukkeBox494
  Placement = pos=(72.216,-42.784,1.65) rot=(0,0,1;0rad)
  shape: bbox 3.2 x 1.6 x 0.55 mm, 26 faces (baked)
FEATURE [Part::Feature] MukkeBox495
  Placement = pos=(57.966,-99.8857,1.65) rot=(0,0,1;0rad)
  shape: bbox 1.6 x 0.8 x 0.45 mm, 26 faces (baked)
FEATURE [Part::Feature] MukkeBox496
  Placement = pos=(59.1276,-102.336,1.65) rot=(0,0,-1;1.5708rad)
  shape: bbox 0.8 x 1.6 x 0.45 mm, 26 faces (baked)
FEATURE [Part::Feature] MukkeBox497
  Placement = pos=(68.0776,-96.3357,1.65) rot=(0,0,-1;1.5708rad)
  shape: bbox 3 x 2.5 x 1.2 mm, 76 faces (baked)
FEATURE [Part::Feature] MukkeBox498
  Placement = pos=(68.0776,-92.3857,1.65) rot=(0,0,-1;1.5708rad)
  shape: bbox 3 x 2.5 x 1.2 mm, 76 faces (baked)
FEATURE [Part::Feature] MukkeBox499
  Placement = pos=(56.9426,-96.5107,1.65) rot=(0,0,1;1.5708rad)
  shape: bbox 2.9 x 2.8 x 1.55 mm, 124 faces (baked)
FEATURE [Part::Feature] MukkeBox500
  Placement = pos=(62.291,-49.009,1.65) rot=(0,0,1;3.14159rad)
  shape: bbox 6.128 x 6.515 x 7 mm, 49 faces (baked)
FEATURE [Part::Feature] MukkeBox501
  Placement = pos=(61.716,-62.284,1.65) rot=(0,0,-1;1.5708rad)
  shape: bbox 0.8 x 1.6 x 0.8 mm, 28 faces (baked)
FEATURE [Part::Feature] MukkeBox502
  Placement = pos=(134.991,-52.159,1.65) rot=(0,0,-1;1.5708rad)
  shape: bbox 0.8 x 1.6 x 0.8 mm, 28 faces (baked)
FEATURE [Part::Feature] MukkeBox503
  Placement = pos=(87.866,-99.159,1.65) rot=(0,0,1;1.5708rad)
  shape: bbox 3 x 2.5 x 1.2 mm, 76 faces (baked)
FEATURE [Part::Feature] MukkeBox504
  Placement = pos=(85.141,-99.084,1.65) rot=(0,0,-1;1.5708rad)
  shape: bbox 0.8 x 1.6 x 0.45 mm, 26 faces (baked)
FEATURE [Part::Feature] MukkeBox505
  Placement = pos=(87.841,-101.884,1.65) rot=(0,0,1;0rad)
  shape: bbox 1.6 x 0.8 x 0.45 mm, 26 faces (baked)
FEATURE [Part::Feature] MukkeBox506
  Placement = pos=(88.041,-96.484,1.65) rot=(0,0,1;0rad)
  shape: bbox 1.6 x 0.8 x 0.45 mm, 26 faces (baked)
FEATURE [Part::Feature] MukkeBox507
  Placement = pos=(190.366,-124.084,1.65) rot=(0,0,1;0rad)
  shape: bbox 7.2 x 3.5 x 10.9 mm, 22 faces (baked)
FEATURE [Part::Feature] MukkeBox508
  Placement = pos=(198.266,-124.084,1.65) rot=(0,0,1;0rad)
  shape: bbox 7.2 x 3.5 x 10.9 mm, 22 faces (baked)
FEATURE [Part::Feature] MukkeBox509
  Placement = pos=(211.166,-124.084,1.65) rot=(0,0,1;3.14159rad)
  shape: bbox 7.2 x 3.5 x 10.9 mm, 22 faces (baked)
FEATURE [Part::Feature] MukkeBox510
  Placement = pos=(219.066,-124.084,1.65) rot=(0,0,1;3.14159rad)
  shape: bbox 7.2 x 3.5 x 10.9 mm, 22 faces (baked)
FEATURE [Part::Feature] MukkeBox511
  Placement = pos=(184.866,-124.048,1.65) rot=(0,0,1;3.14159rad)
  shape: bbox 7.2 x 3.5 x 10.9 mm, 22 faces (baked)
FEATURE [Part::Feature] MukkeBox512
  Placement = pos=(185.166,-138.5,1.65) rot=(0,0,1;3.14159rad)
  shape: bbox 7.2 x 3.5 x 10.9 mm, 22 faces (baked)
FEATURE [Part::Feature] MukkeBox513
  Placement = pos=(176.766,-130,1.65) rot=(0,0,1;3.14159rad)
  shape: bbox 7.2 x 3.5 x 10.9 mm, 22 faces (baked)
FEATURE [Part::Feature] MukkeBox514
  Placement = pos=(208.566,-138.5,1.65) rot=(0,0,1;3.14159rad)
  shape: bbox 7.2 x 3.5 x 10.9 mm, 22 faces (baked)
FEATURE [Part::Feature] MukkeBox515
  Placement = pos=(171.766,-124.048,1.65) rot=(0,0,1;0rad)
  shape: bbox 7.2 x 3.5 x 10.9 mm, 22 faces (baked)
FEATURE [Part::Feature] MukkeBox516
  Placement = pos=(179.866,-130,1.65) rot=(0,0,1;0rad)
  shape: bbox 7.2 x 3.5 x 10.9 mm, 22 faces (baked)
FEATURE [Part::Feature] MukkeBox517
  Placement = pos=(196.766,-138.5,1.65) rot=(0,0,1;3.14159rad)
  shape: bbox 7.2 x 3.5 x 10.9 mm, 22 faces (baked)
FEATURE [Part::Feature] MukkeBox518
  Placement = pos=(218.066,-132.884,1.65) rot=(0,0,-1;1.5708rad)
  shape: bbox 5.212 x 4.924 x 6 mm, 54 faces (baked)
FEATURE [Part::Feature] MukkeBox519
  Placement = pos=(217.966,-129.584,1.65) rot=(0,0,1;1.5708rad)
  shape: bbox 5.212 x 4.924 x 6 mm, 54 faces (baked)
FEATURE [Part::Feature] MukkeBox520
  Placement = pos=(218.666,-138.484,1.65) rot=(0,0,-1;1.5708rad)
  shape: bbox 7.62 x 2.54 x 11.54 mm, 76 faces (baked)
FEATURE [Part::Feature] MukkeBox521
  Placement = pos=(143.891,-68.284,1.65) rot=(0,0,1;0rad)
  shape: bbox 3.2 x 1.6 x 0.55 mm, 26 faces (baked)
FEATURE [Part::Feature] MukkeBox522
  Placement = pos=(187.291,-110.559,1.65) rot=(0,0,1;3.14159rad)
  shape: bbox 7.2 x 3.5 x 10.9 mm, 22 faces (baked)
FEATURE [Part::Feature] MukkeBox523
  Placement = pos=(222.741,-110.534,1.65) rot=(0,0,1;3.14159rad)
  shape: bbox 7.2 x 3.5 x 10.9 mm, 22 faces (baked)
FEATURE [Part::Feature] MukkeBox524
  Placement = pos=(156.566,-86.184,1.65) rot=(0,0,1;3.14159rad)
  shape: bbox 3.2 x 1.6 x 0.55 mm, 26 faces (baked)
FEATURE [Part::Feature] MukkeBox525
  Placement = pos=(156.566,-88.584,1.65) rot=(0,0,1;3.14159rad)
  shape: bbox 3.2 x 1.6 x 0.55 mm, 26 faces (baked)
FEATURE [Part::Feature] MukkeBox526
  Placement = pos=(124.866,-136.984,1.65) rot=(0,0,1;3.14159rad)
  shape: bbox 1.6 x 0.8 x 0.45 mm, 26 faces (baked)
FEATURE [Part::Feature] MukkeBox527
  Placement = pos=(138.866,-125.884,1.65) rot=(0,0,1;0rad)
  shape: bbox 1.6 x 0.8 x 0.45 mm, 26 faces (baked)
FEATURE [Part::Feature] MukkeBox528
  Placement = pos=(137.066,-129.784,1.65) rot=(0,0,1;1.5708rad)
  shape: bbox 0.8 x 1.6 x 0.45 mm, 26 faces (baked)
FEATURE [Part::Feature] MukkeBox529
  Placement = pos=(139.766,-134.984,1.65) rot=(0,0,-1;1.5708rad)
  shape: bbox 0.8 x 1.6 x 0.45 mm, 26 faces (baked)
FEATURE [Part::Feature] MukkeBox530
  Placement = pos=(138.231,-135.009,1.65) rot=(0,0,1;1.5708rad)
  shape: bbox 0.8 x 1.6 x 0.45 mm, 26 faces (baked)
FEATURE [Part::Feature] MukkeBox531
  shape: bbox 200 x 105 x 1.6 mm, 249 faces (baked)
FEATURE [Part::MultiFuse] Fusion
  Placement = pos=(145,97,304) rot=(0,1,0;3.14159rad)
  Shapes = -> [MukkeBox272,MukkeBox276,MukkeBox278,MukkeBox277,MukkeBox275,MukkeBox274,MukkeBox273,MukkeBox357,MukkeBox312,MukkeBox485,MukkeBox505,MukkeBox508,MukkeBox370,MukkeBox391,MukkeBox446,MukkeBox474,MukkeBox381,MukkeBox380,MukkeBox401,MukkeBox420,MukkeBox377,MukkeBox290,MukkeBox509,MukkeBox502,MukkeBox289,MukkeBox341,MukkeBox340,MukkeBox283,MukkeBox528,MukkeBox482,MukkeBox497,MukkeBox522,MukkeBox512,+227 more]
FEATURE [App::DocumentObjectGroup] Gruppe  label="Platine"
  Group = -> [Fusion]
FEATURE [Sketcher::SketchObject] CopySketch017  label="SketchGround003"
  MapMode = 2
  Support = -> [XY_Plane024]
  sketch-geometry (25):
    g0: LineSegment [constr] StartX=-115 StartY=90 StartZ=0 EndX=115 EndY=90 EndZ=0
    g1: LineSegment [constr] StartX=-115 StartY=-90 StartZ=0 EndX=115 EndY=-90 EndZ=0
    g2: LineSegment [constr] StartX=120 StartY=85 StartZ=0 EndX=120 EndY=-85 EndZ=0
    g3: LineSegment [constr] StartX=-120 StartY=85 StartZ=0 EndX=-120 EndY=-85 EndZ=0
    g4: ArcOfCircle [constr] CenterX=115 CenterY=85 CenterZ=0 NormalX=0 NormalY=0 NormalZ=1 AngleXU=0 Radius=5 StartAngle=1e-15 EndAngle=1.5708
    g5: ArcOfCircle [constr] CenterX=115 CenterY=-85 CenterZ=0 NormalX=0 NormalY=0 NormalZ=1 AngleXU=0 Radius=5 StartAngle=4.71239 EndAngle=6.28319
    g6: ArcOfCircle [constr] CenterX=-115 CenterY=-85 CenterZ=0 NormalX=0 NormalY=0 NormalZ=1 AngleXU=0 Radius=5 StartAngle=3.14159 EndAngle=4.71239
    g7: ArcOfCircle [constr] CenterX=-115 CenterY=85 CenterZ=0 NormalX=0 NormalY=0 NormalZ=1 AngleXU=0 Radius=5 StartAngle=1.5708 EndAngle=3.14159
    g8: Circle [constr] CenterX=110 CenterY=80 CenterZ=0 NormalX=0 NormalY=0 NormalZ=1 AngleXU=0 Radius=3.25
    g9: Circle [constr] CenterX=-110 CenterY=80 CenterZ=0 NormalX=0 NormalY=0 NormalZ=1 AngleXU=0 Radius=3.25
    g10: Circle [constr] CenterX=110 CenterY=-80 CenterZ=0 NormalX=0 NormalY=0 NormalZ=1 AngleXU=0 Radius=3.25
    g11: Circle [constr] CenterX=-110 CenterY=-80 CenterZ=0 NormalX=0 NormalY=0 NormalZ=1 AngleXU=0 Radius=3.25
    g12: Circle [constr] CenterX=110 CenterY=0 CenterZ=0 NormalX=0 NormalY=0 NormalZ=1 AngleXU=0 Radius=3.25
    g13: Circle [constr] CenterX=-110 CenterY=0 CenterZ=0 NormalX=0 NormalY=0 NormalZ=1 AngleXU=0 Radius=3.25
    g14: Circle [constr] CenterX=0 CenterY=70 CenterZ=0 NormalX=0 NormalY=0 NormalZ=1 AngleXU=0 Radius=3.25
    g15: Circle [constr] CenterX=0 CenterY=-70 CenterZ=0 NormalX=0 NormalY=0 NormalZ=1 AngleXU=0 Radius=3.25
    g16: ArcOfCircle CenterX=115 CenterY=85 CenterZ=0 NormalX=0 NormalY=0 NormalZ=1 AngleXU=0 Radius=5.5 StartAngle=0 EndAngle=1.5708
    g17: LineSegment StartX=115 StartY=90.5 StartZ=0 EndX=105 EndY=90.5 EndZ=0
    g18: LineSegment StartX=105 StartY=95.5 StartZ=0 EndX=115 EndY=95.5 EndZ=0
    g19: ArcOfCircle CenterX=115 CenterY=85 CenterZ=0 NormalX=0 NormalY=0 NormalZ=1 AngleXU=0 Radius=10.5 StartAngle=0 EndAngle=1.5708
    g20: LineSegment StartX=120.5 StartY=85 StartZ=0 EndX=120.5 EndY=0 EndZ=0
    g21: LineSegment StartX=120.5 StartY=0 StartZ=0 EndX=125.5 EndY=0 EndZ=0
    g22: LineSegment StartX=125.5 StartY=0 StartZ=0 EndX=125.5 EndY=85 EndZ=0
    g23: ArcOfCircle CenterX=105 CenterY=85 CenterZ=0 NormalX=0 NormalY=0 NormalZ=1 AngleXU=0 Radius=10.5 StartAngle=1.5708 EndAngle=2.59028
    g24: LineSegment StartX=96.0557 StartY=90.5 StartZ=0 EndX=105 EndY=90.5 EndZ=0
  constraints (66):
    c: Symmetric(g0,g0,g-2)
    c: Equal(g1,g0)
    c: Symmetric(g1,g1,g-2)
    c: Symmetric(g2,g2,g-1)
    c: Symmetric(g3,g3,g-1)
    c: Equal(g3,g2)
    c: Symmetric(g0,g1,g-1)
    c: Symmetric(g2,g3,g-2)
    c: Coincident(g4,g2)
    c: Tangent(g7,g0) = 1.5708
    c: Tangent(g7,g3) = -1.5708
    c: Tangent(g0,g4) = 1.5708
    c: Coincident(g5,g1)
    c: Tangent(g5,g2) = 1.5708
    c: Coincident(g3,g6)
    c: Tangent(g6,g1) = -1.5708
    c: Distance(g3,g2) = 240
    c: Radius(g4) = 5
    c: Distance(g0,g1) = 180
    c: Diameter(g8) = 6.5
    c: DistanceY(g8,g0) = 10
    c: DistanceX(g8,g2) = 10
    c: Equal(g9,g8)
    c: Symmetric(g9,g8,g-2)
    c: Equal(g11,g10)
    c: Equal(g10,g8)
    c: Symmetric(g10,g8,g-1)
    c: Symmetric(g11,g10,g-2)
    c: PointOnObject(g12,g-1)
    c: PointOnObject(g13,g-1)
    c: Equal(g13,g12)
    c: Equal(g12,g8)
    c: Vertical(g12,g8)
    c: Vertical(g13,g9)
    c: Equal(g15,g14)
    c: Equal(g14,g8)
    c: PointOnObject(g15,g-2)
    c: Symmetric(g15,g14,g-1)
    c: DistanceY(g14,g0) = 20
    c: Radius(g16) = 5.5
    c: Coincident(g16,g4)
    c: Horizontal(g16,g16)
    c: Vertical(g16,g16)
    c: Horizontal(g17)
    c: DistanceX(g17,g17) = 10
    c: Coincident(g17,g16)
    c: DistanceY(g16,g18) = 5
    c: Vertical(g16,g18)
    c: Horizontal(g18)
    c: Horizontal(g19,g16)
    c: Coincident(g18,g19)
    c: Coincident(g4,g19)
    c: Vertical(g20)
    c: PointOnObject(g22,g-1)
    c: Coincident(g21,g22)
    c: PointOnObject(g20,g-1)
    c: Coincident(g21,g20)
    c: Coincident(g20,g16)
    c: Vertical(g22)
    c: Coincident(g22,g19)
    c: Vertical(g17,g18)
    c: Tangent(g23,g18) = 1.5708
    c: Equal(g19,g23)
    c: Horizontal(g23,g17)
    c: Coincident(g24,g23)
    c: Coincident(g17,g24)
FEATURE [PartDesign::Pad] Pad036
  Length = 14
  Length2 = 100
  Profile = -> CopySketch017
  Reversed = true
  Type = 0
FEATURE [PartDesign::Mirrored] Mirrored009
  BaseFeature = -> Pad036
  MirrorPlane = -> CopySketch017 [H_Axis]
  Originals = -> [Pad036]
FEATURE [Sketcher::SketchObject] Sketch078
  MapMode = 5
  Placement = pos=(0,0,-14) rot=(1,0,0;3.14159rad)
  Support = -> [Mirrored009]
  expr: Constraints[17] = CopySketch017.Constraints[17]
  expr: Constraints[38] = CopySketch017.Constraints[38]
  expr: Constraints[21] = CopySketch017.Constraints[21]
  expr: Constraints[20] = CopySketch017.Constraints[20]
  expr: Constraints[19] = CopySketch017.Constraints[19]
  expr: Constraints[18] = CopySketch017.Constraints[18]
  expr: Constraints[16] = CopySketch017.Constraints[16]
  sketch-geometry (23):
    g0: LineSegment [constr] StartX=-115 StartY=90 StartZ=0 EndX=115 EndY=90 EndZ=0
    g1: LineSegment [constr] StartX=-115 StartY=-90 StartZ=0 EndX=115 EndY=-90 EndZ=0
    g2: LineSegment [constr] StartX=120 StartY=85 StartZ=0 EndX=120 EndY=-85 EndZ=0
    g3: LineSegment [constr] StartX=-120 StartY=85 StartZ=0 EndX=-120 EndY=-85 EndZ=0
    g4: ArcOfCircle [constr] CenterX=115 CenterY=85 CenterZ=0 NormalX=0 NormalY=0 NormalZ=1 AngleXU=0 Radius=5 StartAngle=-8.8418e-12 EndAngle=1.5708
    g5: ArcOfCircle [constr] CenterX=115 CenterY=-85 CenterZ=0 NormalX=0 NormalY=0 NormalZ=1 AngleXU=0 Radius=5 StartAngle=4.71239 EndAngle=6.28319
    g6: ArcOfCircle [constr] CenterX=-115 CenterY=-85 CenterZ=0 NormalX=0 NormalY=0 NormalZ=1 AngleXU=0 Radius=5 StartAngle=3.14159 EndAngle=4.71239
    g7: ArcOfCircle [constr] CenterX=-115 CenterY=85 CenterZ=0 NormalX=0 NormalY=0 NormalZ=1 AngleXU=0 Radius=5 StartAngle=1.5708 EndAngle=3.14159
    g8: Circle [constr] CenterX=110 CenterY=80 CenterZ=0 NormalX=0 NormalY=0 NormalZ=1 AngleXU=0 Radius=3.25
    g9: Circle [constr] CenterX=-110 CenterY=80 CenterZ=0 NormalX=0 NormalY=0 NormalZ=1 AngleXU=0 Radius=3.25
    g10: Circle [constr] CenterX=110 CenterY=-80 CenterZ=0 NormalX=0 NormalY=0 NormalZ=1 AngleXU=0 Radius=3.25
    g11: Circle [constr] CenterX=-110 CenterY=-80 CenterZ=0 NormalX=0 NormalY=0 NormalZ=1 AngleXU=0 Radius=3.25
    g12: Circle [constr] CenterX=110 CenterY=0 CenterZ=0 NormalX=0 NormalY=0 NormalZ=1 AngleXU=0 Radius=3.25
    g13: Circle [constr] CenterX=-110 CenterY=0 CenterZ=0 NormalX=0 NormalY=0 NormalZ=1 AngleXU=0 Radius=3.25
    g14: Circle [constr] CenterX=0 CenterY=70 CenterZ=0 NormalX=0 NormalY=0 NormalZ=1 AngleXU=0 Radius=3.25
    g15: Circle [constr] CenterX=0 CenterY=-70 CenterZ=0 NormalX=0 NormalY=0 NormalZ=1 AngleXU=0 Radius=3.25
    g16: LineSegment StartX=105 StartY=95.5 StartZ=0 EndX=115 EndY=95.5 EndZ=0
    g17: ArcOfCircle CenterX=115 CenterY=85 CenterZ=0 NormalX=0 NormalY=0 NormalZ=1 AngleXU=0 Radius=10.5 StartAngle=-2.31e-14 EndAngle=1.5708
    g18: LineSegment StartX=94.5 StartY=0 StartZ=0 EndX=125.5 EndY=0 EndZ=0
    g19: LineSegment StartX=125.5 StartY=0 StartZ=0 EndX=125.5 EndY=85 EndZ=0
    g20: LineSegment StartX=94.5 StartY=85 StartZ=0 EndX=94.5 EndY=0 EndZ=0
    g21: LineSegment [constr] StartX=110 StartY=80 StartZ=0 EndX=110 EndY=95.5 EndZ=0
    g22: ArcOfCircle CenterX=105 CenterY=85 CenterZ=0 NormalX=0 NormalY=0 NormalZ=1 AngleXU=0 Radius=10.5 StartAngle=1.5708 EndAngle=3.14159
  constraints (59):
    c: Symmetric(g0,g0,g-2)
    c: Equal(g1,g0)
    c: Symmetric(g1,g1,g-2)
    c: Symmetric(g2,g2,g-1)
    c: Symmetric(g3,g3,g-1)
    c: Equal(g3,g2)
    c: Symmetric(g0,g1,g-1)
    c: Symmetric(g2,g3,g-2)
    c: Coincident(g4,g2)
    c: Tangent(g7,g0) = 1.5708
    c: Tangent(g7,g3) = -1.5708
    c: Tangent(g0,g4) = 1.5708
    c: Coincident(g5,g1)
    c: Tangent(g5,g2) = 1.5708
    c: Coincident(g3,g6)
    c: Tangent(g6,g1) = -1.5708
    c: Distance(g3,g2) = 240
    c: Radius(g4) = 5
    c: Distance(g0,g1) = 180
    c: Diameter(g8) = 6.5
    c: DistanceY(g8,g0) = 10
    c: DistanceX(g8,g2) = 10
    c: Equal(g9,g8)
    c: Symmetric(g9,g8,g-2)
    c: Equal(g11,g10)
    c: Equal(g10,g8)
    c: Symmetric(g10,g8,g-1)
    c: Symmetric(g11,g10,g-2)
    c: PointOnObject(g12,g-1)
    c: PointOnObject(g13,g-1)
    c: Equal(g13,g12)
    c: Equal(g12,g8)
    c: Vertical(g12,g8)
    c: Vertical(g13,g9)
    c: Equal(g15,g14)
    c: Equal(g14,g8)
    c: PointOnObject(g15,g-2)
    c: Symmetric(g15,g14,g-1)
    c: DistanceY(g14,g0) = 20
    c: Horizontal(g16)
    c: PointOnObject(g19,g-1)
    c: Coincident(g18,g19)
    c: Vertical(g19)
    c: Horizontal(g17,g20)
    c: Tangent(g19,g17) = -1.5708
    c: DistanceX(g2,g17) = 5.5
    c: Tangent(g16,g17) = 1.5708
    c: Vertical(g16,g0)
    c: Horizontal(g2,g17)
    c: Vertical(g20,g18)
    c: PointOnObject(g18,g-1)
    c: Coincident(g20,g18)
    c: Coincident(g21,g8)
    c: PointOnObject(g21,g16)
    c: Symmetric(g16,g16,g21)
    c: Vertical(g22,g22)
    c: Horizontal(g22,g22)
    c: Coincident(g16,g22)
    c: Coincident(g22,g20)
FEATURE [PartDesign::Pad] Pad037
  BaseFeature = -> Mirrored009
  Length = 14
  Length2 = 100
  Profile = -> Sketch078
  Type = 0
FEATURE [PartDesign::Mirrored] Mirrored010
  BaseFeature = -> Pad037
  MirrorPlane = -> Sketch078 [H_Axis]
  Originals = -> [Pad037]
FEATURE [PartDesign::Plane] DatumPlane015
  AttachmentOffset = pos=(0,0,-28) rot=(0,0,1;0rad)
  Length = 167.675
  MapMode = 5
  Placement = pos=(0,0,-28) rot=(0,0,1;0rad)
  ResizeMode = 0
  Support = -> [XY_Plane024]
  Width = 223.175
FEATURE [Sketcher::SketchObject] CopySketch018  label="GroundSketch005"
  Placement = pos=(0,0,-28) rot=(0,0,1;0rad)
  sketch-geometry (16):
    g0: LineSegment [constr] StartX=-115 StartY=90 StartZ=0 EndX=115 EndY=90 EndZ=0
    g1: LineSegment [constr] StartX=-115 StartY=-90 StartZ=0 EndX=115 EndY=-90 EndZ=0
    g2: LineSegment [constr] StartX=120 StartY=85 StartZ=0 EndX=120 EndY=-85 EndZ=0
    g3: LineSegment [constr] StartX=-120 StartY=85 StartZ=0 EndX=-120 EndY=-85 EndZ=0
    g4: ArcOfCircle [constr] CenterX=115 CenterY=85 CenterZ=0 NormalX=0 NormalY=0 NormalZ=1 AngleXU=0 Radius=5 StartAngle=-9e-16 EndAngle=1.5708
    g5: ArcOfCircle [constr] CenterX=115 CenterY=-85 CenterZ=0 NormalX=0 NormalY=0 NormalZ=1 AngleXU=0 Radius=5 StartAngle=4.71239 EndAngle=6.28319
    g6: ArcOfCircle [constr] CenterX=-115 CenterY=-85 CenterZ=0 NormalX=0 NormalY=0 NormalZ=1 AngleXU=0 Radius=5 StartAngle=3.14159 EndAngle=4.71239
    g7: ArcOfCircle [constr] CenterX=-115 CenterY=85 CenterZ=0 NormalX=0 NormalY=0 NormalZ=1 AngleXU=0 Radius=5 StartAngle=1.5708 EndAngle=3.14159
    g8: Circle CenterX=110 CenterY=80 CenterZ=0 NormalX=0 NormalY=0 NormalZ=1 AngleXU=0 Radius=3.25
    g9: Circle [constr] CenterX=-110 CenterY=80 CenterZ=0 NormalX=0 NormalY=0 NormalZ=1 AngleXU=0 Radius=3.25
    g10: Circle CenterX=110 CenterY=-80 CenterZ=0 NormalX=0 NormalY=0 NormalZ=1 AngleXU=0 Radius=3.25
    g11: Circle [constr] CenterX=-110 CenterY=-80 CenterZ=0 NormalX=0 NormalY=0 NormalZ=1 AngleXU=0 Radius=3.25
    g12: Circle CenterX=110 CenterY=0 CenterZ=0 NormalX=0 NormalY=0 NormalZ=1 AngleXU=0 Radius=3.25
    g13: Circle [constr] CenterX=-110 CenterY=0 CenterZ=0 NormalX=0 NormalY=0 NormalZ=1 AngleXU=0 Radius=3.25
    g14: Circle [constr] CenterX=0 CenterY=70 CenterZ=0 NormalX=0 NormalY=0 NormalZ=1 AngleXU=0 Radius=3.25
    g15: Circle [constr] CenterX=0 CenterY=-70 CenterZ=0 NormalX=0 NormalY=0 NormalZ=1 AngleXU=0 Radius=3.25
  constraints (39):
    c: Symmetric(g0,g0,g-2)
    c: Equal(g1,g0)
    c: Symmetric(g1,g1,g-2)
    c: Symmetric(g2,g2,g-1)
    c: Symmetric(g3,g3,g-1)
    c: Equal(g3,g2)
    c: Symmetric(g0,g1,g-1)
    c: Symmetric(g2,g3,g-2)
    c: Coincident(g4,g2)
    c: Tangent(g7,g0) = 1.5708
    c: Tangent(g7,g3) = -1.5708
    c: Tangent(g0,g4) = 1.5708
    c: Coincident(g5,g1)
    c: Tangent(g5,g2) = 1.5708
    c: Coincident(g3,g6)
    c: Tangent(g6,g1) = -1.5708
    c: Distance(g3,g2) = 240
    c: Radius(g4) = 5
    c: Distance(g0,g1) = 180
    c: Diameter(g8) = 6.5
    c: DistanceY(g8,g0) = 10
    c: DistanceX(g8,g2) = 10
    c: Equal(g9,g8)
    c: Symmetric(g9,g8,g-2)
    c: Equal(g11,g10)
    c: Equal(g10,g8)
    c: Symmetric(g10,g8,g-1)
    c: Symmetric(g11,g10,g-2)
    c: PointOnObject(g12,g-1)
    c: PointOnObject(g13,g-1)
    c: Equal(g13,g12)
    c: Equal(g12,g8)
    c: Vertical(g12,g8)
    c: Vertical(g13,g9)
    c: Equal(g15,g14)
    c: Equal(g14,g8)
    c: PointOnObject(g15,g-2)
    c: Symmetric(g15,g14,g-1)
    c: DistanceY(g14,g0) = 20
FEATURE [PartDesign::Pocket] Pocket047
  BaseFeature = -> Mirrored010
  Length = 9
  Length2 = 100
  Profile = -> CopySketch018
  Reversed = true
  Type = 1
FEATURE [Sketcher::SketchObject] CopySketch019  label="GroundSketch006"
  Placement = pos=(0,0,-28) rot=(0,0,1;0rad)
  sketch-geometry (16):
    g0: LineSegment [constr] StartX=-115 StartY=90 StartZ=0 EndX=115 EndY=90 EndZ=0
    g1: LineSegment [constr] StartX=-115 StartY=-90 StartZ=0 EndX=115 EndY=-90 EndZ=0
    g2: LineSegment [constr] StartX=120 StartY=85 StartZ=0 EndX=120 EndY=-85 EndZ=0
    g3: LineSegment [constr] StartX=-120 StartY=85 StartZ=0 EndX=-120 EndY=-85 EndZ=0
    g4: ArcOfCircle [constr] CenterX=115 CenterY=85 CenterZ=0 NormalX=0 NormalY=0 NormalZ=1 AngleXU=0 Radius=5 StartAngle=-9e-16 EndAngle=1.5708
    g5: ArcOfCircle [constr] CenterX=115 CenterY=-85 CenterZ=0 NormalX=0 NormalY=0 NormalZ=1 AngleXU=0 Radius=5 StartAngle=4.71239 EndAngle=6.28319
    g6: ArcOfCircle [constr] CenterX=-115 CenterY=-85 CenterZ=0 NormalX=0 NormalY=0 NormalZ=1 AngleXU=0 Radius=5 StartAngle=3.14159 EndAngle=4.71239
    g7: ArcOfCircle [constr] CenterX=-115 CenterY=85 CenterZ=0 NormalX=0 NormalY=0 NormalZ=1 AngleXU=0 Radius=5 StartAngle=1.5708 EndAngle=3.14159
    g8: Circle CenterX=110 CenterY=80 CenterZ=0 NormalX=0 NormalY=0 NormalZ=1 AngleXU=0 Radius=8
    g9: Circle [constr] CenterX=-110 CenterY=80 CenterZ=0 NormalX=0 NormalY=0 NormalZ=1 AngleXU=0 Radius=8
    g10: Circle CenterX=110 CenterY=-80 CenterZ=0 NormalX=0 NormalY=0 NormalZ=1 AngleXU=0 Radius=8
    g11: Circle [constr] CenterX=-110 CenterY=-80 CenterZ=0 NormalX=0 NormalY=0 NormalZ=1 AngleXU=0 Radius=8
    g12: Circle CenterX=110 CenterY=0 CenterZ=0 NormalX=0 NormalY=0 NormalZ=1 AngleXU=0 Radius=8
    g13: Circle [constr] CenterX=-110 CenterY=0 CenterZ=0 NormalX=0 NormalY=0 NormalZ=1 AngleXU=0 Radius=8
    g14: Circle [constr] CenterX=0 CenterY=70 CenterZ=0 NormalX=0 NormalY=0 NormalZ=1 AngleXU=0 Radius=8
    g15: Circle [constr] CenterX=0 CenterY=-70 CenterZ=0 NormalX=0 NormalY=0 NormalZ=1 AngleXU=0 Radius=8
  constraints (39):
    c: Symmetric(g0,g0,g-2)
    c: Equal(g1,g0)
    c: Symmetric(g1,g1,g-2)
    c: Symmetric(g2,g2,g-1)
    c: Symmetric(g3,g3,g-1)
    c: Equal(g3,g2)
    c: Symmetric(g0,g1,g-1)
    c: Symmetric(g2,g3,g-2)
    c: Coincident(g4,g2)
    c: Tangent(g7,g0) = 1.5708
    c: Tangent(g7,g3) = -1.5708
    c: Tangent(g0,g4) = 1.5708
    c: Coincident(g5,g1)
    c: Tangent(g5,g2) = 1.5708
    c: Coincident(g3,g6)
    c: Tangent(g6,g1) = -1.5708
    c: Distance(g3,g2) = 240
    c: Radius(g4) = 5
    c: Distance(g0,g1) = 180
    c: Diameter(g8) = 16
    c: DistanceY(g8,g0) = 10
    c: DistanceX(g8,g2) = 10
    c: Equal(g9,g8)
    c: Symmetric(g9,g8,g-2)
    c: Equal(g11,g10)
    c: Equal(g10,g8)
    c: Symmetric(g10,g8,g-1)
    c: Symmetric(g11,g10,g-2)
    c: PointOnObject(g12,g-1)
    c: PointOnObject(g13,g-1)
    c: Equal(g13,g12)
    c: Equal(g12,g8)
    c: Vertical(g12,g8)
    c: Vertical(g13,g9)
    c: Equal(g15,g14)
    c: Equal(g14,g8)
    c: PointOnObject(g15,g-2)
    c: Symmetric(g15,g14,g-1)
    c: DistanceY(g14,g0) = 20
FEATURE [PartDesign::Pocket] Pocket048
  BaseFeature = -> Pocket047
  Length = 8
  Length2 = 100
  Profile = -> CopySketch019
  Reversed = true
  Type = 0
FEATURE [PartDesign::Chamfer] Chamfer009
  Base = -> Pocket048 [Edge16,Edge76]
  BaseFeature = -> Pocket048
  Size = 3
FEATURE [PartDesign::Body] Body024  label="Long_Foot_TOPL"
  Group = -> [CopySketch017,Pad036,Mirrored009,Sketch078,Pad037,Mirrored010,DatumPlane015,CopySketch018,Pocket047,CopySketch019,Pocket048,Chamfer009]
  Origin = -> Origin024
  Placement = pos=(0,0,307) rot=(1,0,0;3.14159rad)
  Tip = -> Chamfer009
FEATURE [PartDesign::Plane] DatumPlane016
  AttachmentOffset = pos=(0,0,-28) rot=(0,0,1;0rad)
  Length = 167.675
  MapMode = 5
  Placement = pos=(0,0,-28) rot=(0,0,1;0rad)
  ResizeMode = 0
  Support = -> [XY_Plane025]
  Width = 223.175
FEATURE [Sketcher::SketchObject] CopySketch020  label="SketchGround004"
  MapMode = 2
  Support = -> [XY_Plane025]
  sketch-geometry (25):
    g0: LineSegment [constr] StartX=-115 StartY=90 StartZ=0 EndX=115 EndY=90 EndZ=0
    g1: LineSegment [constr] StartX=-115 StartY=-90 StartZ=0 EndX=115 EndY=-90 EndZ=0
    g2: LineSegment [constr] StartX=120 StartY=85 StartZ=0 EndX=120 EndY=-85 EndZ=0
    g3: LineSegment [constr] StartX=-120 StartY=85 StartZ=0 EndX=-120 EndY=-85 EndZ=0
    g4: ArcOfCircle [constr] CenterX=115 CenterY=85 CenterZ=0 NormalX=0 NormalY=0 NormalZ=1 AngleXU=0 Radius=5 StartAngle=1e-15 EndAngle=1.5708
    g5: ArcOfCircle [constr] CenterX=115 CenterY=-85 CenterZ=0 NormalX=0 NormalY=0 NormalZ=1 AngleXU=0 Radius=5 StartAngle=4.71239 EndAngle=6.28319
    g6: ArcOfCircle [constr] CenterX=-115 CenterY=-85 CenterZ=0 NormalX=0 NormalY=0 NormalZ=1 AngleXU=0 Radius=5 StartAngle=3.14159 EndAngle=4.71239
    g7: ArcOfCircle [constr] CenterX=-115 CenterY=85 CenterZ=0 NormalX=0 NormalY=0 NormalZ=1 AngleXU=0 Radius=5 StartAngle=1.5708 EndAngle=3.14159
    g8: Circle [constr] CenterX=110 CenterY=80 CenterZ=0 NormalX=0 NormalY=0 NormalZ=1 AngleXU=0 Radius=3.25
    g9: Circle [constr] CenterX=-110 CenterY=80 CenterZ=0 NormalX=0 NormalY=0 NormalZ=1 AngleXU=0 Radius=3.25
    g10: Circle [constr] CenterX=110 CenterY=-80 CenterZ=0 NormalX=0 NormalY=0 NormalZ=1 AngleXU=0 Radius=3.25
    g11: Circle [constr] CenterX=-110 CenterY=-80 CenterZ=0 NormalX=0 NormalY=0 NormalZ=1 AngleXU=0 Radius=3.25
    g12: Circle [constr] CenterX=110 CenterY=0 CenterZ=0 NormalX=0 NormalY=0 NormalZ=1 AngleXU=0 Radius=3.25
    g13: Circle [constr] CenterX=-110 CenterY=0 CenterZ=0 NormalX=0 NormalY=0 NormalZ=1 AngleXU=0 Radius=3.25
    g14: Circle [constr] CenterX=0 CenterY=70 CenterZ=0 NormalX=0 NormalY=0 NormalZ=1 AngleXU=0 Radius=3.25
    g15: Circle [constr] CenterX=0 CenterY=-70 CenterZ=0 NormalX=0 NormalY=0 NormalZ=1 AngleXU=0 Radius=3.25
    g16: ArcOfCircle CenterX=115 CenterY=85 CenterZ=0 NormalX=0 NormalY=0 NormalZ=1 AngleXU=0 Radius=5.5 StartAngle=0 EndAngle=1.5708
    g17: LineSegment StartX=115 StartY=90.5 StartZ=0 EndX=105 EndY=90.5 EndZ=0
    g18: LineSegment StartX=105 StartY=95.5 StartZ=0 EndX=115 EndY=95.5 EndZ=0
    g19: ArcOfCircle CenterX=115 CenterY=85 CenterZ=0 NormalX=0 NormalY=0 NormalZ=1 AngleXU=0 Radius=10.5 StartAngle=0 EndAngle=1.5708
    g20: LineSegment StartX=120.5 StartY=85 StartZ=0 EndX=120.5 EndY=0 EndZ=0
    g21: LineSegment StartX=120.5 StartY=0 StartZ=0 EndX=125.5 EndY=0 EndZ=0
    g22: LineSegment StartX=125.5 StartY=0 StartZ=0 EndX=125.5 EndY=85 EndZ=0
    g23: ArcOfCircle CenterX=105 CenterY=85 CenterZ=0 NormalX=0 NormalY=0 NormalZ=1 AngleXU=0 Radius=10.5 StartAngle=1.5708 EndAngle=2.59028
    g24: LineSegment StartX=96.0557 StartY=90.5 StartZ=0 EndX=105 EndY=90.5 EndZ=0
  constraints (66):
    c: Symmetric(g0,g0,g-2)
    c: Equal(g1,g0)
    c: Symmetric(g1,g1,g-2)
    c: Symmetric(g2,g2,g-1)
    c: Symmetric(g3,g3,g-1)
    c: Equal(g3,g2)
    c: Symmetric(g0,g1,g-1)
    c: Symmetric(g2,g3,g-2)
    c: Coincident(g4,g2)
    c: Tangent(g7,g0) = 1.5708
    c: Tangent(g7,g3) = -1.5708
    c: Tangent(g0,g4) = 1.5708
    c: Coincident(g5,g1)
    c: Tangent(g5,g2) = 1.5708
    c: Coincident(g3,g6)
    c: Tangent(g6,g1) = -1.5708
    c: Distance(g3,g2) = 240
    c: Radius(g4) = 5
    c: Distance(g0,g1) = 180
    c: Diameter(g8) = 6.5
    c: DistanceY(g8,g0) = 10
    c: DistanceX(g8,g2) = 10
    c: Equal(g9,g8)
    c: Symmetric(g9,g8,g-2)
    c: Equal(g11,g10)
    c: Equal(g10,g8)
    c: Symmetric(g10,g8,g-1)
    c: Symmetric(g11,g10,g-2)
    c: PointOnObject(g12,g-1)
    c: PointOnObject(g13,g-1)
    c: Equal(g13,g12)
    c: Equal(g12,g8)
    c: Vertical(g12,g8)
    c: Vertical(g13,g9)
    c: Equal(g15,g14)
    c: Equal(g14,g8)
    c: PointOnObject(g15,g-2)
    c: Symmetric(g15,g14,g-1)
    c: DistanceY(g14,g0) = 20
    c: Radius(g16) = 5.5
    c: Coincident(g16,g4)
    c: Horizontal(g16,g16)
    c: Vertical(g16,g16)
    c: Horizontal(g17)
    c: DistanceX(g17,g17) = 10
    c: Coincident(g17,g16)
    c: DistanceY(g16,g18) = 5
    c: Vertical(g16,g18)
    c: Horizontal(g18)
    c: Horizontal(g19,g16)
    c: Coincident(g18,g19)
    c: Coincident(g4,g19)
    c: Vertical(g20)
    c: PointOnObject(g22,g-1)
    c: Coincident(g21,g22)
    c: PointOnObject(g20,g-1)
    c: Coincident(g21,g20)
    c: Coincident(g20,g16)
    c: Vertical(g22)
    c: Coincident(g22,g19)
    c: Vertical(g17,g18)
    c: Tangent(g23,g18) = 1.5708
    c: Equal(g19,g23)
    c: Horizontal(g23,g17)
    c: Coincident(g24,g23)
    c: Coincident(g17,g24)
FEATURE [PartDesign::Pad] Pad038
  Length = 14
  Length2 = 100
  Profile = -> CopySketch020
  Reversed = true
  Type = 0
FEATURE [Sketcher::SketchObject] CopySketch021  label="GroundSketch007"
  Placement = pos=(0,0,-28) rot=(0,0,1;0rad)
  sketch-geometry (16):
    g0: LineSegment [constr] StartX=-115 StartY=90 StartZ=0 EndX=115 EndY=90 EndZ=0
    g1: LineSegment [constr] StartX=-115 StartY=-90 StartZ=0 EndX=115 EndY=-90 EndZ=0
    g2: LineSegment [constr] StartX=120 StartY=85 StartZ=0 EndX=120 EndY=-85 EndZ=0
    g3: LineSegment [constr] StartX=-120 StartY=85 StartZ=0 EndX=-120 EndY=-85 EndZ=0
    g4: ArcOfCircle [constr] CenterX=115 CenterY=85 CenterZ=0 NormalX=0 NormalY=0 NormalZ=1 AngleXU=0 Radius=5 StartAngle=-9e-16 EndAngle=1.5708
    g5: ArcOfCircle [constr] CenterX=115 CenterY=-85 CenterZ=0 NormalX=0 NormalY=0 NormalZ=1 AngleXU=0 Radius=5 StartAngle=4.71239 EndAngle=6.28319
    g6: ArcOfCircle [constr] CenterX=-115 CenterY=-85 CenterZ=0 NormalX=0 NormalY=0 NormalZ=1 AngleXU=0 Radius=5 StartAngle=3.14159 EndAngle=4.71239
    g7: ArcOfCircle [constr] CenterX=-115 CenterY=85 CenterZ=0 NormalX=0 NormalY=0 NormalZ=1 AngleXU=0 Radius=5 StartAngle=1.5708 EndAngle=3.14159
    g8: Circle CenterX=110 CenterY=80 CenterZ=0 NormalX=0 NormalY=0 NormalZ=1 AngleXU=0 Radius=3.25
    g9: Circle [constr] CenterX=-110 CenterY=80 CenterZ=0 NormalX=0 NormalY=0 NormalZ=1 AngleXU=0 Radius=3.25
    g10: Circle CenterX=110 CenterY=-80 CenterZ=0 NormalX=0 NormalY=0 NormalZ=1 AngleXU=0 Radius=3.25
    g11: Circle [constr] CenterX=-110 CenterY=-80 CenterZ=0 NormalX=0 NormalY=0 NormalZ=1 AngleXU=0 Radius=3.25
    g12: Circle CenterX=110 CenterY=0 CenterZ=0 NormalX=0 NormalY=0 NormalZ=1 AngleXU=0 Radius=3.25
    g13: Circle [constr] CenterX=-110 CenterY=0 CenterZ=0 NormalX=0 NormalY=0 NormalZ=1 AngleXU=0 Radius=3.25
    g14: Circle [constr] CenterX=0 CenterY=70 CenterZ=0 NormalX=0 NormalY=0 NormalZ=1 AngleXU=0 Radius=3.25
    g15: Circle [constr] CenterX=0 CenterY=-70 CenterZ=0 NormalX=0 NormalY=0 NormalZ=1 AngleXU=0 Radius=3.25
  constraints (39):
    c: Symmetric(g0,g0,g-2)
    c: Equal(g1,g0)
    c: Symmetric(g1,g1,g-2)
    c: Symmetric(g2,g2,g-1)
    c: Symmetric(g3,g3,g-1)
    c: Equal(g3,g2)
    c: Symmetric(g0,g1,g-1)
    c: Symmetric(g2,g3,g-2)
    c: Coincident(g4,g2)
    c: Tangent(g7,g0) = 1.5708
    c: Tangent(g7,g3) = -1.5708
    c: Tangent(g0,g4) = 1.5708
    c: Coincident(g5,g1)
    c: Tangent(g5,g2) = 1.5708
    c: Coincident(g3,g6)
    c: Tangent(g6,g1) = -1.5708
    c: Distance(g3,g2) = 240
    c: Radius(g4) = 5
    c: Distance(g0,g1) = 180
    c: Diameter(g8) = 6.5
    c: DistanceY(g8,g0) = 10
    c: DistanceX(g8,g2) = 10
    c: Equal(g9,g8)
    c: Symmetric(g9,g8,g-2)
    c: Equal(g11,g10)
    c: Equal(g10,g8)
    c: Symmetric(g10,g8,g-1)
    c: Symmetric(g11,g10,g-2)
    c: PointOnObject(g12,g-1)
    c: PointOnObject(g13,g-1)
    c: Equal(g13,g12)
    c: Equal(g12,g8)
    c: Vertical(g12,g8)
    c: Vertical(g13,g9)
    c: Equal(g15,g14)
    c: Equal(g14,g8)
    c: PointOnObject(g15,g-2)
    c: Symmetric(g15,g14,g-1)
    c: DistanceY(g14,g0) = 20
FEATURE [Sketcher::SketchObject] CopySketch022  label="GroundSketch008"
  Placement = pos=(0,0,-28) rot=(0,0,1;0rad)
  sketch-geometry (16):
    g0: LineSegment [constr] StartX=-115 StartY=90 StartZ=0 EndX=115 EndY=90 EndZ=0
    g1: LineSegment [constr] StartX=-115 StartY=-90 StartZ=0 EndX=115 EndY=-90 EndZ=0
    g2: LineSegment [constr] StartX=120 StartY=85 StartZ=0 EndX=120 EndY=-85 EndZ=0
    g3: LineSegment [constr] StartX=-120 StartY=85 StartZ=0 EndX=-120 EndY=-85 EndZ=0
    g4: ArcOfCircle [constr] CenterX=115 CenterY=85 CenterZ=0 NormalX=0 NormalY=0 NormalZ=1 AngleXU=0 Radius=5 StartAngle=-9e-16 EndAngle=1.5708
    g5: ArcOfCircle [constr] CenterX=115 CenterY=-85 CenterZ=0 NormalX=0 NormalY=0 NormalZ=1 AngleXU=0 Radius=5 StartAngle=4.71239 EndAngle=6.28319
    g6: ArcOfCircle [constr] CenterX=-115 CenterY=-85 CenterZ=0 NormalX=0 NormalY=0 NormalZ=1 AngleXU=0 Radius=5 StartAngle=3.14159 EndAngle=4.71239
    g7: ArcOfCircle [constr] CenterX=-115 CenterY=85 CenterZ=0 NormalX=0 NormalY=0 NormalZ=1 AngleXU=0 Radius=5 StartAngle=1.5708 EndAngle=3.14159
    g8: Circle CenterX=110 CenterY=80 CenterZ=0 NormalX=0 NormalY=0 NormalZ=1 AngleXU=0 Radius=8
    g9: Circle [constr] CenterX=-110 CenterY=80 CenterZ=0 NormalX=0 NormalY=0 NormalZ=1 AngleXU=0 Radius=8
    g10: Circle CenterX=110 CenterY=-80 CenterZ=0 NormalX=0 NormalY=0 NormalZ=1 AngleXU=0 Radius=8
    g11: Circle [constr] CenterX=-110 CenterY=-80 CenterZ=0 NormalX=0 NormalY=0 NormalZ=1 AngleXU=0 Radius=8
    g12: Circle CenterX=110 CenterY=0 CenterZ=0 NormalX=0 NormalY=0 NormalZ=1 AngleXU=0 Radius=8
    g13: Circle [constr] CenterX=-110 CenterY=0 CenterZ=0 NormalX=0 NormalY=0 NormalZ=1 AngleXU=0 Radius=8
    g14: Circle [constr] CenterX=0 CenterY=70 CenterZ=0 NormalX=0 NormalY=0 NormalZ=1 AngleXU=0 Radius=8
    g15: Circle [constr] CenterX=0 CenterY=-70 CenterZ=0 NormalX=0 NormalY=0 NormalZ=1 AngleXU=0 Radius=8
  constraints (39):
    c: Symmetric(g0,g0,g-2)
    c: Equal(g1,g0)
    c: Symmetric(g1,g1,g-2)
    c: Symmetric(g2,g2,g-1)
    c: Symmetric(g3,g3,g-1)
    c: Equal(g3,g2)
    c: Symmetric(g0,g1,g-1)
    c: Symmetric(g2,g3,g-2)
    c: Coincident(g4,g2)
    c: Tangent(g7,g0) = 1.5708
    c: Tangent(g7,g3) = -1.5708
    c: Tangent(g0,g4) = 1.5708
    c: Coincident(g5,g1)
    c: Tangent(g5,g2) = 1.5708
    c: Coincident(g3,g6)
    c: Tangent(g6,g1) = -1.5708
    c: Distance(g3,g2) = 240
    c: Radius(g4) = 5
    c: Distance(g0,g1) = 180
    c: Diameter(g8) = 16
    c: DistanceY(g8,g0) = 10
    c: DistanceX(g8,g2) = 10
    c: Equal(g9,g8)
    c: Symmetric(g9,g8,g-2)
    c: Equal(g11,g10)
    c: Equal(g10,g8)
    c: Symmetric(g10,g8,g-1)
    c: Symmetric(g11,g10,g-2)
    c: PointOnObject(g12,g-1)
    c: PointOnObject(g13,g-1)
    c: Equal(g13,g12)
    c: Equal(g12,g8)
    c: Vertical(g12,g8)
    c: Vertical(g13,g9)
    c: Equal(g15,g14)
    c: Equal(g14,g8)
    c: PointOnObject(g15,g-2)
    c: Symmetric(g15,g14,g-1)
    c: DistanceY(g14,g0) = 20
FEATURE [PartDesign::Mirrored] Mirrored012
  BaseFeature = -> Pad038
  MirrorPlane = -> CopySketch020 [H_Axis]
  Originals = -> [Pad038]
FEATURE [Sketcher::SketchObject] Sketch079
  MapMode = 5
  Placement = pos=(0,0,-14) rot=(1,0,0;3.14159rad)
  Support = -> [Mirrored012]
  expr: Constraints[17] = CopySketch020.Constraints[17]
  expr: Constraints[38] = CopySketch020.Constraints[38]
  expr: Constraints[21] = CopySketch020.Constraints[21]
  expr: Constraints[20] = CopySketch020.Constraints[20]
  expr: Constraints[19] = CopySketch020.Constraints[19]
  expr: Constraints[18] = CopySketch020.Constraints[18]
  expr: Constraints[16] = CopySketch020.Constraints[16]
  sketch-geometry (23):
    g0: LineSegment [constr] StartX=-115 StartY=90 StartZ=0 EndX=115 EndY=90 EndZ=0
    g1: LineSegment [constr] StartX=-115 StartY=-90 StartZ=0 EndX=115 EndY=-90 EndZ=0
    g2: LineSegment [constr] StartX=120 StartY=85 StartZ=0 EndX=120 EndY=-85 EndZ=0
    g3: LineSegment [constr] StartX=-120 StartY=85 StartZ=0 EndX=-120 EndY=-85 EndZ=0
    g4: ArcOfCircle [constr] CenterX=115 CenterY=85 CenterZ=0 NormalX=0 NormalY=0 NormalZ=1 AngleXU=0 Radius=5 StartAngle=-8.8418e-12 EndAngle=1.5708
    g5: ArcOfCircle [constr] CenterX=115 CenterY=-85 CenterZ=0 NormalX=0 NormalY=0 NormalZ=1 AngleXU=0 Radius=5 StartAngle=4.71239 EndAngle=6.28319
    g6: ArcOfCircle [constr] CenterX=-115 CenterY=-85 CenterZ=0 NormalX=0 NormalY=0 NormalZ=1 AngleXU=0 Radius=5 StartAngle=3.14159 EndAngle=4.71239
    g7: ArcOfCircle [constr] CenterX=-115 CenterY=85 CenterZ=0 NormalX=0 NormalY=0 NormalZ=1 AngleXU=0 Radius=5 StartAngle=1.5708 EndAngle=3.14159
    g8: Circle [constr] CenterX=110 CenterY=80 CenterZ=0 NormalX=0 NormalY=0 NormalZ=1 AngleXU=0 Radius=3.25
    g9: Circle [constr] CenterX=-110 CenterY=80 CenterZ=0 NormalX=0 NormalY=0 NormalZ=1 AngleXU=0 Radius=3.25
    g10: Circle [constr] CenterX=110 CenterY=-80 CenterZ=0 NormalX=0 NormalY=0 NormalZ=1 AngleXU=0 Radius=3.25
    g11: Circle [constr] CenterX=-110 CenterY=-80 CenterZ=0 NormalX=0 NormalY=0 NormalZ=1 AngleXU=0 Radius=3.25
    g12: Circle [constr] CenterX=110 CenterY=0 CenterZ=0 NormalX=0 NormalY=0 NormalZ=1 AngleXU=0 Radius=3.25
    g13: Circle [constr] CenterX=-110 CenterY=0 CenterZ=0 NormalX=0 NormalY=0 NormalZ=1 AngleXU=0 Radius=3.25
    g14: Circle [constr] CenterX=0 CenterY=70 CenterZ=0 NormalX=0 NormalY=0 NormalZ=1 AngleXU=0 Radius=3.25
    g15: Circle [constr] CenterX=0 CenterY=-70 CenterZ=0 NormalX=0 NormalY=0 NormalZ=1 AngleXU=0 Radius=3.25
    g16: LineSegment StartX=105 StartY=95.5 StartZ=0 EndX=115 EndY=95.5 EndZ=0
    g17: ArcOfCircle CenterX=115 CenterY=85 CenterZ=0 NormalX=0 NormalY=0 NormalZ=1 AngleXU=0 Radius=10.5 StartAngle=-2.31e-14 EndAngle=1.5708
    g18: LineSegment StartX=94.5 StartY=0 StartZ=0 EndX=125.5 EndY=0 EndZ=0
    g19: LineSegment StartX=125.5 StartY=0 StartZ=0 EndX=125.5 EndY=85 EndZ=0
    g20: LineSegment StartX=94.5 StartY=85 StartZ=0 EndX=94.5 EndY=0 EndZ=0
    g21: LineSegment [constr] StartX=110 StartY=80 StartZ=0 EndX=110 EndY=95.5 EndZ=0
    g22: ArcOfCircle CenterX=105 CenterY=85 CenterZ=0 NormalX=0 NormalY=0 NormalZ=1 AngleXU=0 Radius=10.5 StartAngle=1.5708 EndAngle=3.14159
  constraints (59):
    c: Symmetric(g0,g0,g-2)
    c: Equal(g1,g0)
    c: Symmetric(g1,g1,g-2)
    c: Symmetric(g2,g2,g-1)
    c: Symmetric(g3,g3,g-1)
    c: Equal(g3,g2)
    c: Symmetric(g0,g1,g-1)
    c: Symmetric(g2,g3,g-2)
    c: Coincident(g4,g2)
    c: Tangent(g7,g0) = 1.5708
    c: Tangent(g7,g3) = -1.5708
    c: Tangent(g0,g4) = 1.5708
    c: Coincident(g5,g1)
    c: Tangent(g5,g2) = 1.5708
    c: Coincident(g3,g6)
    c: Tangent(g6,g1) = -1.5708
    c: Distance(g3,g2) = 240
    c: Radius(g4) = 5
    c: Distance(g0,g1) = 180
    c: Diameter(g8) = 6.5
    c: DistanceY(g8,g0) = 10
    c: DistanceX(g8,g2) = 10
    c: Equal(g9,g8)
    c: Symmetric(g9,g8,g-2)
    c: Equal(g11,g10)
    c: Equal(g10,g8)
    c: Symmetric(g10,g8,g-1)
    c: Symmetric(g11,g10,g-2)
    c: PointOnObject(g12,g-1)
    c: PointOnObject(g13,g-1)
    c: Equal(g13,g12)
    c: Equal(g12,g8)
    c: Vertical(g12,g8)
    c: Vertical(g13,g9)
    c: Equal(g15,g14)
    c: Equal(g14,g8)
    c: PointOnObject(g15,g-2)
    c: Symmetric(g15,g14,g-1)
    c: DistanceY(g14,g0) = 20
    c: Horizontal(g16)
    c: PointOnObject(g19,g-1)
    c: Coincident(g18,g19)
    c: Vertical(g19)
    c: Horizontal(g17,g20)
    c: Tangent(g19,g17) = -1.5708
    c: DistanceX(g2,g17) = 5.5
    c: Tangent(g16,g17) = 1.5708
    c: Vertical(g16,g0)
    c: Horizontal(g2,g17)
    c: Vertical(g20,g18)
    c: PointOnObject(g18,g-1)
    c: Coincident(g20,g18)
    c: Coincident(g21,g8)
    c: PointOnObject(g21,g16)
    c: Symmetric(g16,g16,g21)
    c: Vertical(g22,g22)
    c: Horizontal(g22,g22)
    c: Coincident(g16,g22)
    c: Coincident(g22,g20)
FEATURE [PartDesign::Pad] Pad039
  BaseFeature = -> Mirrored012
  Length = 14
  Length2 = 100
  Profile = -> Sketch079
  Type = 0
FEATURE [PartDesign::Mirrored] Mirrored011
  BaseFeature = -> Pad039
  MirrorPlane = -> Sketch079 [H_Axis]
  Originals = -> [Pad039]
FEATURE [PartDesign::Pocket] Pocket050
  BaseFeature = -> Mirrored011
  Length = 9
  Length2 = 100
  Profile = -> CopySketch021
  Reversed = true
  Type = 1
FEATURE [PartDesign::Pocket] Pocket049
  BaseFeature = -> Pocket050
  Length = 8
  Length2 = 100
  Profile = -> CopySketch022
  Reversed = true
  Type = 0
FEATURE [PartDesign::Chamfer] Chamfer010
  Base = -> Pocket049 [Edge16,Edge76]
  BaseFeature = -> Pocket049
  Size = 3
FEATURE [PartDesign::Body] Body025  label="Long_Foot_TOPL001"
  Group = -> [CopySketch020,Pad038,Mirrored012,Sketch079,Pad039,Mirrored011,DatumPlane016,CopySketch021,Pocket050,CopySketch022,Pocket049,Chamfer010]
  Origin = -> Origin025
  Placement = pos=(0,0,307) rot=(0,1,0;3.14159rad)
  Tip = -> Chamfer010
FEATURE [Sketcher::SketchObject] Sketch080
  MapMode = 5
  Placement = pos=(0,0,0) rot=(1,0,0;1.5708rad)
  Support = -> [XZ_Plane026]
  sketch-geometry (6):
    g0: Circle CenterX=0 CenterY=0 CenterZ=0 NormalX=0 NormalY=0 NormalZ=1 AngleXU=0 Radius=22.5
    g1: LineSegment [constr] StartX=-19.6929 StartY=19.6929 StartZ=0 EndX=19.6929 EndY=19.6929 EndZ=0
    g2: LineSegment [constr] StartX=19.6929 StartY=19.6929 StartZ=0 EndX=19.6929 EndY=-19.6929 EndZ=0
    g3: LineSegment [constr] StartX=19.6929 StartY=-19.6929 StartZ=0 EndX=-19.6929 EndY=-19.6929 EndZ=0
    g4: LineSegment [constr] StartX=-19.6929 StartY=-19.6929 StartZ=0 EndX=-19.6929 EndY=19.6929 EndZ=0
    g5: Circle CenterX=0 CenterY=0 CenterZ=0 NormalX=0 NormalY=0 NormalZ=1 AngleXU=0 Radius=35
  constraints (14):
    c: Coincident(g0,g-1)
    c: Diameter(g0) = 45
    c: Coincident(g1,g2)
    c: Coincident(g2,g3)
    c: Coincident(g3,g4)
    c: Coincident(g4,g1)
    c: Horizontal(g1)
    c: Vertical(g4)
    c: Symmetric(g2,g3,g-2)
    c: Symmetric(g2,g1,g-1)
    c: Equal(g3,g2)
    c: Distance(g0,g1) = 27.85
    c: Coincident(g5,g0)
    c: Diameter(g5) = 70
FEATURE [PartDesign::Pad] Pad040
  Length = 6
  Length2 = 100
  Placement = pos=(0,0,0) rot=(1,0,0;1.5708rad)
  Profile = -> Sketch080
  Type = 0
FEATURE [Sketcher::SketchObject] Sketch081
  MapMode = 5
  Placement = pos=(0,0,0) rot=(-1,0,0;1.5708rad)
  Support = -> [Pad040]
  sketch-geometry (8):
    g0: LineSegment [constr] StartX=-19.6929 StartY=19.6929 StartZ=0 EndX=19.6929 EndY=19.6929 EndZ=0
    g1: LineSegment [constr] StartX=19.6929 StartY=19.6929 StartZ=0 EndX=19.6929 EndY=-19.6929 EndZ=0
    g2: LineSegment [constr] StartX=19.6929 StartY=-19.6929 StartZ=0 EndX=-19.6929 EndY=-19.6929 EndZ=0
    g3: LineSegment [constr] StartX=-19.6929 StartY=-19.6929 StartZ=0 EndX=-19.6929 EndY=19.6929 EndZ=0
    g4: Circle CenterX=-19.6929 CenterY=19.6929 CenterZ=0 NormalX=0 NormalY=0 NormalZ=1 AngleXU=0 Radius=1.75
    g5: Circle CenterX=19.6929 CenterY=19.6929 CenterZ=0 NormalX=0 NormalY=0 NormalZ=1 AngleXU=0 Radius=1.75
    g6: Circle CenterX=19.6929 CenterY=-19.6929 CenterZ=0 NormalX=0 NormalY=0 NormalZ=1 AngleXU=0 Radius=1.75
    g7: Circle CenterX=-19.6929 CenterY=-19.6929 CenterZ=0 NormalX=0 NormalY=0 NormalZ=1 AngleXU=0 Radius=1.75
  constraints (18):
    c: Coincident(g0,g1)
    c: Coincident(g1,g2)
    c: Coincident(g2,g3)
    c: Coincident(g3,g0)
    c: Horizontal(g2)
    c: Vertical(g3)
    c: Symmetric(g1,g0,g-1)
    c: Symmetric(g0,g0,g-2)
    c: Equal(g0,g1)
    c: Distance(g-1,g0) = 27.85
    c: Coincident(g4,g0)
    c: Coincident(g5,g0)
    c: Coincident(g6,g1)
    c: Coincident(g7,g2)
    c: Equal(g6,g5)
    c: Equal(g5,g4)
    c: Equal(g4,g7)
    c: Diameter(g5) = 3.5
FEATURE [PartDesign::Pocket] Pocket051
  BaseFeature = -> Pad040
  Length = 5
  Length2 = 100
  Placement = pos=(0,0,0) rot=(1,0,0;1.5708rad)
  Profile = -> Sketch081
  Type = 1
FEATURE [Sketcher::SketchObject] Sketch082
  ExternalGeometry = -> [Pocket051]
  MapMode = 5
  Placement = pos=(0,-6,-1.3e-15) rot=(1,0,0;1.5708rad)
  Support = -> [Pocket051]
  sketch-geometry (4):
    g0: Circle CenterX=-19.6929 CenterY=19.6929 CenterZ=0 NormalX=0 NormalY=0 NormalZ=1 AngleXU=0 Radius=2.9
    g1: Circle CenterX=19.6929 CenterY=19.6929 CenterZ=0 NormalX=0 NormalY=0 NormalZ=1 AngleXU=0 Radius=2.9
    g2: Circle CenterX=19.6929 CenterY=-19.6929 CenterZ=0 NormalX=0 NormalY=0 NormalZ=1 AngleXU=0 Radius=2.9
    g3: Circle CenterX=-19.6929 CenterY=-19.6929 CenterZ=0 NormalX=0 NormalY=0 NormalZ=1 AngleXU=0 Radius=2.9
  constraints (8):
    c: Coincident(g0,g-3)
    c: Coincident(g1,g-4)
    c: Coincident(g2,g-5)
    c: Coincident(g3,g-6)
    c: Equal(g3,g0)
    c: Equal(g0,g1)
    c: Equal(g1,g2)
    c: Diameter(g1) = 5.8
FEATURE [PartDesign::Pocket] Pocket052
  BaseFeature = -> Pocket051
  Length = 3
  Length2 = 100
  Placement = pos=(0,0,0) rot=(1,0,0;1.5708rad)
  Profile = -> Sketch082
  Type = 0
FEATURE [Sketcher::SketchObject] Sketch083
  MapMode = 5
  Support = -> [XY_Plane026]
  sketch-geometry (4):
    g0: ArcOfCircle CenterX=-5e-16 CenterY=67.101 CenterZ=0 NormalX=0 NormalY=0 NormalZ=1 AngleXU=0 Radius=80 StartAngle=4.29404 EndAngle=5.13074
    g1: LineSegment StartX=-32.5 StartY=-6 StartZ=0 EndX=-22.5 EndY=-6 EndZ=0
    g2: LineSegment StartX=32.5 StartY=-6 StartZ=0 EndX=22.5 EndY=-6 EndZ=0
    g3: ArcOfCircle CenterX=1.33e-14 CenterY=70.7708 CenterZ=0 NormalX=0 NormalY=0 NormalZ=1 AngleXU=0 Radius=80 StartAngle=4.42729 EndAngle=4.99749
  constraints (12):
    c: Coincident(g1,g0)
    c: Horizontal(g1)
    c: Coincident(g2,g0)
    c: DistanceX(g0,g0) = 65
    c: DistanceX(g1,g2) = 45
    c: DistanceY(g0,g-1) = 6
    c: Symmetric(g0,g0,g-2)
    c: Symmetric(g2,g1,g-2)
    c: Diameter(g0) = 160
    c: Coincident(g3,g2)
    c: Coincident(g3,g1)
    c: Diameter(g3) = 160
FEATURE [PartDesign::Pad] Pad041
  BaseFeature = -> Pocket052
  Length = 8
  Length2 = 100
  Midplane = true
  Placement = pos=(0,0,0) rot=(1,0,0;1.5708rad)
  Profile = -> Sketch083
  Type = 0
FEATURE [PartDesign::Chamfer] Chamfer011
  Base = -> Pad041 [Edge3]
  BaseFeature = -> Pad041
  Placement = pos=(0,0,0) rot=(1,0,0;1.5708rad)
  Size = 2
FEATURE [PartDesign::Body] Body026  label="TweeterBlende"
  Group = -> [Sketch080,Pad040,Sketch081,Pocket051,Sketch082,Pocket052,Sketch083,Pad041,Chamfer011]
  Origin = -> Origin026
  Placement = pos=(-50,-91,254) rot=(0,0,1;0rad)
  Tip = -> Chamfer011
FEATURE [Sketcher::SketchObject] Sketch084
  MapMode = 5
  Placement = pos=(0,0,0) rot=(0.57735,0.57735,0.57735;2.0944rad)
  Support = -> [YZ_Plane027]
  sketch-geometry (20):
    g0: LineSegment StartX=-90 StartY=0 StartZ=0 EndX=90 EndY=0 EndZ=0
    g1: LineSegment StartX=-90 StartY=0 StartZ=0 EndX=-90 EndY=5 EndZ=0
    g2: LineSegment StartX=-90 StartY=5 StartZ=0 EndX=-84 EndY=5 EndZ=0
    g3: LineSegment StartX=-84 StartY=5 StartZ=0 EndX=-84 EndY=35 EndZ=0
    g4: LineSegment StartX=-84 StartY=35 StartZ=0 EndX=-78 EndY=35 EndZ=0
    g5: LineSegment StartX=-78 StartY=35 StartZ=0 EndX=-78 EndY=5 EndZ=0
    g6: LineSegment StartX=-78 StartY=5 StartZ=0 EndX=-62 EndY=5 EndZ=0
    g7: LineSegment StartX=-62 StartY=5 StartZ=0 EndX=-62 EndY=35 EndZ=0
    g8: LineSegment StartX=-62 StartY=35 StartZ=0 EndX=-56 EndY=35 EndZ=0
    g9: LineSegment StartX=-56 StartY=35 StartZ=0 EndX=-56 EndY=5 EndZ=0
    g10: LineSegment StartX=-56 StartY=5 StartZ=0 EndX=56 EndY=5 EndZ=0
    g11: LineSegment StartX=56 StartY=5 StartZ=0 EndX=56 EndY=35 EndZ=0
    g12: LineSegment StartX=56 StartY=35 StartZ=0 EndX=62 EndY=35 EndZ=0
    g13: LineSegment StartX=62 StartY=35 StartZ=0 EndX=62 EndY=5 EndZ=0
    g14: LineSegment StartX=62 StartY=5 StartZ=0 EndX=78 EndY=5 EndZ=0
    g15: LineSegment StartX=78 StartY=5 StartZ=0 EndX=78 EndY=35 EndZ=0
    g16: LineSegment StartX=78 StartY=35 StartZ=0 EndX=84 EndY=35 EndZ=0
    g17: LineSegment StartX=84 StartY=35 StartZ=0 EndX=84 EndY=5 EndZ=0
    g18: LineSegment StartX=84 StartY=5 StartZ=0 EndX=90 EndY=5 EndZ=0
    g19: LineSegment StartX=90 StartY=5 StartZ=0 EndX=90 EndY=0 EndZ=0
  constraints (58):
    c: PointOnObject(g0,g-1)
    c: Symmetric(g0,g0,g-2)
    c: DistanceX(g0,g0) = 180
    c: Coincident(g1,g0)
    c: Vertical(g1)
    c: Coincident(g2,g1)
    c: Horizontal(g2)
    c: Coincident(g3,g2)
    c: Vertical(g3)
    c: Coincident(g4,g3)
    c: Horizontal(g4)
    c: Coincident(g5,g4)
    c: Vertical(g5)
    c: Coincident(g6,g5)
    c: Horizontal(g6)
    c: Coincident(g7,g6)
    c: Vertical(g7)
    c: Coincident(g8,g7)
    c: Horizontal(g8)
    c: Coincident(g9,g8)
    c: Vertical(g9)
    c: Coincident(g10,g9)
    c: Coincident(g11,g10)
    c: Vertical(g11)
    c: Coincident(g12,g11)
    c: Horizontal(g12)
    c: Coincident(g13,g12)
    c: Vertical(g13)
    c: Coincident(g14,g13)
    c: Horizontal(g14)
    c: Coincident(g15,g14)
    c: Vertical(g15)
    c: Coincident(g16,g15)
    c: Horizontal(g16)
    c: Coincident(g17,g16)
    c: Vertical(g17)
    c: Coincident(g18,g17)
    c: Horizontal(g18)
    c: Coincident(g19,g18)
    c: Coincident(g19,g0)
    c: Vertical(g19)
    c: Symmetric(g10,g9,g-2)
    c: Horizontal(g17,g13)
    c: Horizontal(g13,g9)
    c: Horizontal(g9,g5)
    c: Horizontal(g5,g1)
    c: DistanceY(g19,g19) = 5
    c: Horizontal(g16,g12)
    c: Horizontal(g12,g8)
    c: Horizontal(g8,g4)
    c: Equal(g16,g12)
    c: Equal(g12,g8)
    c: Equal(g8,g4)
    c: Equal(g14,g6)
    c: DistanceX(g14,g14) = 16
    c: DistanceX(g16,g16) = 6
    c: DistanceY(g17,g17) = 30
    c: DistanceX(g14,g18) = 12
FEATURE [PartDesign::Pad] Pad042
  Length = 36
  Length2 = 100
  Midplane = true
  Placement = pos=(0,0,0) rot=(0.57735,0.57735,0.57735;2.0944rad)
  Profile = -> Sketch084
  Reversed = true
  Type = 0
FEATURE [Sketcher::SketchObject] Sketch085
  MapMode = 5
  Placement = pos=(0,0,4e-16) rot=(0.707107,0.707107,0;3.14159rad)
  Support = -> [Pad042]
  sketch-geometry (2):
    g0: Circle CenterX=-70 CenterY=0 CenterZ=0 NormalX=0 NormalY=0 NormalZ=1 AngleXU=0 Radius=3.25
    g1: Circle CenterX=70 CenterY=0 CenterZ=0 NormalX=0 NormalY=0 NormalZ=1 AngleXU=0 Radius=3.25
  constraints (5):
    c: Equal(g1,g0)
    c: Symmetric(g0,g1,g-2)
    c: DistanceX(g0,g1) = 140
    c: Diameter(g1) = 6.5
    c: PointOnObject(g1,g-1)
FEATURE [PartDesign::Pocket] Pocket053
  BaseFeature = -> Pad042
  Length = 5
  Length2 = 100
  Placement = pos=(0,0,0) rot=(0.57735,0.57735,0.57735;2.0944rad)
  Profile = -> Sketch085
  Type = 1
FEATURE [Sketcher::SketchObject] Sketch086
  MapMode = 5
  Placement = pos=(0,0,0) rot=(1,0,0;1.5708rad)
  Support = -> [XZ_Plane027]
  sketch-geometry (11):
    g0: Circle [constr] CenterX=0 CenterY=25 CenterZ=0 NormalX=0 NormalY=0 NormalZ=1 AngleXU=0 Radius=10
    g1: LineSegment StartX=-23 StartY=5 StartZ=0 EndX=-23 EndY=40 EndZ=0
    g2: LineSegment StartX=-23 StartY=40 StartZ=0 EndX=23 EndY=40 EndZ=0
    g3: LineSegment StartX=23 StartY=40 StartZ=0 EndX=23 EndY=5 EndZ=0
    g4: LineSegment StartX=23 StartY=5 StartZ=0 EndX=18 EndY=5 EndZ=0
    g5: LineSegment StartX=18 StartY=5 StartZ=0 EndX=10 EndY=13 EndZ=0
    g6: LineSegment StartX=10 StartY=13 StartZ=0 EndX=10 EndY=25 EndZ=0
    g7: LineSegment StartX=-10 StartY=25 StartZ=0 EndX=-10 EndY=13 EndZ=0
    g8: LineSegment StartX=-10 StartY=13 StartZ=0 EndX=-18 EndY=5 EndZ=0
    g9: LineSegment StartX=-18 StartY=5 StartZ=0 EndX=-23 EndY=5 EndZ=0
    g10: ArcOfCircle CenterX=0 CenterY=25 CenterZ=0 NormalX=0 NormalY=0 NormalZ=1 AngleXU=0 Radius=10 StartAngle=0 EndAngle=3.14159
  constraints (30):
    c: PointOnObject(g0,g-2)
    c: Diameter(g0) = 20
    c: DistanceY(g-1,g0) = 25
    c: Vertical(g1)
    c: Coincident(g2,g1)
    c: Horizontal(g2)
    c: Coincident(g3,g2)
    c: Vertical(g3)
    c: Coincident(g4,g3)
    c: Horizontal(g4)
    c: Coincident(g5,g4)
    c: Coincident(g6,g5)
    c: Vertical(g6)
    c: Vertical(g7)
    c: Coincident(g8,g7)
    c: Coincident(g9,g1)
    c: Coincident(g9,g8)
    c: Horizontal(g9)
    c: Symmetric(g8,g4,g-2)
    c: DistanceX(g8,g4) = 36
    c: DistanceY(g-1,g3) = 5
    c: Symmetric(g5,g7,g-2)
    c: DistanceY(g3,g5) = 8
    c: Tangent(g6,g0) = -1.5708
    c: Equal(g4,g9)
    c: DistanceX(g4,g4) = 5
    c: DistanceY(g3,g3) = 35
    c: Coincident(g10,g6)
    c: Coincident(g10,g7)
    c: Coincident(g10,g0)
FEATURE [PartDesign::Pocket] Pocket054
  BaseFeature = -> Pocket053
  Length = 5
  Length2 = 100
  Midplane = true
  Placement = pos=(0,0,0) rot=(0.57735,0.57735,0.57735;2.0944rad)
  Profile = -> Sketch086
  Type = 1
FEATURE [Sketcher::SketchObject] Sketch087
  ExternalGeometry = -> [Pocket054]
  MapMode = 5
  Placement = pos=(0,0,0) rot=(1,0,0;1.5708rad)
  Support = -> [XZ_Plane027]
  sketch-geometry (1):
    g0: Circle CenterX=0 CenterY=25 CenterZ=0 NormalX=0 NormalY=0 NormalZ=1 AngleXU=0 Radius=3.25
  constraints (2):
    c: Coincident(g0,g-3)
    c: Diameter(g0) = 6.5
FEATURE [PartDesign::Pocket] Pocket055
  BaseFeature = -> Pocket054
  Length = 5
  Length2 = 100
  Midplane = true
  Placement = pos=(0,0,0) rot=(0.57735,0.57735,0.57735;2.0944rad)
  Profile = -> Sketch087
  Type = 1
FEATURE [PartDesign::Fillet] Fillet006
  Base = -> Pocket055 [Edge45,Edge54,Edge30,Edge44,Edge35,Edge7]
  BaseFeature = -> Pocket055
  Placement = pos=(0,0,0) rot=(0.57735,0.57735,0.57735;2.0944rad)
  Radius = 2
FEATURE [PartDesign::Body] Body027  label="GriffHalter"
  Group = -> [Sketch084,Pad042,Sketch085,Pocket053,Sketch086,Pocket054,Sketch087,Pocket055,Fillet006]
  Origin = -> Origin027
  Placement = pos=(0,0,321) rot=(0,0,1;0rad)
  Tip = -> Fillet006
FEATURE [Sketcher::SketchObject] Sketch088
  MapMode = 5
  Support = -> [XY_Plane028]
  sketch-geometry (1):
    g0: Circle CenterX=0 CenterY=0 CenterZ=0 NormalX=0 NormalY=0 NormalZ=1 AngleXU=0 Radius=10
  constraints (2):
    c: Coincident(g0,g-1)
    c: Diameter(g0) = 20
FEATURE [PartDesign::Pad] Pad043
  Length = 20
  Length2 = 100
  Profile = -> Sketch088
  Type = 0
FEATURE [Sketcher::SketchObject] Sketch089
  MapMode = 5
  Placement = pos=(0,0,0) rot=(1,0,0;3.14159rad)
  Support = -> [Pad043]
  sketch-geometry (1):
    g0: Circle CenterX=0 CenterY=0 CenterZ=0 NormalX=0 NormalY=0 NormalZ=1 AngleXU=0 Radius=6.5
  constraints (2):
    c: Coincident(g0,g-1)
    c: Diameter(g0) = 13
FEATURE [PartDesign::Pocket] Pocket056
  BaseFeature = -> Pad043
  Length = 5
  Length2 = 100
  Profile = -> Sketch089
  Type = 0
FEATURE [Sketcher::SketchObject] Sketch090
  MapMode = 5
  Placement = pos=(0,0,5) rot=(1,0,0;3.14159rad)
  Support = -> [Pocket056]
  sketch-geometry (1):
    g0: Circle CenterX=0 CenterY=0 CenterZ=0 NormalX=0 NormalY=0 NormalZ=1 AngleXU=0 Radius=3.125
  constraints (2):
    c: Coincident(g0,g-1)
    c: Diameter(g0) = 6.25
FEATURE [PartDesign::Pocket] Pocket057
  BaseFeature = -> Pocket056
  Length = 10
  Length2 = 100
  Profile = -> Sketch090
  Type = 0
FEATURE [PartDesign::Chamfer] Chamfer012
  Base = -> Pocket057 [Edge3]
  BaseFeature = -> Pocket057
  Size = 2
FEATURE [PartDesign::Plane] DatumPlane017
  Length = 24
  MapMode = 2
  ResizeMode = 0
  Width = 24
FEATURE [Part::Part2DObjectPython] ShapeString  # Draft 2D object (typed FeaturePython)
  FontFile = <path>
  Placement = pos=(-4.10626,-5.25224,0) rot=(0,0,1;0rad)
  Size = 5
  String = T
  Tracking = 0
FEATURE [PartDesign::Body] Body028
  Group = -> [Sketch088,Pad043,Sketch089,Pocket056,Sketch090,Pocket057,Chamfer012,DatumPlane017,ShapeString]
  Origin = -> Origin028
  Tip = -> Chamfer012
FEATURE [Part::Extrusion] Extrusion
  Base = -> ShapeString
  Dir = (0,0,2)
  DirMode = 0
  FaceMakerClass = Part::FaceMakerBullseye
  LengthFwd = 0
  LengthRev = 0
  Placement = pos=(0,0,18) rot=(0,0,1;0rad)
  Solid = true
  Symmetric = false
FEATURE [Part::Cut] Cut  label="TweeterKnopf"
  Base = -> Body028
  Placement = pos=(80,-65,308) rot=(0,0,1;0rad)
  Tool = -> Extrusion
FEATURE [Sketcher::SketchObject] Sketch091
  MapMode = 5
  Support = -> [XY_Plane029]
  sketch-geometry (1):
    g0: Circle CenterX=0 CenterY=0 CenterZ=0 NormalX=0 NormalY=0 NormalZ=1 AngleXU=0 Radius=10
  constraints (2):
    c: Coincident(g0,g-1)
    c: Diameter(g0) = 20
FEATURE [PartDesign::Pad] Pad044
  Length = 20
  Length2 = 100
  Profile = -> Sketch091
  Type = 0
FEATURE [Sketcher::SketchObject] Sketch093
  MapMode = 5
  Placement = pos=(0,0,0) rot=(1,0,0;3.14159rad)
  Support = -> [Pad044]
  sketch-geometry (1):
    g0: Circle CenterX=0 CenterY=0 CenterZ=0 NormalX=0 NormalY=0 NormalZ=1 AngleXU=0 Radius=6.5
  constraints (2):
    c: Coincident(g0,g-1)
    c: Diameter(g0) = 13
FEATURE [PartDesign::Pocket] Pocket058
  BaseFeature = -> Pad044
  Length = 5
  Length2 = 100
  Profile = -> Sketch093
  Type = 0
FEATURE [Sketcher::SketchObject] Sketch092
  MapMode = 5
  Placement = pos=(0,0,5) rot=(1,0,0;3.14159rad)
  Support = -> [Pocket058]
  sketch-geometry (1):
    g0: Circle CenterX=0 CenterY=0 CenterZ=0 NormalX=0 NormalY=0 NormalZ=1 AngleXU=0 Radius=3.125
  constraints (2):
    c: Coincident(g0,g-1)
    c: Diameter(g0) = 6.25
FEATURE [PartDesign::Pocket] Pocket059
  BaseFeature = -> Pocket058
  Length = 10
  Length2 = 100
  Profile = -> Sketch092
  Type = 0
FEATURE [PartDesign::Chamfer] Chamfer013
  Base = -> Pocket059 [Edge3]
  BaseFeature = -> Pocket059
  Size = 2
FEATURE [PartDesign::Plane] DatumPlane018
  Length = 24
  MapMode = 2
  ResizeMode = 0
  Width = 24
FEATURE [Part::Part2DObjectPython] ShapeString001  # Draft 2D object (typed FeaturePython)
  FontFile = <path>
  Placement = pos=(-6.2,-4.56,0.11) rot=(0,0,1;0rad)
  Size = 5
  String = M
  Tracking = 0
FEATURE [PartDesign::Body] Body029
  Group = -> [Sketch091,Pad044,Sketch093,Pocket058,Sketch092,Pocket059,Chamfer013,DatumPlane018,ShapeString001]
  Origin = -> Origin029
  Tip = -> Chamfer013
FEATURE [Part::Extrusion] Extrusion001
  Base = -> ShapeString001
  Dir = (0,0,2)
  DirMode = 0
  FaceMakerClass = Part::FaceMakerBullseye
  LengthFwd = 0
  LengthRev = 0
  Placement = pos=(0,0,18) rot=(0,0,1;0rad)
  Solid = true
  Symmetric = false
FEATURE [Part::Cut] Cut001  label="MiddleKnopf"
  Base = -> Body029
  Placement = pos=(55,-65,308) rot=(0,0,1;0rad)
  Tool = -> Extrusion001
FEATURE [Sketcher::SketchObject] Sketch094
  MapMode = 5
  Support = -> [XY_Plane030]
  sketch-geometry (1):
    g0: Circle CenterX=0 CenterY=0 CenterZ=0 NormalX=0 NormalY=0 NormalZ=1 AngleXU=0 Radius=10
  constraints (2):
    c: Coincident(g0,g-1)
    c: Diameter(g0) = 20
FEATURE [PartDesign::Pad] Pad045
  Length = 20
  Length2 = 100
  Profile = -> Sketch094
  Type = 0
FEATURE [Sketcher::SketchObject] Sketch096
  MapMode = 5
  Placement = pos=(0,0,0) rot=(1,0,0;3.14159rad)
  Support = -> [Pad045]
  sketch-geometry (1):
    g0: Circle CenterX=0 CenterY=0 CenterZ=0 NormalX=0 NormalY=0 NormalZ=1 AngleXU=0 Radius=6.5
  constraints (2):
    c: Coincident(g0,g-1)
    c: Diameter(g0) = 13
FEATURE [PartDesign::Pocket] Pocket060
  BaseFeature = -> Pad045
  Length = 5
  Length2 = 100
  Profile = -> Sketch096
  Type = 0
FEATURE [Sketcher::SketchObject] Sketch095
  MapMode = 5
  Placement = pos=(0,0,5) rot=(1,0,0;3.14159rad)
  Support = -> [Pocket060]
  sketch-geometry (1):
    g0: Circle CenterX=0 CenterY=0 CenterZ=0 NormalX=0 NormalY=0 NormalZ=1 AngleXU=0 Radius=3.125
  constraints (2):
    c: Coincident(g0,g-1)
    c: Diameter(g0) = 6.25
FEATURE [PartDesign::Plane] DatumPlane019
  Length = 24
  MapMode = 2
  ResizeMode = 0
  Width = 24
FEATURE [Part::Part2DObjectPython] ShapeString002  # Draft 2D object (typed FeaturePython)
  FontFile = <path>
  Placement = pos=(-4.2,-4.56,0.11) rot=(0,0,1;0rad)
  Size = 5
  String = B
  Tracking = 0
FEATURE [Part::Extrusion] Extrusion002
  Base = -> ShapeString002
  Dir = (0,0,2)
  DirMode = 0
  FaceMakerClass = Part::FaceMakerBullseye
  LengthFwd = 0
  LengthRev = 0
  Placement = pos=(0,0,18) rot=(0,0,1;0rad)
  Solid = true
  Symmetric = false
FEATURE [PartDesign::Pocket] Pocket061
  BaseFeature = -> Pocket060
  Length = 10
  Length2 = 100
  Profile = -> Sketch095
  Type = 0
FEATURE [PartDesign::Chamfer] Chamfer014
  Base = -> Pocket061 [Edge3]
  BaseFeature = -> Pocket061
  Size = 2
FEATURE [PartDesign::Body] Body030
  Group = -> [Sketch094,Pad045,Sketch096,Pocket060,Sketch095,Pocket061,Chamfer014,DatumPlane019,ShapeString002]
  Origin = -> Origin030
  Tip = -> Chamfer014
FEATURE [Part::Cut] Cut002  label="BassKnopf"
  Base = -> Body030
  Placement = pos=(30,-65,308) rot=(0,0,1;0rad)
  Tool = -> Extrusion002
FEATURE [Part::Part2DObjectPython] ShapeString003  # Draft 2D object (typed FeaturePython)
  FontFile = <path>
  Placement = pos=(-5.2,-4.56,0.11) rot=(0,0,1;0rad)
  Size = 5
  String = G
  Tracking = 0
FEATURE [Sketcher::SketchObject] Sketch098
  MapMode = 5
  Support = -> [XY_Plane031]
  sketch-geometry (1):
    g0: Circle CenterX=0 CenterY=0 CenterZ=0 NormalX=0 NormalY=0 NormalZ=1 AngleXU=0 Radius=10
  constraints (2):
    c: Coincident(g0,g-1)
    c: Diameter(g0) = 20
FEATURE [PartDesign::Pad] Pad046
  Length = 20
  Length2 = 100
  Profile = -> Sketch098
  Type = 0
FEATURE [Part::Extrusion] Extrusion003
  Base = -> ShapeString003
  Dir = (0,0,2)
  DirMode = 0
  FaceMakerClass = Part::FaceMakerBullseye
  LengthFwd = 0
  LengthRev = 0
  Placement = pos=(0,0,18) rot=(0,0,1;0rad)
  Solid = true
  Symmetric = false
FEATURE [Sketcher::SketchObject] Sketch099
  MapMode = 5
  Placement = pos=(0,0,0) rot=(1,0,0;3.14159rad)
  Support = -> [Pad046]
  sketch-geometry (1):
    g0: Circle CenterX=0 CenterY=0 CenterZ=0 NormalX=0 NormalY=0 NormalZ=1 AngleXU=0 Radius=6.5
  constraints (2):
    c: Coincident(g0,g-1)
    c: Diameter(g0) = 13
FEATURE [PartDesign::Pocket] Pocket062
  BaseFeature = -> Pad046
  Length = 5
  Length2 = 100
  Profile = -> Sketch099
  Type = 0
FEATURE [Sketcher::SketchObject] Sketch097
  MapMode = 5
  Placement = pos=(0,0,5) rot=(1,0,0;3.14159rad)
  Support = -> [Pocket062]
  sketch-geometry (1):
    g0: Circle CenterX=0 CenterY=0 CenterZ=0 NormalX=0 NormalY=0 NormalZ=1 AngleXU=0 Radius=3.125
  constraints (2):
    c: Coincident(g0,g-1)
    c: Diameter(g0) = 6.25
FEATURE [PartDesign::Pocket] Pocket063
  BaseFeature = -> Pocket062
  Length = 10
  Length2 = 100
  Profile = -> Sketch097
  Type = 0
FEATURE [PartDesign::Chamfer] Chamfer015
  Base = -> Pocket063 [Edge3]
  BaseFeature = -> Pocket063
  Size = 2
FEATURE [PartDesign::Plane] DatumPlane020
  Length = 24
  MapMode = 2
  ResizeMode = 0
  Width = 24
FEATURE [PartDesign::Body] Body031
  Group = -> [Sketch098,Pad046,Sketch099,Pocket062,Sketch097,Pocket063,Chamfer015,DatumPlane020,ShapeString003]
  Origin = -> Origin031
  Tip = -> Chamfer015
FEATURE [Part::Cut] Cut003  label="GainKnopf"
  Base = -> Body031
  Placement = pos=(-80,-65,308) rot=(0,0,1;0rad)
  Tool = -> Extrusion003
FEATURE [Sketcher::SketchObject] Sketch100
  MapMode = 5
  Support = -> [XY_Plane032]
  sketch-geometry (14):
    g0: LineSegment [constr] StartX=0 StartY=47.5 StartZ=0 EndX=-95 EndY=47.5 EndZ=0
    g1: LineSegment [constr] StartX=-95 StartY=47.5 StartZ=0 EndX=-95 EndY=-47.5 EndZ=0
    g2: LineSegment [constr] StartX=-95 StartY=-47.5 StartZ=0 EndX=0 EndY=-47.5 EndZ=0
    g3: LineSegment [constr] StartX=0 StartY=45 StartZ=0 EndX=-75 EndY=45 EndZ=0
    g4: LineSegment [constr] StartX=-75 StartY=45 StartZ=0 EndX=-75 EndY=-45 EndZ=0
    g5: LineSegment [constr] StartX=-75 StartY=-45 StartZ=0 EndX=0 EndY=-45 EndZ=0
    g6: LineSegment StartX=-105 StartY=55 StartZ=0 EndX=-69 EndY=55 EndZ=0
    g7: LineSegment StartX=-69 StartY=55 StartZ=0 EndX=-69 EndY=39 EndZ=0
    g8: LineSegment StartX=-69 StartY=39 StartZ=0 EndX=-85 EndY=39 EndZ=0
    g9: LineSegment StartX=-85 StartY=39 StartZ=0 EndX=-85 EndY=-39 EndZ=0
    g10: LineSegment StartX=-85 StartY=-39 StartZ=0 EndX=-69 EndY=-39 EndZ=0
    g11: LineSegment StartX=-69 StartY=-39 StartZ=0 EndX=-69 EndY=-55 EndZ=0
    g12: LineSegment StartX=-69 StartY=-55 StartZ=0 EndX=-105 EndY=-55 EndZ=0
    g13: LineSegment StartX=-105 StartY=-55 StartZ=0 EndX=-105 EndY=55 EndZ=0
  constraints (40):
    c: PointOnObject(g0,g-2)
    c: Horizontal(g0)
    c: Coincident(g1,g0)
    c: Coincident(g2,g1)
    c: Horizontal(g2)
    c: DistanceX(g0,g0) = 95
    c: Equal(g2,g1)
    c: Equal(g1,g0)
    c: Symmetric(g2,g0,g-1)
    c: PointOnObject(g3,g-2)
    c: Horizontal(g3)
    c: Coincident(g4,g3)
    c: Coincident(g5,g4)
    c: Horizontal(g5)
    c: Equal(g5,g3)
    c: Symmetric(g5,g3,g-1)
    c: DistanceY(g4,g4) = 90
    c: Horizontal(g6)
    c: Coincident(g6,g7)
    c: Vertical(g7)
    c: Coincident(g7,g8)
    c: Horizontal(g8)
    c: Coincident(g8,g9)
    c: Vertical(g9)
    c: Coincident(g9,g10)
    c: Horizontal(g10)
    c: Coincident(g10,g11)
    c: Vertical(g11)
    c: Coincident(g11,g12)
    c: Horizontal(g12)
    c: Coincident(g12,g13)
    c: Coincident(g13,g6)
    c: DistanceY(g13,g13) = 110
    c: Symmetric(g6,g12,g-1)
    c: Symmetric(g7,g10,g-1)
    c: DistanceY(g4,g10) = 6
    c: DistanceX(g4,g10) = 6
    c: DistanceX(g5,g5) = 75
    c: DistanceX(g6,g8) = 20
    c: DistanceX(g6,g0) = 10
FEATURE [PartDesign::Pad] Pad047
  Length = 7
  Length2 = 100
  Profile = -> Sketch100
  Type = 0
FEATURE [Sketcher::SketchObject] Sketch101
  ExternalGeometry = -> [Pad047]
  MapMode = 5
  Placement = pos=(0,0,7) rot=(0,0,1;0rad)
  Support = -> [Pad047]
  sketch-geometry (2):
    g0: Circle CenterX=-95 CenterY=47.5 CenterZ=0 NormalX=0 NormalY=0 NormalZ=1 AngleXU=0 Radius=2
    g1: Circle CenterX=-95 CenterY=-47.5 CenterZ=0 NormalX=0 NormalY=0 NormalZ=1 AngleXU=0 Radius=2
  constraints (5):
    c: Equal(g1,g0)
    c: Radius(g0) = 2
    c: DistanceX(g-3,g0) = 10
    c: Symmetric(g0,g1,g-1)
    c: DistanceY(g1,g0) = 95
FEATURE [PartDesign::Body] Body032  label="PlatinenHalter"
  Group = -> [Sketch100,Pad047,Sketch101]
  Origin = -> Origin032
  Tip = -> Pad047
note: 4 file-system paths scrubbed to <path> (originals preserved in the JSON sidecar)
